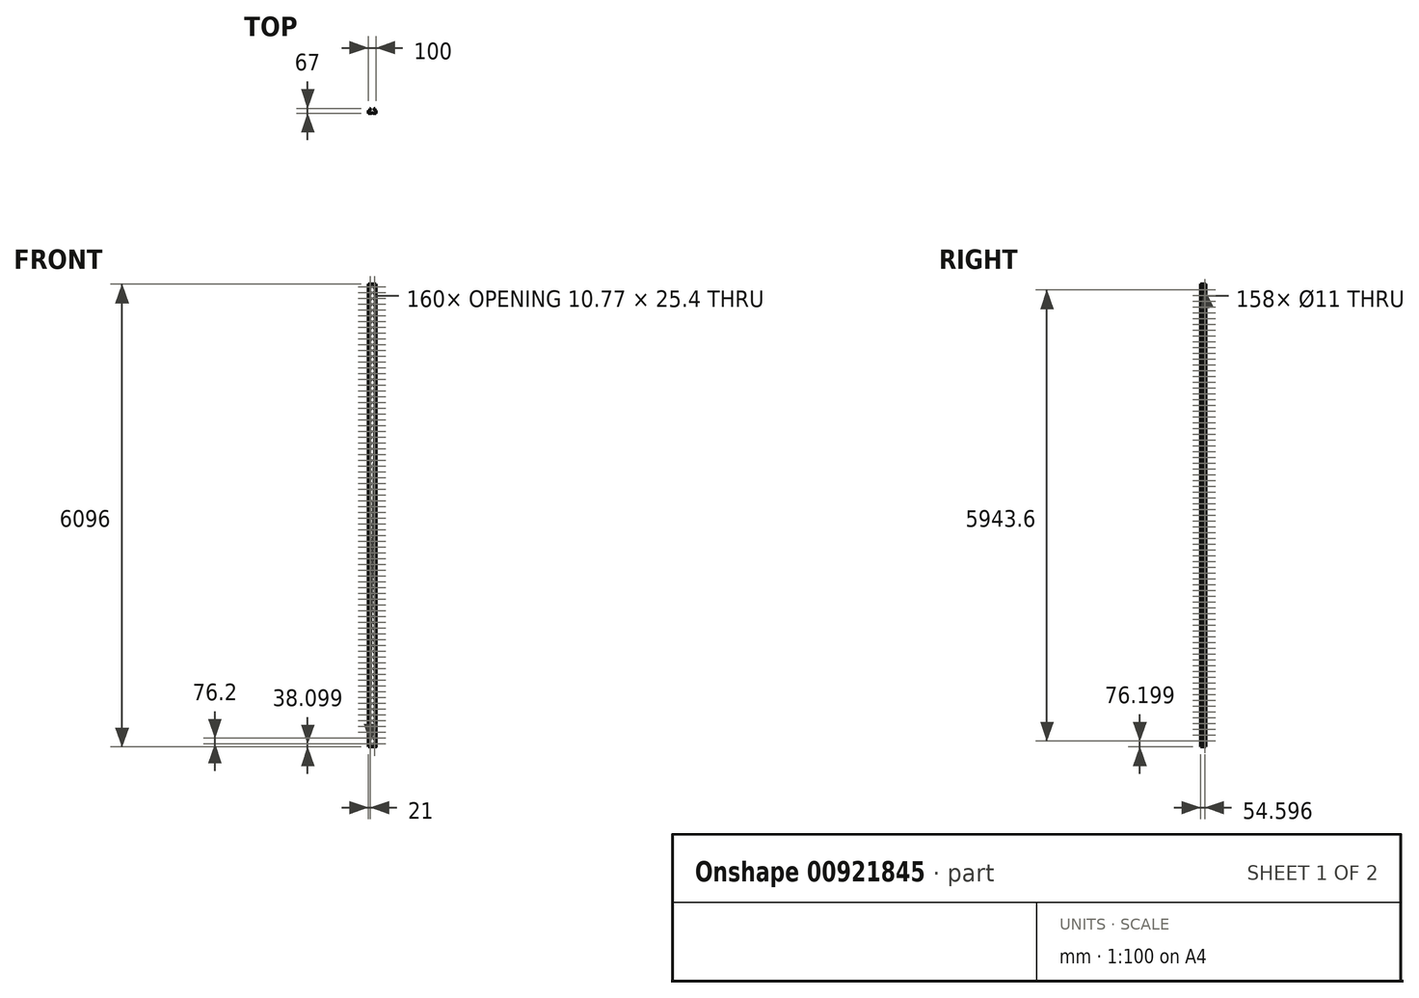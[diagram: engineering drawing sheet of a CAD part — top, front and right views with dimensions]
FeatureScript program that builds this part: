
annotation { "Feature Type Name" : "Feature", "Feature Type Description" : "" }
export const myFeature = defineFeature(function(context is Context, id is Id, definition is map)
    precondition{}
    {
        {
            var Q0;
            Q0=qCreatedBy(makeId("Top.planeOp"),FACE);
            var sketch = newSketch(context, id + "F0", { "sketchPlane" : qUnion([Q0])});
            skLineSegment(sketch, "E0", {"start": v(133.85, 104.26) * mm, "end": v(133.85, 405.9) * mm});
            skLineSegment(sketch, "E1", {"start": v(129.85, 104.03) * mm, "end": v(129.85, 405.9) * mm});
            skLineSegment(sketch, "E2", {"start": v(96.7, -203.7) * mm, "end": v(96.7, 405.9) * mm});
            skLineSegment(sketch, "E3", {"start": v(93.87, -203.7) * mm, "end": v(93.87, 405.9) * mm});
            skLineSegment(sketch, "E4", {"start": v(88.87, 103.15) * mm, "end": v(88.87, 405.9) * mm});
            skLineSegment(sketch, "E5", {"start": v(86.87, 103.6) * mm, "end": v(86.87, 405.9) * mm});
            skLineSegment(sketch, "E6", {"start": v(70.87, -203.7) * mm, "end": v(70.87, 405.9) * mm});
            skLineSegment(sketch, "E7", {"start": v(68.87, -203.7) * mm, "end": v(68.87, 405.9) * mm});
            skLineSegment(sketch, "E8", {"start": v(-161.67, -203.7) * mm, "end": v(-161.67, 405.9) * mm});
            skLineSegment(sketch, "E9", {"start": v(-165.67, -203.7) * mm, "end": v(-165.67, 405.9) * mm});
            skLineSegment(sketch, "E10", {"start": v(-122.17, -203.7) * mm, "end": v(-122.17, 405.9) * mm});
            skLineSegment(sketch, "E11", {"start": v(-125.67, -203.7) * mm, "end": v(-125.67, 405.9) * mm});
            skLineSegment(sketch, "E12", {"start": v(-109.17, -203.7) * mm, "end": v(-109.17, 405.9) * mm});
            skLineSegment(sketch, "E13", {"start": v(-105.67, -203.7) * mm, "end": v(-105.67, 405.9) * mm});
            skLineSegment(sketch, "E14", {"start": v(-69.67, -203.7) * mm, "end": v(-69.67, 405.9) * mm});
            skLineSegment(sketch, "E15", {"start": v(-65.67, -203.7) * mm, "end": v(-65.67, 405.9) * mm});
            skLineSegment(sketch, "E16", {"start": v(-165.67, -203.7) * mm, "end": v(-65.67, -203.7) * mm});
            skLineSegment(sketch, "E17", {"start": v(-140.6, 355.3) * mm, "end": v(-140.6, 357.1) * mm});
            skArc(sketch, "E18", {"start": v(-140.8, 355.1) * mm, "mid": v(-140.66, 355.17) * mm, "end": v(-140.6, 355.3) * mm});
            skLineSegment(sketch, "E19", {"start": v(-148.54, 355.1) * mm, "end": v(-140.8, 355.1) * mm});
            skArc(sketch, "E20", {"start": v(-148.74, 355.3) * mm, "mid": v(-148.68, 355.17) * mm, "end": v(-148.54, 355.1) * mm});
            skLineSegment(sketch, "E21", {"start": v(-148.74, 357.1) * mm, "end": v(-148.74, 355.3) * mm});
            skLineSegment(sketch, "E22", {"start": v(-150.06, 367.8) * mm, "end": v(-148.74, 357.1) * mm});
            skLineSegment(sketch, "E23", {"start": v(-148.74, 378.5) * mm, "end": v(-150.06, 367.8) * mm});
            skLineSegment(sketch, "E24", {"start": v(-148.74, 380.3) * mm, "end": v(-148.74, 378.5) * mm});
            skArc(sketch, "E25", {"start": v(-148.54, 380.5) * mm, "mid": v(-148.68, 380.45) * mm, "end": v(-148.74, 380.3) * mm});
            skLineSegment(sketch, "E26", {"start": v(-140.8, 380.5) * mm, "end": v(-148.54, 380.5) * mm});
            skArc(sketch, "E27", {"start": v(-140.6, 380.3) * mm, "mid": v(-140.66, 380.45) * mm, "end": v(-140.8, 380.5) * mm});
            skLineSegment(sketch, "E28", {"start": v(-140.6, 378.5) * mm, "end": v(-140.6, 380.3) * mm});
            skLineSegment(sketch, "E29", {"start": v(-139.29, 367.8) * mm, "end": v(-140.6, 378.5) * mm});
            skLineSegment(sketch, "E30", {"start": v(-140.6, 357.1) * mm, "end": v(-139.29, 367.8) * mm});
            skLineSegment(sketch, "E31", {"start": v(-140.6, 279.1) * mm, "end": v(-140.6, 280.9) * mm});
            skArc(sketch, "E32", {"start": v(-140.8, 278.9) * mm, "mid": v(-140.66, 278.97) * mm, "end": v(-140.6, 279.1) * mm});
            skLineSegment(sketch, "E33", {"start": v(-148.54, 278.9) * mm, "end": v(-140.8, 278.9) * mm});
            skArc(sketch, "E34", {"start": v(-148.74, 279.1) * mm, "mid": v(-148.68, 278.97) * mm, "end": v(-148.54, 278.9) * mm});
            skLineSegment(sketch, "E35", {"start": v(-148.74, 280.9) * mm, "end": v(-148.74, 279.1) * mm});
            skLineSegment(sketch, "E36", {"start": v(-150.06, 291.6) * mm, "end": v(-148.74, 280.9) * mm});
            skLineSegment(sketch, "E37", {"start": v(-148.74, 302.3) * mm, "end": v(-150.06, 291.6) * mm});
            skLineSegment(sketch, "E38", {"start": v(-148.74, 304.1) * mm, "end": v(-148.74, 302.3) * mm});
            skArc(sketch, "E39", {"start": v(-148.54, 304.3) * mm, "mid": v(-148.68, 304.25) * mm, "end": v(-148.74, 304.1) * mm});
            skLineSegment(sketch, "E40", {"start": v(-140.8, 304.3) * mm, "end": v(-148.54, 304.3) * mm});
            skArc(sketch, "E41", {"start": v(-140.6, 304.1) * mm, "mid": v(-140.66, 304.25) * mm, "end": v(-140.8, 304.3) * mm});
            skLineSegment(sketch, "E42", {"start": v(-140.6, 302.3) * mm, "end": v(-140.6, 304.1) * mm});
            skLineSegment(sketch, "E43", {"start": v(-139.29, 291.6) * mm, "end": v(-140.6, 302.3) * mm});
            skLineSegment(sketch, "E44", {"start": v(-140.6, 280.9) * mm, "end": v(-139.29, 291.6) * mm});
            skLineSegment(sketch, "E45", {"start": v(-140.6, 202.9) * mm, "end": v(-140.6, 204.7) * mm});
            skArc(sketch, "E46", {"start": v(-140.8, 202.7) * mm, "mid": v(-140.66, 202.77) * mm, "end": v(-140.6, 202.9) * mm});
            skLineSegment(sketch, "E47", {"start": v(-148.54, 202.7) * mm, "end": v(-140.8, 202.7) * mm});
            skArc(sketch, "E48", {"start": v(-148.74, 202.9) * mm, "mid": v(-148.68, 202.77) * mm, "end": v(-148.54, 202.7) * mm});
            skLineSegment(sketch, "E49", {"start": v(-148.74, 204.7) * mm, "end": v(-148.74, 202.9) * mm});
            skLineSegment(sketch, "E50", {"start": v(-150.06, 215.4) * mm, "end": v(-148.74, 204.7) * mm});
            skLineSegment(sketch, "E51", {"start": v(-148.74, 226.1) * mm, "end": v(-150.06, 215.4) * mm});
            skLineSegment(sketch, "E52", {"start": v(-148.74, 227.9) * mm, "end": v(-148.74, 226.1) * mm});
            skArc(sketch, "E53", {"start": v(-148.54, 228.1) * mm, "mid": v(-148.68, 228.05) * mm, "end": v(-148.74, 227.9) * mm});
            skLineSegment(sketch, "E54", {"start": v(-140.8, 228.1) * mm, "end": v(-148.54, 228.1) * mm});
            skArc(sketch, "E55", {"start": v(-140.6, 227.9) * mm, "mid": v(-140.66, 228.05) * mm, "end": v(-140.8, 228.1) * mm});
            skLineSegment(sketch, "E56", {"start": v(-140.6, 226.1) * mm, "end": v(-140.6, 227.9) * mm});
            skLineSegment(sketch, "E57", {"start": v(-139.29, 215.4) * mm, "end": v(-140.6, 226.1) * mm});
            skLineSegment(sketch, "E58", {"start": v(-140.6, 204.7) * mm, "end": v(-139.29, 215.4) * mm});
            skLineSegment(sketch, "E59", {"start": v(-140.6, 126.7) * mm, "end": v(-140.6, 128.5) * mm});
            skArc(sketch, "E60", {"start": v(-140.8, 126.5) * mm, "mid": v(-140.66, 126.57) * mm, "end": v(-140.6, 126.7) * mm});
            skLineSegment(sketch, "E61", {"start": v(-148.54, 126.5) * mm, "end": v(-140.8, 126.5) * mm});
            skArc(sketch, "E62", {"start": v(-148.74, 126.7) * mm, "mid": v(-148.68, 126.57) * mm, "end": v(-148.54, 126.5) * mm});
            skLineSegment(sketch, "E63", {"start": v(-148.74, 128.5) * mm, "end": v(-148.74, 126.7) * mm});
            skLineSegment(sketch, "E64", {"start": v(-150.06, 139.2) * mm, "end": v(-148.74, 128.5) * mm});
            skLineSegment(sketch, "E65", {"start": v(-148.74, 149.9) * mm, "end": v(-150.06, 139.2) * mm});
            skLineSegment(sketch, "E66", {"start": v(-148.74, 151.7) * mm, "end": v(-148.74, 149.9) * mm});
            skArc(sketch, "E67", {"start": v(-148.54, 151.9) * mm, "mid": v(-148.68, 151.85) * mm, "end": v(-148.74, 151.7) * mm});
            skLineSegment(sketch, "E68", {"start": v(-140.8, 151.9) * mm, "end": v(-148.54, 151.9) * mm});
            skArc(sketch, "E69", {"start": v(-140.6, 151.7) * mm, "mid": v(-140.66, 151.85) * mm, "end": v(-140.8, 151.9) * mm});
            skLineSegment(sketch, "E70", {"start": v(-140.6, 149.9) * mm, "end": v(-140.6, 151.7) * mm});
            skLineSegment(sketch, "E71", {"start": v(-139.29, 139.2) * mm, "end": v(-140.6, 149.9) * mm});
            skLineSegment(sketch, "E72", {"start": v(-140.6, 128.5) * mm, "end": v(-139.29, 139.2) * mm});
            skLineSegment(sketch, "E73", {"start": v(-140.6, 50.5) * mm, "end": v(-140.6, 52.3) * mm});
            skArc(sketch, "E74", {"start": v(-140.8, 50.3) * mm, "mid": v(-140.66, 50.37) * mm, "end": v(-140.6, 50.5) * mm});
            skLineSegment(sketch, "E75", {"start": v(-148.54, 50.3) * mm, "end": v(-140.8, 50.3) * mm});
            skArc(sketch, "E76", {"start": v(-148.74, 50.5) * mm, "mid": v(-148.68, 50.37) * mm, "end": v(-148.54, 50.3) * mm});
            skLineSegment(sketch, "E77", {"start": v(-148.74, 52.3) * mm, "end": v(-148.74, 50.5) * mm});
            skLineSegment(sketch, "E78", {"start": v(-150.06, 63) * mm, "end": v(-148.74, 52.3) * mm});
            skLineSegment(sketch, "E79", {"start": v(-148.74, 73.7) * mm, "end": v(-150.06, 63) * mm});
            skLineSegment(sketch, "E80", {"start": v(-148.74, 75.5) * mm, "end": v(-148.74, 73.7) * mm});
            skArc(sketch, "E81", {"start": v(-148.54, 75.7) * mm, "mid": v(-148.68, 75.65) * mm, "end": v(-148.74, 75.5) * mm});
            skLineSegment(sketch, "E82", {"start": v(-140.8, 75.7) * mm, "end": v(-148.54, 75.7) * mm});
            skArc(sketch, "E83", {"start": v(-140.6, 75.5) * mm, "mid": v(-140.66, 75.65) * mm, "end": v(-140.8, 75.7) * mm});
            skLineSegment(sketch, "E84", {"start": v(-140.6, 73.7) * mm, "end": v(-140.6, 75.5) * mm});
            skLineSegment(sketch, "E85", {"start": v(-139.29, 63) * mm, "end": v(-140.6, 73.7) * mm});
            skLineSegment(sketch, "E86", {"start": v(-140.6, 52.3) * mm, "end": v(-139.29, 63) * mm});
            skLineSegment(sketch, "E87", {"start": v(-140.6, -25.7) * mm, "end": v(-140.6, -23.9) * mm});
            skArc(sketch, "E88", {"start": v(-140.8, -25.9) * mm, "mid": v(-140.66, -25.83) * mm, "end": v(-140.6, -25.7) * mm});
            skLineSegment(sketch, "E89", {"start": v(-148.54, -25.9) * mm, "end": v(-140.8, -25.9) * mm});
            skArc(sketch, "E90", {"start": v(-148.74, -25.7) * mm, "mid": v(-148.68, -25.83) * mm, "end": v(-148.54, -25.9) * mm});
            skLineSegment(sketch, "E91", {"start": v(-148.74, -23.9) * mm, "end": v(-148.74, -25.7) * mm});
            skLineSegment(sketch, "E92", {"start": v(-150.06, -13.2) * mm, "end": v(-148.74, -23.9) * mm});
            skLineSegment(sketch, "E93", {"start": v(-148.74, -2.5) * mm, "end": v(-150.06, -13.2) * mm});
            skLineSegment(sketch, "E94", {"start": v(-148.74, -0.7) * mm, "end": v(-148.74, -2.5) * mm});
            skArc(sketch, "E95", {"start": v(-148.54, -0.5) * mm, "mid": v(-148.68, -0.55) * mm, "end": v(-148.74, -0.7) * mm});
            skLineSegment(sketch, "E96", {"start": v(-140.8, -0.5) * mm, "end": v(-148.54, -0.5) * mm});
            skArc(sketch, "E97", {"start": v(-140.6, -0.7) * mm, "mid": v(-140.66, -0.55) * mm, "end": v(-140.8, -0.5) * mm});
            skLineSegment(sketch, "E98", {"start": v(-140.6, -2.5) * mm, "end": v(-140.6, -0.7) * mm});
            skLineSegment(sketch, "E99", {"start": v(-139.29, -13.2) * mm, "end": v(-140.6, -2.5) * mm});
            skLineSegment(sketch, "E100", {"start": v(-140.6, -23.9) * mm, "end": v(-139.29, -13.2) * mm});
            skLineSegment(sketch, "E101", {"start": v(-140.6, -101.9) * mm, "end": v(-140.6, -100.1) * mm});
            skArc(sketch, "E102", {"start": v(-140.8, -102.1) * mm, "mid": v(-140.66, -102.03) * mm, "end": v(-140.6, -101.9) * mm});
            skLineSegment(sketch, "E103", {"start": v(-148.54, -102.1) * mm, "end": v(-140.8, -102.1) * mm});
            skArc(sketch, "E104", {"start": v(-148.74, -101.9) * mm, "mid": v(-148.68, -102.03) * mm, "end": v(-148.54, -102.1) * mm});
            skLineSegment(sketch, "E105", {"start": v(-148.74, -100.1) * mm, "end": v(-148.74, -101.9) * mm});
            skLineSegment(sketch, "E106", {"start": v(-150.06, -89.4) * mm, "end": v(-148.74, -100.1) * mm});
            skLineSegment(sketch, "E107", {"start": v(-148.74, -78.7) * mm, "end": v(-150.06, -89.4) * mm});
            skLineSegment(sketch, "E108", {"start": v(-148.74, -76.9) * mm, "end": v(-148.74, -78.7) * mm});
            skArc(sketch, "E109", {"start": v(-148.54, -76.7) * mm, "mid": v(-148.68, -76.75) * mm, "end": v(-148.74, -76.9) * mm});
            skLineSegment(sketch, "E110", {"start": v(-140.8, -76.7) * mm, "end": v(-148.54, -76.7) * mm});
            skArc(sketch, "E111", {"start": v(-140.6, -76.9) * mm, "mid": v(-140.66, -76.75) * mm, "end": v(-140.8, -76.7) * mm});
            skLineSegment(sketch, "E112", {"start": v(-140.6, -78.7) * mm, "end": v(-140.6, -76.9) * mm});
            skLineSegment(sketch, "E113", {"start": v(-139.29, -89.4) * mm, "end": v(-140.6, -78.7) * mm});
            skLineSegment(sketch, "E114", {"start": v(-140.6, -100.1) * mm, "end": v(-139.29, -89.4) * mm});
            skLineSegment(sketch, "E115", {"start": v(-140.6, -178.1) * mm, "end": v(-140.6, -176.3) * mm});
            skArc(sketch, "E116", {"start": v(-140.8, -178.3) * mm, "mid": v(-140.66, -178.23) * mm, "end": v(-140.6, -178.1) * mm});
            skLineSegment(sketch, "E117", {"start": v(-148.54, -178.3) * mm, "end": v(-140.8, -178.3) * mm});
            skArc(sketch, "E118", {"start": v(-148.74, -178.1) * mm, "mid": v(-148.68, -178.23) * mm, "end": v(-148.54, -178.3) * mm});
            skLineSegment(sketch, "E119", {"start": v(-148.74, -176.3) * mm, "end": v(-148.74, -178.1) * mm});
            skLineSegment(sketch, "E120", {"start": v(-150.06, -165.6) * mm, "end": v(-148.74, -176.3) * mm});
            skLineSegment(sketch, "E121", {"start": v(-148.74, -154.9) * mm, "end": v(-150.06, -165.6) * mm});
            skLineSegment(sketch, "E122", {"start": v(-148.74, -153.1) * mm, "end": v(-148.74, -154.9) * mm});
            skArc(sketch, "E123", {"start": v(-148.54, -152.9) * mm, "mid": v(-148.68, -152.95) * mm, "end": v(-148.74, -153.1) * mm});
            skLineSegment(sketch, "E124", {"start": v(-140.8, -152.9) * mm, "end": v(-148.54, -152.9) * mm});
            skArc(sketch, "E125", {"start": v(-140.6, -153.1) * mm, "mid": v(-140.66, -152.95) * mm, "end": v(-140.8, -152.9) * mm});
            skLineSegment(sketch, "E126", {"start": v(-140.6, -154.9) * mm, "end": v(-140.6, -153.1) * mm});
            skLineSegment(sketch, "E127", {"start": v(-139.29, -165.6) * mm, "end": v(-140.6, -154.9) * mm});
            skLineSegment(sketch, "E128", {"start": v(-140.6, -176.3) * mm, "end": v(-139.29, -165.6) * mm});
            skArc(sketch, "E129", {"start": v(-90.74, -178.1) * mm, "mid": v(-90.68, -178.23) * mm, "end": v(-90.54, -178.3) * mm});
            skLineSegment(sketch, "E130", {"start": v(-90.74, -176.3) * mm, "end": v(-90.74, -178.1) * mm});
            skLineSegment(sketch, "E131", {"start": v(-92.06, -165.6) * mm, "end": v(-90.74, -176.3) * mm});
            skLineSegment(sketch, "E132", {"start": v(-90.74, -154.9) * mm, "end": v(-92.06, -165.6) * mm});
            skLineSegment(sketch, "E133", {"start": v(-90.74, -153.1) * mm, "end": v(-90.74, -154.9) * mm});
            skArc(sketch, "E134", {"start": v(-90.54, -152.9) * mm, "mid": v(-90.68, -152.95) * mm, "end": v(-90.74, -153.1) * mm});
            skLineSegment(sketch, "E135", {"start": v(-82.8, -152.9) * mm, "end": v(-90.54, -152.9) * mm});
            skArc(sketch, "E136", {"start": v(-82.6, -153.1) * mm, "mid": v(-82.66, -152.95) * mm, "end": v(-82.8, -152.9) * mm});
            skLineSegment(sketch, "E137", {"start": v(-82.6, -154.9) * mm, "end": v(-82.6, -153.1) * mm});
            skLineSegment(sketch, "E138", {"start": v(-81.29, -165.6) * mm, "end": v(-82.6, -154.9) * mm});
            skLineSegment(sketch, "E139", {"start": v(-82.6, -176.3) * mm, "end": v(-81.29, -165.6) * mm});
            skLineSegment(sketch, "E140", {"start": v(-82.6, -178.1) * mm, "end": v(-82.6, -176.3) * mm});
            skArc(sketch, "E141", {"start": v(-82.8, -178.3) * mm, "mid": v(-82.66, -178.23) * mm, "end": v(-82.6, -178.1) * mm});
            skLineSegment(sketch, "E142", {"start": v(-90.54, -178.3) * mm, "end": v(-82.8, -178.3) * mm});
            skArc(sketch, "E143", {"start": v(-90.74, -101.9) * mm, "mid": v(-90.68, -102.03) * mm, "end": v(-90.54, -102.1) * mm});
            skLineSegment(sketch, "E144", {"start": v(-90.74, -100.1) * mm, "end": v(-90.74, -101.9) * mm});
            skLineSegment(sketch, "E145", {"start": v(-92.06, -89.4) * mm, "end": v(-90.74, -100.1) * mm});
            skLineSegment(sketch, "E146", {"start": v(-90.74, -78.7) * mm, "end": v(-92.06, -89.4) * mm});
            skLineSegment(sketch, "E147", {"start": v(-90.74, -76.9) * mm, "end": v(-90.74, -78.7) * mm});
            skArc(sketch, "E148", {"start": v(-90.54, -76.7) * mm, "mid": v(-90.68, -76.75) * mm, "end": v(-90.74, -76.9) * mm});
            skLineSegment(sketch, "E149", {"start": v(-82.8, -76.7) * mm, "end": v(-90.54, -76.7) * mm});
            skArc(sketch, "E150", {"start": v(-82.6, -76.9) * mm, "mid": v(-82.66, -76.75) * mm, "end": v(-82.8, -76.7) * mm});
            skLineSegment(sketch, "E151", {"start": v(-82.6, -78.7) * mm, "end": v(-82.6, -76.9) * mm});
            skLineSegment(sketch, "E152", {"start": v(-81.29, -89.4) * mm, "end": v(-82.6, -78.7) * mm});
            skLineSegment(sketch, "E153", {"start": v(-82.6, -100.1) * mm, "end": v(-81.29, -89.4) * mm});
            skLineSegment(sketch, "E154", {"start": v(-82.6, -101.9) * mm, "end": v(-82.6, -100.1) * mm});
            skArc(sketch, "E155", {"start": v(-82.8, -102.1) * mm, "mid": v(-82.66, -102.03) * mm, "end": v(-82.6, -101.9) * mm});
            skLineSegment(sketch, "E156", {"start": v(-90.54, -102.1) * mm, "end": v(-82.8, -102.1) * mm});
            skArc(sketch, "E157", {"start": v(-90.74, -25.7) * mm, "mid": v(-90.68, -25.83) * mm, "end": v(-90.54, -25.9) * mm});
            skLineSegment(sketch, "E158", {"start": v(-90.74, -23.9) * mm, "end": v(-90.74, -25.7) * mm});
            skLineSegment(sketch, "E159", {"start": v(-92.06, -13.2) * mm, "end": v(-90.74, -23.9) * mm});
            skLineSegment(sketch, "E160", {"start": v(-90.74, -2.5) * mm, "end": v(-92.06, -13.2) * mm});
            skLineSegment(sketch, "E161", {"start": v(-90.74, -0.7) * mm, "end": v(-90.74, -2.5) * mm});
            skArc(sketch, "E162", {"start": v(-90.54, -0.5) * mm, "mid": v(-90.68, -0.55) * mm, "end": v(-90.74, -0.7) * mm});
            skLineSegment(sketch, "E163", {"start": v(-82.8, -0.5) * mm, "end": v(-90.54, -0.5) * mm});
            skArc(sketch, "E164", {"start": v(-82.6, -0.7) * mm, "mid": v(-82.66, -0.55) * mm, "end": v(-82.8, -0.5) * mm});
            skLineSegment(sketch, "E165", {"start": v(-82.6, -2.5) * mm, "end": v(-82.6, -0.7) * mm});
            skLineSegment(sketch, "E166", {"start": v(-81.29, -13.2) * mm, "end": v(-82.6, -2.5) * mm});
            skLineSegment(sketch, "E167", {"start": v(-82.6, -23.9) * mm, "end": v(-81.29, -13.2) * mm});
            skLineSegment(sketch, "E168", {"start": v(-82.6, -25.7) * mm, "end": v(-82.6, -23.9) * mm});
            skArc(sketch, "E169", {"start": v(-82.8, -25.9) * mm, "mid": v(-82.66, -25.83) * mm, "end": v(-82.6, -25.7) * mm});
            skLineSegment(sketch, "E170", {"start": v(-90.54, -25.9) * mm, "end": v(-82.8, -25.9) * mm});
            skArc(sketch, "E171", {"start": v(-90.74, 50.5) * mm, "mid": v(-90.68, 50.37) * mm, "end": v(-90.54, 50.3) * mm});
            skLineSegment(sketch, "E172", {"start": v(-90.74, 52.3) * mm, "end": v(-90.74, 50.5) * mm});
            skLineSegment(sketch, "E173", {"start": v(-92.06, 63) * mm, "end": v(-90.74, 52.3) * mm});
            skLineSegment(sketch, "E174", {"start": v(-90.74, 73.7) * mm, "end": v(-92.06, 63) * mm});
            skLineSegment(sketch, "E175", {"start": v(-90.74, 75.5) * mm, "end": v(-90.74, 73.7) * mm});
            skArc(sketch, "E176", {"start": v(-90.54, 75.7) * mm, "mid": v(-90.68, 75.65) * mm, "end": v(-90.74, 75.5) * mm});
            skLineSegment(sketch, "E177", {"start": v(-82.8, 75.7) * mm, "end": v(-90.54, 75.7) * mm});
            skArc(sketch, "E178", {"start": v(-82.6, 75.5) * mm, "mid": v(-82.66, 75.65) * mm, "end": v(-82.8, 75.7) * mm});
            skLineSegment(sketch, "E179", {"start": v(-82.6, 73.7) * mm, "end": v(-82.6, 75.5) * mm});
            skLineSegment(sketch, "E180", {"start": v(-81.29, 63) * mm, "end": v(-82.6, 73.7) * mm});
            skLineSegment(sketch, "E181", {"start": v(-82.6, 52.3) * mm, "end": v(-81.29, 63) * mm});
            skLineSegment(sketch, "E182", {"start": v(-82.6, 50.5) * mm, "end": v(-82.6, 52.3) * mm});
            skArc(sketch, "E183", {"start": v(-82.8, 50.3) * mm, "mid": v(-82.66, 50.37) * mm, "end": v(-82.6, 50.5) * mm});
            skLineSegment(sketch, "E184", {"start": v(-90.54, 50.3) * mm, "end": v(-82.8, 50.3) * mm});
            skArc(sketch, "E185", {"start": v(-90.74, 126.7) * mm, "mid": v(-90.68, 126.57) * mm, "end": v(-90.54, 126.5) * mm});
            skLineSegment(sketch, "E186", {"start": v(-90.74, 128.5) * mm, "end": v(-90.74, 126.7) * mm});
            skLineSegment(sketch, "E187", {"start": v(-92.06, 139.2) * mm, "end": v(-90.74, 128.5) * mm});
            skLineSegment(sketch, "E188", {"start": v(-90.74, 149.9) * mm, "end": v(-92.06, 139.2) * mm});
            skLineSegment(sketch, "E189", {"start": v(-90.74, 151.7) * mm, "end": v(-90.74, 149.9) * mm});
            skArc(sketch, "E190", {"start": v(-90.54, 151.9) * mm, "mid": v(-90.68, 151.85) * mm, "end": v(-90.74, 151.7) * mm});
            skLineSegment(sketch, "E191", {"start": v(-82.8, 151.9) * mm, "end": v(-90.54, 151.9) * mm});
            skArc(sketch, "E192", {"start": v(-82.6, 151.7) * mm, "mid": v(-82.66, 151.85) * mm, "end": v(-82.8, 151.9) * mm});
            skLineSegment(sketch, "E193", {"start": v(-82.6, 149.9) * mm, "end": v(-82.6, 151.7) * mm});
            skLineSegment(sketch, "E194", {"start": v(-81.29, 139.2) * mm, "end": v(-82.6, 149.9) * mm});
            skLineSegment(sketch, "E195", {"start": v(-82.6, 128.5) * mm, "end": v(-81.29, 139.2) * mm});
            skLineSegment(sketch, "E196", {"start": v(-82.6, 126.7) * mm, "end": v(-82.6, 128.5) * mm});
            skArc(sketch, "E197", {"start": v(-82.8, 126.5) * mm, "mid": v(-82.66, 126.57) * mm, "end": v(-82.6, 126.7) * mm});
            skLineSegment(sketch, "E198", {"start": v(-90.54, 126.5) * mm, "end": v(-82.8, 126.5) * mm});
            skArc(sketch, "E199", {"start": v(-90.74, 202.9) * mm, "mid": v(-90.68, 202.77) * mm, "end": v(-90.54, 202.7) * mm});
            skLineSegment(sketch, "E200", {"start": v(-90.74, 204.7) * mm, "end": v(-90.74, 202.9) * mm});
            skLineSegment(sketch, "E201", {"start": v(-92.06, 215.4) * mm, "end": v(-90.74, 204.7) * mm});
            skLineSegment(sketch, "E202", {"start": v(-90.74, 226.1) * mm, "end": v(-92.06, 215.4) * mm});
            skLineSegment(sketch, "E203", {"start": v(-90.74, 227.9) * mm, "end": v(-90.74, 226.1) * mm});
            skArc(sketch, "E204", {"start": v(-90.54, 228.1) * mm, "mid": v(-90.68, 228.05) * mm, "end": v(-90.74, 227.9) * mm});
            skLineSegment(sketch, "E205", {"start": v(-82.8, 228.1) * mm, "end": v(-90.54, 228.1) * mm});
            skArc(sketch, "E206", {"start": v(-82.6, 227.9) * mm, "mid": v(-82.66, 228.05) * mm, "end": v(-82.8, 228.1) * mm});
            skLineSegment(sketch, "E207", {"start": v(-82.6, 226.1) * mm, "end": v(-82.6, 227.9) * mm});
            skLineSegment(sketch, "E208", {"start": v(-81.29, 215.4) * mm, "end": v(-82.6, 226.1) * mm});
            skLineSegment(sketch, "E209", {"start": v(-82.6, 204.7) * mm, "end": v(-81.29, 215.4) * mm});
            skLineSegment(sketch, "E210", {"start": v(-82.6, 202.9) * mm, "end": v(-82.6, 204.7) * mm});
            skArc(sketch, "E211", {"start": v(-82.8, 202.7) * mm, "mid": v(-82.66, 202.77) * mm, "end": v(-82.6, 202.9) * mm});
            skLineSegment(sketch, "E212", {"start": v(-90.54, 202.7) * mm, "end": v(-82.8, 202.7) * mm});
            skArc(sketch, "E213", {"start": v(-90.74, 279.1) * mm, "mid": v(-90.68, 278.97) * mm, "end": v(-90.54, 278.9) * mm});
            skLineSegment(sketch, "E214", {"start": v(-90.74, 280.9) * mm, "end": v(-90.74, 279.1) * mm});
            skLineSegment(sketch, "E215", {"start": v(-92.06, 291.6) * mm, "end": v(-90.74, 280.9) * mm});
            skLineSegment(sketch, "E216", {"start": v(-90.74, 302.3) * mm, "end": v(-92.06, 291.6) * mm});
            skLineSegment(sketch, "E217", {"start": v(-90.74, 304.1) * mm, "end": v(-90.74, 302.3) * mm});
            skArc(sketch, "E218", {"start": v(-90.54, 304.3) * mm, "mid": v(-90.68, 304.25) * mm, "end": v(-90.74, 304.1) * mm});
            skLineSegment(sketch, "E219", {"start": v(-82.8, 304.3) * mm, "end": v(-90.54, 304.3) * mm});
            skArc(sketch, "E220", {"start": v(-82.6, 304.1) * mm, "mid": v(-82.66, 304.25) * mm, "end": v(-82.8, 304.3) * mm});
            skLineSegment(sketch, "E221", {"start": v(-82.6, 302.3) * mm, "end": v(-82.6, 304.1) * mm});
            skLineSegment(sketch, "E222", {"start": v(-81.29, 291.6) * mm, "end": v(-82.6, 302.3) * mm});
            skLineSegment(sketch, "E223", {"start": v(-82.6, 280.9) * mm, "end": v(-81.29, 291.6) * mm});
            skLineSegment(sketch, "E224", {"start": v(-82.6, 279.1) * mm, "end": v(-82.6, 280.9) * mm});
            skArc(sketch, "E225", {"start": v(-82.8, 278.9) * mm, "mid": v(-82.66, 278.97) * mm, "end": v(-82.6, 279.1) * mm});
            skLineSegment(sketch, "E226", {"start": v(-90.54, 278.9) * mm, "end": v(-82.8, 278.9) * mm});
            skArc(sketch, "E227", {"start": v(-90.74, 355.3) * mm, "mid": v(-90.68, 355.17) * mm, "end": v(-90.54, 355.1) * mm});
            skLineSegment(sketch, "E228", {"start": v(-90.74, 357.1) * mm, "end": v(-90.74, 355.3) * mm});
            skLineSegment(sketch, "E229", {"start": v(-92.06, 367.8) * mm, "end": v(-90.74, 357.1) * mm});
            skLineSegment(sketch, "E230", {"start": v(-90.74, 378.5) * mm, "end": v(-92.06, 367.8) * mm});
            skLineSegment(sketch, "E231", {"start": v(-90.74, 380.3) * mm, "end": v(-90.74, 378.5) * mm});
            skArc(sketch, "E232", {"start": v(-90.54, 380.5) * mm, "mid": v(-90.68, 380.45) * mm, "end": v(-90.74, 380.3) * mm});
            skLineSegment(sketch, "E233", {"start": v(-82.8, 380.5) * mm, "end": v(-90.54, 380.5) * mm});
            skArc(sketch, "E234", {"start": v(-82.6, 380.3) * mm, "mid": v(-82.66, 380.45) * mm, "end": v(-82.8, 380.5) * mm});
            skLineSegment(sketch, "E235", {"start": v(-82.6, 378.5) * mm, "end": v(-82.6, 380.3) * mm});
            skLineSegment(sketch, "E236", {"start": v(-81.29, 367.8) * mm, "end": v(-82.6, 378.5) * mm});
            skLineSegment(sketch, "E237", {"start": v(-82.6, 357.1) * mm, "end": v(-81.29, 367.8) * mm});
            skLineSegment(sketch, "E238", {"start": v(-82.6, 355.3) * mm, "end": v(-82.6, 357.1) * mm});
            skArc(sketch, "E239", {"start": v(-82.8, 355.1) * mm, "mid": v(-82.66, 355.17) * mm, "end": v(-82.6, 355.3) * mm});
            skLineSegment(sketch, "E240", {"start": v(-90.54, 355.1) * mm, "end": v(-82.8, 355.1) * mm});
            skLineSegment(sketch, "E241", {"start": v(133.85, -203.7) * mm, "end": v(133.85, 175.06) * mm});
            skLineSegment(sketch, "E242", {"start": v(129.85, -203.7) * mm, "end": v(129.85, 174.83) * mm});
            skLineSegment(sketch, "E243", {"start": v(129.85, -203.7) * mm, "end": v(133.85, -203.7) * mm});
            skLineSegment(sketch, "E244", {"start": v(129.85, -203.7) * mm, "end": v(96.7, -203.7) * mm});
            skLineSegment(sketch, "E245", {"start": v(92.87, -203.7) * mm, "end": v(96.7, -203.7) * mm});
            skLineSegment(sketch, "E246", {"start": v(88.87, -203.7) * mm, "end": v(88.87, 173.95) * mm});
            skLineSegment(sketch, "E247", {"start": v(92.87, -203.7) * mm, "end": v(87.87, -203.7) * mm});
            skLineSegment(sketch, "E248", {"start": v(86.87, -203.7) * mm, "end": v(86.87, 174.41) * mm});
            skLineSegment(sketch, "E249", {"start": v(87.87, -203.7) * mm, "end": v(85.87, -203.7) * mm});
            skLineSegment(sketch, "E250", {"start": v(66.87, -203.7) * mm, "end": v(66.87, 405.9) * mm});
            skLineSegment(sketch, "E251", {"start": v(66.87, -203.7) * mm, "end": v(67.87, -203.7) * mm});
            skArc(sketch, "E252", {"start": v(72.35, 405.9) * mm, "mid": v(77.85, 400.4) * mm, "end": v(83.35, 405.9) * mm});
            skCircle(sketch, "E253", {"center": v(77.85, 253.5) * mm, "radius": 5.5 * mm});
            skCircle(sketch, "E254", {"center": v(77.85, 24.9) * mm, "radius": 5.5 * mm});
            skCircle(sketch, "E255", {"center": v(77.85, -127.5) * mm, "radius": 5.5 * mm});
            skArc(sketch, "E256", {"start": v(83.35, -203.7) * mm, "mid": v(77.85, -198.2) * mm, "end": v(72.35, -203.7) * mm});
            skCircle(sketch, "E257", {"center": v(77.85, -51.3) * mm, "radius": 5.5 * mm});
            skCircle(sketch, "E258", {"center": v(77.85, 101.1) * mm, "radius": 5.5 * mm});
            skCircle(sketch, "E259", {"center": v(77.85, 177.3) * mm, "radius": 5.5 * mm});
            skCircle(sketch, "E260", {"center": v(77.85, 329.7) * mm, "radius": 5.5 * mm});
            skLineSegment(sketch, "E261", {"start": v(69.87, -203.7) * mm, "end": v(72.35, -203.7) * mm});
            skLineSegment(sketch, "E262", {"start": v(83.35, -203.7) * mm, "end": v(85.87, -203.7) * mm});
            skLineSegment(sketch, "E263", {"start": v(69.87, -203.7) * mm, "end": v(67.87, -203.7) * mm});
            skLineSegment(sketch, "E264", {"start": v(-150.17, -262.95) * mm, "end": v(-150.17, -265.45) * mm});
            skArc(sketch, "E265", {"start": v(-143.67, -267.95) * mm, "mid": v(-144.4, -266.18) * mm, "end": v(-146.17, -265.45) * mm});
            skArc(sketch, "E266", {"start": v(-165.67, -324.45) * mm, "mid": v(-164.06, -328.34) * mm, "end": v(-160.17, -329.95) * mm});
            skLineSegment(sketch, "E267", {"start": v(-160.17, -329.95) * mm, "end": v(-130.39, -329.95) * mm});
            skArc(sketch, "E268", {"start": v(-130.39, -329.95) * mm, "mid": v(-128.45, -329.45) * mm, "end": v(-127, -328.07) * mm});
            skLineSegment(sketch, "E269", {"start": v(-127, -328.07) * mm, "end": v(-126.4, -327.12) * mm});
            skArc(sketch, "E270", {"start": v(-124.28, -325.95) * mm, "mid": v(-125.5, -326.26) * mm, "end": v(-126.4, -327.12) * mm});
            skLineSegment(sketch, "E271", {"start": v(-124.28, -325.95) * mm, "end": v(-107.06, -325.95) * mm});
            skLineSegment(sketch, "E272", {"start": v(-165.67, 405.9) * mm, "end": v(-65.67, 405.9) * mm});
            skLineSegment(sketch, "E273", {"start": v(66.87, 405.9) * mm, "end": v(72.35, 405.9) * mm});
            skLineSegment(sketch, "E274", {"start": v(83.35, 405.9) * mm, "end": v(133.85, 405.9) * mm});
            skLineSegment(sketch, "E275", {"start": v(-150.17, -265.45) * mm, "end": v(-146.17, -265.45) * mm});
            skLineSegment(sketch, "E276", {"start": v(-165.67, -324.45) * mm, "end": v(-165.67, -297.7) * mm});
            skArc(sketch, "E277", {"start": v(-165.67, -297.7) * mm, "mid": v(-164.71, -294.6) * mm, "end": v(-162.17, -292.58) * mm});
            skLineSegment(sketch, "E278", {"start": v(-162.17, -292.58) * mm, "end": v(-145.9, -286.02) * mm});
            skArc(sketch, "E279", {"start": v(-145.9, -286.02) * mm, "mid": v(-144.28, -284.73) * mm, "end": v(-143.67, -282.76) * mm});
            skLineSegment(sketch, "E280", {"start": v(-143.67, -282.76) * mm, "end": v(-143.67, -267.95) * mm});
            skLineSegment(sketch, "E281", {"start": v(-150.17, -262.95) * mm, "end": v(-146.17, -262.95) * mm});
            skArc(sketch, "E282", {"start": v(-141.17, -267.95) * mm, "mid": v(-142.63, -264.41) * mm, "end": v(-146.17, -262.95) * mm});
            skLineSegment(sketch, "E283", {"start": v(-163.17, -324.45) * mm, "end": v(-163.17, -297.7) * mm});
            skArc(sketch, "E284", {"start": v(-163.17, -297.7) * mm, "mid": v(-162.64, -296) * mm, "end": v(-161.25, -294.9) * mm});
            skLineSegment(sketch, "E285", {"start": v(-161.25, -294.9) * mm, "end": v(-144.97, -288.34) * mm});
            skArc(sketch, "E286", {"start": v(-144.97, -288.34) * mm, "mid": v(-142.21, -286.14) * mm, "end": v(-141.17, -282.76) * mm});
            skLineSegment(sketch, "E287", {"start": v(-141.17, -282.76) * mm, "end": v(-141.17, -267.95) * mm});
            skArc(sketch, "E288", {"start": v(-163.17, -324.45) * mm, "mid": v(-162.3, -326.57) * mm, "end": v(-160.17, -327.45) * mm});
            skLineSegment(sketch, "E289", {"start": v(-160.17, -327.45) * mm, "end": v(-130.39, -327.45) * mm});
            skArc(sketch, "E290", {"start": v(-130.39, -327.45) * mm, "mid": v(-129.66, -327.26) * mm, "end": v(-129.12, -326.74) * mm});
            skLineSegment(sketch, "E291", {"start": v(-129.12, -326.74) * mm, "end": v(-128.52, -325.8) * mm});
            skArc(sketch, "E292", {"start": v(-124.28, -323.45) * mm, "mid": v(-126.7, -324.08) * mm, "end": v(-128.52, -325.8) * mm});
            skLineSegment(sketch, "E293", {"start": v(-124.28, -323.45) * mm, "end": v(-107.06, -323.45) * mm});
            skLineSegment(sketch, "E294", {"start": v(-81.17, -262.95) * mm, "end": v(-81.17, -265.45) * mm});
            skLineSegment(sketch, "E295", {"start": v(-81.17, -265.45) * mm, "end": v(-85.17, -265.45) * mm});
            skLineSegment(sketch, "E296", {"start": v(-81.17, -262.95) * mm, "end": v(-85.17, -262.95) * mm});
            skArc(sketch, "E297", {"start": v(-85.17, -265.45) * mm, "mid": v(-86.94, -266.18) * mm, "end": v(-87.67, -267.95) * mm});
            skArc(sketch, "E298", {"start": v(-85.17, -262.95) * mm, "mid": v(-88.7, -264.41) * mm, "end": v(-90.17, -267.95) * mm});
            skLineSegment(sketch, "E299", {"start": v(-65.67, -324.45) * mm, "end": v(-65.67, -297.7) * mm});
            skArc(sketch, "E300", {"start": v(-65.67, -297.7) * mm, "mid": v(-66.63, -294.6) * mm, "end": v(-69.17, -292.58) * mm});
            skLineSegment(sketch, "E301", {"start": v(-69.17, -292.58) * mm, "end": v(-85.45, -286.02) * mm});
            skArc(sketch, "E302", {"start": v(-85.45, -286.02) * mm, "mid": v(-87.06, -284.73) * mm, "end": v(-87.67, -282.76) * mm});
            skLineSegment(sketch, "E303", {"start": v(-87.67, -282.76) * mm, "end": v(-87.67, -267.95) * mm});
            skLineSegment(sketch, "E304", {"start": v(-68.17, -324.45) * mm, "end": v(-68.17, -297.7) * mm});
            skArc(sketch, "E305", {"start": v(-68.17, -297.7) * mm, "mid": v(-68.7, -296) * mm, "end": v(-70.09, -294.9) * mm});
            skLineSegment(sketch, "E306", {"start": v(-70.09, -294.9) * mm, "end": v(-86.37, -288.34) * mm});
            skArc(sketch, "E307", {"start": v(-86.37, -288.34) * mm, "mid": v(-89.13, -286.14) * mm, "end": v(-90.17, -282.76) * mm});
            skLineSegment(sketch, "E308", {"start": v(-90.17, -282.76) * mm, "end": v(-90.17, -267.95) * mm});
            skArc(sketch, "E309", {"start": v(-71.17, -329.95) * mm, "mid": v(-67.28, -328.34) * mm, "end": v(-65.67, -324.45) * mm});
            skArc(sketch, "E310", {"start": v(-71.17, -327.45) * mm, "mid": v(-69.05, -326.57) * mm, "end": v(-68.17, -324.45) * mm});
            skLineSegment(sketch, "E311", {"start": v(-71.17, -329.95) * mm, "end": v(-100.95, -329.95) * mm});
            skLineSegment(sketch, "E312", {"start": v(-71.17, -327.45) * mm, "end": v(-100.95, -327.45) * mm});
            skArc(sketch, "E313", {"start": v(-104.35, -328.07) * mm, "mid": v(-102.9, -329.45) * mm, "end": v(-100.95, -329.95) * mm});
            skArc(sketch, "E314", {"start": v(-102.23, -326.74) * mm, "mid": v(-101.68, -327.26) * mm, "end": v(-100.95, -327.45) * mm});
            skLineSegment(sketch, "E315", {"start": v(-104.35, -328.07) * mm, "end": v(-104.94, -327.12) * mm});
            skLineSegment(sketch, "E316", {"start": v(-102.23, -326.74) * mm, "end": v(-102.82, -325.8) * mm});
            skArc(sketch, "E317", {"start": v(-104.94, -327.12) * mm, "mid": v(-105.84, -326.26) * mm, "end": v(-107.06, -325.95) * mm});
            skArc(sketch, "E318", {"start": v(-102.82, -325.8) * mm, "mid": v(-104.63, -324.08) * mm, "end": v(-107.06, -323.45) * mm});
            skSolve(sketch);
        }
        {
            var Q0;
            Q0=makeQuery(id+"F0.imprint","IMPRINT",FACE,{"disambiguationData":[TD([[makeQuery(id+"F0.imprint","IMPRINT",EDGE,{"derivedFrom":sQuery(id+"F0.wireOp",EDGE,"E264")}),1.0]])]});
            extrude(context, id + "F1", {"entities" : qUnion([Q0]), "depth" : 5257 * mm, "offsetDistance" : 25 * mm});
        }
        {
            var Q0;
            Q0=makeQuery(id+"F1.opExtrude","CAP_FACE",FACE,{"disambiguationData":[OSD([sQuery(id+"F0.wireOp",EDGE,"E264"),sQuery(id+"F0.wireOp",EDGE,"E265"),sQuery(id+"F0.wireOp",EDGE,"E266"),sQuery(id+"F0.wireOp",EDGE,"E267"),sQuery(id+"F0.wireOp",EDGE,"E268"),sQuery(id+"F0.wireOp",EDGE,"E269"),sQuery(id+"F0.wireOp",EDGE,"E270"),sQuery(id+"F0.wireOp",EDGE,"E271"),sQuery(id+"F0.wireOp",EDGE,"E275"),sQuery(id+"F0.wireOp",EDGE,"E276"),sQuery(id+"F0.wireOp",EDGE,"E277"),sQuery(id+"F0.wireOp",EDGE,"E278"),sQuery(id+"F0.wireOp",EDGE,"E279"),sQuery(id+"F0.wireOp",EDGE,"E280"),sQuery(id+"F0.wireOp",EDGE,"E281"),sQuery(id+"F0.wireOp",EDGE,"E282"),sQuery(id+"F0.wireOp",EDGE,"E283"),sQuery(id+"F0.wireOp",EDGE,"E284"),sQuery(id+"F0.wireOp",EDGE,"E285"),sQuery(id+"F0.wireOp",EDGE,"E286"),sQuery(id+"F0.wireOp",EDGE,"E287"),sQuery(id+"F0.wireOp",EDGE,"E288"),sQuery(id+"F0.wireOp",EDGE,"E289"),sQuery(id+"F0.wireOp",EDGE,"E290"),sQuery(id+"F0.wireOp",EDGE,"E291"),sQuery(id+"F0.wireOp",EDGE,"E292"),sQuery(id+"F0.wireOp",EDGE,"E293"),sQuery(id+"F0.wireOp",EDGE,"E294"),sQuery(id+"F0.wireOp",EDGE,"E295"),sQuery(id+"F0.wireOp",EDGE,"E296"),sQuery(id+"F0.wireOp",EDGE,"E297"),sQuery(id+"F0.wireOp",EDGE,"E298"),sQuery(id+"F0.wireOp",EDGE,"E299"),sQuery(id+"F0.wireOp",EDGE,"E300"),sQuery(id+"F0.wireOp",EDGE,"E301"),sQuery(id+"F0.wireOp",EDGE,"E302"),sQuery(id+"F0.wireOp",EDGE,"E303"),sQuery(id+"F0.wireOp",EDGE,"E304"),sQuery(id+"F0.wireOp",EDGE,"E305"),sQuery(id+"F0.wireOp",EDGE,"E306"),sQuery(id+"F0.wireOp",EDGE,"E307"),sQuery(id+"F0.wireOp",EDGE,"E308"),sQuery(id+"F0.wireOp",EDGE,"E309"),sQuery(id+"F0.wireOp",EDGE,"E310"),sQuery(id+"F0.wireOp",EDGE,"E311"),sQuery(id+"F0.wireOp",EDGE,"E312"),sQuery(id+"F0.wireOp",EDGE,"E313"),sQuery(id+"F0.wireOp",EDGE,"E314"),sQuery(id+"F0.wireOp",EDGE,"E315"),sQuery(id+"F0.wireOp",EDGE,"E316"),sQuery(id+"F0.wireOp",EDGE,"E317"),sQuery(id+"F0.wireOp",EDGE,"E318")])],"isStart":true});
            extrude(context, id + "F2", {"entities" : qUnion([Q0]), "operationType" : NewBodyOperationType.ADD, "depth" : 203.7 * mm, "offsetDistance" : 25 * mm});
        }
        {
            var Q0;
            Q0=makeQuery(id+"F1.opExtrude","CAP_FACE",FACE,{"disambiguationData":[OSD([sQuery(id+"F0.wireOp",EDGE,"E264"),sQuery(id+"F0.wireOp",EDGE,"E265"),sQuery(id+"F0.wireOp",EDGE,"E266"),sQuery(id+"F0.wireOp",EDGE,"E267"),sQuery(id+"F0.wireOp",EDGE,"E268"),sQuery(id+"F0.wireOp",EDGE,"E269"),sQuery(id+"F0.wireOp",EDGE,"E270"),sQuery(id+"F0.wireOp",EDGE,"E271"),sQuery(id+"F0.wireOp",EDGE,"E275"),sQuery(id+"F0.wireOp",EDGE,"E276"),sQuery(id+"F0.wireOp",EDGE,"E277"),sQuery(id+"F0.wireOp",EDGE,"E278"),sQuery(id+"F0.wireOp",EDGE,"E279"),sQuery(id+"F0.wireOp",EDGE,"E280"),sQuery(id+"F0.wireOp",EDGE,"E281"),sQuery(id+"F0.wireOp",EDGE,"E282"),sQuery(id+"F0.wireOp",EDGE,"E283"),sQuery(id+"F0.wireOp",EDGE,"E284"),sQuery(id+"F0.wireOp",EDGE,"E285"),sQuery(id+"F0.wireOp",EDGE,"E286"),sQuery(id+"F0.wireOp",EDGE,"E287"),sQuery(id+"F0.wireOp",EDGE,"E288"),sQuery(id+"F0.wireOp",EDGE,"E289"),sQuery(id+"F0.wireOp",EDGE,"E290"),sQuery(id+"F0.wireOp",EDGE,"E291"),sQuery(id+"F0.wireOp",EDGE,"E292"),sQuery(id+"F0.wireOp",EDGE,"E293"),sQuery(id+"F0.wireOp",EDGE,"E294"),sQuery(id+"F0.wireOp",EDGE,"E295"),sQuery(id+"F0.wireOp",EDGE,"E296"),sQuery(id+"F0.wireOp",EDGE,"E297"),sQuery(id+"F0.wireOp",EDGE,"E298"),sQuery(id+"F0.wireOp",EDGE,"E299"),sQuery(id+"F0.wireOp",EDGE,"E300"),sQuery(id+"F0.wireOp",EDGE,"E301"),sQuery(id+"F0.wireOp",EDGE,"E302"),sQuery(id+"F0.wireOp",EDGE,"E303"),sQuery(id+"F0.wireOp",EDGE,"E304"),sQuery(id+"F0.wireOp",EDGE,"E305"),sQuery(id+"F0.wireOp",EDGE,"E306"),sQuery(id+"F0.wireOp",EDGE,"E307"),sQuery(id+"F0.wireOp",EDGE,"E308"),sQuery(id+"F0.wireOp",EDGE,"E309"),sQuery(id+"F0.wireOp",EDGE,"E310"),sQuery(id+"F0.wireOp",EDGE,"E311"),sQuery(id+"F0.wireOp",EDGE,"E312"),sQuery(id+"F0.wireOp",EDGE,"E313"),sQuery(id+"F0.wireOp",EDGE,"E314"),sQuery(id+"F0.wireOp",EDGE,"E315"),sQuery(id+"F0.wireOp",EDGE,"E316"),sQuery(id+"F0.wireOp",EDGE,"E317"),sQuery(id+"F0.wireOp",EDGE,"E318")])],"isStart":false});
            extrude(context, id + "F3", {"entities" : qUnion([Q0]), "operationType" : NewBodyOperationType.REMOVE, "oppositeDirection" : true, "depth" : 203.7 * mm, "offsetDistance" : 25 * mm});
        }
        {
            var Q0;
            Q0=makeQuery(id+"F3.boolean.opBoolean","COPY",FACE,{"derivedFrom":makeQuery(id+"F3.opExtrude","CAP_FACE",FACE,{"disambiguationData":[OSD([sQuery(id+"F0.wireOp",EDGE,"E264"),sQuery(id+"F0.wireOp",EDGE,"E265"),sQuery(id+"F0.wireOp",EDGE,"E266"),sQuery(id+"F0.wireOp",EDGE,"E267"),sQuery(id+"F0.wireOp",EDGE,"E268"),sQuery(id+"F0.wireOp",EDGE,"E269"),sQuery(id+"F0.wireOp",EDGE,"E270"),sQuery(id+"F0.wireOp",EDGE,"E271"),sQuery(id+"F0.wireOp",EDGE,"E275"),sQuery(id+"F0.wireOp",EDGE,"E276"),sQuery(id+"F0.wireOp",EDGE,"E277"),sQuery(id+"F0.wireOp",EDGE,"E278"),sQuery(id+"F0.wireOp",EDGE,"E279"),sQuery(id+"F0.wireOp",EDGE,"E280"),sQuery(id+"F0.wireOp",EDGE,"E281"),sQuery(id+"F0.wireOp",EDGE,"E282"),sQuery(id+"F0.wireOp",EDGE,"E283"),sQuery(id+"F0.wireOp",EDGE,"E284"),sQuery(id+"F0.wireOp",EDGE,"E285"),sQuery(id+"F0.wireOp",EDGE,"E286"),sQuery(id+"F0.wireOp",EDGE,"E287"),sQuery(id+"F0.wireOp",EDGE,"E288"),sQuery(id+"F0.wireOp",EDGE,"E289"),sQuery(id+"F0.wireOp",EDGE,"E290"),sQuery(id+"F0.wireOp",EDGE,"E291"),sQuery(id+"F0.wireOp",EDGE,"E292"),sQuery(id+"F0.wireOp",EDGE,"E293"),sQuery(id+"F0.wireOp",EDGE,"E294"),sQuery(id+"F0.wireOp",EDGE,"E295"),sQuery(id+"F0.wireOp",EDGE,"E296"),sQuery(id+"F0.wireOp",EDGE,"E297"),sQuery(id+"F0.wireOp",EDGE,"E298"),sQuery(id+"F0.wireOp",EDGE,"E299"),sQuery(id+"F0.wireOp",EDGE,"E300"),sQuery(id+"F0.wireOp",EDGE,"E301"),sQuery(id+"F0.wireOp",EDGE,"E302"),sQuery(id+"F0.wireOp",EDGE,"E303"),sQuery(id+"F0.wireOp",EDGE,"E304"),sQuery(id+"F0.wireOp",EDGE,"E305"),sQuery(id+"F0.wireOp",EDGE,"E306"),sQuery(id+"F0.wireOp",EDGE,"E307"),sQuery(id+"F0.wireOp",EDGE,"E308"),sQuery(id+"F0.wireOp",EDGE,"E309"),sQuery(id+"F0.wireOp",EDGE,"E310"),sQuery(id+"F0.wireOp",EDGE,"E311"),sQuery(id+"F0.wireOp",EDGE,"E312"),sQuery(id+"F0.wireOp",EDGE,"E313"),sQuery(id+"F0.wireOp",EDGE,"E314"),sQuery(id+"F0.wireOp",EDGE,"E315"),sQuery(id+"F0.wireOp",EDGE,"E316"),sQuery(id+"F0.wireOp",EDGE,"E317"),sQuery(id+"F0.wireOp",EDGE,"E318")])],"isStart":false})});
            extrude(context, id + "F4", {"entities" : qUnion([Q0]), "operationType" : NewBodyOperationType.ADD, "depth" : 839 * mm, "offsetDistance" : 25 * mm});
        }
        {
            var Q0;
            {var subQ0=sQuery(id+"F0.wireOp",EDGE,"E267");Q0=makeQuery(id+"F4.boolean.opBoolean","MERGE",FACE,{"derivedFrom":[makeQuery(id+"F2.boolean.opBoolean","MERGE",FACE,{"derivedFrom":[makeQuery(id+"F1.opExtrude","SWEPT_FACE",FACE,{"disambiguationData":[OSD([subQ0])]}),makeQuery(id+"F2.opExtrude","SWEPT_FACE",FACE,{"disambiguationData":[OSD([subQ0])]})]}),makeQuery(id+"F4.opExtrude","SWEPT_FACE",FACE,{"disambiguationData":[OSD([subQ0])]})]});}
            var sketch = newSketch(context, id + "F5", { "sketchPlane" : qUnion([Q0])});
            skLineSegment(sketch, "E319", {"start": v(-140.6, -178.1) * mm, "end": v(-140.6, -176.3) * mm});
            skArc(sketch, "E320", {"start": v(-140.8, -178.3) * mm, "mid": v(-140.66, -178.23) * mm, "end": v(-140.6, -178.1) * mm});
            skLineSegment(sketch, "E321", {"start": v(-148.54, -178.3) * mm, "end": v(-140.8, -178.3) * mm});
            skArc(sketch, "E322", {"start": v(-148.74, -178.1) * mm, "mid": v(-148.68, -178.23) * mm, "end": v(-148.54, -178.3) * mm});
            skLineSegment(sketch, "E323", {"start": v(-148.74, -176.3) * mm, "end": v(-148.74, -178.1) * mm});
            skLineSegment(sketch, "E324", {"start": v(-150.06, -165.6) * mm, "end": v(-148.74, -176.3) * mm});
            skLineSegment(sketch, "E325", {"start": v(-148.74, -154.9) * mm, "end": v(-150.06, -165.6) * mm});
            skLineSegment(sketch, "E326", {"start": v(-148.74, -153.1) * mm, "end": v(-148.74, -154.9) * mm});
            skArc(sketch, "E327", {"start": v(-148.54, -152.9) * mm, "mid": v(-148.68, -152.95) * mm, "end": v(-148.74, -153.1) * mm});
            skLineSegment(sketch, "E328", {"start": v(-140.8, -152.9) * mm, "end": v(-148.54, -152.9) * mm});
            skArc(sketch, "E329", {"start": v(-140.6, -153.1) * mm, "mid": v(-140.66, -152.95) * mm, "end": v(-140.8, -152.9) * mm});
            skLineSegment(sketch, "E330", {"start": v(-140.6, -154.9) * mm, "end": v(-140.6, -153.1) * mm});
            skLineSegment(sketch, "E331", {"start": v(-139.29, -165.6) * mm, "end": v(-140.6, -154.9) * mm});
            skLineSegment(sketch, "E332", {"start": v(-140.6, -176.3) * mm, "end": v(-139.29, -165.6) * mm});
            skArc(sketch, "E333", {"start": v(-90.74, -178.1) * mm, "mid": v(-90.68, -178.23) * mm, "end": v(-90.54, -178.3) * mm});
            skLineSegment(sketch, "E334", {"start": v(-90.74, -176.3) * mm, "end": v(-90.74, -178.1) * mm});
            skLineSegment(sketch, "E335", {"start": v(-92.06, -165.6) * mm, "end": v(-90.74, -176.3) * mm});
            skLineSegment(sketch, "E336", {"start": v(-90.74, -154.9) * mm, "end": v(-92.06, -165.6) * mm});
            skLineSegment(sketch, "E337", {"start": v(-90.74, -153.1) * mm, "end": v(-90.74, -154.9) * mm});
            skArc(sketch, "E338", {"start": v(-90.54, -152.9) * mm, "mid": v(-90.68, -152.95) * mm, "end": v(-90.74, -153.1) * mm});
            skLineSegment(sketch, "E339", {"start": v(-82.8, -152.9) * mm, "end": v(-90.54, -152.9) * mm});
            skArc(sketch, "E340", {"start": v(-82.6, -153.1) * mm, "mid": v(-82.66, -152.95) * mm, "end": v(-82.8, -152.9) * mm});
            skLineSegment(sketch, "E341", {"start": v(-82.6, -154.9) * mm, "end": v(-82.6, -153.1) * mm});
            skLineSegment(sketch, "E342", {"start": v(-81.29, -165.6) * mm, "end": v(-82.6, -154.9) * mm});
            skLineSegment(sketch, "E343", {"start": v(-82.6, -176.3) * mm, "end": v(-81.29, -165.6) * mm});
            skLineSegment(sketch, "E344", {"start": v(-82.6, -178.1) * mm, "end": v(-82.6, -176.3) * mm});
            skArc(sketch, "E345", {"start": v(-82.8, -178.3) * mm, "mid": v(-82.66, -178.23) * mm, "end": v(-82.6, -178.1) * mm});
            skLineSegment(sketch, "E346", {"start": v(-90.54, -178.3) * mm, "end": v(-82.8, -178.3) * mm});
            skLineSegment(sketch, "E347.0.1.0", {"start": v(-92.06, -89.4) * mm, "end": v(-90.74, -100.1) * mm});
            skLineSegment(sketch, "E347.0.1.1", {"start": v(-139.29, -89.4) * mm, "end": v(-140.6, -78.7) * mm});
            skLineSegment(sketch, "E347.0.1.2", {"start": v(-81.29, -89.4) * mm, "end": v(-82.6, -78.7) * mm});
            skLineSegment(sketch, "E347.0.1.3", {"start": v(-82.6, -100.1) * mm, "end": v(-81.29, -89.4) * mm});
            skLineSegment(sketch, "E347.0.1.4", {"start": v(-140.6, -100.1) * mm, "end": v(-139.29, -89.4) * mm});
            skLineSegment(sketch, "E347.0.1.5", {"start": v(-150.06, -89.4) * mm, "end": v(-148.74, -100.1) * mm});
            skLineSegment(sketch, "E347.0.1.6", {"start": v(-90.74, -78.7) * mm, "end": v(-92.06, -89.4) * mm});
            skLineSegment(sketch, "E347.0.1.7", {"start": v(-148.74, -78.7) * mm, "end": v(-150.06, -89.4) * mm});
            skLineSegment(sketch, "E347.0.1.8", {"start": v(-90.74, -76.9) * mm, "end": v(-90.74, -78.7) * mm});
            skLineSegment(sketch, "E347.0.1.9", {"start": v(-148.54, -102.1) * mm, "end": v(-140.8, -102.1) * mm});
            skArc(sketch, "E347.0.1.10", {"start": v(-82.6, -76.9) * mm, "mid": v(-82.66, -76.75) * mm, "end": v(-82.8, -76.7) * mm});
            skLineSegment(sketch, "E347.0.1.11", {"start": v(-82.8, -76.7) * mm, "end": v(-90.54, -76.7) * mm});
            skArc(sketch, "E347.0.1.12", {"start": v(-140.8, -102.1) * mm, "mid": v(-140.66, -102.03) * mm, "end": v(-140.6, -101.9) * mm});
            skLineSegment(sketch, "E347.0.1.13", {"start": v(-82.6, -78.7) * mm, "end": v(-82.6, -76.9) * mm});
            skLineSegment(sketch, "E347.0.1.14", {"start": v(-140.6, -101.9) * mm, "end": v(-140.6, -100.1) * mm});
            skArc(sketch, "E347.0.1.15", {"start": v(-90.54, -76.7) * mm, "mid": v(-90.68, -76.75) * mm, "end": v(-90.74, -76.9) * mm});
            skLineSegment(sketch, "E347.0.1.16", {"start": v(-140.6, -78.7) * mm, "end": v(-140.6, -76.9) * mm});
            skArc(sketch, "E347.0.1.17", {"start": v(-140.6, -76.9) * mm, "mid": v(-140.66, -76.75) * mm, "end": v(-140.8, -76.7) * mm});
            skLineSegment(sketch, "E347.0.1.18", {"start": v(-140.8, -76.7) * mm, "end": v(-148.54, -76.7) * mm});
            skArc(sketch, "E347.0.1.19", {"start": v(-90.74, -101.9) * mm, "mid": v(-90.68, -102.03) * mm, "end": v(-90.54, -102.1) * mm});
            skLineSegment(sketch, "E347.0.1.20", {"start": v(-90.74, -100.1) * mm, "end": v(-90.74, -101.9) * mm});
            skLineSegment(sketch, "E347.0.1.21", {"start": v(-82.6, -101.9) * mm, "end": v(-82.6, -100.1) * mm});
            skArc(sketch, "E347.0.1.22", {"start": v(-148.54, -76.7) * mm, "mid": v(-148.68, -76.75) * mm, "end": v(-148.74, -76.9) * mm});
            skLineSegment(sketch, "E347.0.1.23", {"start": v(-148.74, -76.9) * mm, "end": v(-148.74, -78.7) * mm});
            skArc(sketch, "E347.0.1.24", {"start": v(-148.74, -101.9) * mm, "mid": v(-148.68, -102.03) * mm, "end": v(-148.54, -102.1) * mm});
            skLineSegment(sketch, "E347.0.1.25", {"start": v(-148.74, -100.1) * mm, "end": v(-148.74, -101.9) * mm});
            skLineSegment(sketch, "E347.0.1.26", {"start": v(-90.54, -102.1) * mm, "end": v(-82.8, -102.1) * mm});
            skArc(sketch, "E347.0.1.27", {"start": v(-82.8, -102.1) * mm, "mid": v(-82.66, -102.03) * mm, "end": v(-82.6, -101.9) * mm});
            skLineSegment(sketch, "E347.0.2.0", {"start": v(-92.06, -13.2) * mm, "end": v(-90.74, -23.9) * mm});
            skLineSegment(sketch, "E347.0.2.1", {"start": v(-139.29, -13.2) * mm, "end": v(-140.6, -2.5) * mm});
            skLineSegment(sketch, "E347.0.2.2", {"start": v(-81.29, -13.2) * mm, "end": v(-82.6, -2.5) * mm});
            skLineSegment(sketch, "E347.0.2.3", {"start": v(-82.6, -23.9) * mm, "end": v(-81.29, -13.2) * mm});
            skLineSegment(sketch, "E347.0.2.4", {"start": v(-140.6, -23.9) * mm, "end": v(-139.29, -13.2) * mm});
            skLineSegment(sketch, "E347.0.2.5", {"start": v(-150.06, -13.2) * mm, "end": v(-148.74, -23.9) * mm});
            skLineSegment(sketch, "E347.0.2.6", {"start": v(-90.74, -2.5) * mm, "end": v(-92.06, -13.2) * mm});
            skLineSegment(sketch, "E347.0.2.7", {"start": v(-148.74, -2.5) * mm, "end": v(-150.06, -13.2) * mm});
            skLineSegment(sketch, "E347.0.2.8", {"start": v(-90.74, -0.7) * mm, "end": v(-90.74, -2.5) * mm});
            skLineSegment(sketch, "E347.0.2.9", {"start": v(-148.54, -25.9) * mm, "end": v(-140.8, -25.9) * mm});
            skArc(sketch, "E347.0.2.10", {"start": v(-82.6, -0.7) * mm, "mid": v(-82.66, -0.55) * mm, "end": v(-82.8, -0.5) * mm});
            skLineSegment(sketch, "E347.0.2.11", {"start": v(-82.8, -0.5) * mm, "end": v(-90.54, -0.5) * mm});
            skArc(sketch, "E347.0.2.12", {"start": v(-140.8, -25.9) * mm, "mid": v(-140.66, -25.83) * mm, "end": v(-140.6, -25.7) * mm});
            skLineSegment(sketch, "E347.0.2.13", {"start": v(-82.6, -2.5) * mm, "end": v(-82.6, -0.7) * mm});
            skLineSegment(sketch, "E347.0.2.14", {"start": v(-140.6, -25.7) * mm, "end": v(-140.6, -23.9) * mm});
            skArc(sketch, "E347.0.2.15", {"start": v(-90.54, -0.5) * mm, "mid": v(-90.68, -0.55) * mm, "end": v(-90.74, -0.7) * mm});
            skLineSegment(sketch, "E347.0.2.16", {"start": v(-140.6, -2.5) * mm, "end": v(-140.6, -0.7) * mm});
            skArc(sketch, "E347.0.2.17", {"start": v(-140.6, -0.7) * mm, "mid": v(-140.66, -0.55) * mm, "end": v(-140.8, -0.5) * mm});
            skLineSegment(sketch, "E347.0.2.18", {"start": v(-140.8, -0.5) * mm, "end": v(-148.54, -0.5) * mm});
            skArc(sketch, "E347.0.2.19", {"start": v(-90.74, -25.7) * mm, "mid": v(-90.68, -25.83) * mm, "end": v(-90.54, -25.9) * mm});
            skLineSegment(sketch, "E347.0.2.20", {"start": v(-90.74, -23.9) * mm, "end": v(-90.74, -25.7) * mm});
            skLineSegment(sketch, "E347.0.2.21", {"start": v(-82.6, -25.7) * mm, "end": v(-82.6, -23.9) * mm});
            skArc(sketch, "E347.0.2.22", {"start": v(-148.54, -0.5) * mm, "mid": v(-148.68, -0.55) * mm, "end": v(-148.74, -0.7) * mm});
            skLineSegment(sketch, "E347.0.2.23", {"start": v(-148.74, -0.7) * mm, "end": v(-148.74, -2.5) * mm});
            skArc(sketch, "E347.0.2.24", {"start": v(-148.74, -25.7) * mm, "mid": v(-148.68, -25.83) * mm, "end": v(-148.54, -25.9) * mm});
            skLineSegment(sketch, "E347.0.2.25", {"start": v(-148.74, -23.9) * mm, "end": v(-148.74, -25.7) * mm});
            skLineSegment(sketch, "E347.0.2.26", {"start": v(-90.54, -25.9) * mm, "end": v(-82.8, -25.9) * mm});
            skArc(sketch, "E347.0.2.27", {"start": v(-82.8, -25.9) * mm, "mid": v(-82.66, -25.83) * mm, "end": v(-82.6, -25.7) * mm});
            skLineSegment(sketch, "E347.0.3.0", {"start": v(-92.06, 63) * mm, "end": v(-90.74, 52.3) * mm});
            skLineSegment(sketch, "E347.0.3.1", {"start": v(-139.29, 63) * mm, "end": v(-140.6, 73.7) * mm});
            skLineSegment(sketch, "E347.0.3.2", {"start": v(-81.29, 63) * mm, "end": v(-82.6, 73.7) * mm});
            skLineSegment(sketch, "E347.0.3.3", {"start": v(-82.6, 52.3) * mm, "end": v(-81.29, 63) * mm});
            skLineSegment(sketch, "E347.0.3.4", {"start": v(-140.6, 52.3) * mm, "end": v(-139.29, 63) * mm});
            skLineSegment(sketch, "E347.0.3.5", {"start": v(-150.06, 63) * mm, "end": v(-148.74, 52.3) * mm});
            skLineSegment(sketch, "E347.0.3.6", {"start": v(-90.74, 73.7) * mm, "end": v(-92.06, 63) * mm});
            skLineSegment(sketch, "E347.0.3.7", {"start": v(-148.74, 73.7) * mm, "end": v(-150.06, 63) * mm});
            skLineSegment(sketch, "E347.0.3.8", {"start": v(-90.74, 75.5) * mm, "end": v(-90.74, 73.7) * mm});
            skLineSegment(sketch, "E347.0.3.9", {"start": v(-148.54, 50.3) * mm, "end": v(-140.8, 50.3) * mm});
            skArc(sketch, "E347.0.3.10", {"start": v(-82.6, 75.5) * mm, "mid": v(-82.66, 75.65) * mm, "end": v(-82.8, 75.7) * mm});
            skLineSegment(sketch, "E347.0.3.11", {"start": v(-82.8, 75.7) * mm, "end": v(-90.54, 75.7) * mm});
            skArc(sketch, "E347.0.3.12", {"start": v(-140.8, 50.3) * mm, "mid": v(-140.66, 50.37) * mm, "end": v(-140.6, 50.5) * mm});
            skLineSegment(sketch, "E347.0.3.13", {"start": v(-82.6, 73.7) * mm, "end": v(-82.6, 75.5) * mm});
            skLineSegment(sketch, "E347.0.3.14", {"start": v(-140.6, 50.5) * mm, "end": v(-140.6, 52.3) * mm});
            skArc(sketch, "E347.0.3.15", {"start": v(-90.54, 75.7) * mm, "mid": v(-90.68, 75.65) * mm, "end": v(-90.74, 75.5) * mm});
            skLineSegment(sketch, "E347.0.3.16", {"start": v(-140.6, 73.7) * mm, "end": v(-140.6, 75.5) * mm});
            skArc(sketch, "E347.0.3.17", {"start": v(-140.6, 75.5) * mm, "mid": v(-140.66, 75.65) * mm, "end": v(-140.8, 75.7) * mm});
            skLineSegment(sketch, "E347.0.3.18", {"start": v(-140.8, 75.7) * mm, "end": v(-148.54, 75.7) * mm});
            skArc(sketch, "E347.0.3.19", {"start": v(-90.74, 50.5) * mm, "mid": v(-90.68, 50.37) * mm, "end": v(-90.54, 50.3) * mm});
            skLineSegment(sketch, "E347.0.3.20", {"start": v(-90.74, 52.3) * mm, "end": v(-90.74, 50.5) * mm});
            skLineSegment(sketch, "E347.0.3.21", {"start": v(-82.6, 50.5) * mm, "end": v(-82.6, 52.3) * mm});
            skArc(sketch, "E347.0.3.22", {"start": v(-148.54, 75.7) * mm, "mid": v(-148.68, 75.65) * mm, "end": v(-148.74, 75.5) * mm});
            skLineSegment(sketch, "E347.0.3.23", {"start": v(-148.74, 75.5) * mm, "end": v(-148.74, 73.7) * mm});
            skArc(sketch, "E347.0.3.24", {"start": v(-148.74, 50.5) * mm, "mid": v(-148.68, 50.37) * mm, "end": v(-148.54, 50.3) * mm});
            skLineSegment(sketch, "E347.0.3.25", {"start": v(-148.74, 52.3) * mm, "end": v(-148.74, 50.5) * mm});
            skLineSegment(sketch, "E347.0.3.26", {"start": v(-90.54, 50.3) * mm, "end": v(-82.8, 50.3) * mm});
            skArc(sketch, "E347.0.3.27", {"start": v(-82.8, 50.3) * mm, "mid": v(-82.66, 50.37) * mm, "end": v(-82.6, 50.5) * mm});
            skLineSegment(sketch, "E347.0.4.0", {"start": v(-92.06, 139.2) * mm, "end": v(-90.74, 128.5) * mm});
            skLineSegment(sketch, "E347.0.4.1", {"start": v(-139.29, 139.2) * mm, "end": v(-140.6, 149.9) * mm});
            skLineSegment(sketch, "E347.0.4.2", {"start": v(-81.29, 139.2) * mm, "end": v(-82.6, 149.9) * mm});
            skLineSegment(sketch, "E347.0.4.3", {"start": v(-82.6, 128.5) * mm, "end": v(-81.29, 139.2) * mm});
            skLineSegment(sketch, "E347.0.4.4", {"start": v(-140.6, 128.5) * mm, "end": v(-139.29, 139.2) * mm});
            skLineSegment(sketch, "E347.0.4.5", {"start": v(-150.06, 139.2) * mm, "end": v(-148.74, 128.5) * mm});
            skLineSegment(sketch, "E347.0.4.6", {"start": v(-90.74, 149.9) * mm, "end": v(-92.06, 139.2) * mm});
            skLineSegment(sketch, "E347.0.4.7", {"start": v(-148.74, 149.9) * mm, "end": v(-150.06, 139.2) * mm});
            skLineSegment(sketch, "E347.0.4.8", {"start": v(-90.74, 151.7) * mm, "end": v(-90.74, 149.9) * mm});
            skLineSegment(sketch, "E347.0.4.9", {"start": v(-148.54, 126.5) * mm, "end": v(-140.8, 126.5) * mm});
            skArc(sketch, "E347.0.4.10", {"start": v(-82.6, 151.7) * mm, "mid": v(-82.66, 151.85) * mm, "end": v(-82.8, 151.9) * mm});
            skLineSegment(sketch, "E347.0.4.11", {"start": v(-82.8, 151.9) * mm, "end": v(-90.54, 151.9) * mm});
            skArc(sketch, "E347.0.4.12", {"start": v(-140.8, 126.5) * mm, "mid": v(-140.66, 126.57) * mm, "end": v(-140.6, 126.7) * mm});
            skLineSegment(sketch, "E347.0.4.13", {"start": v(-82.6, 149.9) * mm, "end": v(-82.6, 151.7) * mm});
            skLineSegment(sketch, "E347.0.4.14", {"start": v(-140.6, 126.7) * mm, "end": v(-140.6, 128.5) * mm});
            skArc(sketch, "E347.0.4.15", {"start": v(-90.54, 151.9) * mm, "mid": v(-90.68, 151.85) * mm, "end": v(-90.74, 151.7) * mm});
            skLineSegment(sketch, "E347.0.4.16", {"start": v(-140.6, 149.9) * mm, "end": v(-140.6, 151.7) * mm});
            skArc(sketch, "E347.0.4.17", {"start": v(-140.6, 151.7) * mm, "mid": v(-140.66, 151.85) * mm, "end": v(-140.8, 151.9) * mm});
            skLineSegment(sketch, "E347.0.4.18", {"start": v(-140.8, 151.9) * mm, "end": v(-148.54, 151.9) * mm});
            skArc(sketch, "E347.0.4.19", {"start": v(-90.74, 126.7) * mm, "mid": v(-90.68, 126.57) * mm, "end": v(-90.54, 126.5) * mm});
            skLineSegment(sketch, "E347.0.4.20", {"start": v(-90.74, 128.5) * mm, "end": v(-90.74, 126.7) * mm});
            skLineSegment(sketch, "E347.0.4.21", {"start": v(-82.6, 126.7) * mm, "end": v(-82.6, 128.5) * mm});
            skArc(sketch, "E347.0.4.22", {"start": v(-148.54, 151.9) * mm, "mid": v(-148.68, 151.85) * mm, "end": v(-148.74, 151.7) * mm});
            skLineSegment(sketch, "E347.0.4.23", {"start": v(-148.74, 151.7) * mm, "end": v(-148.74, 149.9) * mm});
            skArc(sketch, "E347.0.4.24", {"start": v(-148.74, 126.7) * mm, "mid": v(-148.68, 126.57) * mm, "end": v(-148.54, 126.5) * mm});
            skLineSegment(sketch, "E347.0.4.25", {"start": v(-148.74, 128.5) * mm, "end": v(-148.74, 126.7) * mm});
            skLineSegment(sketch, "E347.0.4.26", {"start": v(-90.54, 126.5) * mm, "end": v(-82.8, 126.5) * mm});
            skArc(sketch, "E347.0.4.27", {"start": v(-82.8, 126.5) * mm, "mid": v(-82.66, 126.57) * mm, "end": v(-82.6, 126.7) * mm});
            skLineSegment(sketch, "E347.0.5.0", {"start": v(-92.06, 215.4) * mm, "end": v(-90.74, 204.7) * mm});
            skLineSegment(sketch, "E347.0.5.1", {"start": v(-139.29, 215.4) * mm, "end": v(-140.6, 226.1) * mm});
            skLineSegment(sketch, "E347.0.5.2", {"start": v(-81.29, 215.4) * mm, "end": v(-82.6, 226.1) * mm});
            skLineSegment(sketch, "E347.0.5.3", {"start": v(-82.6, 204.7) * mm, "end": v(-81.29, 215.4) * mm});
            skLineSegment(sketch, "E347.0.5.4", {"start": v(-140.6, 204.7) * mm, "end": v(-139.29, 215.4) * mm});
            skLineSegment(sketch, "E347.0.5.5", {"start": v(-150.06, 215.4) * mm, "end": v(-148.74, 204.7) * mm});
            skLineSegment(sketch, "E347.0.5.6", {"start": v(-90.74, 226.1) * mm, "end": v(-92.06, 215.4) * mm});
            skLineSegment(sketch, "E347.0.5.7", {"start": v(-148.74, 226.1) * mm, "end": v(-150.06, 215.4) * mm});
            skLineSegment(sketch, "E347.0.5.8", {"start": v(-90.74, 227.9) * mm, "end": v(-90.74, 226.1) * mm});
            skLineSegment(sketch, "E347.0.5.9", {"start": v(-148.54, 202.7) * mm, "end": v(-140.8, 202.7) * mm});
            skArc(sketch, "E347.0.5.10", {"start": v(-82.6, 227.9) * mm, "mid": v(-82.66, 228.05) * mm, "end": v(-82.8, 228.1) * mm});
            skLineSegment(sketch, "E347.0.5.11", {"start": v(-82.8, 228.1) * mm, "end": v(-90.54, 228.1) * mm});
            skArc(sketch, "E347.0.5.12", {"start": v(-140.8, 202.7) * mm, "mid": v(-140.66, 202.77) * mm, "end": v(-140.6, 202.9) * mm});
            skLineSegment(sketch, "E347.0.5.13", {"start": v(-82.6, 226.1) * mm, "end": v(-82.6, 227.9) * mm});
            skLineSegment(sketch, "E347.0.5.14", {"start": v(-140.6, 202.9) * mm, "end": v(-140.6, 204.7) * mm});
            skArc(sketch, "E347.0.5.15", {"start": v(-90.54, 228.1) * mm, "mid": v(-90.68, 228.05) * mm, "end": v(-90.74, 227.9) * mm});
            skLineSegment(sketch, "E347.0.5.16", {"start": v(-140.6, 226.1) * mm, "end": v(-140.6, 227.9) * mm});
            skArc(sketch, "E347.0.5.17", {"start": v(-140.6, 227.9) * mm, "mid": v(-140.66, 228.05) * mm, "end": v(-140.8, 228.1) * mm});
            skLineSegment(sketch, "E347.0.5.18", {"start": v(-140.8, 228.1) * mm, "end": v(-148.54, 228.1) * mm});
            skArc(sketch, "E347.0.5.19", {"start": v(-90.74, 202.9) * mm, "mid": v(-90.68, 202.77) * mm, "end": v(-90.54, 202.7) * mm});
            skLineSegment(sketch, "E347.0.5.20", {"start": v(-90.74, 204.7) * mm, "end": v(-90.74, 202.9) * mm});
            skLineSegment(sketch, "E347.0.5.21", {"start": v(-82.6, 202.9) * mm, "end": v(-82.6, 204.7) * mm});
            skArc(sketch, "E347.0.5.22", {"start": v(-148.54, 228.1) * mm, "mid": v(-148.68, 228.05) * mm, "end": v(-148.74, 227.9) * mm});
            skLineSegment(sketch, "E347.0.5.23", {"start": v(-148.74, 227.9) * mm, "end": v(-148.74, 226.1) * mm});
            skArc(sketch, "E347.0.5.24", {"start": v(-148.74, 202.9) * mm, "mid": v(-148.68, 202.77) * mm, "end": v(-148.54, 202.7) * mm});
            skLineSegment(sketch, "E347.0.5.25", {"start": v(-148.74, 204.7) * mm, "end": v(-148.74, 202.9) * mm});
            skLineSegment(sketch, "E347.0.5.26", {"start": v(-90.54, 202.7) * mm, "end": v(-82.8, 202.7) * mm});
            skArc(sketch, "E347.0.5.27", {"start": v(-82.8, 202.7) * mm, "mid": v(-82.66, 202.77) * mm, "end": v(-82.6, 202.9) * mm});
            skLineSegment(sketch, "E347.0.6.0", {"start": v(-92.06, 291.6) * mm, "end": v(-90.74, 280.9) * mm});
            skLineSegment(sketch, "E347.0.6.1", {"start": v(-139.29, 291.6) * mm, "end": v(-140.6, 302.3) * mm});
            skLineSegment(sketch, "E347.0.6.2", {"start": v(-81.29, 291.6) * mm, "end": v(-82.6, 302.3) * mm});
            skLineSegment(sketch, "E347.0.6.3", {"start": v(-82.6, 280.9) * mm, "end": v(-81.29, 291.6) * mm});
            skLineSegment(sketch, "E347.0.6.4", {"start": v(-140.6, 280.9) * mm, "end": v(-139.29, 291.6) * mm});
            skLineSegment(sketch, "E347.0.6.5", {"start": v(-150.06, 291.6) * mm, "end": v(-148.74, 280.9) * mm});
            skLineSegment(sketch, "E347.0.6.6", {"start": v(-90.74, 302.3) * mm, "end": v(-92.06, 291.6) * mm});
            skLineSegment(sketch, "E347.0.6.7", {"start": v(-148.74, 302.3) * mm, "end": v(-150.06, 291.6) * mm});
            skLineSegment(sketch, "E347.0.6.8", {"start": v(-90.74, 304.1) * mm, "end": v(-90.74, 302.3) * mm});
            skLineSegment(sketch, "E347.0.6.9", {"start": v(-148.54, 278.9) * mm, "end": v(-140.8, 278.9) * mm});
            skArc(sketch, "E347.0.6.10", {"start": v(-82.6, 304.1) * mm, "mid": v(-82.66, 304.25) * mm, "end": v(-82.8, 304.3) * mm});
            skLineSegment(sketch, "E347.0.6.11", {"start": v(-82.8, 304.3) * mm, "end": v(-90.54, 304.3) * mm});
            skArc(sketch, "E347.0.6.12", {"start": v(-140.8, 278.9) * mm, "mid": v(-140.66, 278.97) * mm, "end": v(-140.6, 279.1) * mm});
            skLineSegment(sketch, "E347.0.6.13", {"start": v(-82.6, 302.3) * mm, "end": v(-82.6, 304.1) * mm});
            skLineSegment(sketch, "E347.0.6.14", {"start": v(-140.6, 279.1) * mm, "end": v(-140.6, 280.9) * mm});
            skArc(sketch, "E347.0.6.15", {"start": v(-90.54, 304.3) * mm, "mid": v(-90.68, 304.25) * mm, "end": v(-90.74, 304.1) * mm});
            skLineSegment(sketch, "E347.0.6.16", {"start": v(-140.6, 302.3) * mm, "end": v(-140.6, 304.1) * mm});
            skArc(sketch, "E347.0.6.17", {"start": v(-140.6, 304.1) * mm, "mid": v(-140.66, 304.25) * mm, "end": v(-140.8, 304.3) * mm});
            skLineSegment(sketch, "E347.0.6.18", {"start": v(-140.8, 304.3) * mm, "end": v(-148.54, 304.3) * mm});
            skArc(sketch, "E347.0.6.19", {"start": v(-90.74, 279.1) * mm, "mid": v(-90.68, 278.97) * mm, "end": v(-90.54, 278.9) * mm});
            skLineSegment(sketch, "E347.0.6.20", {"start": v(-90.74, 280.9) * mm, "end": v(-90.74, 279.1) * mm});
            skLineSegment(sketch, "E347.0.6.21", {"start": v(-82.6, 279.1) * mm, "end": v(-82.6, 280.9) * mm});
            skArc(sketch, "E347.0.6.22", {"start": v(-148.54, 304.3) * mm, "mid": v(-148.68, 304.25) * mm, "end": v(-148.74, 304.1) * mm});
            skLineSegment(sketch, "E347.0.6.23", {"start": v(-148.74, 304.1) * mm, "end": v(-148.74, 302.3) * mm});
            skArc(sketch, "E347.0.6.24", {"start": v(-148.74, 279.1) * mm, "mid": v(-148.68, 278.97) * mm, "end": v(-148.54, 278.9) * mm});
            skLineSegment(sketch, "E347.0.6.25", {"start": v(-148.74, 280.9) * mm, "end": v(-148.74, 279.1) * mm});
            skLineSegment(sketch, "E347.0.6.26", {"start": v(-90.54, 278.9) * mm, "end": v(-82.8, 278.9) * mm});
            skArc(sketch, "E347.0.6.27", {"start": v(-82.8, 278.9) * mm, "mid": v(-82.66, 278.97) * mm, "end": v(-82.6, 279.1) * mm});
            skLineSegment(sketch, "E347.0.7.0", {"start": v(-92.06, 367.8) * mm, "end": v(-90.74, 357.1) * mm});
            skLineSegment(sketch, "E347.0.7.1", {"start": v(-139.29, 367.8) * mm, "end": v(-140.6, 378.5) * mm});
            skLineSegment(sketch, "E347.0.7.2", {"start": v(-81.29, 367.8) * mm, "end": v(-82.6, 378.5) * mm});
            skLineSegment(sketch, "E347.0.7.3", {"start": v(-82.6, 357.1) * mm, "end": v(-81.29, 367.8) * mm});
            skLineSegment(sketch, "E347.0.7.4", {"start": v(-140.6, 357.1) * mm, "end": v(-139.29, 367.8) * mm});
            skLineSegment(sketch, "E347.0.7.5", {"start": v(-150.06, 367.8) * mm, "end": v(-148.74, 357.1) * mm});
            skLineSegment(sketch, "E347.0.7.6", {"start": v(-90.74, 378.5) * mm, "end": v(-92.06, 367.8) * mm});
            skLineSegment(sketch, "E347.0.7.7", {"start": v(-148.74, 378.5) * mm, "end": v(-150.06, 367.8) * mm});
            skLineSegment(sketch, "E347.0.7.8", {"start": v(-90.74, 380.3) * mm, "end": v(-90.74, 378.5) * mm});
            skLineSegment(sketch, "E347.0.7.9", {"start": v(-148.54, 355.1) * mm, "end": v(-140.8, 355.1) * mm});
            skArc(sketch, "E347.0.7.10", {"start": v(-82.6, 380.3) * mm, "mid": v(-82.66, 380.45) * mm, "end": v(-82.8, 380.5) * mm});
            skLineSegment(sketch, "E347.0.7.11", {"start": v(-82.8, 380.5) * mm, "end": v(-90.54, 380.5) * mm});
            skArc(sketch, "E347.0.7.12", {"start": v(-140.8, 355.1) * mm, "mid": v(-140.66, 355.17) * mm, "end": v(-140.6, 355.3) * mm});
            skLineSegment(sketch, "E347.0.7.13", {"start": v(-82.6, 378.5) * mm, "end": v(-82.6, 380.3) * mm});
            skLineSegment(sketch, "E347.0.7.14", {"start": v(-140.6, 355.3) * mm, "end": v(-140.6, 357.1) * mm});
            skArc(sketch, "E347.0.7.15", {"start": v(-90.54, 380.5) * mm, "mid": v(-90.68, 380.45) * mm, "end": v(-90.74, 380.3) * mm});
            skLineSegment(sketch, "E347.0.7.16", {"start": v(-140.6, 378.5) * mm, "end": v(-140.6, 380.3) * mm});
            skArc(sketch, "E347.0.7.17", {"start": v(-140.6, 380.3) * mm, "mid": v(-140.66, 380.45) * mm, "end": v(-140.8, 380.5) * mm});
            skLineSegment(sketch, "E347.0.7.18", {"start": v(-140.8, 380.5) * mm, "end": v(-148.54, 380.5) * mm});
            skArc(sketch, "E347.0.7.19", {"start": v(-90.74, 355.3) * mm, "mid": v(-90.68, 355.17) * mm, "end": v(-90.54, 355.1) * mm});
            skLineSegment(sketch, "E347.0.7.20", {"start": v(-90.74, 357.1) * mm, "end": v(-90.74, 355.3) * mm});
            skLineSegment(sketch, "E347.0.7.21", {"start": v(-82.6, 355.3) * mm, "end": v(-82.6, 357.1) * mm});
            skArc(sketch, "E347.0.7.22", {"start": v(-148.54, 380.5) * mm, "mid": v(-148.68, 380.45) * mm, "end": v(-148.74, 380.3) * mm});
            skLineSegment(sketch, "E347.0.7.23", {"start": v(-148.74, 380.3) * mm, "end": v(-148.74, 378.5) * mm});
            skArc(sketch, "E347.0.7.24", {"start": v(-148.74, 355.3) * mm, "mid": v(-148.68, 355.17) * mm, "end": v(-148.54, 355.1) * mm});
            skLineSegment(sketch, "E347.0.7.25", {"start": v(-148.74, 357.1) * mm, "end": v(-148.74, 355.3) * mm});
            skLineSegment(sketch, "E347.0.7.26", {"start": v(-90.54, 355.1) * mm, "end": v(-82.8, 355.1) * mm});
            skArc(sketch, "E347.0.7.27", {"start": v(-82.8, 355.1) * mm, "mid": v(-82.66, 355.17) * mm, "end": v(-82.6, 355.3) * mm});
            skLineSegment(sketch, "E347.0.8.0", {"start": v(-92.06, 444) * mm, "end": v(-90.74, 433.3) * mm});
            skLineSegment(sketch, "E347.0.8.1", {"start": v(-139.29, 444) * mm, "end": v(-140.6, 454.7) * mm});
            skLineSegment(sketch, "E347.0.8.2", {"start": v(-81.29, 444) * mm, "end": v(-82.6, 454.7) * mm});
            skLineSegment(sketch, "E347.0.8.3", {"start": v(-82.6, 433.3) * mm, "end": v(-81.29, 444) * mm});
            skLineSegment(sketch, "E347.0.8.4", {"start": v(-140.6, 433.3) * mm, "end": v(-139.29, 444) * mm});
            skLineSegment(sketch, "E347.0.8.5", {"start": v(-150.06, 444) * mm, "end": v(-148.74, 433.3) * mm});
            skLineSegment(sketch, "E347.0.8.6", {"start": v(-90.74, 454.7) * mm, "end": v(-92.06, 444) * mm});
            skLineSegment(sketch, "E347.0.8.7", {"start": v(-148.74, 454.7) * mm, "end": v(-150.06, 444) * mm});
            skLineSegment(sketch, "E347.0.8.8", {"start": v(-90.74, 456.5) * mm, "end": v(-90.74, 454.7) * mm});
            skLineSegment(sketch, "E347.0.8.9", {"start": v(-148.54, 431.3) * mm, "end": v(-140.8, 431.3) * mm});
            skArc(sketch, "E347.0.8.10", {"start": v(-82.6, 456.5) * mm, "mid": v(-82.66, 456.65) * mm, "end": v(-82.8, 456.7) * mm});
            skLineSegment(sketch, "E347.0.8.11", {"start": v(-82.8, 456.7) * mm, "end": v(-90.54, 456.7) * mm});
            skArc(sketch, "E347.0.8.12", {"start": v(-140.8, 431.3) * mm, "mid": v(-140.66, 431.37) * mm, "end": v(-140.6, 431.5) * mm});
            skLineSegment(sketch, "E347.0.8.13", {"start": v(-82.6, 454.7) * mm, "end": v(-82.6, 456.5) * mm});
            skLineSegment(sketch, "E347.0.8.14", {"start": v(-140.6, 431.5) * mm, "end": v(-140.6, 433.3) * mm});
            skArc(sketch, "E347.0.8.15", {"start": v(-90.54, 456.7) * mm, "mid": v(-90.68, 456.65) * mm, "end": v(-90.74, 456.5) * mm});
            skLineSegment(sketch, "E347.0.8.16", {"start": v(-140.6, 454.7) * mm, "end": v(-140.6, 456.5) * mm});
            skArc(sketch, "E347.0.8.17", {"start": v(-140.6, 456.5) * mm, "mid": v(-140.66, 456.65) * mm, "end": v(-140.8, 456.7) * mm});
            skLineSegment(sketch, "E347.0.8.18", {"start": v(-140.8, 456.7) * mm, "end": v(-148.54, 456.7) * mm});
            skArc(sketch, "E347.0.8.19", {"start": v(-90.74, 431.5) * mm, "mid": v(-90.68, 431.37) * mm, "end": v(-90.54, 431.3) * mm});
            skLineSegment(sketch, "E347.0.8.20", {"start": v(-90.74, 433.3) * mm, "end": v(-90.74, 431.5) * mm});
            skLineSegment(sketch, "E347.0.8.21", {"start": v(-82.6, 431.5) * mm, "end": v(-82.6, 433.3) * mm});
            skArc(sketch, "E347.0.8.22", {"start": v(-148.54, 456.7) * mm, "mid": v(-148.68, 456.65) * mm, "end": v(-148.74, 456.5) * mm});
            skLineSegment(sketch, "E347.0.8.23", {"start": v(-148.74, 456.5) * mm, "end": v(-148.74, 454.7) * mm});
            skArc(sketch, "E347.0.8.24", {"start": v(-148.74, 431.5) * mm, "mid": v(-148.68, 431.37) * mm, "end": v(-148.54, 431.3) * mm});
            skLineSegment(sketch, "E347.0.8.25", {"start": v(-148.74, 433.3) * mm, "end": v(-148.74, 431.5) * mm});
            skLineSegment(sketch, "E347.0.8.26", {"start": v(-90.54, 431.3) * mm, "end": v(-82.8, 431.3) * mm});
            skArc(sketch, "E347.0.8.27", {"start": v(-82.8, 431.3) * mm, "mid": v(-82.66, 431.37) * mm, "end": v(-82.6, 431.5) * mm});
            skLineSegment(sketch, "E347.0.9.0", {"start": v(-92.06, 520.2) * mm, "end": v(-90.74, 509.5) * mm});
            skLineSegment(sketch, "E347.0.9.1", {"start": v(-139.29, 520.2) * mm, "end": v(-140.6, 530.9) * mm});
            skLineSegment(sketch, "E347.0.9.2", {"start": v(-81.29, 520.2) * mm, "end": v(-82.6, 530.9) * mm});
            skLineSegment(sketch, "E347.0.9.3", {"start": v(-82.6, 509.5) * mm, "end": v(-81.29, 520.2) * mm});
            skLineSegment(sketch, "E347.0.9.4", {"start": v(-140.6, 509.5) * mm, "end": v(-139.29, 520.2) * mm});
            skLineSegment(sketch, "E347.0.9.5", {"start": v(-150.06, 520.2) * mm, "end": v(-148.74, 509.5) * mm});
            skLineSegment(sketch, "E347.0.9.6", {"start": v(-90.74, 530.9) * mm, "end": v(-92.06, 520.2) * mm});
            skLineSegment(sketch, "E347.0.9.7", {"start": v(-148.74, 530.9) * mm, "end": v(-150.06, 520.2) * mm});
            skLineSegment(sketch, "E347.0.9.8", {"start": v(-90.74, 532.7) * mm, "end": v(-90.74, 530.9) * mm});
            skLineSegment(sketch, "E347.0.9.9", {"start": v(-148.54, 507.5) * mm, "end": v(-140.8, 507.5) * mm});
            skArc(sketch, "E347.0.9.10", {"start": v(-82.6, 532.7) * mm, "mid": v(-82.66, 532.85) * mm, "end": v(-82.8, 532.9) * mm});
            skLineSegment(sketch, "E347.0.9.11", {"start": v(-82.8, 532.9) * mm, "end": v(-90.54, 532.9) * mm});
            skArc(sketch, "E347.0.9.12", {"start": v(-140.8, 507.5) * mm, "mid": v(-140.66, 507.57) * mm, "end": v(-140.6, 507.7) * mm});
            skLineSegment(sketch, "E347.0.9.13", {"start": v(-82.6, 530.9) * mm, "end": v(-82.6, 532.7) * mm});
            skLineSegment(sketch, "E347.0.9.14", {"start": v(-140.6, 507.7) * mm, "end": v(-140.6, 509.5) * mm});
            skArc(sketch, "E347.0.9.15", {"start": v(-90.54, 532.9) * mm, "mid": v(-90.68, 532.85) * mm, "end": v(-90.74, 532.7) * mm});
            skLineSegment(sketch, "E347.0.9.16", {"start": v(-140.6, 530.9) * mm, "end": v(-140.6, 532.7) * mm});
            skArc(sketch, "E347.0.9.17", {"start": v(-140.6, 532.7) * mm, "mid": v(-140.66, 532.85) * mm, "end": v(-140.8, 532.9) * mm});
            skLineSegment(sketch, "E347.0.9.18", {"start": v(-140.8, 532.9) * mm, "end": v(-148.54, 532.9) * mm});
            skArc(sketch, "E347.0.9.19", {"start": v(-90.74, 507.7) * mm, "mid": v(-90.68, 507.57) * mm, "end": v(-90.54, 507.5) * mm});
            skLineSegment(sketch, "E347.0.9.20", {"start": v(-90.74, 509.5) * mm, "end": v(-90.74, 507.7) * mm});
            skLineSegment(sketch, "E347.0.9.21", {"start": v(-82.6, 507.7) * mm, "end": v(-82.6, 509.5) * mm});
            skArc(sketch, "E347.0.9.22", {"start": v(-148.54, 532.9) * mm, "mid": v(-148.68, 532.85) * mm, "end": v(-148.74, 532.7) * mm});
            skLineSegment(sketch, "E347.0.9.23", {"start": v(-148.74, 532.7) * mm, "end": v(-148.74, 530.9) * mm});
            skArc(sketch, "E347.0.9.24", {"start": v(-148.74, 507.7) * mm, "mid": v(-148.68, 507.57) * mm, "end": v(-148.54, 507.5) * mm});
            skLineSegment(sketch, "E347.0.9.25", {"start": v(-148.74, 509.5) * mm, "end": v(-148.74, 507.7) * mm});
            skLineSegment(sketch, "E347.0.9.26", {"start": v(-90.54, 507.5) * mm, "end": v(-82.8, 507.5) * mm});
            skArc(sketch, "E347.0.9.27", {"start": v(-82.8, 507.5) * mm, "mid": v(-82.66, 507.57) * mm, "end": v(-82.6, 507.7) * mm});
            skLineSegment(sketch, "E347.0.10.0", {"start": v(-92.06, 596.4) * mm, "end": v(-90.74, 585.7) * mm});
            skLineSegment(sketch, "E347.0.10.1", {"start": v(-139.29, 596.4) * mm, "end": v(-140.6, 607.1) * mm});
            skLineSegment(sketch, "E347.0.10.2", {"start": v(-81.29, 596.4) * mm, "end": v(-82.6, 607.1) * mm});
            skLineSegment(sketch, "E347.0.10.3", {"start": v(-82.6, 585.7) * mm, "end": v(-81.29, 596.4) * mm});
            skLineSegment(sketch, "E347.0.10.4", {"start": v(-140.6, 585.7) * mm, "end": v(-139.29, 596.4) * mm});
            skLineSegment(sketch, "E347.0.10.5", {"start": v(-150.06, 596.4) * mm, "end": v(-148.74, 585.7) * mm});
            skLineSegment(sketch, "E347.0.10.6", {"start": v(-90.74, 607.1) * mm, "end": v(-92.06, 596.4) * mm});
            skLineSegment(sketch, "E347.0.10.7", {"start": v(-148.74, 607.1) * mm, "end": v(-150.06, 596.4) * mm});
            skLineSegment(sketch, "E347.0.10.8", {"start": v(-90.74, 608.9) * mm, "end": v(-90.74, 607.1) * mm});
            skLineSegment(sketch, "E347.0.10.9", {"start": v(-148.54, 583.7) * mm, "end": v(-140.8, 583.7) * mm});
            skArc(sketch, "E347.0.10.10", {"start": v(-82.6, 608.9) * mm, "mid": v(-82.66, 609.05) * mm, "end": v(-82.8, 609.1) * mm});
            skLineSegment(sketch, "E347.0.10.11", {"start": v(-82.8, 609.1) * mm, "end": v(-90.54, 609.1) * mm});
            skArc(sketch, "E347.0.10.12", {"start": v(-140.8, 583.7) * mm, "mid": v(-140.66, 583.77) * mm, "end": v(-140.6, 583.9) * mm});
            skLineSegment(sketch, "E347.0.10.13", {"start": v(-82.6, 607.1) * mm, "end": v(-82.6, 608.9) * mm});
            skLineSegment(sketch, "E347.0.10.14", {"start": v(-140.6, 583.9) * mm, "end": v(-140.6, 585.7) * mm});
            skArc(sketch, "E347.0.10.15", {"start": v(-90.54, 609.1) * mm, "mid": v(-90.68, 609.05) * mm, "end": v(-90.74, 608.9) * mm});
            skLineSegment(sketch, "E347.0.10.16", {"start": v(-140.6, 607.1) * mm, "end": v(-140.6, 608.9) * mm});
            skArc(sketch, "E347.0.10.17", {"start": v(-140.6, 608.9) * mm, "mid": v(-140.66, 609.05) * mm, "end": v(-140.8, 609.1) * mm});
            skLineSegment(sketch, "E347.0.10.18", {"start": v(-140.8, 609.1) * mm, "end": v(-148.54, 609.1) * mm});
            skArc(sketch, "E347.0.10.19", {"start": v(-90.74, 583.9) * mm, "mid": v(-90.68, 583.77) * mm, "end": v(-90.54, 583.7) * mm});
            skLineSegment(sketch, "E347.0.10.20", {"start": v(-90.74, 585.7) * mm, "end": v(-90.74, 583.9) * mm});
            skLineSegment(sketch, "E347.0.10.21", {"start": v(-82.6, 583.9) * mm, "end": v(-82.6, 585.7) * mm});
            skArc(sketch, "E347.0.10.22", {"start": v(-148.54, 609.1) * mm, "mid": v(-148.68, 609.05) * mm, "end": v(-148.74, 608.9) * mm});
            skLineSegment(sketch, "E347.0.10.23", {"start": v(-148.74, 608.9) * mm, "end": v(-148.74, 607.1) * mm});
            skArc(sketch, "E347.0.10.24", {"start": v(-148.74, 583.9) * mm, "mid": v(-148.68, 583.77) * mm, "end": v(-148.54, 583.7) * mm});
            skLineSegment(sketch, "E347.0.10.25", {"start": v(-148.74, 585.7) * mm, "end": v(-148.74, 583.9) * mm});
            skLineSegment(sketch, "E347.0.10.26", {"start": v(-90.54, 583.7) * mm, "end": v(-82.8, 583.7) * mm});
            skArc(sketch, "E347.0.10.27", {"start": v(-82.8, 583.7) * mm, "mid": v(-82.66, 583.77) * mm, "end": v(-82.6, 583.9) * mm});
            skLineSegment(sketch, "E347.0.11.0", {"start": v(-92.06, 672.6) * mm, "end": v(-90.74, 661.9) * mm});
            skLineSegment(sketch, "E347.0.11.1", {"start": v(-139.29, 672.6) * mm, "end": v(-140.6, 683.3) * mm});
            skLineSegment(sketch, "E347.0.11.2", {"start": v(-81.29, 672.6) * mm, "end": v(-82.6, 683.3) * mm});
            skLineSegment(sketch, "E347.0.11.3", {"start": v(-82.6, 661.9) * mm, "end": v(-81.29, 672.6) * mm});
            skLineSegment(sketch, "E347.0.11.4", {"start": v(-140.6, 661.9) * mm, "end": v(-139.29, 672.6) * mm});
            skLineSegment(sketch, "E347.0.11.5", {"start": v(-150.06, 672.6) * mm, "end": v(-148.74, 661.9) * mm});
            skLineSegment(sketch, "E347.0.11.6", {"start": v(-90.74, 683.3) * mm, "end": v(-92.06, 672.6) * mm});
            skLineSegment(sketch, "E347.0.11.7", {"start": v(-148.74, 683.3) * mm, "end": v(-150.06, 672.6) * mm});
            skLineSegment(sketch, "E347.0.11.8", {"start": v(-90.74, 685.1) * mm, "end": v(-90.74, 683.3) * mm});
            skLineSegment(sketch, "E347.0.11.9", {"start": v(-148.54, 659.9) * mm, "end": v(-140.8, 659.9) * mm});
            skArc(sketch, "E347.0.11.10", {"start": v(-82.6, 685.1) * mm, "mid": v(-82.66, 685.25) * mm, "end": v(-82.8, 685.3) * mm});
            skLineSegment(sketch, "E347.0.11.11", {"start": v(-82.8, 685.3) * mm, "end": v(-90.54, 685.3) * mm});
            skArc(sketch, "E347.0.11.12", {"start": v(-140.8, 659.9) * mm, "mid": v(-140.66, 659.97) * mm, "end": v(-140.6, 660.1) * mm});
            skLineSegment(sketch, "E347.0.11.13", {"start": v(-82.6, 683.3) * mm, "end": v(-82.6, 685.1) * mm});
            skLineSegment(sketch, "E347.0.11.14", {"start": v(-140.6, 660.1) * mm, "end": v(-140.6, 661.9) * mm});
            skArc(sketch, "E347.0.11.15", {"start": v(-90.54, 685.3) * mm, "mid": v(-90.68, 685.25) * mm, "end": v(-90.74, 685.1) * mm});
            skLineSegment(sketch, "E347.0.11.16", {"start": v(-140.6, 683.3) * mm, "end": v(-140.6, 685.1) * mm});
            skArc(sketch, "E347.0.11.17", {"start": v(-140.6, 685.1) * mm, "mid": v(-140.66, 685.25) * mm, "end": v(-140.8, 685.3) * mm});
            skLineSegment(sketch, "E347.0.11.18", {"start": v(-140.8, 685.3) * mm, "end": v(-148.54, 685.3) * mm});
            skArc(sketch, "E347.0.11.19", {"start": v(-90.74, 660.1) * mm, "mid": v(-90.68, 659.97) * mm, "end": v(-90.54, 659.9) * mm});
            skLineSegment(sketch, "E347.0.11.20", {"start": v(-90.74, 661.9) * mm, "end": v(-90.74, 660.1) * mm});
            skLineSegment(sketch, "E347.0.11.21", {"start": v(-82.6, 660.1) * mm, "end": v(-82.6, 661.9) * mm});
            skArc(sketch, "E347.0.11.22", {"start": v(-148.54, 685.3) * mm, "mid": v(-148.68, 685.25) * mm, "end": v(-148.74, 685.1) * mm});
            skLineSegment(sketch, "E347.0.11.23", {"start": v(-148.74, 685.1) * mm, "end": v(-148.74, 683.3) * mm});
            skArc(sketch, "E347.0.11.24", {"start": v(-148.74, 660.1) * mm, "mid": v(-148.68, 659.97) * mm, "end": v(-148.54, 659.9) * mm});
            skLineSegment(sketch, "E347.0.11.25", {"start": v(-148.74, 661.9) * mm, "end": v(-148.74, 660.1) * mm});
            skLineSegment(sketch, "E347.0.11.26", {"start": v(-90.54, 659.9) * mm, "end": v(-82.8, 659.9) * mm});
            skArc(sketch, "E347.0.11.27", {"start": v(-82.8, 659.9) * mm, "mid": v(-82.66, 659.97) * mm, "end": v(-82.6, 660.1) * mm});
            skLineSegment(sketch, "E347.0.12.0", {"start": v(-92.06, 748.8) * mm, "end": v(-90.74, 738.1) * mm});
            skLineSegment(sketch, "E347.0.12.1", {"start": v(-139.29, 748.8) * mm, "end": v(-140.6, 759.5) * mm});
            skLineSegment(sketch, "E347.0.12.2", {"start": v(-81.29, 748.8) * mm, "end": v(-82.6, 759.5) * mm});
            skLineSegment(sketch, "E347.0.12.3", {"start": v(-82.6, 738.1) * mm, "end": v(-81.29, 748.8) * mm});
            skLineSegment(sketch, "E347.0.12.4", {"start": v(-140.6, 738.1) * mm, "end": v(-139.29, 748.8) * mm});
            skLineSegment(sketch, "E347.0.12.5", {"start": v(-150.06, 748.8) * mm, "end": v(-148.74, 738.1) * mm});
            skLineSegment(sketch, "E347.0.12.6", {"start": v(-90.74, 759.5) * mm, "end": v(-92.06, 748.8) * mm});
            skLineSegment(sketch, "E347.0.12.7", {"start": v(-148.74, 759.5) * mm, "end": v(-150.06, 748.8) * mm});
            skLineSegment(sketch, "E347.0.12.8", {"start": v(-90.74, 761.3) * mm, "end": v(-90.74, 759.5) * mm});
            skLineSegment(sketch, "E347.0.12.9", {"start": v(-148.54, 736.1) * mm, "end": v(-140.8, 736.1) * mm});
            skArc(sketch, "E347.0.12.10", {"start": v(-82.6, 761.3) * mm, "mid": v(-82.66, 761.45) * mm, "end": v(-82.8, 761.5) * mm});
            skLineSegment(sketch, "E347.0.12.11", {"start": v(-82.8, 761.5) * mm, "end": v(-90.54, 761.5) * mm});
            skArc(sketch, "E347.0.12.12", {"start": v(-140.8, 736.1) * mm, "mid": v(-140.66, 736.17) * mm, "end": v(-140.6, 736.3) * mm});
            skLineSegment(sketch, "E347.0.12.13", {"start": v(-82.6, 759.5) * mm, "end": v(-82.6, 761.3) * mm});
            skLineSegment(sketch, "E347.0.12.14", {"start": v(-140.6, 736.3) * mm, "end": v(-140.6, 738.1) * mm});
            skArc(sketch, "E347.0.12.15", {"start": v(-90.54, 761.5) * mm, "mid": v(-90.68, 761.45) * mm, "end": v(-90.74, 761.3) * mm});
            skLineSegment(sketch, "E347.0.12.16", {"start": v(-140.6, 759.5) * mm, "end": v(-140.6, 761.3) * mm});
            skArc(sketch, "E347.0.12.17", {"start": v(-140.6, 761.3) * mm, "mid": v(-140.66, 761.45) * mm, "end": v(-140.8, 761.5) * mm});
            skLineSegment(sketch, "E347.0.12.18", {"start": v(-140.8, 761.5) * mm, "end": v(-148.54, 761.5) * mm});
            skArc(sketch, "E347.0.12.19", {"start": v(-90.74, 736.3) * mm, "mid": v(-90.68, 736.17) * mm, "end": v(-90.54, 736.1) * mm});
            skLineSegment(sketch, "E347.0.12.20", {"start": v(-90.74, 738.1) * mm, "end": v(-90.74, 736.3) * mm});
            skLineSegment(sketch, "E347.0.12.21", {"start": v(-82.6, 736.3) * mm, "end": v(-82.6, 738.1) * mm});
            skArc(sketch, "E347.0.12.22", {"start": v(-148.54, 761.5) * mm, "mid": v(-148.68, 761.45) * mm, "end": v(-148.74, 761.3) * mm});
            skLineSegment(sketch, "E347.0.12.23", {"start": v(-148.74, 761.3) * mm, "end": v(-148.74, 759.5) * mm});
            skArc(sketch, "E347.0.12.24", {"start": v(-148.74, 736.3) * mm, "mid": v(-148.68, 736.17) * mm, "end": v(-148.54, 736.1) * mm});
            skLineSegment(sketch, "E347.0.12.25", {"start": v(-148.74, 738.1) * mm, "end": v(-148.74, 736.3) * mm});
            skLineSegment(sketch, "E347.0.12.26", {"start": v(-90.54, 736.1) * mm, "end": v(-82.8, 736.1) * mm});
            skArc(sketch, "E347.0.12.27", {"start": v(-82.8, 736.1) * mm, "mid": v(-82.66, 736.17) * mm, "end": v(-82.6, 736.3) * mm});
            skLineSegment(sketch, "E347.0.13.0", {"start": v(-92.06, 825) * mm, "end": v(-90.74, 814.3) * mm});
            skLineSegment(sketch, "E347.0.13.1", {"start": v(-139.29, 825) * mm, "end": v(-140.6, 835.7) * mm});
            skLineSegment(sketch, "E347.0.13.2", {"start": v(-81.29, 825) * mm, "end": v(-82.6, 835.7) * mm});
            skLineSegment(sketch, "E347.0.13.3", {"start": v(-82.6, 814.3) * mm, "end": v(-81.29, 825) * mm});
            skLineSegment(sketch, "E347.0.13.4", {"start": v(-140.6, 814.3) * mm, "end": v(-139.29, 825) * mm});
            skLineSegment(sketch, "E347.0.13.5", {"start": v(-150.06, 825) * mm, "end": v(-148.74, 814.3) * mm});
            skLineSegment(sketch, "E347.0.13.6", {"start": v(-90.74, 835.7) * mm, "end": v(-92.06, 825) * mm});
            skLineSegment(sketch, "E347.0.13.7", {"start": v(-148.74, 835.7) * mm, "end": v(-150.06, 825) * mm});
            skLineSegment(sketch, "E347.0.13.8", {"start": v(-90.74, 837.5) * mm, "end": v(-90.74, 835.7) * mm});
            skLineSegment(sketch, "E347.0.13.9", {"start": v(-148.54, 812.3) * mm, "end": v(-140.8, 812.3) * mm});
            skArc(sketch, "E347.0.13.10", {"start": v(-82.6, 837.5) * mm, "mid": v(-82.66, 837.65) * mm, "end": v(-82.8, 837.7) * mm});
            skLineSegment(sketch, "E347.0.13.11", {"start": v(-82.8, 837.7) * mm, "end": v(-90.54, 837.7) * mm});
            skArc(sketch, "E347.0.13.12", {"start": v(-140.8, 812.3) * mm, "mid": v(-140.66, 812.37) * mm, "end": v(-140.6, 812.5) * mm});
            skLineSegment(sketch, "E347.0.13.13", {"start": v(-82.6, 835.7) * mm, "end": v(-82.6, 837.5) * mm});
            skLineSegment(sketch, "E347.0.13.14", {"start": v(-140.6, 812.5) * mm, "end": v(-140.6, 814.3) * mm});
            skArc(sketch, "E347.0.13.15", {"start": v(-90.54, 837.7) * mm, "mid": v(-90.68, 837.65) * mm, "end": v(-90.74, 837.5) * mm});
            skLineSegment(sketch, "E347.0.13.16", {"start": v(-140.6, 835.7) * mm, "end": v(-140.6, 837.5) * mm});
            skArc(sketch, "E347.0.13.17", {"start": v(-140.6, 837.5) * mm, "mid": v(-140.66, 837.65) * mm, "end": v(-140.8, 837.7) * mm});
            skLineSegment(sketch, "E347.0.13.18", {"start": v(-140.8, 837.7) * mm, "end": v(-148.54, 837.7) * mm});
            skArc(sketch, "E347.0.13.19", {"start": v(-90.74, 812.5) * mm, "mid": v(-90.68, 812.37) * mm, "end": v(-90.54, 812.3) * mm});
            skLineSegment(sketch, "E347.0.13.20", {"start": v(-90.74, 814.3) * mm, "end": v(-90.74, 812.5) * mm});
            skLineSegment(sketch, "E347.0.13.21", {"start": v(-82.6, 812.5) * mm, "end": v(-82.6, 814.3) * mm});
            skArc(sketch, "E347.0.13.22", {"start": v(-148.54, 837.7) * mm, "mid": v(-148.68, 837.65) * mm, "end": v(-148.74, 837.5) * mm});
            skLineSegment(sketch, "E347.0.13.23", {"start": v(-148.74, 837.5) * mm, "end": v(-148.74, 835.7) * mm});
            skArc(sketch, "E347.0.13.24", {"start": v(-148.74, 812.5) * mm, "mid": v(-148.68, 812.37) * mm, "end": v(-148.54, 812.3) * mm});
            skLineSegment(sketch, "E347.0.13.25", {"start": v(-148.74, 814.3) * mm, "end": v(-148.74, 812.5) * mm});
            skLineSegment(sketch, "E347.0.13.26", {"start": v(-90.54, 812.3) * mm, "end": v(-82.8, 812.3) * mm});
            skArc(sketch, "E347.0.13.27", {"start": v(-82.8, 812.3) * mm, "mid": v(-82.66, 812.37) * mm, "end": v(-82.6, 812.5) * mm});
            skLineSegment(sketch, "E347.0.14.0", {"start": v(-92.06, 901.2) * mm, "end": v(-90.74, 890.5) * mm});
            skLineSegment(sketch, "E347.0.14.1", {"start": v(-139.29, 901.2) * mm, "end": v(-140.6, 911.9) * mm});
            skLineSegment(sketch, "E347.0.14.2", {"start": v(-81.29, 901.2) * mm, "end": v(-82.6, 911.9) * mm});
            skLineSegment(sketch, "E347.0.14.3", {"start": v(-82.6, 890.5) * mm, "end": v(-81.29, 901.2) * mm});
            skLineSegment(sketch, "E347.0.14.4", {"start": v(-140.6, 890.5) * mm, "end": v(-139.29, 901.2) * mm});
            skLineSegment(sketch, "E347.0.14.5", {"start": v(-150.06, 901.2) * mm, "end": v(-148.74, 890.5) * mm});
            skLineSegment(sketch, "E347.0.14.6", {"start": v(-90.74, 911.9) * mm, "end": v(-92.06, 901.2) * mm});
            skLineSegment(sketch, "E347.0.14.7", {"start": v(-148.74, 911.9) * mm, "end": v(-150.06, 901.2) * mm});
            skLineSegment(sketch, "E347.0.14.8", {"start": v(-90.74, 913.7) * mm, "end": v(-90.74, 911.9) * mm});
            skLineSegment(sketch, "E347.0.14.9", {"start": v(-148.54, 888.5) * mm, "end": v(-140.8, 888.5) * mm});
            skArc(sketch, "E347.0.14.10", {"start": v(-82.6, 913.7) * mm, "mid": v(-82.66, 913.85) * mm, "end": v(-82.8, 913.9) * mm});
            skLineSegment(sketch, "E347.0.14.11", {"start": v(-82.8, 913.9) * mm, "end": v(-90.54, 913.9) * mm});
            skArc(sketch, "E347.0.14.12", {"start": v(-140.8, 888.5) * mm, "mid": v(-140.66, 888.57) * mm, "end": v(-140.6, 888.7) * mm});
            skLineSegment(sketch, "E347.0.14.13", {"start": v(-82.6, 911.9) * mm, "end": v(-82.6, 913.7) * mm});
            skLineSegment(sketch, "E347.0.14.14", {"start": v(-140.6, 888.7) * mm, "end": v(-140.6, 890.5) * mm});
            skArc(sketch, "E347.0.14.15", {"start": v(-90.54, 913.9) * mm, "mid": v(-90.68, 913.85) * mm, "end": v(-90.74, 913.7) * mm});
            skLineSegment(sketch, "E347.0.14.16", {"start": v(-140.6, 911.9) * mm, "end": v(-140.6, 913.7) * mm});
            skArc(sketch, "E347.0.14.17", {"start": v(-140.6, 913.7) * mm, "mid": v(-140.66, 913.85) * mm, "end": v(-140.8, 913.9) * mm});
            skLineSegment(sketch, "E347.0.14.18", {"start": v(-140.8, 913.9) * mm, "end": v(-148.54, 913.9) * mm});
            skArc(sketch, "E347.0.14.19", {"start": v(-90.74, 888.7) * mm, "mid": v(-90.68, 888.57) * mm, "end": v(-90.54, 888.5) * mm});
            skLineSegment(sketch, "E347.0.14.20", {"start": v(-90.74, 890.5) * mm, "end": v(-90.74, 888.7) * mm});
            skLineSegment(sketch, "E347.0.14.21", {"start": v(-82.6, 888.7) * mm, "end": v(-82.6, 890.5) * mm});
            skArc(sketch, "E347.0.14.22", {"start": v(-148.54, 913.9) * mm, "mid": v(-148.68, 913.85) * mm, "end": v(-148.74, 913.7) * mm});
            skLineSegment(sketch, "E347.0.14.23", {"start": v(-148.74, 913.7) * mm, "end": v(-148.74, 911.9) * mm});
            skArc(sketch, "E347.0.14.24", {"start": v(-148.74, 888.7) * mm, "mid": v(-148.68, 888.57) * mm, "end": v(-148.54, 888.5) * mm});
            skLineSegment(sketch, "E347.0.14.25", {"start": v(-148.74, 890.5) * mm, "end": v(-148.74, 888.7) * mm});
            skLineSegment(sketch, "E347.0.14.26", {"start": v(-90.54, 888.5) * mm, "end": v(-82.8, 888.5) * mm});
            skArc(sketch, "E347.0.14.27", {"start": v(-82.8, 888.5) * mm, "mid": v(-82.66, 888.57) * mm, "end": v(-82.6, 888.7) * mm});
            skLineSegment(sketch, "E347.0.15.0", {"start": v(-92.06, 977.4) * mm, "end": v(-90.74, 966.7) * mm});
            skLineSegment(sketch, "E347.0.15.1", {"start": v(-139.29, 977.4) * mm, "end": v(-140.6, 988.1) * mm});
            skLineSegment(sketch, "E347.0.15.2", {"start": v(-81.29, 977.4) * mm, "end": v(-82.6, 988.1) * mm});
            skLineSegment(sketch, "E347.0.15.3", {"start": v(-82.6, 966.7) * mm, "end": v(-81.29, 977.4) * mm});
            skLineSegment(sketch, "E347.0.15.4", {"start": v(-140.6, 966.7) * mm, "end": v(-139.29, 977.4) * mm});
            skLineSegment(sketch, "E347.0.15.5", {"start": v(-150.06, 977.4) * mm, "end": v(-148.74, 966.7) * mm});
            skLineSegment(sketch, "E347.0.15.6", {"start": v(-90.74, 988.1) * mm, "end": v(-92.06, 977.4) * mm});
            skLineSegment(sketch, "E347.0.15.7", {"start": v(-148.74, 988.1) * mm, "end": v(-150.06, 977.4) * mm});
            skLineSegment(sketch, "E347.0.15.8", {"start": v(-90.74, 989.9) * mm, "end": v(-90.74, 988.1) * mm});
            skLineSegment(sketch, "E347.0.15.9", {"start": v(-148.54, 964.7) * mm, "end": v(-140.8, 964.7) * mm});
            skArc(sketch, "E347.0.15.10", {"start": v(-82.6, 989.9) * mm, "mid": v(-82.66, 990.05) * mm, "end": v(-82.8, 990.1) * mm});
            skLineSegment(sketch, "E347.0.15.11", {"start": v(-82.8, 990.1) * mm, "end": v(-90.54, 990.1) * mm});
            skArc(sketch, "E347.0.15.12", {"start": v(-140.8, 964.7) * mm, "mid": v(-140.66, 964.77) * mm, "end": v(-140.6, 964.9) * mm});
            skLineSegment(sketch, "E347.0.15.13", {"start": v(-82.6, 988.1) * mm, "end": v(-82.6, 989.9) * mm});
            skLineSegment(sketch, "E347.0.15.14", {"start": v(-140.6, 964.9) * mm, "end": v(-140.6, 966.7) * mm});
            skArc(sketch, "E347.0.15.15", {"start": v(-90.54, 990.1) * mm, "mid": v(-90.68, 990.05) * mm, "end": v(-90.74, 989.9) * mm});
            skLineSegment(sketch, "E347.0.15.16", {"start": v(-140.6, 988.1) * mm, "end": v(-140.6, 989.9) * mm});
            skArc(sketch, "E347.0.15.17", {"start": v(-140.6, 989.9) * mm, "mid": v(-140.66, 990.05) * mm, "end": v(-140.8, 990.1) * mm});
            skLineSegment(sketch, "E347.0.15.18", {"start": v(-140.8, 990.1) * mm, "end": v(-148.54, 990.1) * mm});
            skArc(sketch, "E347.0.15.19", {"start": v(-90.74, 964.9) * mm, "mid": v(-90.68, 964.77) * mm, "end": v(-90.54, 964.7) * mm});
            skLineSegment(sketch, "E347.0.15.20", {"start": v(-90.74, 966.7) * mm, "end": v(-90.74, 964.9) * mm});
            skLineSegment(sketch, "E347.0.15.21", {"start": v(-82.6, 964.9) * mm, "end": v(-82.6, 966.7) * mm});
            skArc(sketch, "E347.0.15.22", {"start": v(-148.54, 990.1) * mm, "mid": v(-148.68, 990.05) * mm, "end": v(-148.74, 989.9) * mm});
            skLineSegment(sketch, "E347.0.15.23", {"start": v(-148.74, 989.9) * mm, "end": v(-148.74, 988.1) * mm});
            skArc(sketch, "E347.0.15.24", {"start": v(-148.74, 964.9) * mm, "mid": v(-148.68, 964.77) * mm, "end": v(-148.54, 964.7) * mm});
            skLineSegment(sketch, "E347.0.15.25", {"start": v(-148.74, 966.7) * mm, "end": v(-148.74, 964.9) * mm});
            skLineSegment(sketch, "E347.0.15.26", {"start": v(-90.54, 964.7) * mm, "end": v(-82.8, 964.7) * mm});
            skArc(sketch, "E347.0.15.27", {"start": v(-82.8, 964.7) * mm, "mid": v(-82.66, 964.77) * mm, "end": v(-82.6, 964.9) * mm});
            skLineSegment(sketch, "E347.0.16.0", {"start": v(-92.06, 1053.6) * mm, "end": v(-90.74, 1042.9) * mm});
            skLineSegment(sketch, "E347.0.16.1", {"start": v(-139.29, 1053.6) * mm, "end": v(-140.6, 1064.3) * mm});
            skLineSegment(sketch, "E347.0.16.2", {"start": v(-81.29, 1053.6) * mm, "end": v(-82.6, 1064.3) * mm});
            skLineSegment(sketch, "E347.0.16.3", {"start": v(-82.6, 1042.9) * mm, "end": v(-81.29, 1053.6) * mm});
            skLineSegment(sketch, "E347.0.16.4", {"start": v(-140.6, 1042.9) * mm, "end": v(-139.29, 1053.6) * mm});
            skLineSegment(sketch, "E347.0.16.5", {"start": v(-150.06, 1053.6) * mm, "end": v(-148.74, 1042.9) * mm});
            skLineSegment(sketch, "E347.0.16.6", {"start": v(-90.74, 1064.3) * mm, "end": v(-92.06, 1053.6) * mm});
            skLineSegment(sketch, "E347.0.16.7", {"start": v(-148.74, 1064.3) * mm, "end": v(-150.06, 1053.6) * mm});
            skLineSegment(sketch, "E347.0.16.8", {"start": v(-90.74, 1066.1) * mm, "end": v(-90.74, 1064.3) * mm});
            skLineSegment(sketch, "E347.0.16.9", {"start": v(-148.54, 1040.9) * mm, "end": v(-140.8, 1040.9) * mm});
            skArc(sketch, "E347.0.16.10", {"start": v(-82.6, 1066.1) * mm, "mid": v(-82.66, 1066.25) * mm, "end": v(-82.8, 1066.3) * mm});
            skLineSegment(sketch, "E347.0.16.11", {"start": v(-82.8, 1066.3) * mm, "end": v(-90.54, 1066.3) * mm});
            skArc(sketch, "E347.0.16.12", {"start": v(-140.8, 1040.9) * mm, "mid": v(-140.66, 1040.97) * mm, "end": v(-140.6, 1041.1) * mm});
            skLineSegment(sketch, "E347.0.16.13", {"start": v(-82.6, 1064.3) * mm, "end": v(-82.6, 1066.1) * mm});
            skLineSegment(sketch, "E347.0.16.14", {"start": v(-140.6, 1041.1) * mm, "end": v(-140.6, 1042.9) * mm});
            skArc(sketch, "E347.0.16.15", {"start": v(-90.54, 1066.3) * mm, "mid": v(-90.68, 1066.25) * mm, "end": v(-90.74, 1066.1) * mm});
            skLineSegment(sketch, "E347.0.16.16", {"start": v(-140.6, 1064.3) * mm, "end": v(-140.6, 1066.1) * mm});
            skArc(sketch, "E347.0.16.17", {"start": v(-140.6, 1066.1) * mm, "mid": v(-140.66, 1066.25) * mm, "end": v(-140.8, 1066.3) * mm});
            skLineSegment(sketch, "E347.0.16.18", {"start": v(-140.8, 1066.3) * mm, "end": v(-148.54, 1066.3) * mm});
            skArc(sketch, "E347.0.16.19", {"start": v(-90.74, 1041.1) * mm, "mid": v(-90.68, 1040.97) * mm, "end": v(-90.54, 1040.9) * mm});
            skLineSegment(sketch, "E347.0.16.20", {"start": v(-90.74, 1042.9) * mm, "end": v(-90.74, 1041.1) * mm});
            skLineSegment(sketch, "E347.0.16.21", {"start": v(-82.6, 1041.1) * mm, "end": v(-82.6, 1042.9) * mm});
            skArc(sketch, "E347.0.16.22", {"start": v(-148.54, 1066.3) * mm, "mid": v(-148.68, 1066.25) * mm, "end": v(-148.74, 1066.1) * mm});
            skLineSegment(sketch, "E347.0.16.23", {"start": v(-148.74, 1066.1) * mm, "end": v(-148.74, 1064.3) * mm});
            skArc(sketch, "E347.0.16.24", {"start": v(-148.74, 1041.1) * mm, "mid": v(-148.68, 1040.97) * mm, "end": v(-148.54, 1040.9) * mm});
            skLineSegment(sketch, "E347.0.16.25", {"start": v(-148.74, 1042.9) * mm, "end": v(-148.74, 1041.1) * mm});
            skLineSegment(sketch, "E347.0.16.26", {"start": v(-90.54, 1040.9) * mm, "end": v(-82.8, 1040.9) * mm});
            skArc(sketch, "E347.0.16.27", {"start": v(-82.8, 1040.9) * mm, "mid": v(-82.66, 1040.97) * mm, "end": v(-82.6, 1041.1) * mm});
            skLineSegment(sketch, "E347.0.17.0", {"start": v(-92.06, 1129.8) * mm, "end": v(-90.74, 1119.1) * mm});
            skLineSegment(sketch, "E347.0.17.1", {"start": v(-139.29, 1129.8) * mm, "end": v(-140.6, 1140.5) * mm});
            skLineSegment(sketch, "E347.0.17.2", {"start": v(-81.29, 1129.8) * mm, "end": v(-82.6, 1140.5) * mm});
            skLineSegment(sketch, "E347.0.17.3", {"start": v(-82.6, 1119.1) * mm, "end": v(-81.29, 1129.8) * mm});
            skLineSegment(sketch, "E347.0.17.4", {"start": v(-140.6, 1119.1) * mm, "end": v(-139.29, 1129.8) * mm});
            skLineSegment(sketch, "E347.0.17.5", {"start": v(-150.06, 1129.8) * mm, "end": v(-148.74, 1119.1) * mm});
            skLineSegment(sketch, "E347.0.17.6", {"start": v(-90.74, 1140.5) * mm, "end": v(-92.06, 1129.8) * mm});
            skLineSegment(sketch, "E347.0.17.7", {"start": v(-148.74, 1140.5) * mm, "end": v(-150.06, 1129.8) * mm});
            skLineSegment(sketch, "E347.0.17.8", {"start": v(-90.74, 1142.3) * mm, "end": v(-90.74, 1140.5) * mm});
            skLineSegment(sketch, "E347.0.17.9", {"start": v(-148.54, 1117.1) * mm, "end": v(-140.8, 1117.1) * mm});
            skArc(sketch, "E347.0.17.10", {"start": v(-82.6, 1142.3) * mm, "mid": v(-82.66, 1142.45) * mm, "end": v(-82.8, 1142.5) * mm});
            skLineSegment(sketch, "E347.0.17.11", {"start": v(-82.8, 1142.5) * mm, "end": v(-90.54, 1142.5) * mm});
            skArc(sketch, "E347.0.17.12", {"start": v(-140.8, 1117.1) * mm, "mid": v(-140.66, 1117.17) * mm, "end": v(-140.6, 1117.3) * mm});
            skLineSegment(sketch, "E347.0.17.13", {"start": v(-82.6, 1140.5) * mm, "end": v(-82.6, 1142.3) * mm});
            skLineSegment(sketch, "E347.0.17.14", {"start": v(-140.6, 1117.3) * mm, "end": v(-140.6, 1119.1) * mm});
            skArc(sketch, "E347.0.17.15", {"start": v(-90.54, 1142.5) * mm, "mid": v(-90.68, 1142.45) * mm, "end": v(-90.74, 1142.3) * mm});
            skLineSegment(sketch, "E347.0.17.16", {"start": v(-140.6, 1140.5) * mm, "end": v(-140.6, 1142.3) * mm});
            skArc(sketch, "E347.0.17.17", {"start": v(-140.6, 1142.3) * mm, "mid": v(-140.66, 1142.45) * mm, "end": v(-140.8, 1142.5) * mm});
            skLineSegment(sketch, "E347.0.17.18", {"start": v(-140.8, 1142.5) * mm, "end": v(-148.54, 1142.5) * mm});
            skArc(sketch, "E347.0.17.19", {"start": v(-90.74, 1117.3) * mm, "mid": v(-90.68, 1117.17) * mm, "end": v(-90.54, 1117.1) * mm});
            skLineSegment(sketch, "E347.0.17.20", {"start": v(-90.74, 1119.1) * mm, "end": v(-90.74, 1117.3) * mm});
            skLineSegment(sketch, "E347.0.17.21", {"start": v(-82.6, 1117.3) * mm, "end": v(-82.6, 1119.1) * mm});
            skArc(sketch, "E347.0.17.22", {"start": v(-148.54, 1142.5) * mm, "mid": v(-148.68, 1142.45) * mm, "end": v(-148.74, 1142.3) * mm});
            skLineSegment(sketch, "E347.0.17.23", {"start": v(-148.74, 1142.3) * mm, "end": v(-148.74, 1140.5) * mm});
            skArc(sketch, "E347.0.17.24", {"start": v(-148.74, 1117.3) * mm, "mid": v(-148.68, 1117.17) * mm, "end": v(-148.54, 1117.1) * mm});
            skLineSegment(sketch, "E347.0.17.25", {"start": v(-148.74, 1119.1) * mm, "end": v(-148.74, 1117.3) * mm});
            skLineSegment(sketch, "E347.0.17.26", {"start": v(-90.54, 1117.1) * mm, "end": v(-82.8, 1117.1) * mm});
            skArc(sketch, "E347.0.17.27", {"start": v(-82.8, 1117.1) * mm, "mid": v(-82.66, 1117.17) * mm, "end": v(-82.6, 1117.3) * mm});
            skLineSegment(sketch, "E347.0.18.0", {"start": v(-92.06, 1206) * mm, "end": v(-90.74, 1195.3) * mm});
            skLineSegment(sketch, "E347.0.18.1", {"start": v(-139.29, 1206) * mm, "end": v(-140.6, 1216.7) * mm});
            skLineSegment(sketch, "E347.0.18.2", {"start": v(-81.29, 1206) * mm, "end": v(-82.6, 1216.7) * mm});
            skLineSegment(sketch, "E347.0.18.3", {"start": v(-82.6, 1195.3) * mm, "end": v(-81.29, 1206) * mm});
            skLineSegment(sketch, "E347.0.18.4", {"start": v(-140.6, 1195.3) * mm, "end": v(-139.29, 1206) * mm});
            skLineSegment(sketch, "E347.0.18.5", {"start": v(-150.06, 1206) * mm, "end": v(-148.74, 1195.3) * mm});
            skLineSegment(sketch, "E347.0.18.6", {"start": v(-90.74, 1216.7) * mm, "end": v(-92.06, 1206) * mm});
            skLineSegment(sketch, "E347.0.18.7", {"start": v(-148.74, 1216.7) * mm, "end": v(-150.06, 1206) * mm});
            skLineSegment(sketch, "E347.0.18.8", {"start": v(-90.74, 1218.5) * mm, "end": v(-90.74, 1216.7) * mm});
            skLineSegment(sketch, "E347.0.18.9", {"start": v(-148.54, 1193.3) * mm, "end": v(-140.8, 1193.3) * mm});
            skArc(sketch, "E347.0.18.10", {"start": v(-82.6, 1218.5) * mm, "mid": v(-82.66, 1218.65) * mm, "end": v(-82.8, 1218.7) * mm});
            skLineSegment(sketch, "E347.0.18.11", {"start": v(-82.8, 1218.7) * mm, "end": v(-90.54, 1218.7) * mm});
            skArc(sketch, "E347.0.18.12", {"start": v(-140.8, 1193.3) * mm, "mid": v(-140.66, 1193.37) * mm, "end": v(-140.6, 1193.5) * mm});
            skLineSegment(sketch, "E347.0.18.13", {"start": v(-82.6, 1216.7) * mm, "end": v(-82.6, 1218.5) * mm});
            skLineSegment(sketch, "E347.0.18.14", {"start": v(-140.6, 1193.5) * mm, "end": v(-140.6, 1195.3) * mm});
            skArc(sketch, "E347.0.18.15", {"start": v(-90.54, 1218.7) * mm, "mid": v(-90.68, 1218.65) * mm, "end": v(-90.74, 1218.5) * mm});
            skLineSegment(sketch, "E347.0.18.16", {"start": v(-140.6, 1216.7) * mm, "end": v(-140.6, 1218.5) * mm});
            skArc(sketch, "E347.0.18.17", {"start": v(-140.6, 1218.5) * mm, "mid": v(-140.66, 1218.65) * mm, "end": v(-140.8, 1218.7) * mm});
            skLineSegment(sketch, "E347.0.18.18", {"start": v(-140.8, 1218.7) * mm, "end": v(-148.54, 1218.7) * mm});
            skArc(sketch, "E347.0.18.19", {"start": v(-90.74, 1193.5) * mm, "mid": v(-90.68, 1193.37) * mm, "end": v(-90.54, 1193.3) * mm});
            skLineSegment(sketch, "E347.0.18.20", {"start": v(-90.74, 1195.3) * mm, "end": v(-90.74, 1193.5) * mm});
            skLineSegment(sketch, "E347.0.18.21", {"start": v(-82.6, 1193.5) * mm, "end": v(-82.6, 1195.3) * mm});
            skArc(sketch, "E347.0.18.22", {"start": v(-148.54, 1218.7) * mm, "mid": v(-148.68, 1218.65) * mm, "end": v(-148.74, 1218.5) * mm});
            skLineSegment(sketch, "E347.0.18.23", {"start": v(-148.74, 1218.5) * mm, "end": v(-148.74, 1216.7) * mm});
            skArc(sketch, "E347.0.18.24", {"start": v(-148.74, 1193.5) * mm, "mid": v(-148.68, 1193.37) * mm, "end": v(-148.54, 1193.3) * mm});
            skLineSegment(sketch, "E347.0.18.25", {"start": v(-148.74, 1195.3) * mm, "end": v(-148.74, 1193.5) * mm});
            skLineSegment(sketch, "E347.0.18.26", {"start": v(-90.54, 1193.3) * mm, "end": v(-82.8, 1193.3) * mm});
            skArc(sketch, "E347.0.18.27", {"start": v(-82.8, 1193.3) * mm, "mid": v(-82.66, 1193.37) * mm, "end": v(-82.6, 1193.5) * mm});
            skLineSegment(sketch, "E347.0.19.0", {"start": v(-92.06, 1282.2) * mm, "end": v(-90.74, 1271.5) * mm});
            skLineSegment(sketch, "E347.0.19.1", {"start": v(-139.29, 1282.2) * mm, "end": v(-140.6, 1292.9) * mm});
            skLineSegment(sketch, "E347.0.19.2", {"start": v(-81.29, 1282.2) * mm, "end": v(-82.6, 1292.9) * mm});
            skLineSegment(sketch, "E347.0.19.3", {"start": v(-82.6, 1271.5) * mm, "end": v(-81.29, 1282.2) * mm});
            skLineSegment(sketch, "E347.0.19.4", {"start": v(-140.6, 1271.5) * mm, "end": v(-139.29, 1282.2) * mm});
            skLineSegment(sketch, "E347.0.19.5", {"start": v(-150.06, 1282.2) * mm, "end": v(-148.74, 1271.5) * mm});
            skLineSegment(sketch, "E347.0.19.6", {"start": v(-90.74, 1292.9) * mm, "end": v(-92.06, 1282.2) * mm});
            skLineSegment(sketch, "E347.0.19.7", {"start": v(-148.74, 1292.9) * mm, "end": v(-150.06, 1282.2) * mm});
            skLineSegment(sketch, "E347.0.19.8", {"start": v(-90.74, 1294.7) * mm, "end": v(-90.74, 1292.9) * mm});
            skLineSegment(sketch, "E347.0.19.9", {"start": v(-148.54, 1269.5) * mm, "end": v(-140.8, 1269.5) * mm});
            skArc(sketch, "E347.0.19.10", {"start": v(-82.6, 1294.7) * mm, "mid": v(-82.66, 1294.85) * mm, "end": v(-82.8, 1294.9) * mm});
            skLineSegment(sketch, "E347.0.19.11", {"start": v(-82.8, 1294.9) * mm, "end": v(-90.54, 1294.9) * mm});
            skArc(sketch, "E347.0.19.12", {"start": v(-140.8, 1269.5) * mm, "mid": v(-140.66, 1269.57) * mm, "end": v(-140.6, 1269.7) * mm});
            skLineSegment(sketch, "E347.0.19.13", {"start": v(-82.6, 1292.9) * mm, "end": v(-82.6, 1294.7) * mm});
            skLineSegment(sketch, "E347.0.19.14", {"start": v(-140.6, 1269.7) * mm, "end": v(-140.6, 1271.5) * mm});
            skArc(sketch, "E347.0.19.15", {"start": v(-90.54, 1294.9) * mm, "mid": v(-90.68, 1294.85) * mm, "end": v(-90.74, 1294.7) * mm});
            skLineSegment(sketch, "E347.0.19.16", {"start": v(-140.6, 1292.9) * mm, "end": v(-140.6, 1294.7) * mm});
            skArc(sketch, "E347.0.19.17", {"start": v(-140.6, 1294.7) * mm, "mid": v(-140.66, 1294.85) * mm, "end": v(-140.8, 1294.9) * mm});
            skLineSegment(sketch, "E347.0.19.18", {"start": v(-140.8, 1294.9) * mm, "end": v(-148.54, 1294.9) * mm});
            skArc(sketch, "E347.0.19.19", {"start": v(-90.74, 1269.7) * mm, "mid": v(-90.68, 1269.57) * mm, "end": v(-90.54, 1269.5) * mm});
            skLineSegment(sketch, "E347.0.19.20", {"start": v(-90.74, 1271.5) * mm, "end": v(-90.74, 1269.7) * mm});
            skLineSegment(sketch, "E347.0.19.21", {"start": v(-82.6, 1269.7) * mm, "end": v(-82.6, 1271.5) * mm});
            skArc(sketch, "E347.0.19.22", {"start": v(-148.54, 1294.9) * mm, "mid": v(-148.68, 1294.85) * mm, "end": v(-148.74, 1294.7) * mm});
            skLineSegment(sketch, "E347.0.19.23", {"start": v(-148.74, 1294.7) * mm, "end": v(-148.74, 1292.9) * mm});
            skArc(sketch, "E347.0.19.24", {"start": v(-148.74, 1269.7) * mm, "mid": v(-148.68, 1269.57) * mm, "end": v(-148.54, 1269.5) * mm});
            skLineSegment(sketch, "E347.0.19.25", {"start": v(-148.74, 1271.5) * mm, "end": v(-148.74, 1269.7) * mm});
            skLineSegment(sketch, "E347.0.19.26", {"start": v(-90.54, 1269.5) * mm, "end": v(-82.8, 1269.5) * mm});
            skArc(sketch, "E347.0.19.27", {"start": v(-82.8, 1269.5) * mm, "mid": v(-82.66, 1269.57) * mm, "end": v(-82.6, 1269.7) * mm});
            skLineSegment(sketch, "E347.0.20.0", {"start": v(-92.06, 1358.4) * mm, "end": v(-90.74, 1347.7) * mm});
            skLineSegment(sketch, "E347.0.20.1", {"start": v(-139.29, 1358.4) * mm, "end": v(-140.6, 1369.1) * mm});
            skLineSegment(sketch, "E347.0.20.2", {"start": v(-81.29, 1358.4) * mm, "end": v(-82.6, 1369.1) * mm});
            skLineSegment(sketch, "E347.0.20.3", {"start": v(-82.6, 1347.7) * mm, "end": v(-81.29, 1358.4) * mm});
            skLineSegment(sketch, "E347.0.20.4", {"start": v(-140.6, 1347.7) * mm, "end": v(-139.29, 1358.4) * mm});
            skLineSegment(sketch, "E347.0.20.5", {"start": v(-150.06, 1358.4) * mm, "end": v(-148.74, 1347.7) * mm});
            skLineSegment(sketch, "E347.0.20.6", {"start": v(-90.74, 1369.1) * mm, "end": v(-92.06, 1358.4) * mm});
            skLineSegment(sketch, "E347.0.20.7", {"start": v(-148.74, 1369.1) * mm, "end": v(-150.06, 1358.4) * mm});
            skLineSegment(sketch, "E347.0.20.8", {"start": v(-90.74, 1370.9) * mm, "end": v(-90.74, 1369.1) * mm});
            skLineSegment(sketch, "E347.0.20.9", {"start": v(-148.54, 1345.7) * mm, "end": v(-140.8, 1345.7) * mm});
            skArc(sketch, "E347.0.20.10", {"start": v(-82.6, 1370.9) * mm, "mid": v(-82.66, 1371.05) * mm, "end": v(-82.8, 1371.1) * mm});
            skLineSegment(sketch, "E347.0.20.11", {"start": v(-82.8, 1371.1) * mm, "end": v(-90.54, 1371.1) * mm});
            skArc(sketch, "E347.0.20.12", {"start": v(-140.8, 1345.7) * mm, "mid": v(-140.66, 1345.77) * mm, "end": v(-140.6, 1345.9) * mm});
            skLineSegment(sketch, "E347.0.20.13", {"start": v(-82.6, 1369.1) * mm, "end": v(-82.6, 1370.9) * mm});
            skLineSegment(sketch, "E347.0.20.14", {"start": v(-140.6, 1345.9) * mm, "end": v(-140.6, 1347.7) * mm});
            skArc(sketch, "E347.0.20.15", {"start": v(-90.54, 1371.1) * mm, "mid": v(-90.68, 1371.05) * mm, "end": v(-90.74, 1370.9) * mm});
            skLineSegment(sketch, "E347.0.20.16", {"start": v(-140.6, 1369.1) * mm, "end": v(-140.6, 1370.9) * mm});
            skArc(sketch, "E347.0.20.17", {"start": v(-140.6, 1370.9) * mm, "mid": v(-140.66, 1371.05) * mm, "end": v(-140.8, 1371.1) * mm});
            skLineSegment(sketch, "E347.0.20.18", {"start": v(-140.8, 1371.1) * mm, "end": v(-148.54, 1371.1) * mm});
            skArc(sketch, "E347.0.20.19", {"start": v(-90.74, 1345.9) * mm, "mid": v(-90.68, 1345.77) * mm, "end": v(-90.54, 1345.7) * mm});
            skLineSegment(sketch, "E347.0.20.20", {"start": v(-90.74, 1347.7) * mm, "end": v(-90.74, 1345.9) * mm});
            skLineSegment(sketch, "E347.0.20.21", {"start": v(-82.6, 1345.9) * mm, "end": v(-82.6, 1347.7) * mm});
            skArc(sketch, "E347.0.20.22", {"start": v(-148.54, 1371.1) * mm, "mid": v(-148.68, 1371.05) * mm, "end": v(-148.74, 1370.9) * mm});
            skLineSegment(sketch, "E347.0.20.23", {"start": v(-148.74, 1370.9) * mm, "end": v(-148.74, 1369.1) * mm});
            skArc(sketch, "E347.0.20.24", {"start": v(-148.74, 1345.9) * mm, "mid": v(-148.68, 1345.77) * mm, "end": v(-148.54, 1345.7) * mm});
            skLineSegment(sketch, "E347.0.20.25", {"start": v(-148.74, 1347.7) * mm, "end": v(-148.74, 1345.9) * mm});
            skLineSegment(sketch, "E347.0.20.26", {"start": v(-90.54, 1345.7) * mm, "end": v(-82.8, 1345.7) * mm});
            skArc(sketch, "E347.0.20.27", {"start": v(-82.8, 1345.7) * mm, "mid": v(-82.66, 1345.77) * mm, "end": v(-82.6, 1345.9) * mm});
            skLineSegment(sketch, "E347.0.21.0", {"start": v(-92.06, 1434.6) * mm, "end": v(-90.74, 1423.9) * mm});
            skLineSegment(sketch, "E347.0.21.1", {"start": v(-139.29, 1434.6) * mm, "end": v(-140.6, 1445.3) * mm});
            skLineSegment(sketch, "E347.0.21.2", {"start": v(-81.29, 1434.6) * mm, "end": v(-82.6, 1445.3) * mm});
            skLineSegment(sketch, "E347.0.21.3", {"start": v(-82.6, 1423.9) * mm, "end": v(-81.29, 1434.6) * mm});
            skLineSegment(sketch, "E347.0.21.4", {"start": v(-140.6, 1423.9) * mm, "end": v(-139.29, 1434.6) * mm});
            skLineSegment(sketch, "E347.0.21.5", {"start": v(-150.06, 1434.6) * mm, "end": v(-148.74, 1423.9) * mm});
            skLineSegment(sketch, "E347.0.21.6", {"start": v(-90.74, 1445.3) * mm, "end": v(-92.06, 1434.6) * mm});
            skLineSegment(sketch, "E347.0.21.7", {"start": v(-148.74, 1445.3) * mm, "end": v(-150.06, 1434.6) * mm});
            skLineSegment(sketch, "E347.0.21.8", {"start": v(-90.74, 1447.1) * mm, "end": v(-90.74, 1445.3) * mm});
            skLineSegment(sketch, "E347.0.21.9", {"start": v(-148.54, 1421.9) * mm, "end": v(-140.8, 1421.9) * mm});
            skArc(sketch, "E347.0.21.10", {"start": v(-82.6, 1447.1) * mm, "mid": v(-82.66, 1447.25) * mm, "end": v(-82.8, 1447.3) * mm});
            skLineSegment(sketch, "E347.0.21.11", {"start": v(-82.8, 1447.3) * mm, "end": v(-90.54, 1447.3) * mm});
            skArc(sketch, "E347.0.21.12", {"start": v(-140.8, 1421.9) * mm, "mid": v(-140.66, 1421.97) * mm, "end": v(-140.6, 1422.1) * mm});
            skLineSegment(sketch, "E347.0.21.13", {"start": v(-82.6, 1445.3) * mm, "end": v(-82.6, 1447.1) * mm});
            skLineSegment(sketch, "E347.0.21.14", {"start": v(-140.6, 1422.1) * mm, "end": v(-140.6, 1423.9) * mm});
            skArc(sketch, "E347.0.21.15", {"start": v(-90.54, 1447.3) * mm, "mid": v(-90.68, 1447.25) * mm, "end": v(-90.74, 1447.1) * mm});
            skLineSegment(sketch, "E347.0.21.16", {"start": v(-140.6, 1445.3) * mm, "end": v(-140.6, 1447.1) * mm});
            skArc(sketch, "E347.0.21.17", {"start": v(-140.6, 1447.1) * mm, "mid": v(-140.66, 1447.25) * mm, "end": v(-140.8, 1447.3) * mm});
            skLineSegment(sketch, "E347.0.21.18", {"start": v(-140.8, 1447.3) * mm, "end": v(-148.54, 1447.3) * mm});
            skArc(sketch, "E347.0.21.19", {"start": v(-90.74, 1422.1) * mm, "mid": v(-90.68, 1421.97) * mm, "end": v(-90.54, 1421.9) * mm});
            skLineSegment(sketch, "E347.0.21.20", {"start": v(-90.74, 1423.9) * mm, "end": v(-90.74, 1422.1) * mm});
            skLineSegment(sketch, "E347.0.21.21", {"start": v(-82.6, 1422.1) * mm, "end": v(-82.6, 1423.9) * mm});
            skArc(sketch, "E347.0.21.22", {"start": v(-148.54, 1447.3) * mm, "mid": v(-148.68, 1447.25) * mm, "end": v(-148.74, 1447.1) * mm});
            skLineSegment(sketch, "E347.0.21.23", {"start": v(-148.74, 1447.1) * mm, "end": v(-148.74, 1445.3) * mm});
            skArc(sketch, "E347.0.21.24", {"start": v(-148.74, 1422.1) * mm, "mid": v(-148.68, 1421.97) * mm, "end": v(-148.54, 1421.9) * mm});
            skLineSegment(sketch, "E347.0.21.25", {"start": v(-148.74, 1423.9) * mm, "end": v(-148.74, 1422.1) * mm});
            skLineSegment(sketch, "E347.0.21.26", {"start": v(-90.54, 1421.9) * mm, "end": v(-82.8, 1421.9) * mm});
            skArc(sketch, "E347.0.21.27", {"start": v(-82.8, 1421.9) * mm, "mid": v(-82.66, 1421.97) * mm, "end": v(-82.6, 1422.1) * mm});
            skLineSegment(sketch, "E347.0.22.0", {"start": v(-92.06, 1510.8) * mm, "end": v(-90.74, 1500.1) * mm});
            skLineSegment(sketch, "E347.0.22.1", {"start": v(-139.29, 1510.8) * mm, "end": v(-140.6, 1521.5) * mm});
            skLineSegment(sketch, "E347.0.22.2", {"start": v(-81.29, 1510.8) * mm, "end": v(-82.6, 1521.5) * mm});
            skLineSegment(sketch, "E347.0.22.3", {"start": v(-82.6, 1500.1) * mm, "end": v(-81.29, 1510.8) * mm});
            skLineSegment(sketch, "E347.0.22.4", {"start": v(-140.6, 1500.1) * mm, "end": v(-139.29, 1510.8) * mm});
            skLineSegment(sketch, "E347.0.22.5", {"start": v(-150.06, 1510.8) * mm, "end": v(-148.74, 1500.1) * mm});
            skLineSegment(sketch, "E347.0.22.6", {"start": v(-90.74, 1521.5) * mm, "end": v(-92.06, 1510.8) * mm});
            skLineSegment(sketch, "E347.0.22.7", {"start": v(-148.74, 1521.5) * mm, "end": v(-150.06, 1510.8) * mm});
            skLineSegment(sketch, "E347.0.22.8", {"start": v(-90.74, 1523.3) * mm, "end": v(-90.74, 1521.5) * mm});
            skLineSegment(sketch, "E347.0.22.9", {"start": v(-148.54, 1498.1) * mm, "end": v(-140.8, 1498.1) * mm});
            skArc(sketch, "E347.0.22.10", {"start": v(-82.6, 1523.3) * mm, "mid": v(-82.66, 1523.45) * mm, "end": v(-82.8, 1523.5) * mm});
            skLineSegment(sketch, "E347.0.22.11", {"start": v(-82.8, 1523.5) * mm, "end": v(-90.54, 1523.5) * mm});
            skArc(sketch, "E347.0.22.12", {"start": v(-140.8, 1498.1) * mm, "mid": v(-140.66, 1498.17) * mm, "end": v(-140.6, 1498.3) * mm});
            skLineSegment(sketch, "E347.0.22.13", {"start": v(-82.6, 1521.5) * mm, "end": v(-82.6, 1523.3) * mm});
            skLineSegment(sketch, "E347.0.22.14", {"start": v(-140.6, 1498.3) * mm, "end": v(-140.6, 1500.1) * mm});
            skArc(sketch, "E347.0.22.15", {"start": v(-90.54, 1523.5) * mm, "mid": v(-90.68, 1523.45) * mm, "end": v(-90.74, 1523.3) * mm});
            skLineSegment(sketch, "E347.0.22.16", {"start": v(-140.6, 1521.5) * mm, "end": v(-140.6, 1523.3) * mm});
            skArc(sketch, "E347.0.22.17", {"start": v(-140.6, 1523.3) * mm, "mid": v(-140.66, 1523.45) * mm, "end": v(-140.8, 1523.5) * mm});
            skLineSegment(sketch, "E347.0.22.18", {"start": v(-140.8, 1523.5) * mm, "end": v(-148.54, 1523.5) * mm});
            skArc(sketch, "E347.0.22.19", {"start": v(-90.74, 1498.3) * mm, "mid": v(-90.68, 1498.17) * mm, "end": v(-90.54, 1498.1) * mm});
            skLineSegment(sketch, "E347.0.22.20", {"start": v(-90.74, 1500.1) * mm, "end": v(-90.74, 1498.3) * mm});
            skLineSegment(sketch, "E347.0.22.21", {"start": v(-82.6, 1498.3) * mm, "end": v(-82.6, 1500.1) * mm});
            skArc(sketch, "E347.0.22.22", {"start": v(-148.54, 1523.5) * mm, "mid": v(-148.68, 1523.45) * mm, "end": v(-148.74, 1523.3) * mm});
            skLineSegment(sketch, "E347.0.22.23", {"start": v(-148.74, 1523.3) * mm, "end": v(-148.74, 1521.5) * mm});
            skArc(sketch, "E347.0.22.24", {"start": v(-148.74, 1498.3) * mm, "mid": v(-148.68, 1498.17) * mm, "end": v(-148.54, 1498.1) * mm});
            skLineSegment(sketch, "E347.0.22.25", {"start": v(-148.74, 1500.1) * mm, "end": v(-148.74, 1498.3) * mm});
            skLineSegment(sketch, "E347.0.22.26", {"start": v(-90.54, 1498.1) * mm, "end": v(-82.8, 1498.1) * mm});
            skArc(sketch, "E347.0.22.27", {"start": v(-82.8, 1498.1) * mm, "mid": v(-82.66, 1498.17) * mm, "end": v(-82.6, 1498.3) * mm});
            skLineSegment(sketch, "E347.0.23.0", {"start": v(-92.06, 1587) * mm, "end": v(-90.74, 1576.3) * mm});
            skLineSegment(sketch, "E347.0.23.1", {"start": v(-139.29, 1587) * mm, "end": v(-140.6, 1597.7) * mm});
            skLineSegment(sketch, "E347.0.23.2", {"start": v(-81.29, 1587) * mm, "end": v(-82.6, 1597.7) * mm});
            skLineSegment(sketch, "E347.0.23.3", {"start": v(-82.6, 1576.3) * mm, "end": v(-81.29, 1587) * mm});
            skLineSegment(sketch, "E347.0.23.4", {"start": v(-140.6, 1576.3) * mm, "end": v(-139.29, 1587) * mm});
            skLineSegment(sketch, "E347.0.23.5", {"start": v(-150.06, 1587) * mm, "end": v(-148.74, 1576.3) * mm});
            skLineSegment(sketch, "E347.0.23.6", {"start": v(-90.74, 1597.7) * mm, "end": v(-92.06, 1587) * mm});
            skLineSegment(sketch, "E347.0.23.7", {"start": v(-148.74, 1597.7) * mm, "end": v(-150.06, 1587) * mm});
            skLineSegment(sketch, "E347.0.23.8", {"start": v(-90.74, 1599.5) * mm, "end": v(-90.74, 1597.7) * mm});
            skLineSegment(sketch, "E347.0.23.9", {"start": v(-148.54, 1574.3) * mm, "end": v(-140.8, 1574.3) * mm});
            skArc(sketch, "E347.0.23.10", {"start": v(-82.6, 1599.5) * mm, "mid": v(-82.66, 1599.65) * mm, "end": v(-82.8, 1599.7) * mm});
            skLineSegment(sketch, "E347.0.23.11", {"start": v(-82.8, 1599.7) * mm, "end": v(-90.54, 1599.7) * mm});
            skArc(sketch, "E347.0.23.12", {"start": v(-140.8, 1574.3) * mm, "mid": v(-140.66, 1574.37) * mm, "end": v(-140.6, 1574.5) * mm});
            skLineSegment(sketch, "E347.0.23.13", {"start": v(-82.6, 1597.7) * mm, "end": v(-82.6, 1599.5) * mm});
            skLineSegment(sketch, "E347.0.23.14", {"start": v(-140.6, 1574.5) * mm, "end": v(-140.6, 1576.3) * mm});
            skArc(sketch, "E347.0.23.15", {"start": v(-90.54, 1599.7) * mm, "mid": v(-90.68, 1599.65) * mm, "end": v(-90.74, 1599.5) * mm});
            skLineSegment(sketch, "E347.0.23.16", {"start": v(-140.6, 1597.7) * mm, "end": v(-140.6, 1599.5) * mm});
            skArc(sketch, "E347.0.23.17", {"start": v(-140.6, 1599.5) * mm, "mid": v(-140.66, 1599.65) * mm, "end": v(-140.8, 1599.7) * mm});
            skLineSegment(sketch, "E347.0.23.18", {"start": v(-140.8, 1599.7) * mm, "end": v(-148.54, 1599.7) * mm});
            skArc(sketch, "E347.0.23.19", {"start": v(-90.74, 1574.5) * mm, "mid": v(-90.68, 1574.37) * mm, "end": v(-90.54, 1574.3) * mm});
            skLineSegment(sketch, "E347.0.23.20", {"start": v(-90.74, 1576.3) * mm, "end": v(-90.74, 1574.5) * mm});
            skLineSegment(sketch, "E347.0.23.21", {"start": v(-82.6, 1574.5) * mm, "end": v(-82.6, 1576.3) * mm});
            skArc(sketch, "E347.0.23.22", {"start": v(-148.54, 1599.7) * mm, "mid": v(-148.68, 1599.65) * mm, "end": v(-148.74, 1599.5) * mm});
            skLineSegment(sketch, "E347.0.23.23", {"start": v(-148.74, 1599.5) * mm, "end": v(-148.74, 1597.7) * mm});
            skArc(sketch, "E347.0.23.24", {"start": v(-148.74, 1574.5) * mm, "mid": v(-148.68, 1574.37) * mm, "end": v(-148.54, 1574.3) * mm});
            skLineSegment(sketch, "E347.0.23.25", {"start": v(-148.74, 1576.3) * mm, "end": v(-148.74, 1574.5) * mm});
            skLineSegment(sketch, "E347.0.23.26", {"start": v(-90.54, 1574.3) * mm, "end": v(-82.8, 1574.3) * mm});
            skArc(sketch, "E347.0.23.27", {"start": v(-82.8, 1574.3) * mm, "mid": v(-82.66, 1574.37) * mm, "end": v(-82.6, 1574.5) * mm});
            skLineSegment(sketch, "E347.0.24.0", {"start": v(-92.06, 1663.2) * mm, "end": v(-90.74, 1652.5) * mm});
            skLineSegment(sketch, "E347.0.24.1", {"start": v(-139.29, 1663.2) * mm, "end": v(-140.6, 1673.9) * mm});
            skLineSegment(sketch, "E347.0.24.2", {"start": v(-81.29, 1663.2) * mm, "end": v(-82.6, 1673.9) * mm});
            skLineSegment(sketch, "E347.0.24.3", {"start": v(-82.6, 1652.5) * mm, "end": v(-81.29, 1663.2) * mm});
            skLineSegment(sketch, "E347.0.24.4", {"start": v(-140.6, 1652.5) * mm, "end": v(-139.29, 1663.2) * mm});
            skLineSegment(sketch, "E347.0.24.5", {"start": v(-150.06, 1663.2) * mm, "end": v(-148.74, 1652.5) * mm});
            skLineSegment(sketch, "E347.0.24.6", {"start": v(-90.74, 1673.9) * mm, "end": v(-92.06, 1663.2) * mm});
            skLineSegment(sketch, "E347.0.24.7", {"start": v(-148.74, 1673.9) * mm, "end": v(-150.06, 1663.2) * mm});
            skLineSegment(sketch, "E347.0.24.8", {"start": v(-90.74, 1675.7) * mm, "end": v(-90.74, 1673.9) * mm});
            skLineSegment(sketch, "E347.0.24.9", {"start": v(-148.54, 1650.5) * mm, "end": v(-140.8, 1650.5) * mm});
            skArc(sketch, "E347.0.24.10", {"start": v(-82.6, 1675.7) * mm, "mid": v(-82.66, 1675.85) * mm, "end": v(-82.8, 1675.9) * mm});
            skLineSegment(sketch, "E347.0.24.11", {"start": v(-82.8, 1675.9) * mm, "end": v(-90.54, 1675.9) * mm});
            skArc(sketch, "E347.0.24.12", {"start": v(-140.8, 1650.5) * mm, "mid": v(-140.66, 1650.57) * mm, "end": v(-140.6, 1650.7) * mm});
            skLineSegment(sketch, "E347.0.24.13", {"start": v(-82.6, 1673.9) * mm, "end": v(-82.6, 1675.7) * mm});
            skLineSegment(sketch, "E347.0.24.14", {"start": v(-140.6, 1650.7) * mm, "end": v(-140.6, 1652.5) * mm});
            skArc(sketch, "E347.0.24.15", {"start": v(-90.54, 1675.9) * mm, "mid": v(-90.68, 1675.85) * mm, "end": v(-90.74, 1675.7) * mm});
            skLineSegment(sketch, "E347.0.24.16", {"start": v(-140.6, 1673.9) * mm, "end": v(-140.6, 1675.7) * mm});
            skArc(sketch, "E347.0.24.17", {"start": v(-140.6, 1675.7) * mm, "mid": v(-140.66, 1675.85) * mm, "end": v(-140.8, 1675.9) * mm});
            skLineSegment(sketch, "E347.0.24.18", {"start": v(-140.8, 1675.9) * mm, "end": v(-148.54, 1675.9) * mm});
            skArc(sketch, "E347.0.24.19", {"start": v(-90.74, 1650.7) * mm, "mid": v(-90.68, 1650.57) * mm, "end": v(-90.54, 1650.5) * mm});
            skLineSegment(sketch, "E347.0.24.20", {"start": v(-90.74, 1652.5) * mm, "end": v(-90.74, 1650.7) * mm});
            skLineSegment(sketch, "E347.0.24.21", {"start": v(-82.6, 1650.7) * mm, "end": v(-82.6, 1652.5) * mm});
            skArc(sketch, "E347.0.24.22", {"start": v(-148.54, 1675.9) * mm, "mid": v(-148.68, 1675.85) * mm, "end": v(-148.74, 1675.7) * mm});
            skLineSegment(sketch, "E347.0.24.23", {"start": v(-148.74, 1675.7) * mm, "end": v(-148.74, 1673.9) * mm});
            skArc(sketch, "E347.0.24.24", {"start": v(-148.74, 1650.7) * mm, "mid": v(-148.68, 1650.57) * mm, "end": v(-148.54, 1650.5) * mm});
            skLineSegment(sketch, "E347.0.24.25", {"start": v(-148.74, 1652.5) * mm, "end": v(-148.74, 1650.7) * mm});
            skLineSegment(sketch, "E347.0.24.26", {"start": v(-90.54, 1650.5) * mm, "end": v(-82.8, 1650.5) * mm});
            skArc(sketch, "E347.0.24.27", {"start": v(-82.8, 1650.5) * mm, "mid": v(-82.66, 1650.57) * mm, "end": v(-82.6, 1650.7) * mm});
            skLineSegment(sketch, "E347.0.25.0", {"start": v(-92.06, 1739.4) * mm, "end": v(-90.74, 1728.7) * mm});
            skLineSegment(sketch, "E347.0.25.1", {"start": v(-139.29, 1739.4) * mm, "end": v(-140.6, 1750.1) * mm});
            skLineSegment(sketch, "E347.0.25.2", {"start": v(-81.29, 1739.4) * mm, "end": v(-82.6, 1750.1) * mm});
            skLineSegment(sketch, "E347.0.25.3", {"start": v(-82.6, 1728.7) * mm, "end": v(-81.29, 1739.4) * mm});
            skLineSegment(sketch, "E347.0.25.4", {"start": v(-140.6, 1728.7) * mm, "end": v(-139.29, 1739.4) * mm});
            skLineSegment(sketch, "E347.0.25.5", {"start": v(-150.06, 1739.4) * mm, "end": v(-148.74, 1728.7) * mm});
            skLineSegment(sketch, "E347.0.25.6", {"start": v(-90.74, 1750.1) * mm, "end": v(-92.06, 1739.4) * mm});
            skLineSegment(sketch, "E347.0.25.7", {"start": v(-148.74, 1750.1) * mm, "end": v(-150.06, 1739.4) * mm});
            skLineSegment(sketch, "E347.0.25.8", {"start": v(-90.74, 1751.9) * mm, "end": v(-90.74, 1750.1) * mm});
            skLineSegment(sketch, "E347.0.25.9", {"start": v(-148.54, 1726.7) * mm, "end": v(-140.8, 1726.7) * mm});
            skArc(sketch, "E347.0.25.10", {"start": v(-82.6, 1751.9) * mm, "mid": v(-82.66, 1752.05) * mm, "end": v(-82.8, 1752.1) * mm});
            skLineSegment(sketch, "E347.0.25.11", {"start": v(-82.8, 1752.1) * mm, "end": v(-90.54, 1752.1) * mm});
            skArc(sketch, "E347.0.25.12", {"start": v(-140.8, 1726.7) * mm, "mid": v(-140.66, 1726.77) * mm, "end": v(-140.6, 1726.9) * mm});
            skLineSegment(sketch, "E347.0.25.13", {"start": v(-82.6, 1750.1) * mm, "end": v(-82.6, 1751.9) * mm});
            skLineSegment(sketch, "E347.0.25.14", {"start": v(-140.6, 1726.9) * mm, "end": v(-140.6, 1728.7) * mm});
            skArc(sketch, "E347.0.25.15", {"start": v(-90.54, 1752.1) * mm, "mid": v(-90.68, 1752.05) * mm, "end": v(-90.74, 1751.9) * mm});
            skLineSegment(sketch, "E347.0.25.16", {"start": v(-140.6, 1750.1) * mm, "end": v(-140.6, 1751.9) * mm});
            skArc(sketch, "E347.0.25.17", {"start": v(-140.6, 1751.9) * mm, "mid": v(-140.66, 1752.05) * mm, "end": v(-140.8, 1752.1) * mm});
            skLineSegment(sketch, "E347.0.25.18", {"start": v(-140.8, 1752.1) * mm, "end": v(-148.54, 1752.1) * mm});
            skArc(sketch, "E347.0.25.19", {"start": v(-90.74, 1726.9) * mm, "mid": v(-90.68, 1726.77) * mm, "end": v(-90.54, 1726.7) * mm});
            skLineSegment(sketch, "E347.0.25.20", {"start": v(-90.74, 1728.7) * mm, "end": v(-90.74, 1726.9) * mm});
            skLineSegment(sketch, "E347.0.25.21", {"start": v(-82.6, 1726.9) * mm, "end": v(-82.6, 1728.7) * mm});
            skArc(sketch, "E347.0.25.22", {"start": v(-148.54, 1752.1) * mm, "mid": v(-148.68, 1752.05) * mm, "end": v(-148.74, 1751.9) * mm});
            skLineSegment(sketch, "E347.0.25.23", {"start": v(-148.74, 1751.9) * mm, "end": v(-148.74, 1750.1) * mm});
            skArc(sketch, "E347.0.25.24", {"start": v(-148.74, 1726.9) * mm, "mid": v(-148.68, 1726.77) * mm, "end": v(-148.54, 1726.7) * mm});
            skLineSegment(sketch, "E347.0.25.25", {"start": v(-148.74, 1728.7) * mm, "end": v(-148.74, 1726.9) * mm});
            skLineSegment(sketch, "E347.0.25.26", {"start": v(-90.54, 1726.7) * mm, "end": v(-82.8, 1726.7) * mm});
            skArc(sketch, "E347.0.25.27", {"start": v(-82.8, 1726.7) * mm, "mid": v(-82.66, 1726.77) * mm, "end": v(-82.6, 1726.9) * mm});
            skLineSegment(sketch, "E347.0.26.0", {"start": v(-92.06, 1815.6) * mm, "end": v(-90.74, 1804.9) * mm});
            skLineSegment(sketch, "E347.0.26.1", {"start": v(-139.29, 1815.6) * mm, "end": v(-140.6, 1826.3) * mm});
            skLineSegment(sketch, "E347.0.26.2", {"start": v(-81.29, 1815.6) * mm, "end": v(-82.6, 1826.3) * mm});
            skLineSegment(sketch, "E347.0.26.3", {"start": v(-82.6, 1804.9) * mm, "end": v(-81.29, 1815.6) * mm});
            skLineSegment(sketch, "E347.0.26.4", {"start": v(-140.6, 1804.9) * mm, "end": v(-139.29, 1815.6) * mm});
            skLineSegment(sketch, "E347.0.26.5", {"start": v(-150.06, 1815.6) * mm, "end": v(-148.74, 1804.9) * mm});
            skLineSegment(sketch, "E347.0.26.6", {"start": v(-90.74, 1826.3) * mm, "end": v(-92.06, 1815.6) * mm});
            skLineSegment(sketch, "E347.0.26.7", {"start": v(-148.74, 1826.3) * mm, "end": v(-150.06, 1815.6) * mm});
            skLineSegment(sketch, "E347.0.26.8", {"start": v(-90.74, 1828.1) * mm, "end": v(-90.74, 1826.3) * mm});
            skLineSegment(sketch, "E347.0.26.9", {"start": v(-148.54, 1802.9) * mm, "end": v(-140.8, 1802.9) * mm});
            skArc(sketch, "E347.0.26.10", {"start": v(-82.6, 1828.1) * mm, "mid": v(-82.66, 1828.25) * mm, "end": v(-82.8, 1828.3) * mm});
            skLineSegment(sketch, "E347.0.26.11", {"start": v(-82.8, 1828.3) * mm, "end": v(-90.54, 1828.3) * mm});
            skArc(sketch, "E347.0.26.12", {"start": v(-140.8, 1802.9) * mm, "mid": v(-140.66, 1802.97) * mm, "end": v(-140.6, 1803.1) * mm});
            skLineSegment(sketch, "E347.0.26.13", {"start": v(-82.6, 1826.3) * mm, "end": v(-82.6, 1828.1) * mm});
            skLineSegment(sketch, "E347.0.26.14", {"start": v(-140.6, 1803.1) * mm, "end": v(-140.6, 1804.9) * mm});
            skArc(sketch, "E347.0.26.15", {"start": v(-90.54, 1828.3) * mm, "mid": v(-90.68, 1828.25) * mm, "end": v(-90.74, 1828.1) * mm});
            skLineSegment(sketch, "E347.0.26.16", {"start": v(-140.6, 1826.3) * mm, "end": v(-140.6, 1828.1) * mm});
            skArc(sketch, "E347.0.26.17", {"start": v(-140.6, 1828.1) * mm, "mid": v(-140.66, 1828.25) * mm, "end": v(-140.8, 1828.3) * mm});
            skLineSegment(sketch, "E347.0.26.18", {"start": v(-140.8, 1828.3) * mm, "end": v(-148.54, 1828.3) * mm});
            skArc(sketch, "E347.0.26.19", {"start": v(-90.74, 1803.1) * mm, "mid": v(-90.68, 1802.97) * mm, "end": v(-90.54, 1802.9) * mm});
            skLineSegment(sketch, "E347.0.26.20", {"start": v(-90.74, 1804.9) * mm, "end": v(-90.74, 1803.1) * mm});
            skLineSegment(sketch, "E347.0.26.21", {"start": v(-82.6, 1803.1) * mm, "end": v(-82.6, 1804.9) * mm});
            skArc(sketch, "E347.0.26.22", {"start": v(-148.54, 1828.3) * mm, "mid": v(-148.68, 1828.25) * mm, "end": v(-148.74, 1828.1) * mm});
            skLineSegment(sketch, "E347.0.26.23", {"start": v(-148.74, 1828.1) * mm, "end": v(-148.74, 1826.3) * mm});
            skArc(sketch, "E347.0.26.24", {"start": v(-148.74, 1803.1) * mm, "mid": v(-148.68, 1802.97) * mm, "end": v(-148.54, 1802.9) * mm});
            skLineSegment(sketch, "E347.0.26.25", {"start": v(-148.74, 1804.9) * mm, "end": v(-148.74, 1803.1) * mm});
            skLineSegment(sketch, "E347.0.26.26", {"start": v(-90.54, 1802.9) * mm, "end": v(-82.8, 1802.9) * mm});
            skArc(sketch, "E347.0.26.27", {"start": v(-82.8, 1802.9) * mm, "mid": v(-82.66, 1802.97) * mm, "end": v(-82.6, 1803.1) * mm});
            skLineSegment(sketch, "E347.0.27.0", {"start": v(-92.06, 1891.8) * mm, "end": v(-90.74, 1881.1) * mm});
            skLineSegment(sketch, "E347.0.27.1", {"start": v(-139.29, 1891.8) * mm, "end": v(-140.6, 1902.5) * mm});
            skLineSegment(sketch, "E347.0.27.2", {"start": v(-81.29, 1891.8) * mm, "end": v(-82.6, 1902.5) * mm});
            skLineSegment(sketch, "E347.0.27.3", {"start": v(-82.6, 1881.1) * mm, "end": v(-81.29, 1891.8) * mm});
            skLineSegment(sketch, "E347.0.27.4", {"start": v(-140.6, 1881.1) * mm, "end": v(-139.29, 1891.8) * mm});
            skLineSegment(sketch, "E347.0.27.5", {"start": v(-150.06, 1891.8) * mm, "end": v(-148.74, 1881.1) * mm});
            skLineSegment(sketch, "E347.0.27.6", {"start": v(-90.74, 1902.5) * mm, "end": v(-92.06, 1891.8) * mm});
            skLineSegment(sketch, "E347.0.27.7", {"start": v(-148.74, 1902.5) * mm, "end": v(-150.06, 1891.8) * mm});
            skLineSegment(sketch, "E347.0.27.8", {"start": v(-90.74, 1904.3) * mm, "end": v(-90.74, 1902.5) * mm});
            skLineSegment(sketch, "E347.0.27.9", {"start": v(-148.54, 1879.1) * mm, "end": v(-140.8, 1879.1) * mm});
            skArc(sketch, "E347.0.27.10", {"start": v(-82.6, 1904.3) * mm, "mid": v(-82.66, 1904.45) * mm, "end": v(-82.8, 1904.5) * mm});
            skLineSegment(sketch, "E347.0.27.11", {"start": v(-82.8, 1904.5) * mm, "end": v(-90.54, 1904.5) * mm});
            skArc(sketch, "E347.0.27.12", {"start": v(-140.8, 1879.1) * mm, "mid": v(-140.66, 1879.17) * mm, "end": v(-140.6, 1879.3) * mm});
            skLineSegment(sketch, "E347.0.27.13", {"start": v(-82.6, 1902.5) * mm, "end": v(-82.6, 1904.3) * mm});
            skLineSegment(sketch, "E347.0.27.14", {"start": v(-140.6, 1879.3) * mm, "end": v(-140.6, 1881.1) * mm});
            skArc(sketch, "E347.0.27.15", {"start": v(-90.54, 1904.5) * mm, "mid": v(-90.68, 1904.45) * mm, "end": v(-90.74, 1904.3) * mm});
            skLineSegment(sketch, "E347.0.27.16", {"start": v(-140.6, 1902.5) * mm, "end": v(-140.6, 1904.3) * mm});
            skArc(sketch, "E347.0.27.17", {"start": v(-140.6, 1904.3) * mm, "mid": v(-140.66, 1904.45) * mm, "end": v(-140.8, 1904.5) * mm});
            skLineSegment(sketch, "E347.0.27.18", {"start": v(-140.8, 1904.5) * mm, "end": v(-148.54, 1904.5) * mm});
            skArc(sketch, "E347.0.27.19", {"start": v(-90.74, 1879.3) * mm, "mid": v(-90.68, 1879.17) * mm, "end": v(-90.54, 1879.1) * mm});
            skLineSegment(sketch, "E347.0.27.20", {"start": v(-90.74, 1881.1) * mm, "end": v(-90.74, 1879.3) * mm});
            skLineSegment(sketch, "E347.0.27.21", {"start": v(-82.6, 1879.3) * mm, "end": v(-82.6, 1881.1) * mm});
            skArc(sketch, "E347.0.27.22", {"start": v(-148.54, 1904.5) * mm, "mid": v(-148.68, 1904.45) * mm, "end": v(-148.74, 1904.3) * mm});
            skLineSegment(sketch, "E347.0.27.23", {"start": v(-148.74, 1904.3) * mm, "end": v(-148.74, 1902.5) * mm});
            skArc(sketch, "E347.0.27.24", {"start": v(-148.74, 1879.3) * mm, "mid": v(-148.68, 1879.17) * mm, "end": v(-148.54, 1879.1) * mm});
            skLineSegment(sketch, "E347.0.27.25", {"start": v(-148.74, 1881.1) * mm, "end": v(-148.74, 1879.3) * mm});
            skLineSegment(sketch, "E347.0.27.26", {"start": v(-90.54, 1879.1) * mm, "end": v(-82.8, 1879.1) * mm});
            skArc(sketch, "E347.0.27.27", {"start": v(-82.8, 1879.1) * mm, "mid": v(-82.66, 1879.17) * mm, "end": v(-82.6, 1879.3) * mm});
            skLineSegment(sketch, "E347.0.28.0", {"start": v(-92.06, 1968) * mm, "end": v(-90.74, 1957.3) * mm});
            skLineSegment(sketch, "E347.0.28.1", {"start": v(-139.29, 1968) * mm, "end": v(-140.6, 1978.7) * mm});
            skLineSegment(sketch, "E347.0.28.2", {"start": v(-81.29, 1968) * mm, "end": v(-82.6, 1978.7) * mm});
            skLineSegment(sketch, "E347.0.28.3", {"start": v(-82.6, 1957.3) * mm, "end": v(-81.29, 1968) * mm});
            skLineSegment(sketch, "E347.0.28.4", {"start": v(-140.6, 1957.3) * mm, "end": v(-139.29, 1968) * mm});
            skLineSegment(sketch, "E347.0.28.5", {"start": v(-150.06, 1968) * mm, "end": v(-148.74, 1957.3) * mm});
            skLineSegment(sketch, "E347.0.28.6", {"start": v(-90.74, 1978.7) * mm, "end": v(-92.06, 1968) * mm});
            skLineSegment(sketch, "E347.0.28.7", {"start": v(-148.74, 1978.7) * mm, "end": v(-150.06, 1968) * mm});
            skLineSegment(sketch, "E347.0.28.8", {"start": v(-90.74, 1980.5) * mm, "end": v(-90.74, 1978.7) * mm});
            skLineSegment(sketch, "E347.0.28.9", {"start": v(-148.54, 1955.3) * mm, "end": v(-140.8, 1955.3) * mm});
            skArc(sketch, "E347.0.28.10", {"start": v(-82.6, 1980.5) * mm, "mid": v(-82.66, 1980.65) * mm, "end": v(-82.8, 1980.7) * mm});
            skLineSegment(sketch, "E347.0.28.11", {"start": v(-82.8, 1980.7) * mm, "end": v(-90.54, 1980.7) * mm});
            skArc(sketch, "E347.0.28.12", {"start": v(-140.8, 1955.3) * mm, "mid": v(-140.66, 1955.37) * mm, "end": v(-140.6, 1955.5) * mm});
            skLineSegment(sketch, "E347.0.28.13", {"start": v(-82.6, 1978.7) * mm, "end": v(-82.6, 1980.5) * mm});
            skLineSegment(sketch, "E347.0.28.14", {"start": v(-140.6, 1955.5) * mm, "end": v(-140.6, 1957.3) * mm});
            skArc(sketch, "E347.0.28.15", {"start": v(-90.54, 1980.7) * mm, "mid": v(-90.68, 1980.65) * mm, "end": v(-90.74, 1980.5) * mm});
            skLineSegment(sketch, "E347.0.28.16", {"start": v(-140.6, 1978.7) * mm, "end": v(-140.6, 1980.5) * mm});
            skArc(sketch, "E347.0.28.17", {"start": v(-140.6, 1980.5) * mm, "mid": v(-140.66, 1980.65) * mm, "end": v(-140.8, 1980.7) * mm});
            skLineSegment(sketch, "E347.0.28.18", {"start": v(-140.8, 1980.7) * mm, "end": v(-148.54, 1980.7) * mm});
            skArc(sketch, "E347.0.28.19", {"start": v(-90.74, 1955.5) * mm, "mid": v(-90.68, 1955.37) * mm, "end": v(-90.54, 1955.3) * mm});
            skLineSegment(sketch, "E347.0.28.20", {"start": v(-90.74, 1957.3) * mm, "end": v(-90.74, 1955.5) * mm});
            skLineSegment(sketch, "E347.0.28.21", {"start": v(-82.6, 1955.5) * mm, "end": v(-82.6, 1957.3) * mm});
            skArc(sketch, "E347.0.28.22", {"start": v(-148.54, 1980.7) * mm, "mid": v(-148.68, 1980.65) * mm, "end": v(-148.74, 1980.5) * mm});
            skLineSegment(sketch, "E347.0.28.23", {"start": v(-148.74, 1980.5) * mm, "end": v(-148.74, 1978.7) * mm});
            skArc(sketch, "E347.0.28.24", {"start": v(-148.74, 1955.5) * mm, "mid": v(-148.68, 1955.37) * mm, "end": v(-148.54, 1955.3) * mm});
            skLineSegment(sketch, "E347.0.28.25", {"start": v(-148.74, 1957.3) * mm, "end": v(-148.74, 1955.5) * mm});
            skLineSegment(sketch, "E347.0.28.26", {"start": v(-90.54, 1955.3) * mm, "end": v(-82.8, 1955.3) * mm});
            skArc(sketch, "E347.0.28.27", {"start": v(-82.8, 1955.3) * mm, "mid": v(-82.66, 1955.37) * mm, "end": v(-82.6, 1955.5) * mm});
            skLineSegment(sketch, "E347.0.29.0", {"start": v(-92.06, 2044.2) * mm, "end": v(-90.74, 2033.5) * mm});
            skLineSegment(sketch, "E347.0.29.1", {"start": v(-139.29, 2044.2) * mm, "end": v(-140.6, 2054.9) * mm});
            skLineSegment(sketch, "E347.0.29.2", {"start": v(-81.29, 2044.2) * mm, "end": v(-82.6, 2054.9) * mm});
            skLineSegment(sketch, "E347.0.29.3", {"start": v(-82.6, 2033.5) * mm, "end": v(-81.29, 2044.2) * mm});
            skLineSegment(sketch, "E347.0.29.4", {"start": v(-140.6, 2033.5) * mm, "end": v(-139.29, 2044.2) * mm});
            skLineSegment(sketch, "E347.0.29.5", {"start": v(-150.06, 2044.2) * mm, "end": v(-148.74, 2033.5) * mm});
            skLineSegment(sketch, "E347.0.29.6", {"start": v(-90.74, 2054.9) * mm, "end": v(-92.06, 2044.2) * mm});
            skLineSegment(sketch, "E347.0.29.7", {"start": v(-148.74, 2054.9) * mm, "end": v(-150.06, 2044.2) * mm});
            skLineSegment(sketch, "E347.0.29.8", {"start": v(-90.74, 2056.7) * mm, "end": v(-90.74, 2054.9) * mm});
            skLineSegment(sketch, "E347.0.29.9", {"start": v(-148.54, 2031.5) * mm, "end": v(-140.8, 2031.5) * mm});
            skArc(sketch, "E347.0.29.10", {"start": v(-82.6, 2056.7) * mm, "mid": v(-82.66, 2056.85) * mm, "end": v(-82.8, 2056.9) * mm});
            skLineSegment(sketch, "E347.0.29.11", {"start": v(-82.8, 2056.9) * mm, "end": v(-90.54, 2056.9) * mm});
            skArc(sketch, "E347.0.29.12", {"start": v(-140.8, 2031.5) * mm, "mid": v(-140.66, 2031.57) * mm, "end": v(-140.6, 2031.7) * mm});
            skLineSegment(sketch, "E347.0.29.13", {"start": v(-82.6, 2054.9) * mm, "end": v(-82.6, 2056.7) * mm});
            skLineSegment(sketch, "E347.0.29.14", {"start": v(-140.6, 2031.7) * mm, "end": v(-140.6, 2033.5) * mm});
            skArc(sketch, "E347.0.29.15", {"start": v(-90.54, 2056.9) * mm, "mid": v(-90.68, 2056.85) * mm, "end": v(-90.74, 2056.7) * mm});
            skLineSegment(sketch, "E347.0.29.16", {"start": v(-140.6, 2054.9) * mm, "end": v(-140.6, 2056.7) * mm});
            skArc(sketch, "E347.0.29.17", {"start": v(-140.6, 2056.7) * mm, "mid": v(-140.66, 2056.85) * mm, "end": v(-140.8, 2056.9) * mm});
            skLineSegment(sketch, "E347.0.29.18", {"start": v(-140.8, 2056.9) * mm, "end": v(-148.54, 2056.9) * mm});
            skArc(sketch, "E347.0.29.19", {"start": v(-90.74, 2031.7) * mm, "mid": v(-90.68, 2031.57) * mm, "end": v(-90.54, 2031.5) * mm});
            skLineSegment(sketch, "E347.0.29.20", {"start": v(-90.74, 2033.5) * mm, "end": v(-90.74, 2031.7) * mm});
            skLineSegment(sketch, "E347.0.29.21", {"start": v(-82.6, 2031.7) * mm, "end": v(-82.6, 2033.5) * mm});
            skArc(sketch, "E347.0.29.22", {"start": v(-148.54, 2056.9) * mm, "mid": v(-148.68, 2056.85) * mm, "end": v(-148.74, 2056.7) * mm});
            skLineSegment(sketch, "E347.0.29.23", {"start": v(-148.74, 2056.7) * mm, "end": v(-148.74, 2054.9) * mm});
            skArc(sketch, "E347.0.29.24", {"start": v(-148.74, 2031.7) * mm, "mid": v(-148.68, 2031.57) * mm, "end": v(-148.54, 2031.5) * mm});
            skLineSegment(sketch, "E347.0.29.25", {"start": v(-148.74, 2033.5) * mm, "end": v(-148.74, 2031.7) * mm});
            skLineSegment(sketch, "E347.0.29.26", {"start": v(-90.54, 2031.5) * mm, "end": v(-82.8, 2031.5) * mm});
            skArc(sketch, "E347.0.29.27", {"start": v(-82.8, 2031.5) * mm, "mid": v(-82.66, 2031.57) * mm, "end": v(-82.6, 2031.7) * mm});
            skLineSegment(sketch, "E347.0.30.0", {"start": v(-92.06, 2120.4) * mm, "end": v(-90.74, 2109.7) * mm});
            skLineSegment(sketch, "E347.0.30.1", {"start": v(-139.29, 2120.4) * mm, "end": v(-140.6, 2131.1) * mm});
            skLineSegment(sketch, "E347.0.30.2", {"start": v(-81.29, 2120.4) * mm, "end": v(-82.6, 2131.1) * mm});
            skLineSegment(sketch, "E347.0.30.3", {"start": v(-82.6, 2109.7) * mm, "end": v(-81.29, 2120.4) * mm});
            skLineSegment(sketch, "E347.0.30.4", {"start": v(-140.6, 2109.7) * mm, "end": v(-139.29, 2120.4) * mm});
            skLineSegment(sketch, "E347.0.30.5", {"start": v(-150.06, 2120.4) * mm, "end": v(-148.74, 2109.7) * mm});
            skLineSegment(sketch, "E347.0.30.6", {"start": v(-90.74, 2131.1) * mm, "end": v(-92.06, 2120.4) * mm});
            skLineSegment(sketch, "E347.0.30.7", {"start": v(-148.74, 2131.1) * mm, "end": v(-150.06, 2120.4) * mm});
            skLineSegment(sketch, "E347.0.30.8", {"start": v(-90.74, 2132.9) * mm, "end": v(-90.74, 2131.1) * mm});
            skLineSegment(sketch, "E347.0.30.9", {"start": v(-148.54, 2107.7) * mm, "end": v(-140.8, 2107.7) * mm});
            skArc(sketch, "E347.0.30.10", {"start": v(-82.6, 2132.9) * mm, "mid": v(-82.66, 2133.05) * mm, "end": v(-82.8, 2133.1) * mm});
            skLineSegment(sketch, "E347.0.30.11", {"start": v(-82.8, 2133.1) * mm, "end": v(-90.54, 2133.1) * mm});
            skArc(sketch, "E347.0.30.12", {"start": v(-140.8, 2107.7) * mm, "mid": v(-140.66, 2107.77) * mm, "end": v(-140.6, 2107.9) * mm});
            skLineSegment(sketch, "E347.0.30.13", {"start": v(-82.6, 2131.1) * mm, "end": v(-82.6, 2132.9) * mm});
            skLineSegment(sketch, "E347.0.30.14", {"start": v(-140.6, 2107.9) * mm, "end": v(-140.6, 2109.7) * mm});
            skArc(sketch, "E347.0.30.15", {"start": v(-90.54, 2133.1) * mm, "mid": v(-90.68, 2133.05) * mm, "end": v(-90.74, 2132.9) * mm});
            skLineSegment(sketch, "E347.0.30.16", {"start": v(-140.6, 2131.1) * mm, "end": v(-140.6, 2132.9) * mm});
            skArc(sketch, "E347.0.30.17", {"start": v(-140.6, 2132.9) * mm, "mid": v(-140.66, 2133.05) * mm, "end": v(-140.8, 2133.1) * mm});
            skLineSegment(sketch, "E347.0.30.18", {"start": v(-140.8, 2133.1) * mm, "end": v(-148.54, 2133.1) * mm});
            skArc(sketch, "E347.0.30.19", {"start": v(-90.74, 2107.9) * mm, "mid": v(-90.68, 2107.77) * mm, "end": v(-90.54, 2107.7) * mm});
            skLineSegment(sketch, "E347.0.30.20", {"start": v(-90.74, 2109.7) * mm, "end": v(-90.74, 2107.9) * mm});
            skLineSegment(sketch, "E347.0.30.21", {"start": v(-82.6, 2107.9) * mm, "end": v(-82.6, 2109.7) * mm});
            skArc(sketch, "E347.0.30.22", {"start": v(-148.54, 2133.1) * mm, "mid": v(-148.68, 2133.05) * mm, "end": v(-148.74, 2132.9) * mm});
            skLineSegment(sketch, "E347.0.30.23", {"start": v(-148.74, 2132.9) * mm, "end": v(-148.74, 2131.1) * mm});
            skArc(sketch, "E347.0.30.24", {"start": v(-148.74, 2107.9) * mm, "mid": v(-148.68, 2107.77) * mm, "end": v(-148.54, 2107.7) * mm});
            skLineSegment(sketch, "E347.0.30.25", {"start": v(-148.74, 2109.7) * mm, "end": v(-148.74, 2107.9) * mm});
            skLineSegment(sketch, "E347.0.30.26", {"start": v(-90.54, 2107.7) * mm, "end": v(-82.8, 2107.7) * mm});
            skArc(sketch, "E347.0.30.27", {"start": v(-82.8, 2107.7) * mm, "mid": v(-82.66, 2107.77) * mm, "end": v(-82.6, 2107.9) * mm});
            skLineSegment(sketch, "E347.0.31.0", {"start": v(-92.06, 2196.6) * mm, "end": v(-90.74, 2185.9) * mm});
            skLineSegment(sketch, "E347.0.31.1", {"start": v(-139.29, 2196.6) * mm, "end": v(-140.6, 2207.3) * mm});
            skLineSegment(sketch, "E347.0.31.2", {"start": v(-81.29, 2196.6) * mm, "end": v(-82.6, 2207.3) * mm});
            skLineSegment(sketch, "E347.0.31.3", {"start": v(-82.6, 2185.9) * mm, "end": v(-81.29, 2196.6) * mm});
            skLineSegment(sketch, "E347.0.31.4", {"start": v(-140.6, 2185.9) * mm, "end": v(-139.29, 2196.6) * mm});
            skLineSegment(sketch, "E347.0.31.5", {"start": v(-150.06, 2196.6) * mm, "end": v(-148.74, 2185.9) * mm});
            skLineSegment(sketch, "E347.0.31.6", {"start": v(-90.74, 2207.3) * mm, "end": v(-92.06, 2196.6) * mm});
            skLineSegment(sketch, "E347.0.31.7", {"start": v(-148.74, 2207.3) * mm, "end": v(-150.06, 2196.6) * mm});
            skLineSegment(sketch, "E347.0.31.8", {"start": v(-90.74, 2209.1) * mm, "end": v(-90.74, 2207.3) * mm});
            skLineSegment(sketch, "E347.0.31.9", {"start": v(-148.54, 2183.9) * mm, "end": v(-140.8, 2183.9) * mm});
            skArc(sketch, "E347.0.31.10", {"start": v(-82.6, 2209.1) * mm, "mid": v(-82.66, 2209.25) * mm, "end": v(-82.8, 2209.3) * mm});
            skLineSegment(sketch, "E347.0.31.11", {"start": v(-82.8, 2209.3) * mm, "end": v(-90.54, 2209.3) * mm});
            skArc(sketch, "E347.0.31.12", {"start": v(-140.8, 2183.9) * mm, "mid": v(-140.66, 2183.97) * mm, "end": v(-140.6, 2184.1) * mm});
            skLineSegment(sketch, "E347.0.31.13", {"start": v(-82.6, 2207.3) * mm, "end": v(-82.6, 2209.1) * mm});
            skLineSegment(sketch, "E347.0.31.14", {"start": v(-140.6, 2184.1) * mm, "end": v(-140.6, 2185.9) * mm});
            skArc(sketch, "E347.0.31.15", {"start": v(-90.54, 2209.3) * mm, "mid": v(-90.68, 2209.25) * mm, "end": v(-90.74, 2209.1) * mm});
            skLineSegment(sketch, "E347.0.31.16", {"start": v(-140.6, 2207.3) * mm, "end": v(-140.6, 2209.1) * mm});
            skArc(sketch, "E347.0.31.17", {"start": v(-140.6, 2209.1) * mm, "mid": v(-140.66, 2209.25) * mm, "end": v(-140.8, 2209.3) * mm});
            skLineSegment(sketch, "E347.0.31.18", {"start": v(-140.8, 2209.3) * mm, "end": v(-148.54, 2209.3) * mm});
            skArc(sketch, "E347.0.31.19", {"start": v(-90.74, 2184.1) * mm, "mid": v(-90.68, 2183.97) * mm, "end": v(-90.54, 2183.9) * mm});
            skLineSegment(sketch, "E347.0.31.20", {"start": v(-90.74, 2185.9) * mm, "end": v(-90.74, 2184.1) * mm});
            skLineSegment(sketch, "E347.0.31.21", {"start": v(-82.6, 2184.1) * mm, "end": v(-82.6, 2185.9) * mm});
            skArc(sketch, "E347.0.31.22", {"start": v(-148.54, 2209.3) * mm, "mid": v(-148.68, 2209.25) * mm, "end": v(-148.74, 2209.1) * mm});
            skLineSegment(sketch, "E347.0.31.23", {"start": v(-148.74, 2209.1) * mm, "end": v(-148.74, 2207.3) * mm});
            skArc(sketch, "E347.0.31.24", {"start": v(-148.74, 2184.1) * mm, "mid": v(-148.68, 2183.97) * mm, "end": v(-148.54, 2183.9) * mm});
            skLineSegment(sketch, "E347.0.31.25", {"start": v(-148.74, 2185.9) * mm, "end": v(-148.74, 2184.1) * mm});
            skLineSegment(sketch, "E347.0.31.26", {"start": v(-90.54, 2183.9) * mm, "end": v(-82.8, 2183.9) * mm});
            skArc(sketch, "E347.0.31.27", {"start": v(-82.8, 2183.9) * mm, "mid": v(-82.66, 2183.97) * mm, "end": v(-82.6, 2184.1) * mm});
            skLineSegment(sketch, "E347.0.32.0", {"start": v(-92.06, 2272.8) * mm, "end": v(-90.74, 2262.1) * mm});
            skLineSegment(sketch, "E347.0.32.1", {"start": v(-139.29, 2272.8) * mm, "end": v(-140.6, 2283.5) * mm});
            skLineSegment(sketch, "E347.0.32.2", {"start": v(-81.29, 2272.8) * mm, "end": v(-82.6, 2283.5) * mm});
            skLineSegment(sketch, "E347.0.32.3", {"start": v(-82.6, 2262.1) * mm, "end": v(-81.29, 2272.8) * mm});
            skLineSegment(sketch, "E347.0.32.4", {"start": v(-140.6, 2262.1) * mm, "end": v(-139.29, 2272.8) * mm});
            skLineSegment(sketch, "E347.0.32.5", {"start": v(-150.06, 2272.8) * mm, "end": v(-148.74, 2262.1) * mm});
            skLineSegment(sketch, "E347.0.32.6", {"start": v(-90.74, 2283.5) * mm, "end": v(-92.06, 2272.8) * mm});
            skLineSegment(sketch, "E347.0.32.7", {"start": v(-148.74, 2283.5) * mm, "end": v(-150.06, 2272.8) * mm});
            skLineSegment(sketch, "E347.0.32.8", {"start": v(-90.74, 2285.3) * mm, "end": v(-90.74, 2283.5) * mm});
            skLineSegment(sketch, "E347.0.32.9", {"start": v(-148.54, 2260.1) * mm, "end": v(-140.8, 2260.1) * mm});
            skArc(sketch, "E347.0.32.10", {"start": v(-82.6, 2285.3) * mm, "mid": v(-82.66, 2285.45) * mm, "end": v(-82.8, 2285.5) * mm});
            skLineSegment(sketch, "E347.0.32.11", {"start": v(-82.8, 2285.5) * mm, "end": v(-90.54, 2285.5) * mm});
            skArc(sketch, "E347.0.32.12", {"start": v(-140.8, 2260.1) * mm, "mid": v(-140.66, 2260.17) * mm, "end": v(-140.6, 2260.3) * mm});
            skLineSegment(sketch, "E347.0.32.13", {"start": v(-82.6, 2283.5) * mm, "end": v(-82.6, 2285.3) * mm});
            skLineSegment(sketch, "E347.0.32.14", {"start": v(-140.6, 2260.3) * mm, "end": v(-140.6, 2262.1) * mm});
            skArc(sketch, "E347.0.32.15", {"start": v(-90.54, 2285.5) * mm, "mid": v(-90.68, 2285.45) * mm, "end": v(-90.74, 2285.3) * mm});
            skLineSegment(sketch, "E347.0.32.16", {"start": v(-140.6, 2283.5) * mm, "end": v(-140.6, 2285.3) * mm});
            skArc(sketch, "E347.0.32.17", {"start": v(-140.6, 2285.3) * mm, "mid": v(-140.66, 2285.45) * mm, "end": v(-140.8, 2285.5) * mm});
            skLineSegment(sketch, "E347.0.32.18", {"start": v(-140.8, 2285.5) * mm, "end": v(-148.54, 2285.5) * mm});
            skArc(sketch, "E347.0.32.19", {"start": v(-90.74, 2260.3) * mm, "mid": v(-90.68, 2260.17) * mm, "end": v(-90.54, 2260.1) * mm});
            skLineSegment(sketch, "E347.0.32.20", {"start": v(-90.74, 2262.1) * mm, "end": v(-90.74, 2260.3) * mm});
            skLineSegment(sketch, "E347.0.32.21", {"start": v(-82.6, 2260.3) * mm, "end": v(-82.6, 2262.1) * mm});
            skArc(sketch, "E347.0.32.22", {"start": v(-148.54, 2285.5) * mm, "mid": v(-148.68, 2285.45) * mm, "end": v(-148.74, 2285.3) * mm});
            skLineSegment(sketch, "E347.0.32.23", {"start": v(-148.74, 2285.3) * mm, "end": v(-148.74, 2283.5) * mm});
            skArc(sketch, "E347.0.32.24", {"start": v(-148.74, 2260.3) * mm, "mid": v(-148.68, 2260.17) * mm, "end": v(-148.54, 2260.1) * mm});
            skLineSegment(sketch, "E347.0.32.25", {"start": v(-148.74, 2262.1) * mm, "end": v(-148.74, 2260.3) * mm});
            skLineSegment(sketch, "E347.0.32.26", {"start": v(-90.54, 2260.1) * mm, "end": v(-82.8, 2260.1) * mm});
            skArc(sketch, "E347.0.32.27", {"start": v(-82.8, 2260.1) * mm, "mid": v(-82.66, 2260.17) * mm, "end": v(-82.6, 2260.3) * mm});
            skLineSegment(sketch, "E347.0.33.0", {"start": v(-92.06, 2349) * mm, "end": v(-90.74, 2338.3) * mm});
            skLineSegment(sketch, "E347.0.33.1", {"start": v(-139.29, 2349) * mm, "end": v(-140.6, 2359.7) * mm});
            skLineSegment(sketch, "E347.0.33.2", {"start": v(-81.29, 2349) * mm, "end": v(-82.6, 2359.7) * mm});
            skLineSegment(sketch, "E347.0.33.3", {"start": v(-82.6, 2338.3) * mm, "end": v(-81.29, 2349) * mm});
            skLineSegment(sketch, "E347.0.33.4", {"start": v(-140.6, 2338.3) * mm, "end": v(-139.29, 2349) * mm});
            skLineSegment(sketch, "E347.0.33.5", {"start": v(-150.06, 2349) * mm, "end": v(-148.74, 2338.3) * mm});
            skLineSegment(sketch, "E347.0.33.6", {"start": v(-90.74, 2359.7) * mm, "end": v(-92.06, 2349) * mm});
            skLineSegment(sketch, "E347.0.33.7", {"start": v(-148.74, 2359.7) * mm, "end": v(-150.06, 2349) * mm});
            skLineSegment(sketch, "E347.0.33.8", {"start": v(-90.74, 2361.5) * mm, "end": v(-90.74, 2359.7) * mm});
            skLineSegment(sketch, "E347.0.33.9", {"start": v(-148.54, 2336.3) * mm, "end": v(-140.8, 2336.3) * mm});
            skArc(sketch, "E347.0.33.10", {"start": v(-82.6, 2361.5) * mm, "mid": v(-82.66, 2361.65) * mm, "end": v(-82.8, 2361.7) * mm});
            skLineSegment(sketch, "E347.0.33.11", {"start": v(-82.8, 2361.7) * mm, "end": v(-90.54, 2361.7) * mm});
            skArc(sketch, "E347.0.33.12", {"start": v(-140.8, 2336.3) * mm, "mid": v(-140.66, 2336.37) * mm, "end": v(-140.6, 2336.5) * mm});
            skLineSegment(sketch, "E347.0.33.13", {"start": v(-82.6, 2359.7) * mm, "end": v(-82.6, 2361.5) * mm});
            skLineSegment(sketch, "E347.0.33.14", {"start": v(-140.6, 2336.5) * mm, "end": v(-140.6, 2338.3) * mm});
            skArc(sketch, "E347.0.33.15", {"start": v(-90.54, 2361.7) * mm, "mid": v(-90.68, 2361.65) * mm, "end": v(-90.74, 2361.5) * mm});
            skLineSegment(sketch, "E347.0.33.16", {"start": v(-140.6, 2359.7) * mm, "end": v(-140.6, 2361.5) * mm});
            skArc(sketch, "E347.0.33.17", {"start": v(-140.6, 2361.5) * mm, "mid": v(-140.66, 2361.65) * mm, "end": v(-140.8, 2361.7) * mm});
            skLineSegment(sketch, "E347.0.33.18", {"start": v(-140.8, 2361.7) * mm, "end": v(-148.54, 2361.7) * mm});
            skArc(sketch, "E347.0.33.19", {"start": v(-90.74, 2336.5) * mm, "mid": v(-90.68, 2336.37) * mm, "end": v(-90.54, 2336.3) * mm});
            skLineSegment(sketch, "E347.0.33.20", {"start": v(-90.74, 2338.3) * mm, "end": v(-90.74, 2336.5) * mm});
            skLineSegment(sketch, "E347.0.33.21", {"start": v(-82.6, 2336.5) * mm, "end": v(-82.6, 2338.3) * mm});
            skArc(sketch, "E347.0.33.22", {"start": v(-148.54, 2361.7) * mm, "mid": v(-148.68, 2361.65) * mm, "end": v(-148.74, 2361.5) * mm});
            skLineSegment(sketch, "E347.0.33.23", {"start": v(-148.74, 2361.5) * mm, "end": v(-148.74, 2359.7) * mm});
            skArc(sketch, "E347.0.33.24", {"start": v(-148.74, 2336.5) * mm, "mid": v(-148.68, 2336.37) * mm, "end": v(-148.54, 2336.3) * mm});
            skLineSegment(sketch, "E347.0.33.25", {"start": v(-148.74, 2338.3) * mm, "end": v(-148.74, 2336.5) * mm});
            skLineSegment(sketch, "E347.0.33.26", {"start": v(-90.54, 2336.3) * mm, "end": v(-82.8, 2336.3) * mm});
            skArc(sketch, "E347.0.33.27", {"start": v(-82.8, 2336.3) * mm, "mid": v(-82.66, 2336.37) * mm, "end": v(-82.6, 2336.5) * mm});
            skLineSegment(sketch, "E347.0.34.0", {"start": v(-92.06, 2425.2) * mm, "end": v(-90.74, 2414.5) * mm});
            skLineSegment(sketch, "E347.0.34.1", {"start": v(-139.29, 2425.2) * mm, "end": v(-140.6, 2435.9) * mm});
            skLineSegment(sketch, "E347.0.34.2", {"start": v(-81.29, 2425.2) * mm, "end": v(-82.6, 2435.9) * mm});
            skLineSegment(sketch, "E347.0.34.3", {"start": v(-82.6, 2414.5) * mm, "end": v(-81.29, 2425.2) * mm});
            skLineSegment(sketch, "E347.0.34.4", {"start": v(-140.6, 2414.5) * mm, "end": v(-139.29, 2425.2) * mm});
            skLineSegment(sketch, "E347.0.34.5", {"start": v(-150.06, 2425.2) * mm, "end": v(-148.74, 2414.5) * mm});
            skLineSegment(sketch, "E347.0.34.6", {"start": v(-90.74, 2435.9) * mm, "end": v(-92.06, 2425.2) * mm});
            skLineSegment(sketch, "E347.0.34.7", {"start": v(-148.74, 2435.9) * mm, "end": v(-150.06, 2425.2) * mm});
            skLineSegment(sketch, "E347.0.34.8", {"start": v(-90.74, 2437.7) * mm, "end": v(-90.74, 2435.9) * mm});
            skLineSegment(sketch, "E347.0.34.9", {"start": v(-148.54, 2412.5) * mm, "end": v(-140.8, 2412.5) * mm});
            skArc(sketch, "E347.0.34.10", {"start": v(-82.6, 2437.7) * mm, "mid": v(-82.66, 2437.85) * mm, "end": v(-82.8, 2437.9) * mm});
            skLineSegment(sketch, "E347.0.34.11", {"start": v(-82.8, 2437.9) * mm, "end": v(-90.54, 2437.9) * mm});
            skArc(sketch, "E347.0.34.12", {"start": v(-140.8, 2412.5) * mm, "mid": v(-140.66, 2412.57) * mm, "end": v(-140.6, 2412.7) * mm});
            skLineSegment(sketch, "E347.0.34.13", {"start": v(-82.6, 2435.9) * mm, "end": v(-82.6, 2437.7) * mm});
            skLineSegment(sketch, "E347.0.34.14", {"start": v(-140.6, 2412.7) * mm, "end": v(-140.6, 2414.5) * mm});
            skArc(sketch, "E347.0.34.15", {"start": v(-90.54, 2437.9) * mm, "mid": v(-90.68, 2437.85) * mm, "end": v(-90.74, 2437.7) * mm});
            skLineSegment(sketch, "E347.0.34.16", {"start": v(-140.6, 2435.9) * mm, "end": v(-140.6, 2437.7) * mm});
            skArc(sketch, "E347.0.34.17", {"start": v(-140.6, 2437.7) * mm, "mid": v(-140.66, 2437.85) * mm, "end": v(-140.8, 2437.9) * mm});
            skLineSegment(sketch, "E347.0.34.18", {"start": v(-140.8, 2437.9) * mm, "end": v(-148.54, 2437.9) * mm});
            skArc(sketch, "E347.0.34.19", {"start": v(-90.74, 2412.7) * mm, "mid": v(-90.68, 2412.57) * mm, "end": v(-90.54, 2412.5) * mm});
            skLineSegment(sketch, "E347.0.34.20", {"start": v(-90.74, 2414.5) * mm, "end": v(-90.74, 2412.7) * mm});
            skLineSegment(sketch, "E347.0.34.21", {"start": v(-82.6, 2412.7) * mm, "end": v(-82.6, 2414.5) * mm});
            skArc(sketch, "E347.0.34.22", {"start": v(-148.54, 2437.9) * mm, "mid": v(-148.68, 2437.85) * mm, "end": v(-148.74, 2437.7) * mm});
            skLineSegment(sketch, "E347.0.34.23", {"start": v(-148.74, 2437.7) * mm, "end": v(-148.74, 2435.9) * mm});
            skArc(sketch, "E347.0.34.24", {"start": v(-148.74, 2412.7) * mm, "mid": v(-148.68, 2412.57) * mm, "end": v(-148.54, 2412.5) * mm});
            skLineSegment(sketch, "E347.0.34.25", {"start": v(-148.74, 2414.5) * mm, "end": v(-148.74, 2412.7) * mm});
            skLineSegment(sketch, "E347.0.34.26", {"start": v(-90.54, 2412.5) * mm, "end": v(-82.8, 2412.5) * mm});
            skArc(sketch, "E347.0.34.27", {"start": v(-82.8, 2412.5) * mm, "mid": v(-82.66, 2412.57) * mm, "end": v(-82.6, 2412.7) * mm});
            skLineSegment(sketch, "E347.0.35.0", {"start": v(-92.06, 2501.4) * mm, "end": v(-90.74, 2490.7) * mm});
            skLineSegment(sketch, "E347.0.35.1", {"start": v(-139.29, 2501.4) * mm, "end": v(-140.6, 2512.1) * mm});
            skLineSegment(sketch, "E347.0.35.2", {"start": v(-81.29, 2501.4) * mm, "end": v(-82.6, 2512.1) * mm});
            skLineSegment(sketch, "E347.0.35.3", {"start": v(-82.6, 2490.7) * mm, "end": v(-81.29, 2501.4) * mm});
            skLineSegment(sketch, "E347.0.35.4", {"start": v(-140.6, 2490.7) * mm, "end": v(-139.29, 2501.4) * mm});
            skLineSegment(sketch, "E347.0.35.5", {"start": v(-150.06, 2501.4) * mm, "end": v(-148.74, 2490.7) * mm});
            skLineSegment(sketch, "E347.0.35.6", {"start": v(-90.74, 2512.1) * mm, "end": v(-92.06, 2501.4) * mm});
            skLineSegment(sketch, "E347.0.35.7", {"start": v(-148.74, 2512.1) * mm, "end": v(-150.06, 2501.4) * mm});
            skLineSegment(sketch, "E347.0.35.8", {"start": v(-90.74, 2513.9) * mm, "end": v(-90.74, 2512.1) * mm});
            skLineSegment(sketch, "E347.0.35.9", {"start": v(-148.54, 2488.7) * mm, "end": v(-140.8, 2488.7) * mm});
            skArc(sketch, "E347.0.35.10", {"start": v(-82.6, 2513.9) * mm, "mid": v(-82.66, 2514.05) * mm, "end": v(-82.8, 2514.1) * mm});
            skLineSegment(sketch, "E347.0.35.11", {"start": v(-82.8, 2514.1) * mm, "end": v(-90.54, 2514.1) * mm});
            skArc(sketch, "E347.0.35.12", {"start": v(-140.8, 2488.7) * mm, "mid": v(-140.66, 2488.77) * mm, "end": v(-140.6, 2488.9) * mm});
            skLineSegment(sketch, "E347.0.35.13", {"start": v(-82.6, 2512.1) * mm, "end": v(-82.6, 2513.9) * mm});
            skLineSegment(sketch, "E347.0.35.14", {"start": v(-140.6, 2488.9) * mm, "end": v(-140.6, 2490.7) * mm});
            skArc(sketch, "E347.0.35.15", {"start": v(-90.54, 2514.1) * mm, "mid": v(-90.68, 2514.05) * mm, "end": v(-90.74, 2513.9) * mm});
            skLineSegment(sketch, "E347.0.35.16", {"start": v(-140.6, 2512.1) * mm, "end": v(-140.6, 2513.9) * mm});
            skArc(sketch, "E347.0.35.17", {"start": v(-140.6, 2513.9) * mm, "mid": v(-140.66, 2514.05) * mm, "end": v(-140.8, 2514.1) * mm});
            skLineSegment(sketch, "E347.0.35.18", {"start": v(-140.8, 2514.1) * mm, "end": v(-148.54, 2514.1) * mm});
            skArc(sketch, "E347.0.35.19", {"start": v(-90.74, 2488.9) * mm, "mid": v(-90.68, 2488.77) * mm, "end": v(-90.54, 2488.7) * mm});
            skLineSegment(sketch, "E347.0.35.20", {"start": v(-90.74, 2490.7) * mm, "end": v(-90.74, 2488.9) * mm});
            skLineSegment(sketch, "E347.0.35.21", {"start": v(-82.6, 2488.9) * mm, "end": v(-82.6, 2490.7) * mm});
            skArc(sketch, "E347.0.35.22", {"start": v(-148.54, 2514.1) * mm, "mid": v(-148.68, 2514.05) * mm, "end": v(-148.74, 2513.9) * mm});
            skLineSegment(sketch, "E347.0.35.23", {"start": v(-148.74, 2513.9) * mm, "end": v(-148.74, 2512.1) * mm});
            skArc(sketch, "E347.0.35.24", {"start": v(-148.74, 2488.9) * mm, "mid": v(-148.68, 2488.77) * mm, "end": v(-148.54, 2488.7) * mm});
            skLineSegment(sketch, "E347.0.35.25", {"start": v(-148.74, 2490.7) * mm, "end": v(-148.74, 2488.9) * mm});
            skLineSegment(sketch, "E347.0.35.26", {"start": v(-90.54, 2488.7) * mm, "end": v(-82.8, 2488.7) * mm});
            skArc(sketch, "E347.0.35.27", {"start": v(-82.8, 2488.7) * mm, "mid": v(-82.66, 2488.77) * mm, "end": v(-82.6, 2488.9) * mm});
            skLineSegment(sketch, "E347.0.36.0", {"start": v(-92.06, 2577.6) * mm, "end": v(-90.74, 2566.9) * mm});
            skLineSegment(sketch, "E347.0.36.1", {"start": v(-139.29, 2577.6) * mm, "end": v(-140.6, 2588.3) * mm});
            skLineSegment(sketch, "E347.0.36.2", {"start": v(-81.29, 2577.6) * mm, "end": v(-82.6, 2588.3) * mm});
            skLineSegment(sketch, "E347.0.36.3", {"start": v(-82.6, 2566.9) * mm, "end": v(-81.29, 2577.6) * mm});
            skLineSegment(sketch, "E347.0.36.4", {"start": v(-140.6, 2566.9) * mm, "end": v(-139.29, 2577.6) * mm});
            skLineSegment(sketch, "E347.0.36.5", {"start": v(-150.06, 2577.6) * mm, "end": v(-148.74, 2566.9) * mm});
            skLineSegment(sketch, "E347.0.36.6", {"start": v(-90.74, 2588.3) * mm, "end": v(-92.06, 2577.6) * mm});
            skLineSegment(sketch, "E347.0.36.7", {"start": v(-148.74, 2588.3) * mm, "end": v(-150.06, 2577.6) * mm});
            skLineSegment(sketch, "E347.0.36.8", {"start": v(-90.74, 2590.1) * mm, "end": v(-90.74, 2588.3) * mm});
            skLineSegment(sketch, "E347.0.36.9", {"start": v(-148.54, 2564.9) * mm, "end": v(-140.8, 2564.9) * mm});
            skArc(sketch, "E347.0.36.10", {"start": v(-82.6, 2590.1) * mm, "mid": v(-82.66, 2590.25) * mm, "end": v(-82.8, 2590.3) * mm});
            skLineSegment(sketch, "E347.0.36.11", {"start": v(-82.8, 2590.3) * mm, "end": v(-90.54, 2590.3) * mm});
            skArc(sketch, "E347.0.36.12", {"start": v(-140.8, 2564.9) * mm, "mid": v(-140.66, 2564.97) * mm, "end": v(-140.6, 2565.1) * mm});
            skLineSegment(sketch, "E347.0.36.13", {"start": v(-82.6, 2588.3) * mm, "end": v(-82.6, 2590.1) * mm});
            skLineSegment(sketch, "E347.0.36.14", {"start": v(-140.6, 2565.1) * mm, "end": v(-140.6, 2566.9) * mm});
            skArc(sketch, "E347.0.36.15", {"start": v(-90.54, 2590.3) * mm, "mid": v(-90.68, 2590.25) * mm, "end": v(-90.74, 2590.1) * mm});
            skLineSegment(sketch, "E347.0.36.16", {"start": v(-140.6, 2588.3) * mm, "end": v(-140.6, 2590.1) * mm});
            skArc(sketch, "E347.0.36.17", {"start": v(-140.6, 2590.1) * mm, "mid": v(-140.66, 2590.25) * mm, "end": v(-140.8, 2590.3) * mm});
            skLineSegment(sketch, "E347.0.36.18", {"start": v(-140.8, 2590.3) * mm, "end": v(-148.54, 2590.3) * mm});
            skArc(sketch, "E347.0.36.19", {"start": v(-90.74, 2565.1) * mm, "mid": v(-90.68, 2564.97) * mm, "end": v(-90.54, 2564.9) * mm});
            skLineSegment(sketch, "E347.0.36.20", {"start": v(-90.74, 2566.9) * mm, "end": v(-90.74, 2565.1) * mm});
            skLineSegment(sketch, "E347.0.36.21", {"start": v(-82.6, 2565.1) * mm, "end": v(-82.6, 2566.9) * mm});
            skArc(sketch, "E347.0.36.22", {"start": v(-148.54, 2590.3) * mm, "mid": v(-148.68, 2590.25) * mm, "end": v(-148.74, 2590.1) * mm});
            skLineSegment(sketch, "E347.0.36.23", {"start": v(-148.74, 2590.1) * mm, "end": v(-148.74, 2588.3) * mm});
            skArc(sketch, "E347.0.36.24", {"start": v(-148.74, 2565.1) * mm, "mid": v(-148.68, 2564.97) * mm, "end": v(-148.54, 2564.9) * mm});
            skLineSegment(sketch, "E347.0.36.25", {"start": v(-148.74, 2566.9) * mm, "end": v(-148.74, 2565.1) * mm});
            skLineSegment(sketch, "E347.0.36.26", {"start": v(-90.54, 2564.9) * mm, "end": v(-82.8, 2564.9) * mm});
            skArc(sketch, "E347.0.36.27", {"start": v(-82.8, 2564.9) * mm, "mid": v(-82.66, 2564.97) * mm, "end": v(-82.6, 2565.1) * mm});
            skLineSegment(sketch, "E347.0.37.0", {"start": v(-92.06, 2653.8) * mm, "end": v(-90.74, 2643.1) * mm});
            skLineSegment(sketch, "E347.0.37.1", {"start": v(-139.29, 2653.8) * mm, "end": v(-140.6, 2664.5) * mm});
            skLineSegment(sketch, "E347.0.37.2", {"start": v(-81.29, 2653.8) * mm, "end": v(-82.6, 2664.5) * mm});
            skLineSegment(sketch, "E347.0.37.3", {"start": v(-82.6, 2643.1) * mm, "end": v(-81.29, 2653.8) * mm});
            skLineSegment(sketch, "E347.0.37.4", {"start": v(-140.6, 2643.1) * mm, "end": v(-139.29, 2653.8) * mm});
            skLineSegment(sketch, "E347.0.37.5", {"start": v(-150.06, 2653.8) * mm, "end": v(-148.74, 2643.1) * mm});
            skLineSegment(sketch, "E347.0.37.6", {"start": v(-90.74, 2664.5) * mm, "end": v(-92.06, 2653.8) * mm});
            skLineSegment(sketch, "E347.0.37.7", {"start": v(-148.74, 2664.5) * mm, "end": v(-150.06, 2653.8) * mm});
            skLineSegment(sketch, "E347.0.37.8", {"start": v(-90.74, 2666.3) * mm, "end": v(-90.74, 2664.5) * mm});
            skLineSegment(sketch, "E347.0.37.9", {"start": v(-148.54, 2641.1) * mm, "end": v(-140.8, 2641.1) * mm});
            skArc(sketch, "E347.0.37.10", {"start": v(-82.6, 2666.3) * mm, "mid": v(-82.66, 2666.45) * mm, "end": v(-82.8, 2666.5) * mm});
            skLineSegment(sketch, "E347.0.37.11", {"start": v(-82.8, 2666.5) * mm, "end": v(-90.54, 2666.5) * mm});
            skArc(sketch, "E347.0.37.12", {"start": v(-140.8, 2641.1) * mm, "mid": v(-140.66, 2641.17) * mm, "end": v(-140.6, 2641.3) * mm});
            skLineSegment(sketch, "E347.0.37.13", {"start": v(-82.6, 2664.5) * mm, "end": v(-82.6, 2666.3) * mm});
            skLineSegment(sketch, "E347.0.37.14", {"start": v(-140.6, 2641.3) * mm, "end": v(-140.6, 2643.1) * mm});
            skArc(sketch, "E347.0.37.15", {"start": v(-90.54, 2666.5) * mm, "mid": v(-90.68, 2666.45) * mm, "end": v(-90.74, 2666.3) * mm});
            skLineSegment(sketch, "E347.0.37.16", {"start": v(-140.6, 2664.5) * mm, "end": v(-140.6, 2666.3) * mm});
            skArc(sketch, "E347.0.37.17", {"start": v(-140.6, 2666.3) * mm, "mid": v(-140.66, 2666.45) * mm, "end": v(-140.8, 2666.5) * mm});
            skLineSegment(sketch, "E347.0.37.18", {"start": v(-140.8, 2666.5) * mm, "end": v(-148.54, 2666.5) * mm});
            skArc(sketch, "E347.0.37.19", {"start": v(-90.74, 2641.3) * mm, "mid": v(-90.68, 2641.17) * mm, "end": v(-90.54, 2641.1) * mm});
            skLineSegment(sketch, "E347.0.37.20", {"start": v(-90.74, 2643.1) * mm, "end": v(-90.74, 2641.3) * mm});
            skLineSegment(sketch, "E347.0.37.21", {"start": v(-82.6, 2641.3) * mm, "end": v(-82.6, 2643.1) * mm});
            skArc(sketch, "E347.0.37.22", {"start": v(-148.54, 2666.5) * mm, "mid": v(-148.68, 2666.45) * mm, "end": v(-148.74, 2666.3) * mm});
            skLineSegment(sketch, "E347.0.37.23", {"start": v(-148.74, 2666.3) * mm, "end": v(-148.74, 2664.5) * mm});
            skArc(sketch, "E347.0.37.24", {"start": v(-148.74, 2641.3) * mm, "mid": v(-148.68, 2641.17) * mm, "end": v(-148.54, 2641.1) * mm});
            skLineSegment(sketch, "E347.0.37.25", {"start": v(-148.74, 2643.1) * mm, "end": v(-148.74, 2641.3) * mm});
            skLineSegment(sketch, "E347.0.37.26", {"start": v(-90.54, 2641.1) * mm, "end": v(-82.8, 2641.1) * mm});
            skArc(sketch, "E347.0.37.27", {"start": v(-82.8, 2641.1) * mm, "mid": v(-82.66, 2641.17) * mm, "end": v(-82.6, 2641.3) * mm});
            skLineSegment(sketch, "E347.0.38.0", {"start": v(-92.06, 2730) * mm, "end": v(-90.74, 2719.3) * mm});
            skLineSegment(sketch, "E347.0.38.1", {"start": v(-139.29, 2730) * mm, "end": v(-140.6, 2740.7) * mm});
            skLineSegment(sketch, "E347.0.38.2", {"start": v(-81.29, 2730) * mm, "end": v(-82.6, 2740.7) * mm});
            skLineSegment(sketch, "E347.0.38.3", {"start": v(-82.6, 2719.3) * mm, "end": v(-81.29, 2730) * mm});
            skLineSegment(sketch, "E347.0.38.4", {"start": v(-140.6, 2719.3) * mm, "end": v(-139.29, 2730) * mm});
            skLineSegment(sketch, "E347.0.38.5", {"start": v(-150.06, 2730) * mm, "end": v(-148.74, 2719.3) * mm});
            skLineSegment(sketch, "E347.0.38.6", {"start": v(-90.74, 2740.7) * mm, "end": v(-92.06, 2730) * mm});
            skLineSegment(sketch, "E347.0.38.7", {"start": v(-148.74, 2740.7) * mm, "end": v(-150.06, 2730) * mm});
            skLineSegment(sketch, "E347.0.38.8", {"start": v(-90.74, 2742.5) * mm, "end": v(-90.74, 2740.7) * mm});
            skLineSegment(sketch, "E347.0.38.9", {"start": v(-148.54, 2717.3) * mm, "end": v(-140.8, 2717.3) * mm});
            skArc(sketch, "E347.0.38.10", {"start": v(-82.6, 2742.5) * mm, "mid": v(-82.66, 2742.65) * mm, "end": v(-82.8, 2742.7) * mm});
            skLineSegment(sketch, "E347.0.38.11", {"start": v(-82.8, 2742.7) * mm, "end": v(-90.54, 2742.7) * mm});
            skArc(sketch, "E347.0.38.12", {"start": v(-140.8, 2717.3) * mm, "mid": v(-140.66, 2717.37) * mm, "end": v(-140.6, 2717.5) * mm});
            skLineSegment(sketch, "E347.0.38.13", {"start": v(-82.6, 2740.7) * mm, "end": v(-82.6, 2742.5) * mm});
            skLineSegment(sketch, "E347.0.38.14", {"start": v(-140.6, 2717.5) * mm, "end": v(-140.6, 2719.3) * mm});
            skArc(sketch, "E347.0.38.15", {"start": v(-90.54, 2742.7) * mm, "mid": v(-90.68, 2742.65) * mm, "end": v(-90.74, 2742.5) * mm});
            skLineSegment(sketch, "E347.0.38.16", {"start": v(-140.6, 2740.7) * mm, "end": v(-140.6, 2742.5) * mm});
            skArc(sketch, "E347.0.38.17", {"start": v(-140.6, 2742.5) * mm, "mid": v(-140.66, 2742.65) * mm, "end": v(-140.8, 2742.7) * mm});
            skLineSegment(sketch, "E347.0.38.18", {"start": v(-140.8, 2742.7) * mm, "end": v(-148.54, 2742.7) * mm});
            skArc(sketch, "E347.0.38.19", {"start": v(-90.74, 2717.5) * mm, "mid": v(-90.68, 2717.37) * mm, "end": v(-90.54, 2717.3) * mm});
            skLineSegment(sketch, "E347.0.38.20", {"start": v(-90.74, 2719.3) * mm, "end": v(-90.74, 2717.5) * mm});
            skLineSegment(sketch, "E347.0.38.21", {"start": v(-82.6, 2717.5) * mm, "end": v(-82.6, 2719.3) * mm});
            skArc(sketch, "E347.0.38.22", {"start": v(-148.54, 2742.7) * mm, "mid": v(-148.68, 2742.65) * mm, "end": v(-148.74, 2742.5) * mm});
            skLineSegment(sketch, "E347.0.38.23", {"start": v(-148.74, 2742.5) * mm, "end": v(-148.74, 2740.7) * mm});
            skArc(sketch, "E347.0.38.24", {"start": v(-148.74, 2717.5) * mm, "mid": v(-148.68, 2717.37) * mm, "end": v(-148.54, 2717.3) * mm});
            skLineSegment(sketch, "E347.0.38.25", {"start": v(-148.74, 2719.3) * mm, "end": v(-148.74, 2717.5) * mm});
            skLineSegment(sketch, "E347.0.38.26", {"start": v(-90.54, 2717.3) * mm, "end": v(-82.8, 2717.3) * mm});
            skArc(sketch, "E347.0.38.27", {"start": v(-82.8, 2717.3) * mm, "mid": v(-82.66, 2717.37) * mm, "end": v(-82.6, 2717.5) * mm});
            skLineSegment(sketch, "E347.0.39.0", {"start": v(-92.06, 2806.2) * mm, "end": v(-90.74, 2795.5) * mm});
            skLineSegment(sketch, "E347.0.39.1", {"start": v(-139.29, 2806.2) * mm, "end": v(-140.6, 2816.9) * mm});
            skLineSegment(sketch, "E347.0.39.2", {"start": v(-81.29, 2806.2) * mm, "end": v(-82.6, 2816.9) * mm});
            skLineSegment(sketch, "E347.0.39.3", {"start": v(-82.6, 2795.5) * mm, "end": v(-81.29, 2806.2) * mm});
            skLineSegment(sketch, "E347.0.39.4", {"start": v(-140.6, 2795.5) * mm, "end": v(-139.29, 2806.2) * mm});
            skLineSegment(sketch, "E347.0.39.5", {"start": v(-150.06, 2806.2) * mm, "end": v(-148.74, 2795.5) * mm});
            skLineSegment(sketch, "E347.0.39.6", {"start": v(-90.74, 2816.9) * mm, "end": v(-92.06, 2806.2) * mm});
            skLineSegment(sketch, "E347.0.39.7", {"start": v(-148.74, 2816.9) * mm, "end": v(-150.06, 2806.2) * mm});
            skLineSegment(sketch, "E347.0.39.8", {"start": v(-90.74, 2818.7) * mm, "end": v(-90.74, 2816.9) * mm});
            skLineSegment(sketch, "E347.0.39.9", {"start": v(-148.54, 2793.5) * mm, "end": v(-140.8, 2793.5) * mm});
            skArc(sketch, "E347.0.39.10", {"start": v(-82.6, 2818.7) * mm, "mid": v(-82.66, 2818.85) * mm, "end": v(-82.8, 2818.9) * mm});
            skLineSegment(sketch, "E347.0.39.11", {"start": v(-82.8, 2818.9) * mm, "end": v(-90.54, 2818.9) * mm});
            skArc(sketch, "E347.0.39.12", {"start": v(-140.8, 2793.5) * mm, "mid": v(-140.66, 2793.57) * mm, "end": v(-140.6, 2793.7) * mm});
            skLineSegment(sketch, "E347.0.39.13", {"start": v(-82.6, 2816.9) * mm, "end": v(-82.6, 2818.7) * mm});
            skLineSegment(sketch, "E347.0.39.14", {"start": v(-140.6, 2793.7) * mm, "end": v(-140.6, 2795.5) * mm});
            skArc(sketch, "E347.0.39.15", {"start": v(-90.54, 2818.9) * mm, "mid": v(-90.68, 2818.85) * mm, "end": v(-90.74, 2818.7) * mm});
            skLineSegment(sketch, "E347.0.39.16", {"start": v(-140.6, 2816.9) * mm, "end": v(-140.6, 2818.7) * mm});
            skArc(sketch, "E347.0.39.17", {"start": v(-140.6, 2818.7) * mm, "mid": v(-140.66, 2818.85) * mm, "end": v(-140.8, 2818.9) * mm});
            skLineSegment(sketch, "E347.0.39.18", {"start": v(-140.8, 2818.9) * mm, "end": v(-148.54, 2818.9) * mm});
            skArc(sketch, "E347.0.39.19", {"start": v(-90.74, 2793.7) * mm, "mid": v(-90.68, 2793.57) * mm, "end": v(-90.54, 2793.5) * mm});
            skLineSegment(sketch, "E347.0.39.20", {"start": v(-90.74, 2795.5) * mm, "end": v(-90.74, 2793.7) * mm});
            skLineSegment(sketch, "E347.0.39.21", {"start": v(-82.6, 2793.7) * mm, "end": v(-82.6, 2795.5) * mm});
            skArc(sketch, "E347.0.39.22", {"start": v(-148.54, 2818.9) * mm, "mid": v(-148.68, 2818.85) * mm, "end": v(-148.74, 2818.7) * mm});
            skLineSegment(sketch, "E347.0.39.23", {"start": v(-148.74, 2818.7) * mm, "end": v(-148.74, 2816.9) * mm});
            skArc(sketch, "E347.0.39.24", {"start": v(-148.74, 2793.7) * mm, "mid": v(-148.68, 2793.57) * mm, "end": v(-148.54, 2793.5) * mm});
            skLineSegment(sketch, "E347.0.39.25", {"start": v(-148.74, 2795.5) * mm, "end": v(-148.74, 2793.7) * mm});
            skLineSegment(sketch, "E347.0.39.26", {"start": v(-90.54, 2793.5) * mm, "end": v(-82.8, 2793.5) * mm});
            skArc(sketch, "E347.0.39.27", {"start": v(-82.8, 2793.5) * mm, "mid": v(-82.66, 2793.57) * mm, "end": v(-82.6, 2793.7) * mm});
            skLineSegment(sketch, "E347.0.40.0", {"start": v(-92.06, 2882.4) * mm, "end": v(-90.74, 2871.7) * mm});
            skLineSegment(sketch, "E347.0.40.1", {"start": v(-139.29, 2882.4) * mm, "end": v(-140.6, 2893.1) * mm});
            skLineSegment(sketch, "E347.0.40.2", {"start": v(-81.29, 2882.4) * mm, "end": v(-82.6, 2893.1) * mm});
            skLineSegment(sketch, "E347.0.40.3", {"start": v(-82.6, 2871.7) * mm, "end": v(-81.29, 2882.4) * mm});
            skLineSegment(sketch, "E347.0.40.4", {"start": v(-140.6, 2871.7) * mm, "end": v(-139.29, 2882.4) * mm});
            skLineSegment(sketch, "E347.0.40.5", {"start": v(-150.06, 2882.4) * mm, "end": v(-148.74, 2871.7) * mm});
            skLineSegment(sketch, "E347.0.40.6", {"start": v(-90.74, 2893.1) * mm, "end": v(-92.06, 2882.4) * mm});
            skLineSegment(sketch, "E347.0.40.7", {"start": v(-148.74, 2893.1) * mm, "end": v(-150.06, 2882.4) * mm});
            skLineSegment(sketch, "E347.0.40.8", {"start": v(-90.74, 2894.9) * mm, "end": v(-90.74, 2893.1) * mm});
            skLineSegment(sketch, "E347.0.40.9", {"start": v(-148.54, 2869.7) * mm, "end": v(-140.8, 2869.7) * mm});
            skArc(sketch, "E347.0.40.10", {"start": v(-82.6, 2894.9) * mm, "mid": v(-82.66, 2895.05) * mm, "end": v(-82.8, 2895.1) * mm});
            skLineSegment(sketch, "E347.0.40.11", {"start": v(-82.8, 2895.1) * mm, "end": v(-90.54, 2895.1) * mm});
            skArc(sketch, "E347.0.40.12", {"start": v(-140.8, 2869.7) * mm, "mid": v(-140.66, 2869.77) * mm, "end": v(-140.6, 2869.9) * mm});
            skLineSegment(sketch, "E347.0.40.13", {"start": v(-82.6, 2893.1) * mm, "end": v(-82.6, 2894.9) * mm});
            skLineSegment(sketch, "E347.0.40.14", {"start": v(-140.6, 2869.9) * mm, "end": v(-140.6, 2871.7) * mm});
            skArc(sketch, "E347.0.40.15", {"start": v(-90.54, 2895.1) * mm, "mid": v(-90.68, 2895.05) * mm, "end": v(-90.74, 2894.9) * mm});
            skLineSegment(sketch, "E347.0.40.16", {"start": v(-140.6, 2893.1) * mm, "end": v(-140.6, 2894.9) * mm});
            skArc(sketch, "E347.0.40.17", {"start": v(-140.6, 2894.9) * mm, "mid": v(-140.66, 2895.05) * mm, "end": v(-140.8, 2895.1) * mm});
            skLineSegment(sketch, "E347.0.40.18", {"start": v(-140.8, 2895.1) * mm, "end": v(-148.54, 2895.1) * mm});
            skArc(sketch, "E347.0.40.19", {"start": v(-90.74, 2869.9) * mm, "mid": v(-90.68, 2869.77) * mm, "end": v(-90.54, 2869.7) * mm});
            skLineSegment(sketch, "E347.0.40.20", {"start": v(-90.74, 2871.7) * mm, "end": v(-90.74, 2869.9) * mm});
            skLineSegment(sketch, "E347.0.40.21", {"start": v(-82.6, 2869.9) * mm, "end": v(-82.6, 2871.7) * mm});
            skArc(sketch, "E347.0.40.22", {"start": v(-148.54, 2895.1) * mm, "mid": v(-148.68, 2895.05) * mm, "end": v(-148.74, 2894.9) * mm});
            skLineSegment(sketch, "E347.0.40.23", {"start": v(-148.74, 2894.9) * mm, "end": v(-148.74, 2893.1) * mm});
            skArc(sketch, "E347.0.40.24", {"start": v(-148.74, 2869.9) * mm, "mid": v(-148.68, 2869.77) * mm, "end": v(-148.54, 2869.7) * mm});
            skLineSegment(sketch, "E347.0.40.25", {"start": v(-148.74, 2871.7) * mm, "end": v(-148.74, 2869.9) * mm});
            skLineSegment(sketch, "E347.0.40.26", {"start": v(-90.54, 2869.7) * mm, "end": v(-82.8, 2869.7) * mm});
            skArc(sketch, "E347.0.40.27", {"start": v(-82.8, 2869.7) * mm, "mid": v(-82.66, 2869.77) * mm, "end": v(-82.6, 2869.9) * mm});
            skLineSegment(sketch, "E347.0.41.0", {"start": v(-92.06, 2958.6) * mm, "end": v(-90.74, 2947.9) * mm});
            skLineSegment(sketch, "E347.0.41.1", {"start": v(-139.29, 2958.6) * mm, "end": v(-140.6, 2969.3) * mm});
            skLineSegment(sketch, "E347.0.41.2", {"start": v(-81.29, 2958.6) * mm, "end": v(-82.6, 2969.3) * mm});
            skLineSegment(sketch, "E347.0.41.3", {"start": v(-82.6, 2947.9) * mm, "end": v(-81.29, 2958.6) * mm});
            skLineSegment(sketch, "E347.0.41.4", {"start": v(-140.6, 2947.9) * mm, "end": v(-139.29, 2958.6) * mm});
            skLineSegment(sketch, "E347.0.41.5", {"start": v(-150.06, 2958.6) * mm, "end": v(-148.74, 2947.9) * mm});
            skLineSegment(sketch, "E347.0.41.6", {"start": v(-90.74, 2969.3) * mm, "end": v(-92.06, 2958.6) * mm});
            skLineSegment(sketch, "E347.0.41.7", {"start": v(-148.74, 2969.3) * mm, "end": v(-150.06, 2958.6) * mm});
            skLineSegment(sketch, "E347.0.41.8", {"start": v(-90.74, 2971.1) * mm, "end": v(-90.74, 2969.3) * mm});
            skLineSegment(sketch, "E347.0.41.9", {"start": v(-148.54, 2945.9) * mm, "end": v(-140.8, 2945.9) * mm});
            skArc(sketch, "E347.0.41.10", {"start": v(-82.6, 2971.1) * mm, "mid": v(-82.66, 2971.25) * mm, "end": v(-82.8, 2971.3) * mm});
            skLineSegment(sketch, "E347.0.41.11", {"start": v(-82.8, 2971.3) * mm, "end": v(-90.54, 2971.3) * mm});
            skArc(sketch, "E347.0.41.12", {"start": v(-140.8, 2945.9) * mm, "mid": v(-140.66, 2945.97) * mm, "end": v(-140.6, 2946.1) * mm});
            skLineSegment(sketch, "E347.0.41.13", {"start": v(-82.6, 2969.3) * mm, "end": v(-82.6, 2971.1) * mm});
            skLineSegment(sketch, "E347.0.41.14", {"start": v(-140.6, 2946.1) * mm, "end": v(-140.6, 2947.9) * mm});
            skArc(sketch, "E347.0.41.15", {"start": v(-90.54, 2971.3) * mm, "mid": v(-90.68, 2971.25) * mm, "end": v(-90.74, 2971.1) * mm});
            skLineSegment(sketch, "E347.0.41.16", {"start": v(-140.6, 2969.3) * mm, "end": v(-140.6, 2971.1) * mm});
            skArc(sketch, "E347.0.41.17", {"start": v(-140.6, 2971.1) * mm, "mid": v(-140.66, 2971.25) * mm, "end": v(-140.8, 2971.3) * mm});
            skLineSegment(sketch, "E347.0.41.18", {"start": v(-140.8, 2971.3) * mm, "end": v(-148.54, 2971.3) * mm});
            skArc(sketch, "E347.0.41.19", {"start": v(-90.74, 2946.1) * mm, "mid": v(-90.68, 2945.97) * mm, "end": v(-90.54, 2945.9) * mm});
            skLineSegment(sketch, "E347.0.41.20", {"start": v(-90.74, 2947.9) * mm, "end": v(-90.74, 2946.1) * mm});
            skLineSegment(sketch, "E347.0.41.21", {"start": v(-82.6, 2946.1) * mm, "end": v(-82.6, 2947.9) * mm});
            skArc(sketch, "E347.0.41.22", {"start": v(-148.54, 2971.3) * mm, "mid": v(-148.68, 2971.25) * mm, "end": v(-148.74, 2971.1) * mm});
            skLineSegment(sketch, "E347.0.41.23", {"start": v(-148.74, 2971.1) * mm, "end": v(-148.74, 2969.3) * mm});
            skArc(sketch, "E347.0.41.24", {"start": v(-148.74, 2946.1) * mm, "mid": v(-148.68, 2945.97) * mm, "end": v(-148.54, 2945.9) * mm});
            skLineSegment(sketch, "E347.0.41.25", {"start": v(-148.74, 2947.9) * mm, "end": v(-148.74, 2946.1) * mm});
            skLineSegment(sketch, "E347.0.41.26", {"start": v(-90.54, 2945.9) * mm, "end": v(-82.8, 2945.9) * mm});
            skArc(sketch, "E347.0.41.27", {"start": v(-82.8, 2945.9) * mm, "mid": v(-82.66, 2945.97) * mm, "end": v(-82.6, 2946.1) * mm});
            skLineSegment(sketch, "E347.0.42.0", {"start": v(-92.06, 3034.8) * mm, "end": v(-90.74, 3024.1) * mm});
            skLineSegment(sketch, "E347.0.42.1", {"start": v(-139.29, 3034.8) * mm, "end": v(-140.6, 3045.5) * mm});
            skLineSegment(sketch, "E347.0.42.2", {"start": v(-81.29, 3034.8) * mm, "end": v(-82.6, 3045.5) * mm});
            skLineSegment(sketch, "E347.0.42.3", {"start": v(-82.6, 3024.1) * mm, "end": v(-81.29, 3034.8) * mm});
            skLineSegment(sketch, "E347.0.42.4", {"start": v(-140.6, 3024.1) * mm, "end": v(-139.29, 3034.8) * mm});
            skLineSegment(sketch, "E347.0.42.5", {"start": v(-150.06, 3034.8) * mm, "end": v(-148.74, 3024.1) * mm});
            skLineSegment(sketch, "E347.0.42.6", {"start": v(-90.74, 3045.5) * mm, "end": v(-92.06, 3034.8) * mm});
            skLineSegment(sketch, "E347.0.42.7", {"start": v(-148.74, 3045.5) * mm, "end": v(-150.06, 3034.8) * mm});
            skLineSegment(sketch, "E347.0.42.8", {"start": v(-90.74, 3047.3) * mm, "end": v(-90.74, 3045.5) * mm});
            skLineSegment(sketch, "E347.0.42.9", {"start": v(-148.54, 3022.1) * mm, "end": v(-140.8, 3022.1) * mm});
            skArc(sketch, "E347.0.42.10", {"start": v(-82.6, 3047.3) * mm, "mid": v(-82.66, 3047.45) * mm, "end": v(-82.8, 3047.5) * mm});
            skLineSegment(sketch, "E347.0.42.11", {"start": v(-82.8, 3047.5) * mm, "end": v(-90.54, 3047.5) * mm});
            skArc(sketch, "E347.0.42.12", {"start": v(-140.8, 3022.1) * mm, "mid": v(-140.66, 3022.17) * mm, "end": v(-140.6, 3022.3) * mm});
            skLineSegment(sketch, "E347.0.42.13", {"start": v(-82.6, 3045.5) * mm, "end": v(-82.6, 3047.3) * mm});
            skLineSegment(sketch, "E347.0.42.14", {"start": v(-140.6, 3022.3) * mm, "end": v(-140.6, 3024.1) * mm});
            skArc(sketch, "E347.0.42.15", {"start": v(-90.54, 3047.5) * mm, "mid": v(-90.68, 3047.45) * mm, "end": v(-90.74, 3047.3) * mm});
            skLineSegment(sketch, "E347.0.42.16", {"start": v(-140.6, 3045.5) * mm, "end": v(-140.6, 3047.3) * mm});
            skArc(sketch, "E347.0.42.17", {"start": v(-140.6, 3047.3) * mm, "mid": v(-140.66, 3047.45) * mm, "end": v(-140.8, 3047.5) * mm});
            skLineSegment(sketch, "E347.0.42.18", {"start": v(-140.8, 3047.5) * mm, "end": v(-148.54, 3047.5) * mm});
            skArc(sketch, "E347.0.42.19", {"start": v(-90.74, 3022.3) * mm, "mid": v(-90.68, 3022.17) * mm, "end": v(-90.54, 3022.1) * mm});
            skLineSegment(sketch, "E347.0.42.20", {"start": v(-90.74, 3024.1) * mm, "end": v(-90.74, 3022.3) * mm});
            skLineSegment(sketch, "E347.0.42.21", {"start": v(-82.6, 3022.3) * mm, "end": v(-82.6, 3024.1) * mm});
            skArc(sketch, "E347.0.42.22", {"start": v(-148.54, 3047.5) * mm, "mid": v(-148.68, 3047.45) * mm, "end": v(-148.74, 3047.3) * mm});
            skLineSegment(sketch, "E347.0.42.23", {"start": v(-148.74, 3047.3) * mm, "end": v(-148.74, 3045.5) * mm});
            skArc(sketch, "E347.0.42.24", {"start": v(-148.74, 3022.3) * mm, "mid": v(-148.68, 3022.17) * mm, "end": v(-148.54, 3022.1) * mm});
            skLineSegment(sketch, "E347.0.42.25", {"start": v(-148.74, 3024.1) * mm, "end": v(-148.74, 3022.3) * mm});
            skLineSegment(sketch, "E347.0.42.26", {"start": v(-90.54, 3022.1) * mm, "end": v(-82.8, 3022.1) * mm});
            skArc(sketch, "E347.0.42.27", {"start": v(-82.8, 3022.1) * mm, "mid": v(-82.66, 3022.17) * mm, "end": v(-82.6, 3022.3) * mm});
            skLineSegment(sketch, "E347.0.43.0", {"start": v(-92.06, 3111) * mm, "end": v(-90.74, 3100.3) * mm});
            skLineSegment(sketch, "E347.0.43.1", {"start": v(-139.29, 3111) * mm, "end": v(-140.6, 3121.7) * mm});
            skLineSegment(sketch, "E347.0.43.2", {"start": v(-81.29, 3111) * mm, "end": v(-82.6, 3121.7) * mm});
            skLineSegment(sketch, "E347.0.43.3", {"start": v(-82.6, 3100.3) * mm, "end": v(-81.29, 3111) * mm});
            skLineSegment(sketch, "E347.0.43.4", {"start": v(-140.6, 3100.3) * mm, "end": v(-139.29, 3111) * mm});
            skLineSegment(sketch, "E347.0.43.5", {"start": v(-150.06, 3111) * mm, "end": v(-148.74, 3100.3) * mm});
            skLineSegment(sketch, "E347.0.43.6", {"start": v(-90.74, 3121.7) * mm, "end": v(-92.06, 3111) * mm});
            skLineSegment(sketch, "E347.0.43.7", {"start": v(-148.74, 3121.7) * mm, "end": v(-150.06, 3111) * mm});
            skLineSegment(sketch, "E347.0.43.8", {"start": v(-90.74, 3123.5) * mm, "end": v(-90.74, 3121.7) * mm});
            skLineSegment(sketch, "E347.0.43.9", {"start": v(-148.54, 3098.3) * mm, "end": v(-140.8, 3098.3) * mm});
            skArc(sketch, "E347.0.43.10", {"start": v(-82.6, 3123.5) * mm, "mid": v(-82.66, 3123.65) * mm, "end": v(-82.8, 3123.7) * mm});
            skLineSegment(sketch, "E347.0.43.11", {"start": v(-82.8, 3123.7) * mm, "end": v(-90.54, 3123.7) * mm});
            skArc(sketch, "E347.0.43.12", {"start": v(-140.8, 3098.3) * mm, "mid": v(-140.66, 3098.37) * mm, "end": v(-140.6, 3098.5) * mm});
            skLineSegment(sketch, "E347.0.43.13", {"start": v(-82.6, 3121.7) * mm, "end": v(-82.6, 3123.5) * mm});
            skLineSegment(sketch, "E347.0.43.14", {"start": v(-140.6, 3098.5) * mm, "end": v(-140.6, 3100.3) * mm});
            skArc(sketch, "E347.0.43.15", {"start": v(-90.54, 3123.7) * mm, "mid": v(-90.68, 3123.65) * mm, "end": v(-90.74, 3123.5) * mm});
            skLineSegment(sketch, "E347.0.43.16", {"start": v(-140.6, 3121.7) * mm, "end": v(-140.6, 3123.5) * mm});
            skArc(sketch, "E347.0.43.17", {"start": v(-140.6, 3123.5) * mm, "mid": v(-140.66, 3123.65) * mm, "end": v(-140.8, 3123.7) * mm});
            skLineSegment(sketch, "E347.0.43.18", {"start": v(-140.8, 3123.7) * mm, "end": v(-148.54, 3123.7) * mm});
            skArc(sketch, "E347.0.43.19", {"start": v(-90.74, 3098.5) * mm, "mid": v(-90.68, 3098.37) * mm, "end": v(-90.54, 3098.3) * mm});
            skLineSegment(sketch, "E347.0.43.20", {"start": v(-90.74, 3100.3) * mm, "end": v(-90.74, 3098.5) * mm});
            skLineSegment(sketch, "E347.0.43.21", {"start": v(-82.6, 3098.5) * mm, "end": v(-82.6, 3100.3) * mm});
            skArc(sketch, "E347.0.43.22", {"start": v(-148.54, 3123.7) * mm, "mid": v(-148.68, 3123.65) * mm, "end": v(-148.74, 3123.5) * mm});
            skLineSegment(sketch, "E347.0.43.23", {"start": v(-148.74, 3123.5) * mm, "end": v(-148.74, 3121.7) * mm});
            skArc(sketch, "E347.0.43.24", {"start": v(-148.74, 3098.5) * mm, "mid": v(-148.68, 3098.37) * mm, "end": v(-148.54, 3098.3) * mm});
            skLineSegment(sketch, "E347.0.43.25", {"start": v(-148.74, 3100.3) * mm, "end": v(-148.74, 3098.5) * mm});
            skLineSegment(sketch, "E347.0.43.26", {"start": v(-90.54, 3098.3) * mm, "end": v(-82.8, 3098.3) * mm});
            skArc(sketch, "E347.0.43.27", {"start": v(-82.8, 3098.3) * mm, "mid": v(-82.66, 3098.37) * mm, "end": v(-82.6, 3098.5) * mm});
            skLineSegment(sketch, "E347.0.44.0", {"start": v(-92.06, 3187.2) * mm, "end": v(-90.74, 3176.5) * mm});
            skLineSegment(sketch, "E347.0.44.1", {"start": v(-139.29, 3187.2) * mm, "end": v(-140.6, 3197.9) * mm});
            skLineSegment(sketch, "E347.0.44.2", {"start": v(-81.29, 3187.2) * mm, "end": v(-82.6, 3197.9) * mm});
            skLineSegment(sketch, "E347.0.44.3", {"start": v(-82.6, 3176.5) * mm, "end": v(-81.29, 3187.2) * mm});
            skLineSegment(sketch, "E347.0.44.4", {"start": v(-140.6, 3176.5) * mm, "end": v(-139.29, 3187.2) * mm});
            skLineSegment(sketch, "E347.0.44.5", {"start": v(-150.06, 3187.2) * mm, "end": v(-148.74, 3176.5) * mm});
            skLineSegment(sketch, "E347.0.44.6", {"start": v(-90.74, 3197.9) * mm, "end": v(-92.06, 3187.2) * mm});
            skLineSegment(sketch, "E347.0.44.7", {"start": v(-148.74, 3197.9) * mm, "end": v(-150.06, 3187.2) * mm});
            skLineSegment(sketch, "E347.0.44.8", {"start": v(-90.74, 3199.7) * mm, "end": v(-90.74, 3197.9) * mm});
            skLineSegment(sketch, "E347.0.44.9", {"start": v(-148.54, 3174.5) * mm, "end": v(-140.8, 3174.5) * mm});
            skArc(sketch, "E347.0.44.10", {"start": v(-82.6, 3199.7) * mm, "mid": v(-82.66, 3199.85) * mm, "end": v(-82.8, 3199.9) * mm});
            skLineSegment(sketch, "E347.0.44.11", {"start": v(-82.8, 3199.9) * mm, "end": v(-90.54, 3199.9) * mm});
            skArc(sketch, "E347.0.44.12", {"start": v(-140.8, 3174.5) * mm, "mid": v(-140.66, 3174.57) * mm, "end": v(-140.6, 3174.7) * mm});
            skLineSegment(sketch, "E347.0.44.13", {"start": v(-82.6, 3197.9) * mm, "end": v(-82.6, 3199.7) * mm});
            skLineSegment(sketch, "E347.0.44.14", {"start": v(-140.6, 3174.7) * mm, "end": v(-140.6, 3176.5) * mm});
            skArc(sketch, "E347.0.44.15", {"start": v(-90.54, 3199.9) * mm, "mid": v(-90.68, 3199.85) * mm, "end": v(-90.74, 3199.7) * mm});
            skLineSegment(sketch, "E347.0.44.16", {"start": v(-140.6, 3197.9) * mm, "end": v(-140.6, 3199.7) * mm});
            skArc(sketch, "E347.0.44.17", {"start": v(-140.6, 3199.7) * mm, "mid": v(-140.66, 3199.85) * mm, "end": v(-140.8, 3199.9) * mm});
            skLineSegment(sketch, "E347.0.44.18", {"start": v(-140.8, 3199.9) * mm, "end": v(-148.54, 3199.9) * mm});
            skArc(sketch, "E347.0.44.19", {"start": v(-90.74, 3174.7) * mm, "mid": v(-90.68, 3174.57) * mm, "end": v(-90.54, 3174.5) * mm});
            skLineSegment(sketch, "E347.0.44.20", {"start": v(-90.74, 3176.5) * mm, "end": v(-90.74, 3174.7) * mm});
            skLineSegment(sketch, "E347.0.44.21", {"start": v(-82.6, 3174.7) * mm, "end": v(-82.6, 3176.5) * mm});
            skArc(sketch, "E347.0.44.22", {"start": v(-148.54, 3199.9) * mm, "mid": v(-148.68, 3199.85) * mm, "end": v(-148.74, 3199.7) * mm});
            skLineSegment(sketch, "E347.0.44.23", {"start": v(-148.74, 3199.7) * mm, "end": v(-148.74, 3197.9) * mm});
            skArc(sketch, "E347.0.44.24", {"start": v(-148.74, 3174.7) * mm, "mid": v(-148.68, 3174.57) * mm, "end": v(-148.54, 3174.5) * mm});
            skLineSegment(sketch, "E347.0.44.25", {"start": v(-148.74, 3176.5) * mm, "end": v(-148.74, 3174.7) * mm});
            skLineSegment(sketch, "E347.0.44.26", {"start": v(-90.54, 3174.5) * mm, "end": v(-82.8, 3174.5) * mm});
            skArc(sketch, "E347.0.44.27", {"start": v(-82.8, 3174.5) * mm, "mid": v(-82.66, 3174.57) * mm, "end": v(-82.6, 3174.7) * mm});
            skLineSegment(sketch, "E347.0.45.0", {"start": v(-92.06, 3263.4) * mm, "end": v(-90.74, 3252.7) * mm});
            skLineSegment(sketch, "E347.0.45.1", {"start": v(-139.29, 3263.4) * mm, "end": v(-140.6, 3274.1) * mm});
            skLineSegment(sketch, "E347.0.45.2", {"start": v(-81.29, 3263.4) * mm, "end": v(-82.6, 3274.1) * mm});
            skLineSegment(sketch, "E347.0.45.3", {"start": v(-82.6, 3252.7) * mm, "end": v(-81.29, 3263.4) * mm});
            skLineSegment(sketch, "E347.0.45.4", {"start": v(-140.6, 3252.7) * mm, "end": v(-139.29, 3263.4) * mm});
            skLineSegment(sketch, "E347.0.45.5", {"start": v(-150.06, 3263.4) * mm, "end": v(-148.74, 3252.7) * mm});
            skLineSegment(sketch, "E347.0.45.6", {"start": v(-90.74, 3274.1) * mm, "end": v(-92.06, 3263.4) * mm});
            skLineSegment(sketch, "E347.0.45.7", {"start": v(-148.74, 3274.1) * mm, "end": v(-150.06, 3263.4) * mm});
            skLineSegment(sketch, "E347.0.45.8", {"start": v(-90.74, 3275.9) * mm, "end": v(-90.74, 3274.1) * mm});
            skLineSegment(sketch, "E347.0.45.9", {"start": v(-148.54, 3250.7) * mm, "end": v(-140.8, 3250.7) * mm});
            skArc(sketch, "E347.0.45.10", {"start": v(-82.6, 3275.9) * mm, "mid": v(-82.66, 3276.05) * mm, "end": v(-82.8, 3276.1) * mm});
            skLineSegment(sketch, "E347.0.45.11", {"start": v(-82.8, 3276.1) * mm, "end": v(-90.54, 3276.1) * mm});
            skArc(sketch, "E347.0.45.12", {"start": v(-140.8, 3250.7) * mm, "mid": v(-140.66, 3250.77) * mm, "end": v(-140.6, 3250.9) * mm});
            skLineSegment(sketch, "E347.0.45.13", {"start": v(-82.6, 3274.1) * mm, "end": v(-82.6, 3275.9) * mm});
            skLineSegment(sketch, "E347.0.45.14", {"start": v(-140.6, 3250.9) * mm, "end": v(-140.6, 3252.7) * mm});
            skArc(sketch, "E347.0.45.15", {"start": v(-90.54, 3276.1) * mm, "mid": v(-90.68, 3276.05) * mm, "end": v(-90.74, 3275.9) * mm});
            skLineSegment(sketch, "E347.0.45.16", {"start": v(-140.6, 3274.1) * mm, "end": v(-140.6, 3275.9) * mm});
            skArc(sketch, "E347.0.45.17", {"start": v(-140.6, 3275.9) * mm, "mid": v(-140.66, 3276.05) * mm, "end": v(-140.8, 3276.1) * mm});
            skLineSegment(sketch, "E347.0.45.18", {"start": v(-140.8, 3276.1) * mm, "end": v(-148.54, 3276.1) * mm});
            skArc(sketch, "E347.0.45.19", {"start": v(-90.74, 3250.9) * mm, "mid": v(-90.68, 3250.77) * mm, "end": v(-90.54, 3250.7) * mm});
            skLineSegment(sketch, "E347.0.45.20", {"start": v(-90.74, 3252.7) * mm, "end": v(-90.74, 3250.9) * mm});
            skLineSegment(sketch, "E347.0.45.21", {"start": v(-82.6, 3250.9) * mm, "end": v(-82.6, 3252.7) * mm});
            skArc(sketch, "E347.0.45.22", {"start": v(-148.54, 3276.1) * mm, "mid": v(-148.68, 3276.05) * mm, "end": v(-148.74, 3275.9) * mm});
            skLineSegment(sketch, "E347.0.45.23", {"start": v(-148.74, 3275.9) * mm, "end": v(-148.74, 3274.1) * mm});
            skArc(sketch, "E347.0.45.24", {"start": v(-148.74, 3250.9) * mm, "mid": v(-148.68, 3250.77) * mm, "end": v(-148.54, 3250.7) * mm});
            skLineSegment(sketch, "E347.0.45.25", {"start": v(-148.74, 3252.7) * mm, "end": v(-148.74, 3250.9) * mm});
            skLineSegment(sketch, "E347.0.45.26", {"start": v(-90.54, 3250.7) * mm, "end": v(-82.8, 3250.7) * mm});
            skArc(sketch, "E347.0.45.27", {"start": v(-82.8, 3250.7) * mm, "mid": v(-82.66, 3250.77) * mm, "end": v(-82.6, 3250.9) * mm});
            skLineSegment(sketch, "E347.0.46.0", {"start": v(-92.06, 3339.6) * mm, "end": v(-90.74, 3328.9) * mm});
            skLineSegment(sketch, "E347.0.46.1", {"start": v(-139.29, 3339.6) * mm, "end": v(-140.6, 3350.3) * mm});
            skLineSegment(sketch, "E347.0.46.2", {"start": v(-81.29, 3339.6) * mm, "end": v(-82.6, 3350.3) * mm});
            skLineSegment(sketch, "E347.0.46.3", {"start": v(-82.6, 3328.9) * mm, "end": v(-81.29, 3339.6) * mm});
            skLineSegment(sketch, "E347.0.46.4", {"start": v(-140.6, 3328.9) * mm, "end": v(-139.29, 3339.6) * mm});
            skLineSegment(sketch, "E347.0.46.5", {"start": v(-150.06, 3339.6) * mm, "end": v(-148.74, 3328.9) * mm});
            skLineSegment(sketch, "E347.0.46.6", {"start": v(-90.74, 3350.3) * mm, "end": v(-92.06, 3339.6) * mm});
            skLineSegment(sketch, "E347.0.46.7", {"start": v(-148.74, 3350.3) * mm, "end": v(-150.06, 3339.6) * mm});
            skLineSegment(sketch, "E347.0.46.8", {"start": v(-90.74, 3352.1) * mm, "end": v(-90.74, 3350.3) * mm});
            skLineSegment(sketch, "E347.0.46.9", {"start": v(-148.54, 3326.9) * mm, "end": v(-140.8, 3326.9) * mm});
            skArc(sketch, "E347.0.46.10", {"start": v(-82.6, 3352.1) * mm, "mid": v(-82.66, 3352.25) * mm, "end": v(-82.8, 3352.3) * mm});
            skLineSegment(sketch, "E347.0.46.11", {"start": v(-82.8, 3352.3) * mm, "end": v(-90.54, 3352.3) * mm});
            skArc(sketch, "E347.0.46.12", {"start": v(-140.8, 3326.9) * mm, "mid": v(-140.66, 3326.97) * mm, "end": v(-140.6, 3327.1) * mm});
            skLineSegment(sketch, "E347.0.46.13", {"start": v(-82.6, 3350.3) * mm, "end": v(-82.6, 3352.1) * mm});
            skLineSegment(sketch, "E347.0.46.14", {"start": v(-140.6, 3327.1) * mm, "end": v(-140.6, 3328.9) * mm});
            skArc(sketch, "E347.0.46.15", {"start": v(-90.54, 3352.3) * mm, "mid": v(-90.68, 3352.25) * mm, "end": v(-90.74, 3352.1) * mm});
            skLineSegment(sketch, "E347.0.46.16", {"start": v(-140.6, 3350.3) * mm, "end": v(-140.6, 3352.1) * mm});
            skArc(sketch, "E347.0.46.17", {"start": v(-140.6, 3352.1) * mm, "mid": v(-140.66, 3352.25) * mm, "end": v(-140.8, 3352.3) * mm});
            skLineSegment(sketch, "E347.0.46.18", {"start": v(-140.8, 3352.3) * mm, "end": v(-148.54, 3352.3) * mm});
            skArc(sketch, "E347.0.46.19", {"start": v(-90.74, 3327.1) * mm, "mid": v(-90.68, 3326.97) * mm, "end": v(-90.54, 3326.9) * mm});
            skLineSegment(sketch, "E347.0.46.20", {"start": v(-90.74, 3328.9) * mm, "end": v(-90.74, 3327.1) * mm});
            skLineSegment(sketch, "E347.0.46.21", {"start": v(-82.6, 3327.1) * mm, "end": v(-82.6, 3328.9) * mm});
            skArc(sketch, "E347.0.46.22", {"start": v(-148.54, 3352.3) * mm, "mid": v(-148.68, 3352.25) * mm, "end": v(-148.74, 3352.1) * mm});
            skLineSegment(sketch, "E347.0.46.23", {"start": v(-148.74, 3352.1) * mm, "end": v(-148.74, 3350.3) * mm});
            skArc(sketch, "E347.0.46.24", {"start": v(-148.74, 3327.1) * mm, "mid": v(-148.68, 3326.97) * mm, "end": v(-148.54, 3326.9) * mm});
            skLineSegment(sketch, "E347.0.46.25", {"start": v(-148.74, 3328.9) * mm, "end": v(-148.74, 3327.1) * mm});
            skLineSegment(sketch, "E347.0.46.26", {"start": v(-90.54, 3326.9) * mm, "end": v(-82.8, 3326.9) * mm});
            skArc(sketch, "E347.0.46.27", {"start": v(-82.8, 3326.9) * mm, "mid": v(-82.66, 3326.97) * mm, "end": v(-82.6, 3327.1) * mm});
            skLineSegment(sketch, "E347.0.47.0", {"start": v(-92.06, 3415.8) * mm, "end": v(-90.74, 3405.1) * mm});
            skLineSegment(sketch, "E347.0.47.1", {"start": v(-139.29, 3415.8) * mm, "end": v(-140.6, 3426.5) * mm});
            skLineSegment(sketch, "E347.0.47.2", {"start": v(-81.29, 3415.8) * mm, "end": v(-82.6, 3426.5) * mm});
            skLineSegment(sketch, "E347.0.47.3", {"start": v(-82.6, 3405.1) * mm, "end": v(-81.29, 3415.8) * mm});
            skLineSegment(sketch, "E347.0.47.4", {"start": v(-140.6, 3405.1) * mm, "end": v(-139.29, 3415.8) * mm});
            skLineSegment(sketch, "E347.0.47.5", {"start": v(-150.06, 3415.8) * mm, "end": v(-148.74, 3405.1) * mm});
            skLineSegment(sketch, "E347.0.47.6", {"start": v(-90.74, 3426.5) * mm, "end": v(-92.06, 3415.8) * mm});
            skLineSegment(sketch, "E347.0.47.7", {"start": v(-148.74, 3426.5) * mm, "end": v(-150.06, 3415.8) * mm});
            skLineSegment(sketch, "E347.0.47.8", {"start": v(-90.74, 3428.3) * mm, "end": v(-90.74, 3426.5) * mm});
            skLineSegment(sketch, "E347.0.47.9", {"start": v(-148.54, 3403.1) * mm, "end": v(-140.8, 3403.1) * mm});
            skArc(sketch, "E347.0.47.10", {"start": v(-82.6, 3428.3) * mm, "mid": v(-82.66, 3428.45) * mm, "end": v(-82.8, 3428.5) * mm});
            skLineSegment(sketch, "E347.0.47.11", {"start": v(-82.8, 3428.5) * mm, "end": v(-90.54, 3428.5) * mm});
            skArc(sketch, "E347.0.47.12", {"start": v(-140.8, 3403.1) * mm, "mid": v(-140.66, 3403.17) * mm, "end": v(-140.6, 3403.3) * mm});
            skLineSegment(sketch, "E347.0.47.13", {"start": v(-82.6, 3426.5) * mm, "end": v(-82.6, 3428.3) * mm});
            skLineSegment(sketch, "E347.0.47.14", {"start": v(-140.6, 3403.3) * mm, "end": v(-140.6, 3405.1) * mm});
            skArc(sketch, "E347.0.47.15", {"start": v(-90.54, 3428.5) * mm, "mid": v(-90.68, 3428.45) * mm, "end": v(-90.74, 3428.3) * mm});
            skLineSegment(sketch, "E347.0.47.16", {"start": v(-140.6, 3426.5) * mm, "end": v(-140.6, 3428.3) * mm});
            skArc(sketch, "E347.0.47.17", {"start": v(-140.6, 3428.3) * mm, "mid": v(-140.66, 3428.45) * mm, "end": v(-140.8, 3428.5) * mm});
            skLineSegment(sketch, "E347.0.47.18", {"start": v(-140.8, 3428.5) * mm, "end": v(-148.54, 3428.5) * mm});
            skArc(sketch, "E347.0.47.19", {"start": v(-90.74, 3403.3) * mm, "mid": v(-90.68, 3403.17) * mm, "end": v(-90.54, 3403.1) * mm});
            skLineSegment(sketch, "E347.0.47.20", {"start": v(-90.74, 3405.1) * mm, "end": v(-90.74, 3403.3) * mm});
            skLineSegment(sketch, "E347.0.47.21", {"start": v(-82.6, 3403.3) * mm, "end": v(-82.6, 3405.1) * mm});
            skArc(sketch, "E347.0.47.22", {"start": v(-148.54, 3428.5) * mm, "mid": v(-148.68, 3428.45) * mm, "end": v(-148.74, 3428.3) * mm});
            skLineSegment(sketch, "E347.0.47.23", {"start": v(-148.74, 3428.3) * mm, "end": v(-148.74, 3426.5) * mm});
            skArc(sketch, "E347.0.47.24", {"start": v(-148.74, 3403.3) * mm, "mid": v(-148.68, 3403.17) * mm, "end": v(-148.54, 3403.1) * mm});
            skLineSegment(sketch, "E347.0.47.25", {"start": v(-148.74, 3405.1) * mm, "end": v(-148.74, 3403.3) * mm});
            skLineSegment(sketch, "E347.0.47.26", {"start": v(-90.54, 3403.1) * mm, "end": v(-82.8, 3403.1) * mm});
            skArc(sketch, "E347.0.47.27", {"start": v(-82.8, 3403.1) * mm, "mid": v(-82.66, 3403.17) * mm, "end": v(-82.6, 3403.3) * mm});
            skLineSegment(sketch, "E347.0.48.0", {"start": v(-92.06, 3492) * mm, "end": v(-90.74, 3481.3) * mm});
            skLineSegment(sketch, "E347.0.48.1", {"start": v(-139.29, 3492) * mm, "end": v(-140.6, 3502.7) * mm});
            skLineSegment(sketch, "E347.0.48.2", {"start": v(-81.29, 3492) * mm, "end": v(-82.6, 3502.7) * mm});
            skLineSegment(sketch, "E347.0.48.3", {"start": v(-82.6, 3481.3) * mm, "end": v(-81.29, 3492) * mm});
            skLineSegment(sketch, "E347.0.48.4", {"start": v(-140.6, 3481.3) * mm, "end": v(-139.29, 3492) * mm});
            skLineSegment(sketch, "E347.0.48.5", {"start": v(-150.06, 3492) * mm, "end": v(-148.74, 3481.3) * mm});
            skLineSegment(sketch, "E347.0.48.6", {"start": v(-90.74, 3502.7) * mm, "end": v(-92.06, 3492) * mm});
            skLineSegment(sketch, "E347.0.48.7", {"start": v(-148.74, 3502.7) * mm, "end": v(-150.06, 3492) * mm});
            skLineSegment(sketch, "E347.0.48.8", {"start": v(-90.74, 3504.5) * mm, "end": v(-90.74, 3502.7) * mm});
            skLineSegment(sketch, "E347.0.48.9", {"start": v(-148.54, 3479.3) * mm, "end": v(-140.8, 3479.3) * mm});
            skArc(sketch, "E347.0.48.10", {"start": v(-82.6, 3504.5) * mm, "mid": v(-82.66, 3504.65) * mm, "end": v(-82.8, 3504.7) * mm});
            skLineSegment(sketch, "E347.0.48.11", {"start": v(-82.8, 3504.7) * mm, "end": v(-90.54, 3504.7) * mm});
            skArc(sketch, "E347.0.48.12", {"start": v(-140.8, 3479.3) * mm, "mid": v(-140.66, 3479.37) * mm, "end": v(-140.6, 3479.5) * mm});
            skLineSegment(sketch, "E347.0.48.13", {"start": v(-82.6, 3502.7) * mm, "end": v(-82.6, 3504.5) * mm});
            skLineSegment(sketch, "E347.0.48.14", {"start": v(-140.6, 3479.5) * mm, "end": v(-140.6, 3481.3) * mm});
            skArc(sketch, "E347.0.48.15", {"start": v(-90.54, 3504.7) * mm, "mid": v(-90.68, 3504.65) * mm, "end": v(-90.74, 3504.5) * mm});
            skLineSegment(sketch, "E347.0.48.16", {"start": v(-140.6, 3502.7) * mm, "end": v(-140.6, 3504.5) * mm});
            skArc(sketch, "E347.0.48.17", {"start": v(-140.6, 3504.5) * mm, "mid": v(-140.66, 3504.65) * mm, "end": v(-140.8, 3504.7) * mm});
            skLineSegment(sketch, "E347.0.48.18", {"start": v(-140.8, 3504.7) * mm, "end": v(-148.54, 3504.7) * mm});
            skArc(sketch, "E347.0.48.19", {"start": v(-90.74, 3479.5) * mm, "mid": v(-90.68, 3479.37) * mm, "end": v(-90.54, 3479.3) * mm});
            skLineSegment(sketch, "E347.0.48.20", {"start": v(-90.74, 3481.3) * mm, "end": v(-90.74, 3479.5) * mm});
            skLineSegment(sketch, "E347.0.48.21", {"start": v(-82.6, 3479.5) * mm, "end": v(-82.6, 3481.3) * mm});
            skArc(sketch, "E347.0.48.22", {"start": v(-148.54, 3504.7) * mm, "mid": v(-148.68, 3504.65) * mm, "end": v(-148.74, 3504.5) * mm});
            skLineSegment(sketch, "E347.0.48.23", {"start": v(-148.74, 3504.5) * mm, "end": v(-148.74, 3502.7) * mm});
            skArc(sketch, "E347.0.48.24", {"start": v(-148.74, 3479.5) * mm, "mid": v(-148.68, 3479.37) * mm, "end": v(-148.54, 3479.3) * mm});
            skLineSegment(sketch, "E347.0.48.25", {"start": v(-148.74, 3481.3) * mm, "end": v(-148.74, 3479.5) * mm});
            skLineSegment(sketch, "E347.0.48.26", {"start": v(-90.54, 3479.3) * mm, "end": v(-82.8, 3479.3) * mm});
            skArc(sketch, "E347.0.48.27", {"start": v(-82.8, 3479.3) * mm, "mid": v(-82.66, 3479.37) * mm, "end": v(-82.6, 3479.5) * mm});
            skLineSegment(sketch, "E347.0.49.0", {"start": v(-92.06, 3568.2) * mm, "end": v(-90.74, 3557.5) * mm});
            skLineSegment(sketch, "E347.0.49.1", {"start": v(-139.29, 3568.2) * mm, "end": v(-140.6, 3578.9) * mm});
            skLineSegment(sketch, "E347.0.49.2", {"start": v(-81.29, 3568.2) * mm, "end": v(-82.6, 3578.9) * mm});
            skLineSegment(sketch, "E347.0.49.3", {"start": v(-82.6, 3557.5) * mm, "end": v(-81.29, 3568.2) * mm});
            skLineSegment(sketch, "E347.0.49.4", {"start": v(-140.6, 3557.5) * mm, "end": v(-139.29, 3568.2) * mm});
            skLineSegment(sketch, "E347.0.49.5", {"start": v(-150.06, 3568.2) * mm, "end": v(-148.74, 3557.5) * mm});
            skLineSegment(sketch, "E347.0.49.6", {"start": v(-90.74, 3578.9) * mm, "end": v(-92.06, 3568.2) * mm});
            skLineSegment(sketch, "E347.0.49.7", {"start": v(-148.74, 3578.9) * mm, "end": v(-150.06, 3568.2) * mm});
            skLineSegment(sketch, "E347.0.49.8", {"start": v(-90.74, 3580.7) * mm, "end": v(-90.74, 3578.9) * mm});
            skLineSegment(sketch, "E347.0.49.9", {"start": v(-148.54, 3555.5) * mm, "end": v(-140.8, 3555.5) * mm});
            skArc(sketch, "E347.0.49.10", {"start": v(-82.6, 3580.7) * mm, "mid": v(-82.66, 3580.85) * mm, "end": v(-82.8, 3580.9) * mm});
            skLineSegment(sketch, "E347.0.49.11", {"start": v(-82.8, 3580.9) * mm, "end": v(-90.54, 3580.9) * mm});
            skArc(sketch, "E347.0.49.12", {"start": v(-140.8, 3555.5) * mm, "mid": v(-140.66, 3555.57) * mm, "end": v(-140.6, 3555.7) * mm});
            skLineSegment(sketch, "E347.0.49.13", {"start": v(-82.6, 3578.9) * mm, "end": v(-82.6, 3580.7) * mm});
            skLineSegment(sketch, "E347.0.49.14", {"start": v(-140.6, 3555.7) * mm, "end": v(-140.6, 3557.5) * mm});
            skArc(sketch, "E347.0.49.15", {"start": v(-90.54, 3580.9) * mm, "mid": v(-90.68, 3580.85) * mm, "end": v(-90.74, 3580.7) * mm});
            skLineSegment(sketch, "E347.0.49.16", {"start": v(-140.6, 3578.9) * mm, "end": v(-140.6, 3580.7) * mm});
            skArc(sketch, "E347.0.49.17", {"start": v(-140.6, 3580.7) * mm, "mid": v(-140.66, 3580.85) * mm, "end": v(-140.8, 3580.9) * mm});
            skLineSegment(sketch, "E347.0.49.18", {"start": v(-140.8, 3580.9) * mm, "end": v(-148.54, 3580.9) * mm});
            skArc(sketch, "E347.0.49.19", {"start": v(-90.74, 3555.7) * mm, "mid": v(-90.68, 3555.57) * mm, "end": v(-90.54, 3555.5) * mm});
            skLineSegment(sketch, "E347.0.49.20", {"start": v(-90.74, 3557.5) * mm, "end": v(-90.74, 3555.7) * mm});
            skLineSegment(sketch, "E347.0.49.21", {"start": v(-82.6, 3555.7) * mm, "end": v(-82.6, 3557.5) * mm});
            skArc(sketch, "E347.0.49.22", {"start": v(-148.54, 3580.9) * mm, "mid": v(-148.68, 3580.85) * mm, "end": v(-148.74, 3580.7) * mm});
            skLineSegment(sketch, "E347.0.49.23", {"start": v(-148.74, 3580.7) * mm, "end": v(-148.74, 3578.9) * mm});
            skArc(sketch, "E347.0.49.24", {"start": v(-148.74, 3555.7) * mm, "mid": v(-148.68, 3555.57) * mm, "end": v(-148.54, 3555.5) * mm});
            skLineSegment(sketch, "E347.0.49.25", {"start": v(-148.74, 3557.5) * mm, "end": v(-148.74, 3555.7) * mm});
            skLineSegment(sketch, "E347.0.49.26", {"start": v(-90.54, 3555.5) * mm, "end": v(-82.8, 3555.5) * mm});
            skArc(sketch, "E347.0.49.27", {"start": v(-82.8, 3555.5) * mm, "mid": v(-82.66, 3555.57) * mm, "end": v(-82.6, 3555.7) * mm});
            skLineSegment(sketch, "E347.0.50.0", {"start": v(-92.06, 3644.4) * mm, "end": v(-90.74, 3633.7) * mm});
            skLineSegment(sketch, "E347.0.50.1", {"start": v(-139.29, 3644.4) * mm, "end": v(-140.6, 3655.1) * mm});
            skLineSegment(sketch, "E347.0.50.2", {"start": v(-81.29, 3644.4) * mm, "end": v(-82.6, 3655.1) * mm});
            skLineSegment(sketch, "E347.0.50.3", {"start": v(-82.6, 3633.7) * mm, "end": v(-81.29, 3644.4) * mm});
            skLineSegment(sketch, "E347.0.50.4", {"start": v(-140.6, 3633.7) * mm, "end": v(-139.29, 3644.4) * mm});
            skLineSegment(sketch, "E347.0.50.5", {"start": v(-150.06, 3644.4) * mm, "end": v(-148.74, 3633.7) * mm});
            skLineSegment(sketch, "E347.0.50.6", {"start": v(-90.74, 3655.1) * mm, "end": v(-92.06, 3644.4) * mm});
            skLineSegment(sketch, "E347.0.50.7", {"start": v(-148.74, 3655.1) * mm, "end": v(-150.06, 3644.4) * mm});
            skLineSegment(sketch, "E347.0.50.8", {"start": v(-90.74, 3656.9) * mm, "end": v(-90.74, 3655.1) * mm});
            skLineSegment(sketch, "E347.0.50.9", {"start": v(-148.54, 3631.7) * mm, "end": v(-140.8, 3631.7) * mm});
            skArc(sketch, "E347.0.50.10", {"start": v(-82.6, 3656.9) * mm, "mid": v(-82.66, 3657.05) * mm, "end": v(-82.8, 3657.1) * mm});
            skLineSegment(sketch, "E347.0.50.11", {"start": v(-82.8, 3657.1) * mm, "end": v(-90.54, 3657.1) * mm});
            skArc(sketch, "E347.0.50.12", {"start": v(-140.8, 3631.7) * mm, "mid": v(-140.66, 3631.77) * mm, "end": v(-140.6, 3631.9) * mm});
            skLineSegment(sketch, "E347.0.50.13", {"start": v(-82.6, 3655.1) * mm, "end": v(-82.6, 3656.9) * mm});
            skLineSegment(sketch, "E347.0.50.14", {"start": v(-140.6, 3631.9) * mm, "end": v(-140.6, 3633.7) * mm});
            skArc(sketch, "E347.0.50.15", {"start": v(-90.54, 3657.1) * mm, "mid": v(-90.68, 3657.05) * mm, "end": v(-90.74, 3656.9) * mm});
            skLineSegment(sketch, "E347.0.50.16", {"start": v(-140.6, 3655.1) * mm, "end": v(-140.6, 3656.9) * mm});
            skArc(sketch, "E347.0.50.17", {"start": v(-140.6, 3656.9) * mm, "mid": v(-140.66, 3657.05) * mm, "end": v(-140.8, 3657.1) * mm});
            skLineSegment(sketch, "E347.0.50.18", {"start": v(-140.8, 3657.1) * mm, "end": v(-148.54, 3657.1) * mm});
            skArc(sketch, "E347.0.50.19", {"start": v(-90.74, 3631.9) * mm, "mid": v(-90.68, 3631.77) * mm, "end": v(-90.54, 3631.7) * mm});
            skLineSegment(sketch, "E347.0.50.20", {"start": v(-90.74, 3633.7) * mm, "end": v(-90.74, 3631.9) * mm});
            skLineSegment(sketch, "E347.0.50.21", {"start": v(-82.6, 3631.9) * mm, "end": v(-82.6, 3633.7) * mm});
            skArc(sketch, "E347.0.50.22", {"start": v(-148.54, 3657.1) * mm, "mid": v(-148.68, 3657.05) * mm, "end": v(-148.74, 3656.9) * mm});
            skLineSegment(sketch, "E347.0.50.23", {"start": v(-148.74, 3656.9) * mm, "end": v(-148.74, 3655.1) * mm});
            skArc(sketch, "E347.0.50.24", {"start": v(-148.74, 3631.9) * mm, "mid": v(-148.68, 3631.77) * mm, "end": v(-148.54, 3631.7) * mm});
            skLineSegment(sketch, "E347.0.50.25", {"start": v(-148.74, 3633.7) * mm, "end": v(-148.74, 3631.9) * mm});
            skLineSegment(sketch, "E347.0.50.26", {"start": v(-90.54, 3631.7) * mm, "end": v(-82.8, 3631.7) * mm});
            skArc(sketch, "E347.0.50.27", {"start": v(-82.8, 3631.7) * mm, "mid": v(-82.66, 3631.77) * mm, "end": v(-82.6, 3631.9) * mm});
            skLineSegment(sketch, "E347.0.51.0", {"start": v(-92.06, 3720.6) * mm, "end": v(-90.74, 3709.9) * mm});
            skLineSegment(sketch, "E347.0.51.1", {"start": v(-139.29, 3720.6) * mm, "end": v(-140.6, 3731.3) * mm});
            skLineSegment(sketch, "E347.0.51.2", {"start": v(-81.29, 3720.6) * mm, "end": v(-82.6, 3731.3) * mm});
            skLineSegment(sketch, "E347.0.51.3", {"start": v(-82.6, 3709.9) * mm, "end": v(-81.29, 3720.6) * mm});
            skLineSegment(sketch, "E347.0.51.4", {"start": v(-140.6, 3709.9) * mm, "end": v(-139.29, 3720.6) * mm});
            skLineSegment(sketch, "E347.0.51.5", {"start": v(-150.06, 3720.6) * mm, "end": v(-148.74, 3709.9) * mm});
            skLineSegment(sketch, "E347.0.51.6", {"start": v(-90.74, 3731.3) * mm, "end": v(-92.06, 3720.6) * mm});
            skLineSegment(sketch, "E347.0.51.7", {"start": v(-148.74, 3731.3) * mm, "end": v(-150.06, 3720.6) * mm});
            skLineSegment(sketch, "E347.0.51.8", {"start": v(-90.74, 3733.1) * mm, "end": v(-90.74, 3731.3) * mm});
            skLineSegment(sketch, "E347.0.51.9", {"start": v(-148.54, 3707.9) * mm, "end": v(-140.8, 3707.9) * mm});
            skArc(sketch, "E347.0.51.10", {"start": v(-82.6, 3733.1) * mm, "mid": v(-82.66, 3733.25) * mm, "end": v(-82.8, 3733.3) * mm});
            skLineSegment(sketch, "E347.0.51.11", {"start": v(-82.8, 3733.3) * mm, "end": v(-90.54, 3733.3) * mm});
            skArc(sketch, "E347.0.51.12", {"start": v(-140.8, 3707.9) * mm, "mid": v(-140.66, 3707.97) * mm, "end": v(-140.6, 3708.1) * mm});
            skLineSegment(sketch, "E347.0.51.13", {"start": v(-82.6, 3731.3) * mm, "end": v(-82.6, 3733.1) * mm});
            skLineSegment(sketch, "E347.0.51.14", {"start": v(-140.6, 3708.1) * mm, "end": v(-140.6, 3709.9) * mm});
            skArc(sketch, "E347.0.51.15", {"start": v(-90.54, 3733.3) * mm, "mid": v(-90.68, 3733.25) * mm, "end": v(-90.74, 3733.1) * mm});
            skLineSegment(sketch, "E347.0.51.16", {"start": v(-140.6, 3731.3) * mm, "end": v(-140.6, 3733.1) * mm});
            skArc(sketch, "E347.0.51.17", {"start": v(-140.6, 3733.1) * mm, "mid": v(-140.66, 3733.25) * mm, "end": v(-140.8, 3733.3) * mm});
            skLineSegment(sketch, "E347.0.51.18", {"start": v(-140.8, 3733.3) * mm, "end": v(-148.54, 3733.3) * mm});
            skArc(sketch, "E347.0.51.19", {"start": v(-90.74, 3708.1) * mm, "mid": v(-90.68, 3707.97) * mm, "end": v(-90.54, 3707.9) * mm});
            skLineSegment(sketch, "E347.0.51.20", {"start": v(-90.74, 3709.9) * mm, "end": v(-90.74, 3708.1) * mm});
            skLineSegment(sketch, "E347.0.51.21", {"start": v(-82.6, 3708.1) * mm, "end": v(-82.6, 3709.9) * mm});
            skArc(sketch, "E347.0.51.22", {"start": v(-148.54, 3733.3) * mm, "mid": v(-148.68, 3733.25) * mm, "end": v(-148.74, 3733.1) * mm});
            skLineSegment(sketch, "E347.0.51.23", {"start": v(-148.74, 3733.1) * mm, "end": v(-148.74, 3731.3) * mm});
            skArc(sketch, "E347.0.51.24", {"start": v(-148.74, 3708.1) * mm, "mid": v(-148.68, 3707.97) * mm, "end": v(-148.54, 3707.9) * mm});
            skLineSegment(sketch, "E347.0.51.25", {"start": v(-148.74, 3709.9) * mm, "end": v(-148.74, 3708.1) * mm});
            skLineSegment(sketch, "E347.0.51.26", {"start": v(-90.54, 3707.9) * mm, "end": v(-82.8, 3707.9) * mm});
            skArc(sketch, "E347.0.51.27", {"start": v(-82.8, 3707.9) * mm, "mid": v(-82.66, 3707.97) * mm, "end": v(-82.6, 3708.1) * mm});
            skLineSegment(sketch, "E347.0.52.0", {"start": v(-92.06, 3796.8) * mm, "end": v(-90.74, 3786.1) * mm});
            skLineSegment(sketch, "E347.0.52.1", {"start": v(-139.29, 3796.8) * mm, "end": v(-140.6, 3807.5) * mm});
            skLineSegment(sketch, "E347.0.52.2", {"start": v(-81.29, 3796.8) * mm, "end": v(-82.6, 3807.5) * mm});
            skLineSegment(sketch, "E347.0.52.3", {"start": v(-82.6, 3786.1) * mm, "end": v(-81.29, 3796.8) * mm});
            skLineSegment(sketch, "E347.0.52.4", {"start": v(-140.6, 3786.1) * mm, "end": v(-139.29, 3796.8) * mm});
            skLineSegment(sketch, "E347.0.52.5", {"start": v(-150.06, 3796.8) * mm, "end": v(-148.74, 3786.1) * mm});
            skLineSegment(sketch, "E347.0.52.6", {"start": v(-90.74, 3807.5) * mm, "end": v(-92.06, 3796.8) * mm});
            skLineSegment(sketch, "E347.0.52.7", {"start": v(-148.74, 3807.5) * mm, "end": v(-150.06, 3796.8) * mm});
            skLineSegment(sketch, "E347.0.52.8", {"start": v(-90.74, 3809.3) * mm, "end": v(-90.74, 3807.5) * mm});
            skLineSegment(sketch, "E347.0.52.9", {"start": v(-148.54, 3784.1) * mm, "end": v(-140.8, 3784.1) * mm});
            skArc(sketch, "E347.0.52.10", {"start": v(-82.6, 3809.3) * mm, "mid": v(-82.66, 3809.45) * mm, "end": v(-82.8, 3809.5) * mm});
            skLineSegment(sketch, "E347.0.52.11", {"start": v(-82.8, 3809.5) * mm, "end": v(-90.54, 3809.5) * mm});
            skArc(sketch, "E347.0.52.12", {"start": v(-140.8, 3784.1) * mm, "mid": v(-140.66, 3784.17) * mm, "end": v(-140.6, 3784.3) * mm});
            skLineSegment(sketch, "E347.0.52.13", {"start": v(-82.6, 3807.5) * mm, "end": v(-82.6, 3809.3) * mm});
            skLineSegment(sketch, "E347.0.52.14", {"start": v(-140.6, 3784.3) * mm, "end": v(-140.6, 3786.1) * mm});
            skArc(sketch, "E347.0.52.15", {"start": v(-90.54, 3809.5) * mm, "mid": v(-90.68, 3809.45) * mm, "end": v(-90.74, 3809.3) * mm});
            skLineSegment(sketch, "E347.0.52.16", {"start": v(-140.6, 3807.5) * mm, "end": v(-140.6, 3809.3) * mm});
            skArc(sketch, "E347.0.52.17", {"start": v(-140.6, 3809.3) * mm, "mid": v(-140.66, 3809.45) * mm, "end": v(-140.8, 3809.5) * mm});
            skLineSegment(sketch, "E347.0.52.18", {"start": v(-140.8, 3809.5) * mm, "end": v(-148.54, 3809.5) * mm});
            skArc(sketch, "E347.0.52.19", {"start": v(-90.74, 3784.3) * mm, "mid": v(-90.68, 3784.17) * mm, "end": v(-90.54, 3784.1) * mm});
            skLineSegment(sketch, "E347.0.52.20", {"start": v(-90.74, 3786.1) * mm, "end": v(-90.74, 3784.3) * mm});
            skLineSegment(sketch, "E347.0.52.21", {"start": v(-82.6, 3784.3) * mm, "end": v(-82.6, 3786.1) * mm});
            skArc(sketch, "E347.0.52.22", {"start": v(-148.54, 3809.5) * mm, "mid": v(-148.68, 3809.45) * mm, "end": v(-148.74, 3809.3) * mm});
            skLineSegment(sketch, "E347.0.52.23", {"start": v(-148.74, 3809.3) * mm, "end": v(-148.74, 3807.5) * mm});
            skArc(sketch, "E347.0.52.24", {"start": v(-148.74, 3784.3) * mm, "mid": v(-148.68, 3784.17) * mm, "end": v(-148.54, 3784.1) * mm});
            skLineSegment(sketch, "E347.0.52.25", {"start": v(-148.74, 3786.1) * mm, "end": v(-148.74, 3784.3) * mm});
            skLineSegment(sketch, "E347.0.52.26", {"start": v(-90.54, 3784.1) * mm, "end": v(-82.8, 3784.1) * mm});
            skArc(sketch, "E347.0.52.27", {"start": v(-82.8, 3784.1) * mm, "mid": v(-82.66, 3784.17) * mm, "end": v(-82.6, 3784.3) * mm});
            skLineSegment(sketch, "E347.0.53.0", {"start": v(-92.06, 3873) * mm, "end": v(-90.74, 3862.3) * mm});
            skLineSegment(sketch, "E347.0.53.1", {"start": v(-139.29, 3873) * mm, "end": v(-140.6, 3883.7) * mm});
            skLineSegment(sketch, "E347.0.53.2", {"start": v(-81.29, 3873) * mm, "end": v(-82.6, 3883.7) * mm});
            skLineSegment(sketch, "E347.0.53.3", {"start": v(-82.6, 3862.3) * mm, "end": v(-81.29, 3873) * mm});
            skLineSegment(sketch, "E347.0.53.4", {"start": v(-140.6, 3862.3) * mm, "end": v(-139.29, 3873) * mm});
            skLineSegment(sketch, "E347.0.53.5", {"start": v(-150.06, 3873) * mm, "end": v(-148.74, 3862.3) * mm});
            skLineSegment(sketch, "E347.0.53.6", {"start": v(-90.74, 3883.7) * mm, "end": v(-92.06, 3873) * mm});
            skLineSegment(sketch, "E347.0.53.7", {"start": v(-148.74, 3883.7) * mm, "end": v(-150.06, 3873) * mm});
            skLineSegment(sketch, "E347.0.53.8", {"start": v(-90.74, 3885.5) * mm, "end": v(-90.74, 3883.7) * mm});
            skLineSegment(sketch, "E347.0.53.9", {"start": v(-148.54, 3860.3) * mm, "end": v(-140.8, 3860.3) * mm});
            skArc(sketch, "E347.0.53.10", {"start": v(-82.6, 3885.5) * mm, "mid": v(-82.66, 3885.65) * mm, "end": v(-82.8, 3885.7) * mm});
            skLineSegment(sketch, "E347.0.53.11", {"start": v(-82.8, 3885.7) * mm, "end": v(-90.54, 3885.7) * mm});
            skArc(sketch, "E347.0.53.12", {"start": v(-140.8, 3860.3) * mm, "mid": v(-140.66, 3860.37) * mm, "end": v(-140.6, 3860.5) * mm});
            skLineSegment(sketch, "E347.0.53.13", {"start": v(-82.6, 3883.7) * mm, "end": v(-82.6, 3885.5) * mm});
            skLineSegment(sketch, "E347.0.53.14", {"start": v(-140.6, 3860.5) * mm, "end": v(-140.6, 3862.3) * mm});
            skArc(sketch, "E347.0.53.15", {"start": v(-90.54, 3885.7) * mm, "mid": v(-90.68, 3885.65) * mm, "end": v(-90.74, 3885.5) * mm});
            skLineSegment(sketch, "E347.0.53.16", {"start": v(-140.6, 3883.7) * mm, "end": v(-140.6, 3885.5) * mm});
            skArc(sketch, "E347.0.53.17", {"start": v(-140.6, 3885.5) * mm, "mid": v(-140.66, 3885.65) * mm, "end": v(-140.8, 3885.7) * mm});
            skLineSegment(sketch, "E347.0.53.18", {"start": v(-140.8, 3885.7) * mm, "end": v(-148.54, 3885.7) * mm});
            skArc(sketch, "E347.0.53.19", {"start": v(-90.74, 3860.5) * mm, "mid": v(-90.68, 3860.37) * mm, "end": v(-90.54, 3860.3) * mm});
            skLineSegment(sketch, "E347.0.53.20", {"start": v(-90.74, 3862.3) * mm, "end": v(-90.74, 3860.5) * mm});
            skLineSegment(sketch, "E347.0.53.21", {"start": v(-82.6, 3860.5) * mm, "end": v(-82.6, 3862.3) * mm});
            skArc(sketch, "E347.0.53.22", {"start": v(-148.54, 3885.7) * mm, "mid": v(-148.68, 3885.65) * mm, "end": v(-148.74, 3885.5) * mm});
            skLineSegment(sketch, "E347.0.53.23", {"start": v(-148.74, 3885.5) * mm, "end": v(-148.74, 3883.7) * mm});
            skArc(sketch, "E347.0.53.24", {"start": v(-148.74, 3860.5) * mm, "mid": v(-148.68, 3860.37) * mm, "end": v(-148.54, 3860.3) * mm});
            skLineSegment(sketch, "E347.0.53.25", {"start": v(-148.74, 3862.3) * mm, "end": v(-148.74, 3860.5) * mm});
            skLineSegment(sketch, "E347.0.53.26", {"start": v(-90.54, 3860.3) * mm, "end": v(-82.8, 3860.3) * mm});
            skArc(sketch, "E347.0.53.27", {"start": v(-82.8, 3860.3) * mm, "mid": v(-82.66, 3860.37) * mm, "end": v(-82.6, 3860.5) * mm});
            skLineSegment(sketch, "E347.0.54.0", {"start": v(-92.06, 3949.2) * mm, "end": v(-90.74, 3938.5) * mm});
            skLineSegment(sketch, "E347.0.54.1", {"start": v(-139.29, 3949.2) * mm, "end": v(-140.6, 3959.9) * mm});
            skLineSegment(sketch, "E347.0.54.2", {"start": v(-81.29, 3949.2) * mm, "end": v(-82.6, 3959.9) * mm});
            skLineSegment(sketch, "E347.0.54.3", {"start": v(-82.6, 3938.5) * mm, "end": v(-81.29, 3949.2) * mm});
            skLineSegment(sketch, "E347.0.54.4", {"start": v(-140.6, 3938.5) * mm, "end": v(-139.29, 3949.2) * mm});
            skLineSegment(sketch, "E347.0.54.5", {"start": v(-150.06, 3949.2) * mm, "end": v(-148.74, 3938.5) * mm});
            skLineSegment(sketch, "E347.0.54.6", {"start": v(-90.74, 3959.9) * mm, "end": v(-92.06, 3949.2) * mm});
            skLineSegment(sketch, "E347.0.54.7", {"start": v(-148.74, 3959.9) * mm, "end": v(-150.06, 3949.2) * mm});
            skLineSegment(sketch, "E347.0.54.8", {"start": v(-90.74, 3961.7) * mm, "end": v(-90.74, 3959.9) * mm});
            skLineSegment(sketch, "E347.0.54.9", {"start": v(-148.54, 3936.5) * mm, "end": v(-140.8, 3936.5) * mm});
            skArc(sketch, "E347.0.54.10", {"start": v(-82.6, 3961.7) * mm, "mid": v(-82.66, 3961.85) * mm, "end": v(-82.8, 3961.9) * mm});
            skLineSegment(sketch, "E347.0.54.11", {"start": v(-82.8, 3961.9) * mm, "end": v(-90.54, 3961.9) * mm});
            skArc(sketch, "E347.0.54.12", {"start": v(-140.8, 3936.5) * mm, "mid": v(-140.66, 3936.57) * mm, "end": v(-140.6, 3936.7) * mm});
            skLineSegment(sketch, "E347.0.54.13", {"start": v(-82.6, 3959.9) * mm, "end": v(-82.6, 3961.7) * mm});
            skLineSegment(sketch, "E347.0.54.14", {"start": v(-140.6, 3936.7) * mm, "end": v(-140.6, 3938.5) * mm});
            skArc(sketch, "E347.0.54.15", {"start": v(-90.54, 3961.9) * mm, "mid": v(-90.68, 3961.85) * mm, "end": v(-90.74, 3961.7) * mm});
            skLineSegment(sketch, "E347.0.54.16", {"start": v(-140.6, 3959.9) * mm, "end": v(-140.6, 3961.7) * mm});
            skArc(sketch, "E347.0.54.17", {"start": v(-140.6, 3961.7) * mm, "mid": v(-140.66, 3961.85) * mm, "end": v(-140.8, 3961.9) * mm});
            skLineSegment(sketch, "E347.0.54.18", {"start": v(-140.8, 3961.9) * mm, "end": v(-148.54, 3961.9) * mm});
            skArc(sketch, "E347.0.54.19", {"start": v(-90.74, 3936.7) * mm, "mid": v(-90.68, 3936.57) * mm, "end": v(-90.54, 3936.5) * mm});
            skLineSegment(sketch, "E347.0.54.20", {"start": v(-90.74, 3938.5) * mm, "end": v(-90.74, 3936.7) * mm});
            skLineSegment(sketch, "E347.0.54.21", {"start": v(-82.6, 3936.7) * mm, "end": v(-82.6, 3938.5) * mm});
            skArc(sketch, "E347.0.54.22", {"start": v(-148.54, 3961.9) * mm, "mid": v(-148.68, 3961.85) * mm, "end": v(-148.74, 3961.7) * mm});
            skLineSegment(sketch, "E347.0.54.23", {"start": v(-148.74, 3961.7) * mm, "end": v(-148.74, 3959.9) * mm});
            skArc(sketch, "E347.0.54.24", {"start": v(-148.74, 3936.7) * mm, "mid": v(-148.68, 3936.57) * mm, "end": v(-148.54, 3936.5) * mm});
            skLineSegment(sketch, "E347.0.54.25", {"start": v(-148.74, 3938.5) * mm, "end": v(-148.74, 3936.7) * mm});
            skLineSegment(sketch, "E347.0.54.26", {"start": v(-90.54, 3936.5) * mm, "end": v(-82.8, 3936.5) * mm});
            skArc(sketch, "E347.0.54.27", {"start": v(-82.8, 3936.5) * mm, "mid": v(-82.66, 3936.57) * mm, "end": v(-82.6, 3936.7) * mm});
            skLineSegment(sketch, "E347.0.55.0", {"start": v(-92.06, 4025.4) * mm, "end": v(-90.74, 4014.7) * mm});
            skLineSegment(sketch, "E347.0.55.1", {"start": v(-139.29, 4025.4) * mm, "end": v(-140.6, 4036.1) * mm});
            skLineSegment(sketch, "E347.0.55.2", {"start": v(-81.29, 4025.4) * mm, "end": v(-82.6, 4036.1) * mm});
            skLineSegment(sketch, "E347.0.55.3", {"start": v(-82.6, 4014.7) * mm, "end": v(-81.29, 4025.4) * mm});
            skLineSegment(sketch, "E347.0.55.4", {"start": v(-140.6, 4014.7) * mm, "end": v(-139.29, 4025.4) * mm});
            skLineSegment(sketch, "E347.0.55.5", {"start": v(-150.06, 4025.4) * mm, "end": v(-148.74, 4014.7) * mm});
            skLineSegment(sketch, "E347.0.55.6", {"start": v(-90.74, 4036.1) * mm, "end": v(-92.06, 4025.4) * mm});
            skLineSegment(sketch, "E347.0.55.7", {"start": v(-148.74, 4036.1) * mm, "end": v(-150.06, 4025.4) * mm});
            skLineSegment(sketch, "E347.0.55.8", {"start": v(-90.74, 4037.9) * mm, "end": v(-90.74, 4036.1) * mm});
            skLineSegment(sketch, "E347.0.55.9", {"start": v(-148.54, 4012.7) * mm, "end": v(-140.8, 4012.7) * mm});
            skArc(sketch, "E347.0.55.10", {"start": v(-82.6, 4037.9) * mm, "mid": v(-82.66, 4038.05) * mm, "end": v(-82.8, 4038.1) * mm});
            skLineSegment(sketch, "E347.0.55.11", {"start": v(-82.8, 4038.1) * mm, "end": v(-90.54, 4038.1) * mm});
            skArc(sketch, "E347.0.55.12", {"start": v(-140.8, 4012.7) * mm, "mid": v(-140.66, 4012.77) * mm, "end": v(-140.6, 4012.9) * mm});
            skLineSegment(sketch, "E347.0.55.13", {"start": v(-82.6, 4036.1) * mm, "end": v(-82.6, 4037.9) * mm});
            skLineSegment(sketch, "E347.0.55.14", {"start": v(-140.6, 4012.9) * mm, "end": v(-140.6, 4014.7) * mm});
            skArc(sketch, "E347.0.55.15", {"start": v(-90.54, 4038.1) * mm, "mid": v(-90.68, 4038.05) * mm, "end": v(-90.74, 4037.9) * mm});
            skLineSegment(sketch, "E347.0.55.16", {"start": v(-140.6, 4036.1) * mm, "end": v(-140.6, 4037.9) * mm});
            skArc(sketch, "E347.0.55.17", {"start": v(-140.6, 4037.9) * mm, "mid": v(-140.66, 4038.05) * mm, "end": v(-140.8, 4038.1) * mm});
            skLineSegment(sketch, "E347.0.55.18", {"start": v(-140.8, 4038.1) * mm, "end": v(-148.54, 4038.1) * mm});
            skArc(sketch, "E347.0.55.19", {"start": v(-90.74, 4012.9) * mm, "mid": v(-90.68, 4012.77) * mm, "end": v(-90.54, 4012.7) * mm});
            skLineSegment(sketch, "E347.0.55.20", {"start": v(-90.74, 4014.7) * mm, "end": v(-90.74, 4012.9) * mm});
            skLineSegment(sketch, "E347.0.55.21", {"start": v(-82.6, 4012.9) * mm, "end": v(-82.6, 4014.7) * mm});
            skArc(sketch, "E347.0.55.22", {"start": v(-148.54, 4038.1) * mm, "mid": v(-148.68, 4038.05) * mm, "end": v(-148.74, 4037.9) * mm});
            skLineSegment(sketch, "E347.0.55.23", {"start": v(-148.74, 4037.9) * mm, "end": v(-148.74, 4036.1) * mm});
            skArc(sketch, "E347.0.55.24", {"start": v(-148.74, 4012.9) * mm, "mid": v(-148.68, 4012.77) * mm, "end": v(-148.54, 4012.7) * mm});
            skLineSegment(sketch, "E347.0.55.25", {"start": v(-148.74, 4014.7) * mm, "end": v(-148.74, 4012.9) * mm});
            skLineSegment(sketch, "E347.0.55.26", {"start": v(-90.54, 4012.7) * mm, "end": v(-82.8, 4012.7) * mm});
            skArc(sketch, "E347.0.55.27", {"start": v(-82.8, 4012.7) * mm, "mid": v(-82.66, 4012.77) * mm, "end": v(-82.6, 4012.9) * mm});
            skLineSegment(sketch, "E347.0.56.0", {"start": v(-92.06, 4101.6) * mm, "end": v(-90.74, 4090.9) * mm});
            skLineSegment(sketch, "E347.0.56.1", {"start": v(-139.29, 4101.6) * mm, "end": v(-140.6, 4112.3) * mm});
            skLineSegment(sketch, "E347.0.56.2", {"start": v(-81.29, 4101.6) * mm, "end": v(-82.6, 4112.3) * mm});
            skLineSegment(sketch, "E347.0.56.3", {"start": v(-82.6, 4090.9) * mm, "end": v(-81.29, 4101.6) * mm});
            skLineSegment(sketch, "E347.0.56.4", {"start": v(-140.6, 4090.9) * mm, "end": v(-139.29, 4101.6) * mm});
            skLineSegment(sketch, "E347.0.56.5", {"start": v(-150.06, 4101.6) * mm, "end": v(-148.74, 4090.9) * mm});
            skLineSegment(sketch, "E347.0.56.6", {"start": v(-90.74, 4112.3) * mm, "end": v(-92.06, 4101.6) * mm});
            skLineSegment(sketch, "E347.0.56.7", {"start": v(-148.74, 4112.3) * mm, "end": v(-150.06, 4101.6) * mm});
            skLineSegment(sketch, "E347.0.56.8", {"start": v(-90.74, 4114.1) * mm, "end": v(-90.74, 4112.3) * mm});
            skLineSegment(sketch, "E347.0.56.9", {"start": v(-148.54, 4088.9) * mm, "end": v(-140.8, 4088.9) * mm});
            skArc(sketch, "E347.0.56.10", {"start": v(-82.6, 4114.1) * mm, "mid": v(-82.66, 4114.25) * mm, "end": v(-82.8, 4114.3) * mm});
            skLineSegment(sketch, "E347.0.56.11", {"start": v(-82.8, 4114.3) * mm, "end": v(-90.54, 4114.3) * mm});
            skArc(sketch, "E347.0.56.12", {"start": v(-140.8, 4088.9) * mm, "mid": v(-140.66, 4088.97) * mm, "end": v(-140.6, 4089.1) * mm});
            skLineSegment(sketch, "E347.0.56.13", {"start": v(-82.6, 4112.3) * mm, "end": v(-82.6, 4114.1) * mm});
            skLineSegment(sketch, "E347.0.56.14", {"start": v(-140.6, 4089.1) * mm, "end": v(-140.6, 4090.9) * mm});
            skArc(sketch, "E347.0.56.15", {"start": v(-90.54, 4114.3) * mm, "mid": v(-90.68, 4114.25) * mm, "end": v(-90.74, 4114.1) * mm});
            skLineSegment(sketch, "E347.0.56.16", {"start": v(-140.6, 4112.3) * mm, "end": v(-140.6, 4114.1) * mm});
            skArc(sketch, "E347.0.56.17", {"start": v(-140.6, 4114.1) * mm, "mid": v(-140.66, 4114.25) * mm, "end": v(-140.8, 4114.3) * mm});
            skLineSegment(sketch, "E347.0.56.18", {"start": v(-140.8, 4114.3) * mm, "end": v(-148.54, 4114.3) * mm});
            skArc(sketch, "E347.0.56.19", {"start": v(-90.74, 4089.1) * mm, "mid": v(-90.68, 4088.97) * mm, "end": v(-90.54, 4088.9) * mm});
            skLineSegment(sketch, "E347.0.56.20", {"start": v(-90.74, 4090.9) * mm, "end": v(-90.74, 4089.1) * mm});
            skLineSegment(sketch, "E347.0.56.21", {"start": v(-82.6, 4089.1) * mm, "end": v(-82.6, 4090.9) * mm});
            skArc(sketch, "E347.0.56.22", {"start": v(-148.54, 4114.3) * mm, "mid": v(-148.68, 4114.25) * mm, "end": v(-148.74, 4114.1) * mm});
            skLineSegment(sketch, "E347.0.56.23", {"start": v(-148.74, 4114.1) * mm, "end": v(-148.74, 4112.3) * mm});
            skArc(sketch, "E347.0.56.24", {"start": v(-148.74, 4089.1) * mm, "mid": v(-148.68, 4088.97) * mm, "end": v(-148.54, 4088.9) * mm});
            skLineSegment(sketch, "E347.0.56.25", {"start": v(-148.74, 4090.9) * mm, "end": v(-148.74, 4089.1) * mm});
            skLineSegment(sketch, "E347.0.56.26", {"start": v(-90.54, 4088.9) * mm, "end": v(-82.8, 4088.9) * mm});
            skArc(sketch, "E347.0.56.27", {"start": v(-82.8, 4088.9) * mm, "mid": v(-82.66, 4088.97) * mm, "end": v(-82.6, 4089.1) * mm});
            skLineSegment(sketch, "E347.0.57.0", {"start": v(-92.06, 4177.8) * mm, "end": v(-90.74, 4167.1) * mm});
            skLineSegment(sketch, "E347.0.57.1", {"start": v(-139.29, 4177.8) * mm, "end": v(-140.6, 4188.5) * mm});
            skLineSegment(sketch, "E347.0.57.2", {"start": v(-81.29, 4177.8) * mm, "end": v(-82.6, 4188.5) * mm});
            skLineSegment(sketch, "E347.0.57.3", {"start": v(-82.6, 4167.1) * mm, "end": v(-81.29, 4177.8) * mm});
            skLineSegment(sketch, "E347.0.57.4", {"start": v(-140.6, 4167.1) * mm, "end": v(-139.29, 4177.8) * mm});
            skLineSegment(sketch, "E347.0.57.5", {"start": v(-150.06, 4177.8) * mm, "end": v(-148.74, 4167.1) * mm});
            skLineSegment(sketch, "E347.0.57.6", {"start": v(-90.74, 4188.5) * mm, "end": v(-92.06, 4177.8) * mm});
            skLineSegment(sketch, "E347.0.57.7", {"start": v(-148.74, 4188.5) * mm, "end": v(-150.06, 4177.8) * mm});
            skLineSegment(sketch, "E347.0.57.8", {"start": v(-90.74, 4190.3) * mm, "end": v(-90.74, 4188.5) * mm});
            skLineSegment(sketch, "E347.0.57.9", {"start": v(-148.54, 4165.1) * mm, "end": v(-140.8, 4165.1) * mm});
            skArc(sketch, "E347.0.57.10", {"start": v(-82.6, 4190.3) * mm, "mid": v(-82.66, 4190.45) * mm, "end": v(-82.8, 4190.5) * mm});
            skLineSegment(sketch, "E347.0.57.11", {"start": v(-82.8, 4190.5) * mm, "end": v(-90.54, 4190.5) * mm});
            skArc(sketch, "E347.0.57.12", {"start": v(-140.8, 4165.1) * mm, "mid": v(-140.66, 4165.17) * mm, "end": v(-140.6, 4165.3) * mm});
            skLineSegment(sketch, "E347.0.57.13", {"start": v(-82.6, 4188.5) * mm, "end": v(-82.6, 4190.3) * mm});
            skLineSegment(sketch, "E347.0.57.14", {"start": v(-140.6, 4165.3) * mm, "end": v(-140.6, 4167.1) * mm});
            skArc(sketch, "E347.0.57.15", {"start": v(-90.54, 4190.5) * mm, "mid": v(-90.68, 4190.45) * mm, "end": v(-90.74, 4190.3) * mm});
            skLineSegment(sketch, "E347.0.57.16", {"start": v(-140.6, 4188.5) * mm, "end": v(-140.6, 4190.3) * mm});
            skArc(sketch, "E347.0.57.17", {"start": v(-140.6, 4190.3) * mm, "mid": v(-140.66, 4190.45) * mm, "end": v(-140.8, 4190.5) * mm});
            skLineSegment(sketch, "E347.0.57.18", {"start": v(-140.8, 4190.5) * mm, "end": v(-148.54, 4190.5) * mm});
            skArc(sketch, "E347.0.57.19", {"start": v(-90.74, 4165.3) * mm, "mid": v(-90.68, 4165.17) * mm, "end": v(-90.54, 4165.1) * mm});
            skLineSegment(sketch, "E347.0.57.20", {"start": v(-90.74, 4167.1) * mm, "end": v(-90.74, 4165.3) * mm});
            skLineSegment(sketch, "E347.0.57.21", {"start": v(-82.6, 4165.3) * mm, "end": v(-82.6, 4167.1) * mm});
            skArc(sketch, "E347.0.57.22", {"start": v(-148.54, 4190.5) * mm, "mid": v(-148.68, 4190.45) * mm, "end": v(-148.74, 4190.3) * mm});
            skLineSegment(sketch, "E347.0.57.23", {"start": v(-148.74, 4190.3) * mm, "end": v(-148.74, 4188.5) * mm});
            skArc(sketch, "E347.0.57.24", {"start": v(-148.74, 4165.3) * mm, "mid": v(-148.68, 4165.17) * mm, "end": v(-148.54, 4165.1) * mm});
            skLineSegment(sketch, "E347.0.57.25", {"start": v(-148.74, 4167.1) * mm, "end": v(-148.74, 4165.3) * mm});
            skLineSegment(sketch, "E347.0.57.26", {"start": v(-90.54, 4165.1) * mm, "end": v(-82.8, 4165.1) * mm});
            skArc(sketch, "E347.0.57.27", {"start": v(-82.8, 4165.1) * mm, "mid": v(-82.66, 4165.17) * mm, "end": v(-82.6, 4165.3) * mm});
            skLineSegment(sketch, "E347.0.58.0", {"start": v(-92.06, 4254) * mm, "end": v(-90.74, 4243.3) * mm});
            skLineSegment(sketch, "E347.0.58.1", {"start": v(-139.29, 4254) * mm, "end": v(-140.6, 4264.7) * mm});
            skLineSegment(sketch, "E347.0.58.2", {"start": v(-81.29, 4254) * mm, "end": v(-82.6, 4264.7) * mm});
            skLineSegment(sketch, "E347.0.58.3", {"start": v(-82.6, 4243.3) * mm, "end": v(-81.29, 4254) * mm});
            skLineSegment(sketch, "E347.0.58.4", {"start": v(-140.6, 4243.3) * mm, "end": v(-139.29, 4254) * mm});
            skLineSegment(sketch, "E347.0.58.5", {"start": v(-150.06, 4254) * mm, "end": v(-148.74, 4243.3) * mm});
            skLineSegment(sketch, "E347.0.58.6", {"start": v(-90.74, 4264.7) * mm, "end": v(-92.06, 4254) * mm});
            skLineSegment(sketch, "E347.0.58.7", {"start": v(-148.74, 4264.7) * mm, "end": v(-150.06, 4254) * mm});
            skLineSegment(sketch, "E347.0.58.8", {"start": v(-90.74, 4266.5) * mm, "end": v(-90.74, 4264.7) * mm});
            skLineSegment(sketch, "E347.0.58.9", {"start": v(-148.54, 4241.3) * mm, "end": v(-140.8, 4241.3) * mm});
            skArc(sketch, "E347.0.58.10", {"start": v(-82.6, 4266.5) * mm, "mid": v(-82.66, 4266.65) * mm, "end": v(-82.8, 4266.7) * mm});
            skLineSegment(sketch, "E347.0.58.11", {"start": v(-82.8, 4266.7) * mm, "end": v(-90.54, 4266.7) * mm});
            skArc(sketch, "E347.0.58.12", {"start": v(-140.8, 4241.3) * mm, "mid": v(-140.66, 4241.37) * mm, "end": v(-140.6, 4241.5) * mm});
            skLineSegment(sketch, "E347.0.58.13", {"start": v(-82.6, 4264.7) * mm, "end": v(-82.6, 4266.5) * mm});
            skLineSegment(sketch, "E347.0.58.14", {"start": v(-140.6, 4241.5) * mm, "end": v(-140.6, 4243.3) * mm});
            skArc(sketch, "E347.0.58.15", {"start": v(-90.54, 4266.7) * mm, "mid": v(-90.68, 4266.65) * mm, "end": v(-90.74, 4266.5) * mm});
            skLineSegment(sketch, "E347.0.58.16", {"start": v(-140.6, 4264.7) * mm, "end": v(-140.6, 4266.5) * mm});
            skArc(sketch, "E347.0.58.17", {"start": v(-140.6, 4266.5) * mm, "mid": v(-140.66, 4266.65) * mm, "end": v(-140.8, 4266.7) * mm});
            skLineSegment(sketch, "E347.0.58.18", {"start": v(-140.8, 4266.7) * mm, "end": v(-148.54, 4266.7) * mm});
            skArc(sketch, "E347.0.58.19", {"start": v(-90.74, 4241.5) * mm, "mid": v(-90.68, 4241.37) * mm, "end": v(-90.54, 4241.3) * mm});
            skLineSegment(sketch, "E347.0.58.20", {"start": v(-90.74, 4243.3) * mm, "end": v(-90.74, 4241.5) * mm});
            skLineSegment(sketch, "E347.0.58.21", {"start": v(-82.6, 4241.5) * mm, "end": v(-82.6, 4243.3) * mm});
            skArc(sketch, "E347.0.58.22", {"start": v(-148.54, 4266.7) * mm, "mid": v(-148.68, 4266.65) * mm, "end": v(-148.74, 4266.5) * mm});
            skLineSegment(sketch, "E347.0.58.23", {"start": v(-148.74, 4266.5) * mm, "end": v(-148.74, 4264.7) * mm});
            skArc(sketch, "E347.0.58.24", {"start": v(-148.74, 4241.5) * mm, "mid": v(-148.68, 4241.37) * mm, "end": v(-148.54, 4241.3) * mm});
            skLineSegment(sketch, "E347.0.58.25", {"start": v(-148.74, 4243.3) * mm, "end": v(-148.74, 4241.5) * mm});
            skLineSegment(sketch, "E347.0.58.26", {"start": v(-90.54, 4241.3) * mm, "end": v(-82.8, 4241.3) * mm});
            skArc(sketch, "E347.0.58.27", {"start": v(-82.8, 4241.3) * mm, "mid": v(-82.66, 4241.37) * mm, "end": v(-82.6, 4241.5) * mm});
            skLineSegment(sketch, "E347.0.59.0", {"start": v(-92.06, 4330.2) * mm, "end": v(-90.74, 4319.5) * mm});
            skLineSegment(sketch, "E347.0.59.1", {"start": v(-139.29, 4330.2) * mm, "end": v(-140.6, 4340.9) * mm});
            skLineSegment(sketch, "E347.0.59.2", {"start": v(-81.29, 4330.2) * mm, "end": v(-82.6, 4340.9) * mm});
            skLineSegment(sketch, "E347.0.59.3", {"start": v(-82.6, 4319.5) * mm, "end": v(-81.29, 4330.2) * mm});
            skLineSegment(sketch, "E347.0.59.4", {"start": v(-140.6, 4319.5) * mm, "end": v(-139.29, 4330.2) * mm});
            skLineSegment(sketch, "E347.0.59.5", {"start": v(-150.06, 4330.2) * mm, "end": v(-148.74, 4319.5) * mm});
            skLineSegment(sketch, "E347.0.59.6", {"start": v(-90.74, 4340.9) * mm, "end": v(-92.06, 4330.2) * mm});
            skLineSegment(sketch, "E347.0.59.7", {"start": v(-148.74, 4340.9) * mm, "end": v(-150.06, 4330.2) * mm});
            skLineSegment(sketch, "E347.0.59.8", {"start": v(-90.74, 4342.7) * mm, "end": v(-90.74, 4340.9) * mm});
            skLineSegment(sketch, "E347.0.59.9", {"start": v(-148.54, 4317.5) * mm, "end": v(-140.8, 4317.5) * mm});
            skArc(sketch, "E347.0.59.10", {"start": v(-82.6, 4342.7) * mm, "mid": v(-82.66, 4342.85) * mm, "end": v(-82.8, 4342.9) * mm});
            skLineSegment(sketch, "E347.0.59.11", {"start": v(-82.8, 4342.9) * mm, "end": v(-90.54, 4342.9) * mm});
            skArc(sketch, "E347.0.59.12", {"start": v(-140.8, 4317.5) * mm, "mid": v(-140.66, 4317.57) * mm, "end": v(-140.6, 4317.7) * mm});
            skLineSegment(sketch, "E347.0.59.13", {"start": v(-82.6, 4340.9) * mm, "end": v(-82.6, 4342.7) * mm});
            skLineSegment(sketch, "E347.0.59.14", {"start": v(-140.6, 4317.7) * mm, "end": v(-140.6, 4319.5) * mm});
            skArc(sketch, "E347.0.59.15", {"start": v(-90.54, 4342.9) * mm, "mid": v(-90.68, 4342.85) * mm, "end": v(-90.74, 4342.7) * mm});
            skLineSegment(sketch, "E347.0.59.16", {"start": v(-140.6, 4340.9) * mm, "end": v(-140.6, 4342.7) * mm});
            skArc(sketch, "E347.0.59.17", {"start": v(-140.6, 4342.7) * mm, "mid": v(-140.66, 4342.85) * mm, "end": v(-140.8, 4342.9) * mm});
            skLineSegment(sketch, "E347.0.59.18", {"start": v(-140.8, 4342.9) * mm, "end": v(-148.54, 4342.9) * mm});
            skArc(sketch, "E347.0.59.19", {"start": v(-90.74, 4317.7) * mm, "mid": v(-90.68, 4317.57) * mm, "end": v(-90.54, 4317.5) * mm});
            skLineSegment(sketch, "E347.0.59.20", {"start": v(-90.74, 4319.5) * mm, "end": v(-90.74, 4317.7) * mm});
            skLineSegment(sketch, "E347.0.59.21", {"start": v(-82.6, 4317.7) * mm, "end": v(-82.6, 4319.5) * mm});
            skArc(sketch, "E347.0.59.22", {"start": v(-148.54, 4342.9) * mm, "mid": v(-148.68, 4342.85) * mm, "end": v(-148.74, 4342.7) * mm});
            skLineSegment(sketch, "E347.0.59.23", {"start": v(-148.74, 4342.7) * mm, "end": v(-148.74, 4340.9) * mm});
            skArc(sketch, "E347.0.59.24", {"start": v(-148.74, 4317.7) * mm, "mid": v(-148.68, 4317.57) * mm, "end": v(-148.54, 4317.5) * mm});
            skLineSegment(sketch, "E347.0.59.25", {"start": v(-148.74, 4319.5) * mm, "end": v(-148.74, 4317.7) * mm});
            skLineSegment(sketch, "E347.0.59.26", {"start": v(-90.54, 4317.5) * mm, "end": v(-82.8, 4317.5) * mm});
            skArc(sketch, "E347.0.59.27", {"start": v(-82.8, 4317.5) * mm, "mid": v(-82.66, 4317.57) * mm, "end": v(-82.6, 4317.7) * mm});
            skLineSegment(sketch, "E347.0.60.0", {"start": v(-92.06, 4406.4) * mm, "end": v(-90.74, 4395.7) * mm});
            skLineSegment(sketch, "E347.0.60.1", {"start": v(-139.29, 4406.4) * mm, "end": v(-140.6, 4417.1) * mm});
            skLineSegment(sketch, "E347.0.60.2", {"start": v(-81.29, 4406.4) * mm, "end": v(-82.6, 4417.1) * mm});
            skLineSegment(sketch, "E347.0.60.3", {"start": v(-82.6, 4395.7) * mm, "end": v(-81.29, 4406.4) * mm});
            skLineSegment(sketch, "E347.0.60.4", {"start": v(-140.6, 4395.7) * mm, "end": v(-139.29, 4406.4) * mm});
            skLineSegment(sketch, "E347.0.60.5", {"start": v(-150.06, 4406.4) * mm, "end": v(-148.74, 4395.7) * mm});
            skLineSegment(sketch, "E347.0.60.6", {"start": v(-90.74, 4417.1) * mm, "end": v(-92.06, 4406.4) * mm});
            skLineSegment(sketch, "E347.0.60.7", {"start": v(-148.74, 4417.1) * mm, "end": v(-150.06, 4406.4) * mm});
            skLineSegment(sketch, "E347.0.60.8", {"start": v(-90.74, 4418.9) * mm, "end": v(-90.74, 4417.1) * mm});
            skLineSegment(sketch, "E347.0.60.9", {"start": v(-148.54, 4393.7) * mm, "end": v(-140.8, 4393.7) * mm});
            skArc(sketch, "E347.0.60.10", {"start": v(-82.6, 4418.9) * mm, "mid": v(-82.66, 4419.05) * mm, "end": v(-82.8, 4419.1) * mm});
            skLineSegment(sketch, "E347.0.60.11", {"start": v(-82.8, 4419.1) * mm, "end": v(-90.54, 4419.1) * mm});
            skArc(sketch, "E347.0.60.12", {"start": v(-140.8, 4393.7) * mm, "mid": v(-140.66, 4393.77) * mm, "end": v(-140.6, 4393.9) * mm});
            skLineSegment(sketch, "E347.0.60.13", {"start": v(-82.6, 4417.1) * mm, "end": v(-82.6, 4418.9) * mm});
            skLineSegment(sketch, "E347.0.60.14", {"start": v(-140.6, 4393.9) * mm, "end": v(-140.6, 4395.7) * mm});
            skArc(sketch, "E347.0.60.15", {"start": v(-90.54, 4419.1) * mm, "mid": v(-90.68, 4419.05) * mm, "end": v(-90.74, 4418.9) * mm});
            skLineSegment(sketch, "E347.0.60.16", {"start": v(-140.6, 4417.1) * mm, "end": v(-140.6, 4418.9) * mm});
            skArc(sketch, "E347.0.60.17", {"start": v(-140.6, 4418.9) * mm, "mid": v(-140.66, 4419.05) * mm, "end": v(-140.8, 4419.1) * mm});
            skLineSegment(sketch, "E347.0.60.18", {"start": v(-140.8, 4419.1) * mm, "end": v(-148.54, 4419.1) * mm});
            skArc(sketch, "E347.0.60.19", {"start": v(-90.74, 4393.9) * mm, "mid": v(-90.68, 4393.77) * mm, "end": v(-90.54, 4393.7) * mm});
            skLineSegment(sketch, "E347.0.60.20", {"start": v(-90.74, 4395.7) * mm, "end": v(-90.74, 4393.9) * mm});
            skLineSegment(sketch, "E347.0.60.21", {"start": v(-82.6, 4393.9) * mm, "end": v(-82.6, 4395.7) * mm});
            skArc(sketch, "E347.0.60.22", {"start": v(-148.54, 4419.1) * mm, "mid": v(-148.68, 4419.05) * mm, "end": v(-148.74, 4418.9) * mm});
            skLineSegment(sketch, "E347.0.60.23", {"start": v(-148.74, 4418.9) * mm, "end": v(-148.74, 4417.1) * mm});
            skArc(sketch, "E347.0.60.24", {"start": v(-148.74, 4393.9) * mm, "mid": v(-148.68, 4393.77) * mm, "end": v(-148.54, 4393.7) * mm});
            skLineSegment(sketch, "E347.0.60.25", {"start": v(-148.74, 4395.7) * mm, "end": v(-148.74, 4393.9) * mm});
            skLineSegment(sketch, "E347.0.60.26", {"start": v(-90.54, 4393.7) * mm, "end": v(-82.8, 4393.7) * mm});
            skArc(sketch, "E347.0.60.27", {"start": v(-82.8, 4393.7) * mm, "mid": v(-82.66, 4393.77) * mm, "end": v(-82.6, 4393.9) * mm});
            skLineSegment(sketch, "E347.0.61.0", {"start": v(-92.06, 4482.6) * mm, "end": v(-90.74, 4471.9) * mm});
            skLineSegment(sketch, "E347.0.61.1", {"start": v(-139.29, 4482.6) * mm, "end": v(-140.6, 4493.3) * mm});
            skLineSegment(sketch, "E347.0.61.2", {"start": v(-81.29, 4482.6) * mm, "end": v(-82.6, 4493.3) * mm});
            skLineSegment(sketch, "E347.0.61.3", {"start": v(-82.6, 4471.9) * mm, "end": v(-81.29, 4482.6) * mm});
            skLineSegment(sketch, "E347.0.61.4", {"start": v(-140.6, 4471.9) * mm, "end": v(-139.29, 4482.6) * mm});
            skLineSegment(sketch, "E347.0.61.5", {"start": v(-150.06, 4482.6) * mm, "end": v(-148.74, 4471.9) * mm});
            skLineSegment(sketch, "E347.0.61.6", {"start": v(-90.74, 4493.3) * mm, "end": v(-92.06, 4482.6) * mm});
            skLineSegment(sketch, "E347.0.61.7", {"start": v(-148.74, 4493.3) * mm, "end": v(-150.06, 4482.6) * mm});
            skLineSegment(sketch, "E347.0.61.8", {"start": v(-90.74, 4495.1) * mm, "end": v(-90.74, 4493.3) * mm});
            skLineSegment(sketch, "E347.0.61.9", {"start": v(-148.54, 4469.9) * mm, "end": v(-140.8, 4469.9) * mm});
            skArc(sketch, "E347.0.61.10", {"start": v(-82.6, 4495.1) * mm, "mid": v(-82.66, 4495.25) * mm, "end": v(-82.8, 4495.3) * mm});
            skLineSegment(sketch, "E347.0.61.11", {"start": v(-82.8, 4495.3) * mm, "end": v(-90.54, 4495.3) * mm});
            skArc(sketch, "E347.0.61.12", {"start": v(-140.8, 4469.9) * mm, "mid": v(-140.66, 4469.97) * mm, "end": v(-140.6, 4470.1) * mm});
            skLineSegment(sketch, "E347.0.61.13", {"start": v(-82.6, 4493.3) * mm, "end": v(-82.6, 4495.1) * mm});
            skLineSegment(sketch, "E347.0.61.14", {"start": v(-140.6, 4470.1) * mm, "end": v(-140.6, 4471.9) * mm});
            skArc(sketch, "E347.0.61.15", {"start": v(-90.54, 4495.3) * mm, "mid": v(-90.68, 4495.25) * mm, "end": v(-90.74, 4495.1) * mm});
            skLineSegment(sketch, "E347.0.61.16", {"start": v(-140.6, 4493.3) * mm, "end": v(-140.6, 4495.1) * mm});
            skArc(sketch, "E347.0.61.17", {"start": v(-140.6, 4495.1) * mm, "mid": v(-140.66, 4495.25) * mm, "end": v(-140.8, 4495.3) * mm});
            skLineSegment(sketch, "E347.0.61.18", {"start": v(-140.8, 4495.3) * mm, "end": v(-148.54, 4495.3) * mm});
            skArc(sketch, "E347.0.61.19", {"start": v(-90.74, 4470.1) * mm, "mid": v(-90.68, 4469.97) * mm, "end": v(-90.54, 4469.9) * mm});
            skLineSegment(sketch, "E347.0.61.20", {"start": v(-90.74, 4471.9) * mm, "end": v(-90.74, 4470.1) * mm});
            skLineSegment(sketch, "E347.0.61.21", {"start": v(-82.6, 4470.1) * mm, "end": v(-82.6, 4471.9) * mm});
            skArc(sketch, "E347.0.61.22", {"start": v(-148.54, 4495.3) * mm, "mid": v(-148.68, 4495.25) * mm, "end": v(-148.74, 4495.1) * mm});
            skLineSegment(sketch, "E347.0.61.23", {"start": v(-148.74, 4495.1) * mm, "end": v(-148.74, 4493.3) * mm});
            skArc(sketch, "E347.0.61.24", {"start": v(-148.74, 4470.1) * mm, "mid": v(-148.68, 4469.97) * mm, "end": v(-148.54, 4469.9) * mm});
            skLineSegment(sketch, "E347.0.61.25", {"start": v(-148.74, 4471.9) * mm, "end": v(-148.74, 4470.1) * mm});
            skLineSegment(sketch, "E347.0.61.26", {"start": v(-90.54, 4469.9) * mm, "end": v(-82.8, 4469.9) * mm});
            skArc(sketch, "E347.0.61.27", {"start": v(-82.8, 4469.9) * mm, "mid": v(-82.66, 4469.97) * mm, "end": v(-82.6, 4470.1) * mm});
            skLineSegment(sketch, "E347.0.62.0", {"start": v(-92.06, 4558.8) * mm, "end": v(-90.74, 4548.1) * mm});
            skLineSegment(sketch, "E347.0.62.1", {"start": v(-139.29, 4558.8) * mm, "end": v(-140.6, 4569.5) * mm});
            skLineSegment(sketch, "E347.0.62.2", {"start": v(-81.29, 4558.8) * mm, "end": v(-82.6, 4569.5) * mm});
            skLineSegment(sketch, "E347.0.62.3", {"start": v(-82.6, 4548.1) * mm, "end": v(-81.29, 4558.8) * mm});
            skLineSegment(sketch, "E347.0.62.4", {"start": v(-140.6, 4548.1) * mm, "end": v(-139.29, 4558.8) * mm});
            skLineSegment(sketch, "E347.0.62.5", {"start": v(-150.06, 4558.8) * mm, "end": v(-148.74, 4548.1) * mm});
            skLineSegment(sketch, "E347.0.62.6", {"start": v(-90.74, 4569.5) * mm, "end": v(-92.06, 4558.8) * mm});
            skLineSegment(sketch, "E347.0.62.7", {"start": v(-148.74, 4569.5) * mm, "end": v(-150.06, 4558.8) * mm});
            skLineSegment(sketch, "E347.0.62.8", {"start": v(-90.74, 4571.3) * mm, "end": v(-90.74, 4569.5) * mm});
            skLineSegment(sketch, "E347.0.62.9", {"start": v(-148.54, 4546.1) * mm, "end": v(-140.8, 4546.1) * mm});
            skArc(sketch, "E347.0.62.10", {"start": v(-82.6, 4571.3) * mm, "mid": v(-82.66, 4571.45) * mm, "end": v(-82.8, 4571.5) * mm});
            skLineSegment(sketch, "E347.0.62.11", {"start": v(-82.8, 4571.5) * mm, "end": v(-90.54, 4571.5) * mm});
            skArc(sketch, "E347.0.62.12", {"start": v(-140.8, 4546.1) * mm, "mid": v(-140.66, 4546.17) * mm, "end": v(-140.6, 4546.3) * mm});
            skLineSegment(sketch, "E347.0.62.13", {"start": v(-82.6, 4569.5) * mm, "end": v(-82.6, 4571.3) * mm});
            skLineSegment(sketch, "E347.0.62.14", {"start": v(-140.6, 4546.3) * mm, "end": v(-140.6, 4548.1) * mm});
            skArc(sketch, "E347.0.62.15", {"start": v(-90.54, 4571.5) * mm, "mid": v(-90.68, 4571.45) * mm, "end": v(-90.74, 4571.3) * mm});
            skLineSegment(sketch, "E347.0.62.16", {"start": v(-140.6, 4569.5) * mm, "end": v(-140.6, 4571.3) * mm});
            skArc(sketch, "E347.0.62.17", {"start": v(-140.6, 4571.3) * mm, "mid": v(-140.66, 4571.45) * mm, "end": v(-140.8, 4571.5) * mm});
            skLineSegment(sketch, "E347.0.62.18", {"start": v(-140.8, 4571.5) * mm, "end": v(-148.54, 4571.5) * mm});
            skArc(sketch, "E347.0.62.19", {"start": v(-90.74, 4546.3) * mm, "mid": v(-90.68, 4546.17) * mm, "end": v(-90.54, 4546.1) * mm});
            skLineSegment(sketch, "E347.0.62.20", {"start": v(-90.74, 4548.1) * mm, "end": v(-90.74, 4546.3) * mm});
            skLineSegment(sketch, "E347.0.62.21", {"start": v(-82.6, 4546.3) * mm, "end": v(-82.6, 4548.1) * mm});
            skArc(sketch, "E347.0.62.22", {"start": v(-148.54, 4571.5) * mm, "mid": v(-148.68, 4571.45) * mm, "end": v(-148.74, 4571.3) * mm});
            skLineSegment(sketch, "E347.0.62.23", {"start": v(-148.74, 4571.3) * mm, "end": v(-148.74, 4569.5) * mm});
            skArc(sketch, "E347.0.62.24", {"start": v(-148.74, 4546.3) * mm, "mid": v(-148.68, 4546.17) * mm, "end": v(-148.54, 4546.1) * mm});
            skLineSegment(sketch, "E347.0.62.25", {"start": v(-148.74, 4548.1) * mm, "end": v(-148.74, 4546.3) * mm});
            skLineSegment(sketch, "E347.0.62.26", {"start": v(-90.54, 4546.1) * mm, "end": v(-82.8, 4546.1) * mm});
            skArc(sketch, "E347.0.62.27", {"start": v(-82.8, 4546.1) * mm, "mid": v(-82.66, 4546.17) * mm, "end": v(-82.6, 4546.3) * mm});
            skLineSegment(sketch, "E347.0.63.0", {"start": v(-92.06, 4635) * mm, "end": v(-90.74, 4624.3) * mm});
            skLineSegment(sketch, "E347.0.63.1", {"start": v(-139.29, 4635) * mm, "end": v(-140.6, 4645.7) * mm});
            skLineSegment(sketch, "E347.0.63.2", {"start": v(-81.29, 4635) * mm, "end": v(-82.6, 4645.7) * mm});
            skLineSegment(sketch, "E347.0.63.3", {"start": v(-82.6, 4624.3) * mm, "end": v(-81.29, 4635) * mm});
            skLineSegment(sketch, "E347.0.63.4", {"start": v(-140.6, 4624.3) * mm, "end": v(-139.29, 4635) * mm});
            skLineSegment(sketch, "E347.0.63.5", {"start": v(-150.06, 4635) * mm, "end": v(-148.74, 4624.3) * mm});
            skLineSegment(sketch, "E347.0.63.6", {"start": v(-90.74, 4645.7) * mm, "end": v(-92.06, 4635) * mm});
            skLineSegment(sketch, "E347.0.63.7", {"start": v(-148.74, 4645.7) * mm, "end": v(-150.06, 4635) * mm});
            skLineSegment(sketch, "E347.0.63.8", {"start": v(-90.74, 4647.5) * mm, "end": v(-90.74, 4645.7) * mm});
            skLineSegment(sketch, "E347.0.63.9", {"start": v(-148.54, 4622.3) * mm, "end": v(-140.8, 4622.3) * mm});
            skArc(sketch, "E347.0.63.10", {"start": v(-82.6, 4647.5) * mm, "mid": v(-82.66, 4647.65) * mm, "end": v(-82.8, 4647.7) * mm});
            skLineSegment(sketch, "E347.0.63.11", {"start": v(-82.8, 4647.7) * mm, "end": v(-90.54, 4647.7) * mm});
            skArc(sketch, "E347.0.63.12", {"start": v(-140.8, 4622.3) * mm, "mid": v(-140.66, 4622.37) * mm, "end": v(-140.6, 4622.5) * mm});
            skLineSegment(sketch, "E347.0.63.13", {"start": v(-82.6, 4645.7) * mm, "end": v(-82.6, 4647.5) * mm});
            skLineSegment(sketch, "E347.0.63.14", {"start": v(-140.6, 4622.5) * mm, "end": v(-140.6, 4624.3) * mm});
            skArc(sketch, "E347.0.63.15", {"start": v(-90.54, 4647.7) * mm, "mid": v(-90.68, 4647.65) * mm, "end": v(-90.74, 4647.5) * mm});
            skLineSegment(sketch, "E347.0.63.16", {"start": v(-140.6, 4645.7) * mm, "end": v(-140.6, 4647.5) * mm});
            skArc(sketch, "E347.0.63.17", {"start": v(-140.6, 4647.5) * mm, "mid": v(-140.66, 4647.65) * mm, "end": v(-140.8, 4647.7) * mm});
            skLineSegment(sketch, "E347.0.63.18", {"start": v(-140.8, 4647.7) * mm, "end": v(-148.54, 4647.7) * mm});
            skArc(sketch, "E347.0.63.19", {"start": v(-90.74, 4622.5) * mm, "mid": v(-90.68, 4622.37) * mm, "end": v(-90.54, 4622.3) * mm});
            skLineSegment(sketch, "E347.0.63.20", {"start": v(-90.74, 4624.3) * mm, "end": v(-90.74, 4622.5) * mm});
            skLineSegment(sketch, "E347.0.63.21", {"start": v(-82.6, 4622.5) * mm, "end": v(-82.6, 4624.3) * mm});
            skArc(sketch, "E347.0.63.22", {"start": v(-148.54, 4647.7) * mm, "mid": v(-148.68, 4647.65) * mm, "end": v(-148.74, 4647.5) * mm});
            skLineSegment(sketch, "E347.0.63.23", {"start": v(-148.74, 4647.5) * mm, "end": v(-148.74, 4645.7) * mm});
            skArc(sketch, "E347.0.63.24", {"start": v(-148.74, 4622.5) * mm, "mid": v(-148.68, 4622.37) * mm, "end": v(-148.54, 4622.3) * mm});
            skLineSegment(sketch, "E347.0.63.25", {"start": v(-148.74, 4624.3) * mm, "end": v(-148.74, 4622.5) * mm});
            skLineSegment(sketch, "E347.0.63.26", {"start": v(-90.54, 4622.3) * mm, "end": v(-82.8, 4622.3) * mm});
            skArc(sketch, "E347.0.63.27", {"start": v(-82.8, 4622.3) * mm, "mid": v(-82.66, 4622.37) * mm, "end": v(-82.6, 4622.5) * mm});
            skLineSegment(sketch, "E347.0.64.0", {"start": v(-92.06, 4711.2) * mm, "end": v(-90.74, 4700.5) * mm});
            skLineSegment(sketch, "E347.0.64.1", {"start": v(-139.29, 4711.2) * mm, "end": v(-140.6, 4721.9) * mm});
            skLineSegment(sketch, "E347.0.64.2", {"start": v(-81.29, 4711.2) * mm, "end": v(-82.6, 4721.9) * mm});
            skLineSegment(sketch, "E347.0.64.3", {"start": v(-82.6, 4700.5) * mm, "end": v(-81.29, 4711.2) * mm});
            skLineSegment(sketch, "E347.0.64.4", {"start": v(-140.6, 4700.5) * mm, "end": v(-139.29, 4711.2) * mm});
            skLineSegment(sketch, "E347.0.64.5", {"start": v(-150.06, 4711.2) * mm, "end": v(-148.74, 4700.5) * mm});
            skLineSegment(sketch, "E347.0.64.6", {"start": v(-90.74, 4721.9) * mm, "end": v(-92.06, 4711.2) * mm});
            skLineSegment(sketch, "E347.0.64.7", {"start": v(-148.74, 4721.9) * mm, "end": v(-150.06, 4711.2) * mm});
            skLineSegment(sketch, "E347.0.64.8", {"start": v(-90.74, 4723.7) * mm, "end": v(-90.74, 4721.9) * mm});
            skLineSegment(sketch, "E347.0.64.9", {"start": v(-148.54, 4698.5) * mm, "end": v(-140.8, 4698.5) * mm});
            skArc(sketch, "E347.0.64.10", {"start": v(-82.6, 4723.7) * mm, "mid": v(-82.66, 4723.85) * mm, "end": v(-82.8, 4723.9) * mm});
            skLineSegment(sketch, "E347.0.64.11", {"start": v(-82.8, 4723.9) * mm, "end": v(-90.54, 4723.9) * mm});
            skArc(sketch, "E347.0.64.12", {"start": v(-140.8, 4698.5) * mm, "mid": v(-140.66, 4698.57) * mm, "end": v(-140.6, 4698.7) * mm});
            skLineSegment(sketch, "E347.0.64.13", {"start": v(-82.6, 4721.9) * mm, "end": v(-82.6, 4723.7) * mm});
            skLineSegment(sketch, "E347.0.64.14", {"start": v(-140.6, 4698.7) * mm, "end": v(-140.6, 4700.5) * mm});
            skArc(sketch, "E347.0.64.15", {"start": v(-90.54, 4723.9) * mm, "mid": v(-90.68, 4723.85) * mm, "end": v(-90.74, 4723.7) * mm});
            skLineSegment(sketch, "E347.0.64.16", {"start": v(-140.6, 4721.9) * mm, "end": v(-140.6, 4723.7) * mm});
            skArc(sketch, "E347.0.64.17", {"start": v(-140.6, 4723.7) * mm, "mid": v(-140.66, 4723.85) * mm, "end": v(-140.8, 4723.9) * mm});
            skLineSegment(sketch, "E347.0.64.18", {"start": v(-140.8, 4723.9) * mm, "end": v(-148.54, 4723.9) * mm});
            skArc(sketch, "E347.0.64.19", {"start": v(-90.74, 4698.7) * mm, "mid": v(-90.68, 4698.57) * mm, "end": v(-90.54, 4698.5) * mm});
            skLineSegment(sketch, "E347.0.64.20", {"start": v(-90.74, 4700.5) * mm, "end": v(-90.74, 4698.7) * mm});
            skLineSegment(sketch, "E347.0.64.21", {"start": v(-82.6, 4698.7) * mm, "end": v(-82.6, 4700.5) * mm});
            skArc(sketch, "E347.0.64.22", {"start": v(-148.54, 4723.9) * mm, "mid": v(-148.68, 4723.85) * mm, "end": v(-148.74, 4723.7) * mm});
            skLineSegment(sketch, "E347.0.64.23", {"start": v(-148.74, 4723.7) * mm, "end": v(-148.74, 4721.9) * mm});
            skArc(sketch, "E347.0.64.24", {"start": v(-148.74, 4698.7) * mm, "mid": v(-148.68, 4698.57) * mm, "end": v(-148.54, 4698.5) * mm});
            skLineSegment(sketch, "E347.0.64.25", {"start": v(-148.74, 4700.5) * mm, "end": v(-148.74, 4698.7) * mm});
            skLineSegment(sketch, "E347.0.64.26", {"start": v(-90.54, 4698.5) * mm, "end": v(-82.8, 4698.5) * mm});
            skArc(sketch, "E347.0.64.27", {"start": v(-82.8, 4698.5) * mm, "mid": v(-82.66, 4698.57) * mm, "end": v(-82.6, 4698.7) * mm});
            skLineSegment(sketch, "E347.0.65.0", {"start": v(-92.06, 4787.4) * mm, "end": v(-90.74, 4776.7) * mm});
            skLineSegment(sketch, "E347.0.65.1", {"start": v(-139.29, 4787.4) * mm, "end": v(-140.6, 4798.1) * mm});
            skLineSegment(sketch, "E347.0.65.2", {"start": v(-81.29, 4787.4) * mm, "end": v(-82.6, 4798.1) * mm});
            skLineSegment(sketch, "E347.0.65.3", {"start": v(-82.6, 4776.7) * mm, "end": v(-81.29, 4787.4) * mm});
            skLineSegment(sketch, "E347.0.65.4", {"start": v(-140.6, 4776.7) * mm, "end": v(-139.29, 4787.4) * mm});
            skLineSegment(sketch, "E347.0.65.5", {"start": v(-150.06, 4787.4) * mm, "end": v(-148.74, 4776.7) * mm});
            skLineSegment(sketch, "E347.0.65.6", {"start": v(-90.74, 4798.1) * mm, "end": v(-92.06, 4787.4) * mm});
            skLineSegment(sketch, "E347.0.65.7", {"start": v(-148.74, 4798.1) * mm, "end": v(-150.06, 4787.4) * mm});
            skLineSegment(sketch, "E347.0.65.8", {"start": v(-90.74, 4799.9) * mm, "end": v(-90.74, 4798.1) * mm});
            skLineSegment(sketch, "E347.0.65.9", {"start": v(-148.54, 4774.7) * mm, "end": v(-140.8, 4774.7) * mm});
            skArc(sketch, "E347.0.65.10", {"start": v(-82.6, 4799.9) * mm, "mid": v(-82.66, 4800.05) * mm, "end": v(-82.8, 4800.1) * mm});
            skLineSegment(sketch, "E347.0.65.11", {"start": v(-82.8, 4800.1) * mm, "end": v(-90.54, 4800.1) * mm});
            skArc(sketch, "E347.0.65.12", {"start": v(-140.8, 4774.7) * mm, "mid": v(-140.66, 4774.77) * mm, "end": v(-140.6, 4774.9) * mm});
            skLineSegment(sketch, "E347.0.65.13", {"start": v(-82.6, 4798.1) * mm, "end": v(-82.6, 4799.9) * mm});
            skLineSegment(sketch, "E347.0.65.14", {"start": v(-140.6, 4774.9) * mm, "end": v(-140.6, 4776.7) * mm});
            skArc(sketch, "E347.0.65.15", {"start": v(-90.54, 4800.1) * mm, "mid": v(-90.68, 4800.05) * mm, "end": v(-90.74, 4799.9) * mm});
            skLineSegment(sketch, "E347.0.65.16", {"start": v(-140.6, 4798.1) * mm, "end": v(-140.6, 4799.9) * mm});
            skArc(sketch, "E347.0.65.17", {"start": v(-140.6, 4799.9) * mm, "mid": v(-140.66, 4800.05) * mm, "end": v(-140.8, 4800.1) * mm});
            skLineSegment(sketch, "E347.0.65.18", {"start": v(-140.8, 4800.1) * mm, "end": v(-148.54, 4800.1) * mm});
            skArc(sketch, "E347.0.65.19", {"start": v(-90.74, 4774.9) * mm, "mid": v(-90.68, 4774.77) * mm, "end": v(-90.54, 4774.7) * mm});
            skLineSegment(sketch, "E347.0.65.20", {"start": v(-90.74, 4776.7) * mm, "end": v(-90.74, 4774.9) * mm});
            skLineSegment(sketch, "E347.0.65.21", {"start": v(-82.6, 4774.9) * mm, "end": v(-82.6, 4776.7) * mm});
            skArc(sketch, "E347.0.65.22", {"start": v(-148.54, 4800.1) * mm, "mid": v(-148.68, 4800.05) * mm, "end": v(-148.74, 4799.9) * mm});
            skLineSegment(sketch, "E347.0.65.23", {"start": v(-148.74, 4799.9) * mm, "end": v(-148.74, 4798.1) * mm});
            skArc(sketch, "E347.0.65.24", {"start": v(-148.74, 4774.9) * mm, "mid": v(-148.68, 4774.77) * mm, "end": v(-148.54, 4774.7) * mm});
            skLineSegment(sketch, "E347.0.65.25", {"start": v(-148.74, 4776.7) * mm, "end": v(-148.74, 4774.9) * mm});
            skLineSegment(sketch, "E347.0.65.26", {"start": v(-90.54, 4774.7) * mm, "end": v(-82.8, 4774.7) * mm});
            skArc(sketch, "E347.0.65.27", {"start": v(-82.8, 4774.7) * mm, "mid": v(-82.66, 4774.77) * mm, "end": v(-82.6, 4774.9) * mm});
            skLineSegment(sketch, "E347.0.66.0", {"start": v(-92.06, 4863.6) * mm, "end": v(-90.74, 4852.9) * mm});
            skLineSegment(sketch, "E347.0.66.1", {"start": v(-139.29, 4863.6) * mm, "end": v(-140.6, 4874.3) * mm});
            skLineSegment(sketch, "E347.0.66.2", {"start": v(-81.29, 4863.6) * mm, "end": v(-82.6, 4874.3) * mm});
            skLineSegment(sketch, "E347.0.66.3", {"start": v(-82.6, 4852.9) * mm, "end": v(-81.29, 4863.6) * mm});
            skLineSegment(sketch, "E347.0.66.4", {"start": v(-140.6, 4852.9) * mm, "end": v(-139.29, 4863.6) * mm});
            skLineSegment(sketch, "E347.0.66.5", {"start": v(-150.06, 4863.6) * mm, "end": v(-148.74, 4852.9) * mm});
            skLineSegment(sketch, "E347.0.66.6", {"start": v(-90.74, 4874.3) * mm, "end": v(-92.06, 4863.6) * mm});
            skLineSegment(sketch, "E347.0.66.7", {"start": v(-148.74, 4874.3) * mm, "end": v(-150.06, 4863.6) * mm});
            skLineSegment(sketch, "E347.0.66.8", {"start": v(-90.74, 4876.1) * mm, "end": v(-90.74, 4874.3) * mm});
            skLineSegment(sketch, "E347.0.66.9", {"start": v(-148.54, 4850.9) * mm, "end": v(-140.8, 4850.9) * mm});
            skArc(sketch, "E347.0.66.10", {"start": v(-82.6, 4876.1) * mm, "mid": v(-82.66, 4876.25) * mm, "end": v(-82.8, 4876.3) * mm});
            skLineSegment(sketch, "E347.0.66.11", {"start": v(-82.8, 4876.3) * mm, "end": v(-90.54, 4876.3) * mm});
            skArc(sketch, "E347.0.66.12", {"start": v(-140.8, 4850.9) * mm, "mid": v(-140.66, 4850.97) * mm, "end": v(-140.6, 4851.1) * mm});
            skLineSegment(sketch, "E347.0.66.13", {"start": v(-82.6, 4874.3) * mm, "end": v(-82.6, 4876.1) * mm});
            skLineSegment(sketch, "E347.0.66.14", {"start": v(-140.6, 4851.1) * mm, "end": v(-140.6, 4852.9) * mm});
            skArc(sketch, "E347.0.66.15", {"start": v(-90.54, 4876.3) * mm, "mid": v(-90.68, 4876.25) * mm, "end": v(-90.74, 4876.1) * mm});
            skLineSegment(sketch, "E347.0.66.16", {"start": v(-140.6, 4874.3) * mm, "end": v(-140.6, 4876.1) * mm});
            skArc(sketch, "E347.0.66.17", {"start": v(-140.6, 4876.1) * mm, "mid": v(-140.66, 4876.25) * mm, "end": v(-140.8, 4876.3) * mm});
            skLineSegment(sketch, "E347.0.66.18", {"start": v(-140.8, 4876.3) * mm, "end": v(-148.54, 4876.3) * mm});
            skArc(sketch, "E347.0.66.19", {"start": v(-90.74, 4851.1) * mm, "mid": v(-90.68, 4850.97) * mm, "end": v(-90.54, 4850.9) * mm});
            skLineSegment(sketch, "E347.0.66.20", {"start": v(-90.74, 4852.9) * mm, "end": v(-90.74, 4851.1) * mm});
            skLineSegment(sketch, "E347.0.66.21", {"start": v(-82.6, 4851.1) * mm, "end": v(-82.6, 4852.9) * mm});
            skArc(sketch, "E347.0.66.22", {"start": v(-148.54, 4876.3) * mm, "mid": v(-148.68, 4876.25) * mm, "end": v(-148.74, 4876.1) * mm});
            skLineSegment(sketch, "E347.0.66.23", {"start": v(-148.74, 4876.1) * mm, "end": v(-148.74, 4874.3) * mm});
            skArc(sketch, "E347.0.66.24", {"start": v(-148.74, 4851.1) * mm, "mid": v(-148.68, 4850.97) * mm, "end": v(-148.54, 4850.9) * mm});
            skLineSegment(sketch, "E347.0.66.25", {"start": v(-148.74, 4852.9) * mm, "end": v(-148.74, 4851.1) * mm});
            skLineSegment(sketch, "E347.0.66.26", {"start": v(-90.54, 4850.9) * mm, "end": v(-82.8, 4850.9) * mm});
            skArc(sketch, "E347.0.66.27", {"start": v(-82.8, 4850.9) * mm, "mid": v(-82.66, 4850.97) * mm, "end": v(-82.6, 4851.1) * mm});
            skLineSegment(sketch, "E347.0.67.0", {"start": v(-92.06, 4939.8) * mm, "end": v(-90.74, 4929.1) * mm});
            skLineSegment(sketch, "E347.0.67.1", {"start": v(-139.29, 4939.8) * mm, "end": v(-140.6, 4950.5) * mm});
            skLineSegment(sketch, "E347.0.67.2", {"start": v(-81.29, 4939.8) * mm, "end": v(-82.6, 4950.5) * mm});
            skLineSegment(sketch, "E347.0.67.3", {"start": v(-82.6, 4929.1) * mm, "end": v(-81.29, 4939.8) * mm});
            skLineSegment(sketch, "E347.0.67.4", {"start": v(-140.6, 4929.1) * mm, "end": v(-139.29, 4939.8) * mm});
            skLineSegment(sketch, "E347.0.67.5", {"start": v(-150.06, 4939.8) * mm, "end": v(-148.74, 4929.1) * mm});
            skLineSegment(sketch, "E347.0.67.6", {"start": v(-90.74, 4950.5) * mm, "end": v(-92.06, 4939.8) * mm});
            skLineSegment(sketch, "E347.0.67.7", {"start": v(-148.74, 4950.5) * mm, "end": v(-150.06, 4939.8) * mm});
            skLineSegment(sketch, "E347.0.67.8", {"start": v(-90.74, 4952.3) * mm, "end": v(-90.74, 4950.5) * mm});
            skLineSegment(sketch, "E347.0.67.9", {"start": v(-148.54, 4927.1) * mm, "end": v(-140.8, 4927.1) * mm});
            skArc(sketch, "E347.0.67.10", {"start": v(-82.6, 4952.3) * mm, "mid": v(-82.66, 4952.45) * mm, "end": v(-82.8, 4952.5) * mm});
            skLineSegment(sketch, "E347.0.67.11", {"start": v(-82.8, 4952.5) * mm, "end": v(-90.54, 4952.5) * mm});
            skArc(sketch, "E347.0.67.12", {"start": v(-140.8, 4927.1) * mm, "mid": v(-140.66, 4927.17) * mm, "end": v(-140.6, 4927.3) * mm});
            skLineSegment(sketch, "E347.0.67.13", {"start": v(-82.6, 4950.5) * mm, "end": v(-82.6, 4952.3) * mm});
            skLineSegment(sketch, "E347.0.67.14", {"start": v(-140.6, 4927.3) * mm, "end": v(-140.6, 4929.1) * mm});
            skArc(sketch, "E347.0.67.15", {"start": v(-90.54, 4952.5) * mm, "mid": v(-90.68, 4952.45) * mm, "end": v(-90.74, 4952.3) * mm});
            skLineSegment(sketch, "E347.0.67.16", {"start": v(-140.6, 4950.5) * mm, "end": v(-140.6, 4952.3) * mm});
            skArc(sketch, "E347.0.67.17", {"start": v(-140.6, 4952.3) * mm, "mid": v(-140.66, 4952.45) * mm, "end": v(-140.8, 4952.5) * mm});
            skLineSegment(sketch, "E347.0.67.18", {"start": v(-140.8, 4952.5) * mm, "end": v(-148.54, 4952.5) * mm});
            skArc(sketch, "E347.0.67.19", {"start": v(-90.74, 4927.3) * mm, "mid": v(-90.68, 4927.17) * mm, "end": v(-90.54, 4927.1) * mm});
            skLineSegment(sketch, "E347.0.67.20", {"start": v(-90.74, 4929.1) * mm, "end": v(-90.74, 4927.3) * mm});
            skLineSegment(sketch, "E347.0.67.21", {"start": v(-82.6, 4927.3) * mm, "end": v(-82.6, 4929.1) * mm});
            skArc(sketch, "E347.0.67.22", {"start": v(-148.54, 4952.5) * mm, "mid": v(-148.68, 4952.45) * mm, "end": v(-148.74, 4952.3) * mm});
            skLineSegment(sketch, "E347.0.67.23", {"start": v(-148.74, 4952.3) * mm, "end": v(-148.74, 4950.5) * mm});
            skArc(sketch, "E347.0.67.24", {"start": v(-148.74, 4927.3) * mm, "mid": v(-148.68, 4927.17) * mm, "end": v(-148.54, 4927.1) * mm});
            skLineSegment(sketch, "E347.0.67.25", {"start": v(-148.74, 4929.1) * mm, "end": v(-148.74, 4927.3) * mm});
            skLineSegment(sketch, "E347.0.67.26", {"start": v(-90.54, 4927.1) * mm, "end": v(-82.8, 4927.1) * mm});
            skArc(sketch, "E347.0.67.27", {"start": v(-82.8, 4927.1) * mm, "mid": v(-82.66, 4927.17) * mm, "end": v(-82.6, 4927.3) * mm});
            skLineSegment(sketch, "E347.0.68.0", {"start": v(-92.06, 5016) * mm, "end": v(-90.74, 5005.3) * mm});
            skLineSegment(sketch, "E347.0.68.1", {"start": v(-139.29, 5016) * mm, "end": v(-140.6, 5026.7) * mm});
            skLineSegment(sketch, "E347.0.68.2", {"start": v(-81.29, 5016) * mm, "end": v(-82.6, 5026.7) * mm});
            skLineSegment(sketch, "E347.0.68.3", {"start": v(-82.6, 5005.3) * mm, "end": v(-81.29, 5016) * mm});
            skLineSegment(sketch, "E347.0.68.4", {"start": v(-140.6, 5005.3) * mm, "end": v(-139.29, 5016) * mm});
            skLineSegment(sketch, "E347.0.68.5", {"start": v(-150.06, 5016) * mm, "end": v(-148.74, 5005.3) * mm});
            skLineSegment(sketch, "E347.0.68.6", {"start": v(-90.74, 5026.7) * mm, "end": v(-92.06, 5016) * mm});
            skLineSegment(sketch, "E347.0.68.7", {"start": v(-148.74, 5026.7) * mm, "end": v(-150.06, 5016) * mm});
            skLineSegment(sketch, "E347.0.68.8", {"start": v(-90.74, 5028.5) * mm, "end": v(-90.74, 5026.7) * mm});
            skLineSegment(sketch, "E347.0.68.9", {"start": v(-148.54, 5003.3) * mm, "end": v(-140.8, 5003.3) * mm});
            skArc(sketch, "E347.0.68.10", {"start": v(-82.6, 5028.5) * mm, "mid": v(-82.66, 5028.65) * mm, "end": v(-82.8, 5028.7) * mm});
            skLineSegment(sketch, "E347.0.68.11", {"start": v(-82.8, 5028.7) * mm, "end": v(-90.54, 5028.7) * mm});
            skArc(sketch, "E347.0.68.12", {"start": v(-140.8, 5003.3) * mm, "mid": v(-140.66, 5003.37) * mm, "end": v(-140.6, 5003.5) * mm});
            skLineSegment(sketch, "E347.0.68.13", {"start": v(-82.6, 5026.7) * mm, "end": v(-82.6, 5028.5) * mm});
            skLineSegment(sketch, "E347.0.68.14", {"start": v(-140.6, 5003.5) * mm, "end": v(-140.6, 5005.3) * mm});
            skArc(sketch, "E347.0.68.15", {"start": v(-90.54, 5028.7) * mm, "mid": v(-90.68, 5028.65) * mm, "end": v(-90.74, 5028.5) * mm});
            skLineSegment(sketch, "E347.0.68.16", {"start": v(-140.6, 5026.7) * mm, "end": v(-140.6, 5028.5) * mm});
            skArc(sketch, "E347.0.68.17", {"start": v(-140.6, 5028.5) * mm, "mid": v(-140.66, 5028.65) * mm, "end": v(-140.8, 5028.7) * mm});
            skLineSegment(sketch, "E347.0.68.18", {"start": v(-140.8, 5028.7) * mm, "end": v(-148.54, 5028.7) * mm});
            skArc(sketch, "E347.0.68.19", {"start": v(-90.74, 5003.5) * mm, "mid": v(-90.68, 5003.37) * mm, "end": v(-90.54, 5003.3) * mm});
            skLineSegment(sketch, "E347.0.68.20", {"start": v(-90.74, 5005.3) * mm, "end": v(-90.74, 5003.5) * mm});
            skLineSegment(sketch, "E347.0.68.21", {"start": v(-82.6, 5003.5) * mm, "end": v(-82.6, 5005.3) * mm});
            skArc(sketch, "E347.0.68.22", {"start": v(-148.54, 5028.7) * mm, "mid": v(-148.68, 5028.65) * mm, "end": v(-148.74, 5028.5) * mm});
            skLineSegment(sketch, "E347.0.68.23", {"start": v(-148.74, 5028.5) * mm, "end": v(-148.74, 5026.7) * mm});
            skArc(sketch, "E347.0.68.24", {"start": v(-148.74, 5003.5) * mm, "mid": v(-148.68, 5003.37) * mm, "end": v(-148.54, 5003.3) * mm});
            skLineSegment(sketch, "E347.0.68.25", {"start": v(-148.74, 5005.3) * mm, "end": v(-148.74, 5003.5) * mm});
            skLineSegment(sketch, "E347.0.68.26", {"start": v(-90.54, 5003.3) * mm, "end": v(-82.8, 5003.3) * mm});
            skArc(sketch, "E347.0.68.27", {"start": v(-82.8, 5003.3) * mm, "mid": v(-82.66, 5003.37) * mm, "end": v(-82.6, 5003.5) * mm});
            skLineSegment(sketch, "E347.0.69.0", {"start": v(-92.06, 5092.2) * mm, "end": v(-90.74, 5081.5) * mm});
            skLineSegment(sketch, "E347.0.69.1", {"start": v(-139.29, 5092.2) * mm, "end": v(-140.6, 5102.9) * mm});
            skLineSegment(sketch, "E347.0.69.2", {"start": v(-81.29, 5092.2) * mm, "end": v(-82.6, 5102.9) * mm});
            skLineSegment(sketch, "E347.0.69.3", {"start": v(-82.6, 5081.5) * mm, "end": v(-81.29, 5092.2) * mm});
            skLineSegment(sketch, "E347.0.69.4", {"start": v(-140.6, 5081.5) * mm, "end": v(-139.29, 5092.2) * mm});
            skLineSegment(sketch, "E347.0.69.5", {"start": v(-150.06, 5092.2) * mm, "end": v(-148.74, 5081.5) * mm});
            skLineSegment(sketch, "E347.0.69.6", {"start": v(-90.74, 5102.9) * mm, "end": v(-92.06, 5092.2) * mm});
            skLineSegment(sketch, "E347.0.69.7", {"start": v(-148.74, 5102.9) * mm, "end": v(-150.06, 5092.2) * mm});
            skLineSegment(sketch, "E347.0.69.8", {"start": v(-90.74, 5104.7) * mm, "end": v(-90.74, 5102.9) * mm});
            skLineSegment(sketch, "E347.0.69.9", {"start": v(-148.54, 5079.5) * mm, "end": v(-140.8, 5079.5) * mm});
            skArc(sketch, "E347.0.69.10", {"start": v(-82.6, 5104.7) * mm, "mid": v(-82.66, 5104.85) * mm, "end": v(-82.8, 5104.9) * mm});
            skLineSegment(sketch, "E347.0.69.11", {"start": v(-82.8, 5104.9) * mm, "end": v(-90.54, 5104.9) * mm});
            skArc(sketch, "E347.0.69.12", {"start": v(-140.8, 5079.5) * mm, "mid": v(-140.66, 5079.57) * mm, "end": v(-140.6, 5079.7) * mm});
            skLineSegment(sketch, "E347.0.69.13", {"start": v(-82.6, 5102.9) * mm, "end": v(-82.6, 5104.7) * mm});
            skLineSegment(sketch, "E347.0.69.14", {"start": v(-140.6, 5079.7) * mm, "end": v(-140.6, 5081.5) * mm});
            skArc(sketch, "E347.0.69.15", {"start": v(-90.54, 5104.9) * mm, "mid": v(-90.68, 5104.85) * mm, "end": v(-90.74, 5104.7) * mm});
            skLineSegment(sketch, "E347.0.69.16", {"start": v(-140.6, 5102.9) * mm, "end": v(-140.6, 5104.7) * mm});
            skArc(sketch, "E347.0.69.17", {"start": v(-140.6, 5104.7) * mm, "mid": v(-140.66, 5104.85) * mm, "end": v(-140.8, 5104.9) * mm});
            skLineSegment(sketch, "E347.0.69.18", {"start": v(-140.8, 5104.9) * mm, "end": v(-148.54, 5104.9) * mm});
            skArc(sketch, "E347.0.69.19", {"start": v(-90.74, 5079.7) * mm, "mid": v(-90.68, 5079.57) * mm, "end": v(-90.54, 5079.5) * mm});
            skLineSegment(sketch, "E347.0.69.20", {"start": v(-90.74, 5081.5) * mm, "end": v(-90.74, 5079.7) * mm});
            skLineSegment(sketch, "E347.0.69.21", {"start": v(-82.6, 5079.7) * mm, "end": v(-82.6, 5081.5) * mm});
            skArc(sketch, "E347.0.69.22", {"start": v(-148.54, 5104.9) * mm, "mid": v(-148.68, 5104.85) * mm, "end": v(-148.74, 5104.7) * mm});
            skLineSegment(sketch, "E347.0.69.23", {"start": v(-148.74, 5104.7) * mm, "end": v(-148.74, 5102.9) * mm});
            skArc(sketch, "E347.0.69.24", {"start": v(-148.74, 5079.7) * mm, "mid": v(-148.68, 5079.57) * mm, "end": v(-148.54, 5079.5) * mm});
            skLineSegment(sketch, "E347.0.69.25", {"start": v(-148.74, 5081.5) * mm, "end": v(-148.74, 5079.7) * mm});
            skLineSegment(sketch, "E347.0.69.26", {"start": v(-90.54, 5079.5) * mm, "end": v(-82.8, 5079.5) * mm});
            skArc(sketch, "E347.0.69.27", {"start": v(-82.8, 5079.5) * mm, "mid": v(-82.66, 5079.57) * mm, "end": v(-82.6, 5079.7) * mm});
            skLineSegment(sketch, "E347.0.70.0", {"start": v(-92.06, 5168.4) * mm, "end": v(-90.74, 5157.7) * mm});
            skLineSegment(sketch, "E347.0.70.1", {"start": v(-139.29, 5168.4) * mm, "end": v(-140.6, 5179.1) * mm});
            skLineSegment(sketch, "E347.0.70.2", {"start": v(-81.29, 5168.4) * mm, "end": v(-82.6, 5179.1) * mm});
            skLineSegment(sketch, "E347.0.70.3", {"start": v(-82.6, 5157.7) * mm, "end": v(-81.29, 5168.4) * mm});
            skLineSegment(sketch, "E347.0.70.4", {"start": v(-140.6, 5157.7) * mm, "end": v(-139.29, 5168.4) * mm});
            skLineSegment(sketch, "E347.0.70.5", {"start": v(-150.06, 5168.4) * mm, "end": v(-148.74, 5157.7) * mm});
            skLineSegment(sketch, "E347.0.70.6", {"start": v(-90.74, 5179.1) * mm, "end": v(-92.06, 5168.4) * mm});
            skLineSegment(sketch, "E347.0.70.7", {"start": v(-148.74, 5179.1) * mm, "end": v(-150.06, 5168.4) * mm});
            skLineSegment(sketch, "E347.0.70.8", {"start": v(-90.74, 5180.9) * mm, "end": v(-90.74, 5179.1) * mm});
            skLineSegment(sketch, "E347.0.70.9", {"start": v(-148.54, 5155.7) * mm, "end": v(-140.8, 5155.7) * mm});
            skArc(sketch, "E347.0.70.10", {"start": v(-82.6, 5180.9) * mm, "mid": v(-82.66, 5181.05) * mm, "end": v(-82.8, 5181.1) * mm});
            skLineSegment(sketch, "E347.0.70.11", {"start": v(-82.8, 5181.1) * mm, "end": v(-90.54, 5181.1) * mm});
            skArc(sketch, "E347.0.70.12", {"start": v(-140.8, 5155.7) * mm, "mid": v(-140.66, 5155.77) * mm, "end": v(-140.6, 5155.9) * mm});
            skLineSegment(sketch, "E347.0.70.13", {"start": v(-82.6, 5179.1) * mm, "end": v(-82.6, 5180.9) * mm});
            skLineSegment(sketch, "E347.0.70.14", {"start": v(-140.6, 5155.9) * mm, "end": v(-140.6, 5157.7) * mm});
            skArc(sketch, "E347.0.70.15", {"start": v(-90.54, 5181.1) * mm, "mid": v(-90.68, 5181.05) * mm, "end": v(-90.74, 5180.9) * mm});
            skLineSegment(sketch, "E347.0.70.16", {"start": v(-140.6, 5179.1) * mm, "end": v(-140.6, 5180.9) * mm});
            skArc(sketch, "E347.0.70.17", {"start": v(-140.6, 5180.9) * mm, "mid": v(-140.66, 5181.05) * mm, "end": v(-140.8, 5181.1) * mm});
            skLineSegment(sketch, "E347.0.70.18", {"start": v(-140.8, 5181.1) * mm, "end": v(-148.54, 5181.1) * mm});
            skArc(sketch, "E347.0.70.19", {"start": v(-90.74, 5155.9) * mm, "mid": v(-90.68, 5155.77) * mm, "end": v(-90.54, 5155.7) * mm});
            skLineSegment(sketch, "E347.0.70.20", {"start": v(-90.74, 5157.7) * mm, "end": v(-90.74, 5155.9) * mm});
            skLineSegment(sketch, "E347.0.70.21", {"start": v(-82.6, 5155.9) * mm, "end": v(-82.6, 5157.7) * mm});
            skArc(sketch, "E347.0.70.22", {"start": v(-148.54, 5181.1) * mm, "mid": v(-148.68, 5181.05) * mm, "end": v(-148.74, 5180.9) * mm});
            skLineSegment(sketch, "E347.0.70.23", {"start": v(-148.74, 5180.9) * mm, "end": v(-148.74, 5179.1) * mm});
            skArc(sketch, "E347.0.70.24", {"start": v(-148.74, 5155.9) * mm, "mid": v(-148.68, 5155.77) * mm, "end": v(-148.54, 5155.7) * mm});
            skLineSegment(sketch, "E347.0.70.25", {"start": v(-148.74, 5157.7) * mm, "end": v(-148.74, 5155.9) * mm});
            skLineSegment(sketch, "E347.0.70.26", {"start": v(-90.54, 5155.7) * mm, "end": v(-82.8, 5155.7) * mm});
            skArc(sketch, "E347.0.70.27", {"start": v(-82.8, 5155.7) * mm, "mid": v(-82.66, 5155.77) * mm, "end": v(-82.6, 5155.9) * mm});
            skLineSegment(sketch, "E347.0.71.0", {"start": v(-92.06, 5244.6) * mm, "end": v(-90.74, 5233.9) * mm});
            skLineSegment(sketch, "E347.0.71.1", {"start": v(-139.29, 5244.6) * mm, "end": v(-140.6, 5255.3) * mm});
            skLineSegment(sketch, "E347.0.71.2", {"start": v(-81.29, 5244.6) * mm, "end": v(-82.6, 5255.3) * mm});
            skLineSegment(sketch, "E347.0.71.3", {"start": v(-82.6, 5233.9) * mm, "end": v(-81.29, 5244.6) * mm});
            skLineSegment(sketch, "E347.0.71.4", {"start": v(-140.6, 5233.9) * mm, "end": v(-139.29, 5244.6) * mm});
            skLineSegment(sketch, "E347.0.71.5", {"start": v(-150.06, 5244.6) * mm, "end": v(-148.74, 5233.9) * mm});
            skLineSegment(sketch, "E347.0.71.6", {"start": v(-90.74, 5255.3) * mm, "end": v(-92.06, 5244.6) * mm});
            skLineSegment(sketch, "E347.0.71.7", {"start": v(-148.74, 5255.3) * mm, "end": v(-150.06, 5244.6) * mm});
            skLineSegment(sketch, "E347.0.71.8", {"start": v(-90.74, 5257.1) * mm, "end": v(-90.74, 5255.3) * mm});
            skLineSegment(sketch, "E347.0.71.9", {"start": v(-148.54, 5231.9) * mm, "end": v(-140.8, 5231.9) * mm});
            skArc(sketch, "E347.0.71.10", {"start": v(-82.6, 5257.1) * mm, "mid": v(-82.66, 5257.25) * mm, "end": v(-82.8, 5257.3) * mm});
            skLineSegment(sketch, "E347.0.71.11", {"start": v(-82.8, 5257.3) * mm, "end": v(-90.54, 5257.3) * mm});
            skArc(sketch, "E347.0.71.12", {"start": v(-140.8, 5231.9) * mm, "mid": v(-140.66, 5231.97) * mm, "end": v(-140.6, 5232.1) * mm});
            skLineSegment(sketch, "E347.0.71.13", {"start": v(-82.6, 5255.3) * mm, "end": v(-82.6, 5257.1) * mm});
            skLineSegment(sketch, "E347.0.71.14", {"start": v(-140.6, 5232.1) * mm, "end": v(-140.6, 5233.9) * mm});
            skArc(sketch, "E347.0.71.15", {"start": v(-90.54, 5257.3) * mm, "mid": v(-90.68, 5257.25) * mm, "end": v(-90.74, 5257.1) * mm});
            skLineSegment(sketch, "E347.0.71.16", {"start": v(-140.6, 5255.3) * mm, "end": v(-140.6, 5257.1) * mm});
            skArc(sketch, "E347.0.71.17", {"start": v(-140.6, 5257.1) * mm, "mid": v(-140.66, 5257.25) * mm, "end": v(-140.8, 5257.3) * mm});
            skLineSegment(sketch, "E347.0.71.18", {"start": v(-140.8, 5257.3) * mm, "end": v(-148.54, 5257.3) * mm});
            skArc(sketch, "E347.0.71.19", {"start": v(-90.74, 5232.1) * mm, "mid": v(-90.68, 5231.97) * mm, "end": v(-90.54, 5231.9) * mm});
            skLineSegment(sketch, "E347.0.71.20", {"start": v(-90.74, 5233.9) * mm, "end": v(-90.74, 5232.1) * mm});
            skLineSegment(sketch, "E347.0.71.21", {"start": v(-82.6, 5232.1) * mm, "end": v(-82.6, 5233.9) * mm});
            skArc(sketch, "E347.0.71.22", {"start": v(-148.54, 5257.3) * mm, "mid": v(-148.68, 5257.25) * mm, "end": v(-148.74, 5257.1) * mm});
            skLineSegment(sketch, "E347.0.71.23", {"start": v(-148.74, 5257.1) * mm, "end": v(-148.74, 5255.3) * mm});
            skArc(sketch, "E347.0.71.24", {"start": v(-148.74, 5232.1) * mm, "mid": v(-148.68, 5231.97) * mm, "end": v(-148.54, 5231.9) * mm});
            skLineSegment(sketch, "E347.0.71.25", {"start": v(-148.74, 5233.9) * mm, "end": v(-148.74, 5232.1) * mm});
            skLineSegment(sketch, "E347.0.71.26", {"start": v(-90.54, 5231.9) * mm, "end": v(-82.8, 5231.9) * mm});
            skArc(sketch, "E347.0.71.27", {"start": v(-82.8, 5231.9) * mm, "mid": v(-82.66, 5231.97) * mm, "end": v(-82.6, 5232.1) * mm});
            skLineSegment(sketch, "E347.0.72.0", {"start": v(-92.06, 5320.8) * mm, "end": v(-90.74, 5310.1) * mm});
            skLineSegment(sketch, "E347.0.72.1", {"start": v(-139.29, 5320.8) * mm, "end": v(-140.6, 5331.5) * mm});
            skLineSegment(sketch, "E347.0.72.2", {"start": v(-81.29, 5320.8) * mm, "end": v(-82.6, 5331.5) * mm});
            skLineSegment(sketch, "E347.0.72.3", {"start": v(-82.6, 5310.1) * mm, "end": v(-81.29, 5320.8) * mm});
            skLineSegment(sketch, "E347.0.72.4", {"start": v(-140.6, 5310.1) * mm, "end": v(-139.29, 5320.8) * mm});
            skLineSegment(sketch, "E347.0.72.5", {"start": v(-150.06, 5320.8) * mm, "end": v(-148.74, 5310.1) * mm});
            skLineSegment(sketch, "E347.0.72.6", {"start": v(-90.74, 5331.5) * mm, "end": v(-92.06, 5320.8) * mm});
            skLineSegment(sketch, "E347.0.72.7", {"start": v(-148.74, 5331.5) * mm, "end": v(-150.06, 5320.8) * mm});
            skLineSegment(sketch, "E347.0.72.8", {"start": v(-90.74, 5333.3) * mm, "end": v(-90.74, 5331.5) * mm});
            skLineSegment(sketch, "E347.0.72.9", {"start": v(-148.54, 5308.1) * mm, "end": v(-140.8, 5308.1) * mm});
            skArc(sketch, "E347.0.72.10", {"start": v(-82.6, 5333.3) * mm, "mid": v(-82.66, 5333.45) * mm, "end": v(-82.8, 5333.5) * mm});
            skLineSegment(sketch, "E347.0.72.11", {"start": v(-82.8, 5333.5) * mm, "end": v(-90.54, 5333.5) * mm});
            skArc(sketch, "E347.0.72.12", {"start": v(-140.8, 5308.1) * mm, "mid": v(-140.66, 5308.17) * mm, "end": v(-140.6, 5308.3) * mm});
            skLineSegment(sketch, "E347.0.72.13", {"start": v(-82.6, 5331.5) * mm, "end": v(-82.6, 5333.3) * mm});
            skLineSegment(sketch, "E347.0.72.14", {"start": v(-140.6, 5308.3) * mm, "end": v(-140.6, 5310.1) * mm});
            skArc(sketch, "E347.0.72.15", {"start": v(-90.54, 5333.5) * mm, "mid": v(-90.68, 5333.45) * mm, "end": v(-90.74, 5333.3) * mm});
            skLineSegment(sketch, "E347.0.72.16", {"start": v(-140.6, 5331.5) * mm, "end": v(-140.6, 5333.3) * mm});
            skArc(sketch, "E347.0.72.17", {"start": v(-140.6, 5333.3) * mm, "mid": v(-140.66, 5333.45) * mm, "end": v(-140.8, 5333.5) * mm});
            skLineSegment(sketch, "E347.0.72.18", {"start": v(-140.8, 5333.5) * mm, "end": v(-148.54, 5333.5) * mm});
            skArc(sketch, "E347.0.72.19", {"start": v(-90.74, 5308.3) * mm, "mid": v(-90.68, 5308.17) * mm, "end": v(-90.54, 5308.1) * mm});
            skLineSegment(sketch, "E347.0.72.20", {"start": v(-90.74, 5310.1) * mm, "end": v(-90.74, 5308.3) * mm});
            skLineSegment(sketch, "E347.0.72.21", {"start": v(-82.6, 5308.3) * mm, "end": v(-82.6, 5310.1) * mm});
            skArc(sketch, "E347.0.72.22", {"start": v(-148.54, 5333.5) * mm, "mid": v(-148.68, 5333.45) * mm, "end": v(-148.74, 5333.3) * mm});
            skLineSegment(sketch, "E347.0.72.23", {"start": v(-148.74, 5333.3) * mm, "end": v(-148.74, 5331.5) * mm});
            skArc(sketch, "E347.0.72.24", {"start": v(-148.74, 5308.3) * mm, "mid": v(-148.68, 5308.17) * mm, "end": v(-148.54, 5308.1) * mm});
            skLineSegment(sketch, "E347.0.72.25", {"start": v(-148.74, 5310.1) * mm, "end": v(-148.74, 5308.3) * mm});
            skLineSegment(sketch, "E347.0.72.26", {"start": v(-90.54, 5308.1) * mm, "end": v(-82.8, 5308.1) * mm});
            skArc(sketch, "E347.0.72.27", {"start": v(-82.8, 5308.1) * mm, "mid": v(-82.66, 5308.17) * mm, "end": v(-82.6, 5308.3) * mm});
            skLineSegment(sketch, "E347.0.73.0", {"start": v(-92.06, 5397) * mm, "end": v(-90.74, 5386.3) * mm});
            skLineSegment(sketch, "E347.0.73.1", {"start": v(-139.29, 5397) * mm, "end": v(-140.6, 5407.7) * mm});
            skLineSegment(sketch, "E347.0.73.2", {"start": v(-81.29, 5397) * mm, "end": v(-82.6, 5407.7) * mm});
            skLineSegment(sketch, "E347.0.73.3", {"start": v(-82.6, 5386.3) * mm, "end": v(-81.29, 5397) * mm});
            skLineSegment(sketch, "E347.0.73.4", {"start": v(-140.6, 5386.3) * mm, "end": v(-139.29, 5397) * mm});
            skLineSegment(sketch, "E347.0.73.5", {"start": v(-150.06, 5397) * mm, "end": v(-148.74, 5386.3) * mm});
            skLineSegment(sketch, "E347.0.73.6", {"start": v(-90.74, 5407.7) * mm, "end": v(-92.06, 5397) * mm});
            skLineSegment(sketch, "E347.0.73.7", {"start": v(-148.74, 5407.7) * mm, "end": v(-150.06, 5397) * mm});
            skLineSegment(sketch, "E347.0.73.8", {"start": v(-90.74, 5409.5) * mm, "end": v(-90.74, 5407.7) * mm});
            skLineSegment(sketch, "E347.0.73.9", {"start": v(-148.54, 5384.3) * mm, "end": v(-140.8, 5384.3) * mm});
            skArc(sketch, "E347.0.73.10", {"start": v(-82.6, 5409.5) * mm, "mid": v(-82.66, 5409.65) * mm, "end": v(-82.8, 5409.7) * mm});
            skLineSegment(sketch, "E347.0.73.11", {"start": v(-82.8, 5409.7) * mm, "end": v(-90.54, 5409.7) * mm});
            skArc(sketch, "E347.0.73.12", {"start": v(-140.8, 5384.3) * mm, "mid": v(-140.66, 5384.37) * mm, "end": v(-140.6, 5384.5) * mm});
            skLineSegment(sketch, "E347.0.73.13", {"start": v(-82.6, 5407.7) * mm, "end": v(-82.6, 5409.5) * mm});
            skLineSegment(sketch, "E347.0.73.14", {"start": v(-140.6, 5384.5) * mm, "end": v(-140.6, 5386.3) * mm});
            skArc(sketch, "E347.0.73.15", {"start": v(-90.54, 5409.7) * mm, "mid": v(-90.68, 5409.65) * mm, "end": v(-90.74, 5409.5) * mm});
            skLineSegment(sketch, "E347.0.73.16", {"start": v(-140.6, 5407.7) * mm, "end": v(-140.6, 5409.5) * mm});
            skArc(sketch, "E347.0.73.17", {"start": v(-140.6, 5409.5) * mm, "mid": v(-140.66, 5409.65) * mm, "end": v(-140.8, 5409.7) * mm});
            skLineSegment(sketch, "E347.0.73.18", {"start": v(-140.8, 5409.7) * mm, "end": v(-148.54, 5409.7) * mm});
            skArc(sketch, "E347.0.73.19", {"start": v(-90.74, 5384.5) * mm, "mid": v(-90.68, 5384.37) * mm, "end": v(-90.54, 5384.3) * mm});
            skLineSegment(sketch, "E347.0.73.20", {"start": v(-90.74, 5386.3) * mm, "end": v(-90.74, 5384.5) * mm});
            skLineSegment(sketch, "E347.0.73.21", {"start": v(-82.6, 5384.5) * mm, "end": v(-82.6, 5386.3) * mm});
            skArc(sketch, "E347.0.73.22", {"start": v(-148.54, 5409.7) * mm, "mid": v(-148.68, 5409.65) * mm, "end": v(-148.74, 5409.5) * mm});
            skLineSegment(sketch, "E347.0.73.23", {"start": v(-148.74, 5409.5) * mm, "end": v(-148.74, 5407.7) * mm});
            skArc(sketch, "E347.0.73.24", {"start": v(-148.74, 5384.5) * mm, "mid": v(-148.68, 5384.37) * mm, "end": v(-148.54, 5384.3) * mm});
            skLineSegment(sketch, "E347.0.73.25", {"start": v(-148.74, 5386.3) * mm, "end": v(-148.74, 5384.5) * mm});
            skLineSegment(sketch, "E347.0.73.26", {"start": v(-90.54, 5384.3) * mm, "end": v(-82.8, 5384.3) * mm});
            skArc(sketch, "E347.0.73.27", {"start": v(-82.8, 5384.3) * mm, "mid": v(-82.66, 5384.37) * mm, "end": v(-82.6, 5384.5) * mm});
            skLineSegment(sketch, "E347.0.74.0", {"start": v(-92.06, 5473.2) * mm, "end": v(-90.74, 5462.5) * mm});
            skLineSegment(sketch, "E347.0.74.1", {"start": v(-139.29, 5473.2) * mm, "end": v(-140.6, 5483.9) * mm});
            skLineSegment(sketch, "E347.0.74.2", {"start": v(-81.29, 5473.2) * mm, "end": v(-82.6, 5483.9) * mm});
            skLineSegment(sketch, "E347.0.74.3", {"start": v(-82.6, 5462.5) * mm, "end": v(-81.29, 5473.2) * mm});
            skLineSegment(sketch, "E347.0.74.4", {"start": v(-140.6, 5462.5) * mm, "end": v(-139.29, 5473.2) * mm});
            skLineSegment(sketch, "E347.0.74.5", {"start": v(-150.06, 5473.2) * mm, "end": v(-148.74, 5462.5) * mm});
            skLineSegment(sketch, "E347.0.74.6", {"start": v(-90.74, 5483.9) * mm, "end": v(-92.06, 5473.2) * mm});
            skLineSegment(sketch, "E347.0.74.7", {"start": v(-148.74, 5483.9) * mm, "end": v(-150.06, 5473.2) * mm});
            skLineSegment(sketch, "E347.0.74.8", {"start": v(-90.74, 5485.7) * mm, "end": v(-90.74, 5483.9) * mm});
            skLineSegment(sketch, "E347.0.74.9", {"start": v(-148.54, 5460.5) * mm, "end": v(-140.8, 5460.5) * mm});
            skArc(sketch, "E347.0.74.10", {"start": v(-82.6, 5485.7) * mm, "mid": v(-82.66, 5485.85) * mm, "end": v(-82.8, 5485.9) * mm});
            skLineSegment(sketch, "E347.0.74.11", {"start": v(-82.8, 5485.9) * mm, "end": v(-90.54, 5485.9) * mm});
            skArc(sketch, "E347.0.74.12", {"start": v(-140.8, 5460.5) * mm, "mid": v(-140.66, 5460.57) * mm, "end": v(-140.6, 5460.7) * mm});
            skLineSegment(sketch, "E347.0.74.13", {"start": v(-82.6, 5483.9) * mm, "end": v(-82.6, 5485.7) * mm});
            skLineSegment(sketch, "E347.0.74.14", {"start": v(-140.6, 5460.7) * mm, "end": v(-140.6, 5462.5) * mm});
            skArc(sketch, "E347.0.74.15", {"start": v(-90.54, 5485.9) * mm, "mid": v(-90.68, 5485.85) * mm, "end": v(-90.74, 5485.7) * mm});
            skLineSegment(sketch, "E347.0.74.16", {"start": v(-140.6, 5483.9) * mm, "end": v(-140.6, 5485.7) * mm});
            skArc(sketch, "E347.0.74.17", {"start": v(-140.6, 5485.7) * mm, "mid": v(-140.66, 5485.85) * mm, "end": v(-140.8, 5485.9) * mm});
            skLineSegment(sketch, "E347.0.74.18", {"start": v(-140.8, 5485.9) * mm, "end": v(-148.54, 5485.9) * mm});
            skArc(sketch, "E347.0.74.19", {"start": v(-90.74, 5460.7) * mm, "mid": v(-90.68, 5460.57) * mm, "end": v(-90.54, 5460.5) * mm});
            skLineSegment(sketch, "E347.0.74.20", {"start": v(-90.74, 5462.5) * mm, "end": v(-90.74, 5460.7) * mm});
            skLineSegment(sketch, "E347.0.74.21", {"start": v(-82.6, 5460.7) * mm, "end": v(-82.6, 5462.5) * mm});
            skArc(sketch, "E347.0.74.22", {"start": v(-148.54, 5485.9) * mm, "mid": v(-148.68, 5485.85) * mm, "end": v(-148.74, 5485.7) * mm});
            skLineSegment(sketch, "E347.0.74.23", {"start": v(-148.74, 5485.7) * mm, "end": v(-148.74, 5483.9) * mm});
            skArc(sketch, "E347.0.74.24", {"start": v(-148.74, 5460.7) * mm, "mid": v(-148.68, 5460.57) * mm, "end": v(-148.54, 5460.5) * mm});
            skLineSegment(sketch, "E347.0.74.25", {"start": v(-148.74, 5462.5) * mm, "end": v(-148.74, 5460.7) * mm});
            skLineSegment(sketch, "E347.0.74.26", {"start": v(-90.54, 5460.5) * mm, "end": v(-82.8, 5460.5) * mm});
            skArc(sketch, "E347.0.74.27", {"start": v(-82.8, 5460.5) * mm, "mid": v(-82.66, 5460.57) * mm, "end": v(-82.6, 5460.7) * mm});
            skLineSegment(sketch, "E347.0.75.0", {"start": v(-92.06, 5549.4) * mm, "end": v(-90.74, 5538.7) * mm});
            skLineSegment(sketch, "E347.0.75.1", {"start": v(-139.29, 5549.4) * mm, "end": v(-140.6, 5560.1) * mm});
            skLineSegment(sketch, "E347.0.75.2", {"start": v(-81.29, 5549.4) * mm, "end": v(-82.6, 5560.1) * mm});
            skLineSegment(sketch, "E347.0.75.3", {"start": v(-82.6, 5538.7) * mm, "end": v(-81.29, 5549.4) * mm});
            skLineSegment(sketch, "E347.0.75.4", {"start": v(-140.6, 5538.7) * mm, "end": v(-139.29, 5549.4) * mm});
            skLineSegment(sketch, "E347.0.75.5", {"start": v(-150.06, 5549.4) * mm, "end": v(-148.74, 5538.7) * mm});
            skLineSegment(sketch, "E347.0.75.6", {"start": v(-90.74, 5560.1) * mm, "end": v(-92.06, 5549.4) * mm});
            skLineSegment(sketch, "E347.0.75.7", {"start": v(-148.74, 5560.1) * mm, "end": v(-150.06, 5549.4) * mm});
            skLineSegment(sketch, "E347.0.75.8", {"start": v(-90.74, 5561.9) * mm, "end": v(-90.74, 5560.1) * mm});
            skLineSegment(sketch, "E347.0.75.9", {"start": v(-148.54, 5536.7) * mm, "end": v(-140.8, 5536.7) * mm});
            skArc(sketch, "E347.0.75.10", {"start": v(-82.6, 5561.9) * mm, "mid": v(-82.66, 5562.05) * mm, "end": v(-82.8, 5562.1) * mm});
            skLineSegment(sketch, "E347.0.75.11", {"start": v(-82.8, 5562.1) * mm, "end": v(-90.54, 5562.1) * mm});
            skArc(sketch, "E347.0.75.12", {"start": v(-140.8, 5536.7) * mm, "mid": v(-140.66, 5536.77) * mm, "end": v(-140.6, 5536.9) * mm});
            skLineSegment(sketch, "E347.0.75.13", {"start": v(-82.6, 5560.1) * mm, "end": v(-82.6, 5561.9) * mm});
            skLineSegment(sketch, "E347.0.75.14", {"start": v(-140.6, 5536.9) * mm, "end": v(-140.6, 5538.7) * mm});
            skArc(sketch, "E347.0.75.15", {"start": v(-90.54, 5562.1) * mm, "mid": v(-90.68, 5562.05) * mm, "end": v(-90.74, 5561.9) * mm});
            skLineSegment(sketch, "E347.0.75.16", {"start": v(-140.6, 5560.1) * mm, "end": v(-140.6, 5561.9) * mm});
            skArc(sketch, "E347.0.75.17", {"start": v(-140.6, 5561.9) * mm, "mid": v(-140.66, 5562.05) * mm, "end": v(-140.8, 5562.1) * mm});
            skLineSegment(sketch, "E347.0.75.18", {"start": v(-140.8, 5562.1) * mm, "end": v(-148.54, 5562.1) * mm});
            skArc(sketch, "E347.0.75.19", {"start": v(-90.74, 5536.9) * mm, "mid": v(-90.68, 5536.77) * mm, "end": v(-90.54, 5536.7) * mm});
            skLineSegment(sketch, "E347.0.75.20", {"start": v(-90.74, 5538.7) * mm, "end": v(-90.74, 5536.9) * mm});
            skLineSegment(sketch, "E347.0.75.21", {"start": v(-82.6, 5536.9) * mm, "end": v(-82.6, 5538.7) * mm});
            skArc(sketch, "E347.0.75.22", {"start": v(-148.54, 5562.1) * mm, "mid": v(-148.68, 5562.05) * mm, "end": v(-148.74, 5561.9) * mm});
            skLineSegment(sketch, "E347.0.75.23", {"start": v(-148.74, 5561.9) * mm, "end": v(-148.74, 5560.1) * mm});
            skArc(sketch, "E347.0.75.24", {"start": v(-148.74, 5536.9) * mm, "mid": v(-148.68, 5536.77) * mm, "end": v(-148.54, 5536.7) * mm});
            skLineSegment(sketch, "E347.0.75.25", {"start": v(-148.74, 5538.7) * mm, "end": v(-148.74, 5536.9) * mm});
            skLineSegment(sketch, "E347.0.75.26", {"start": v(-90.54, 5536.7) * mm, "end": v(-82.8, 5536.7) * mm});
            skArc(sketch, "E347.0.75.27", {"start": v(-82.8, 5536.7) * mm, "mid": v(-82.66, 5536.77) * mm, "end": v(-82.6, 5536.9) * mm});
            skLineSegment(sketch, "E347.0.76.0", {"start": v(-92.06, 5625.6) * mm, "end": v(-90.74, 5614.9) * mm});
            skLineSegment(sketch, "E347.0.76.1", {"start": v(-139.29, 5625.6) * mm, "end": v(-140.6, 5636.3) * mm});
            skLineSegment(sketch, "E347.0.76.2", {"start": v(-81.29, 5625.6) * mm, "end": v(-82.6, 5636.3) * mm});
            skLineSegment(sketch, "E347.0.76.3", {"start": v(-82.6, 5614.9) * mm, "end": v(-81.29, 5625.6) * mm});
            skLineSegment(sketch, "E347.0.76.4", {"start": v(-140.6, 5614.9) * mm, "end": v(-139.29, 5625.6) * mm});
            skLineSegment(sketch, "E347.0.76.5", {"start": v(-150.06, 5625.6) * mm, "end": v(-148.74, 5614.9) * mm});
            skLineSegment(sketch, "E347.0.76.6", {"start": v(-90.74, 5636.3) * mm, "end": v(-92.06, 5625.6) * mm});
            skLineSegment(sketch, "E347.0.76.7", {"start": v(-148.74, 5636.3) * mm, "end": v(-150.06, 5625.6) * mm});
            skLineSegment(sketch, "E347.0.76.8", {"start": v(-90.74, 5638.1) * mm, "end": v(-90.74, 5636.3) * mm});
            skLineSegment(sketch, "E347.0.76.9", {"start": v(-148.54, 5612.9) * mm, "end": v(-140.8, 5612.9) * mm});
            skArc(sketch, "E347.0.76.10", {"start": v(-82.6, 5638.1) * mm, "mid": v(-82.66, 5638.25) * mm, "end": v(-82.8, 5638.3) * mm});
            skLineSegment(sketch, "E347.0.76.11", {"start": v(-82.8, 5638.3) * mm, "end": v(-90.54, 5638.3) * mm});
            skArc(sketch, "E347.0.76.12", {"start": v(-140.8, 5612.9) * mm, "mid": v(-140.66, 5612.97) * mm, "end": v(-140.6, 5613.1) * mm});
            skLineSegment(sketch, "E347.0.76.13", {"start": v(-82.6, 5636.3) * mm, "end": v(-82.6, 5638.1) * mm});
            skLineSegment(sketch, "E347.0.76.14", {"start": v(-140.6, 5613.1) * mm, "end": v(-140.6, 5614.9) * mm});
            skArc(sketch, "E347.0.76.15", {"start": v(-90.54, 5638.3) * mm, "mid": v(-90.68, 5638.25) * mm, "end": v(-90.74, 5638.1) * mm});
            skLineSegment(sketch, "E347.0.76.16", {"start": v(-140.6, 5636.3) * mm, "end": v(-140.6, 5638.1) * mm});
            skArc(sketch, "E347.0.76.17", {"start": v(-140.6, 5638.1) * mm, "mid": v(-140.66, 5638.25) * mm, "end": v(-140.8, 5638.3) * mm});
            skLineSegment(sketch, "E347.0.76.18", {"start": v(-140.8, 5638.3) * mm, "end": v(-148.54, 5638.3) * mm});
            skArc(sketch, "E347.0.76.19", {"start": v(-90.74, 5613.1) * mm, "mid": v(-90.68, 5612.97) * mm, "end": v(-90.54, 5612.9) * mm});
            skLineSegment(sketch, "E347.0.76.20", {"start": v(-90.74, 5614.9) * mm, "end": v(-90.74, 5613.1) * mm});
            skLineSegment(sketch, "E347.0.76.21", {"start": v(-82.6, 5613.1) * mm, "end": v(-82.6, 5614.9) * mm});
            skArc(sketch, "E347.0.76.22", {"start": v(-148.54, 5638.3) * mm, "mid": v(-148.68, 5638.25) * mm, "end": v(-148.74, 5638.1) * mm});
            skLineSegment(sketch, "E347.0.76.23", {"start": v(-148.74, 5638.1) * mm, "end": v(-148.74, 5636.3) * mm});
            skArc(sketch, "E347.0.76.24", {"start": v(-148.74, 5613.1) * mm, "mid": v(-148.68, 5612.97) * mm, "end": v(-148.54, 5612.9) * mm});
            skLineSegment(sketch, "E347.0.76.25", {"start": v(-148.74, 5614.9) * mm, "end": v(-148.74, 5613.1) * mm});
            skLineSegment(sketch, "E347.0.76.26", {"start": v(-90.54, 5612.9) * mm, "end": v(-82.8, 5612.9) * mm});
            skArc(sketch, "E347.0.76.27", {"start": v(-82.8, 5612.9) * mm, "mid": v(-82.66, 5612.97) * mm, "end": v(-82.6, 5613.1) * mm});
            skLineSegment(sketch, "E347.0.77.0", {"start": v(-92.06, 5701.8) * mm, "end": v(-90.74, 5691.1) * mm});
            skLineSegment(sketch, "E347.0.77.1", {"start": v(-139.29, 5701.8) * mm, "end": v(-140.6, 5712.5) * mm});
            skLineSegment(sketch, "E347.0.77.2", {"start": v(-81.29, 5701.8) * mm, "end": v(-82.6, 5712.5) * mm});
            skLineSegment(sketch, "E347.0.77.3", {"start": v(-82.6, 5691.1) * mm, "end": v(-81.29, 5701.8) * mm});
            skLineSegment(sketch, "E347.0.77.4", {"start": v(-140.6, 5691.1) * mm, "end": v(-139.29, 5701.8) * mm});
            skLineSegment(sketch, "E347.0.77.5", {"start": v(-150.06, 5701.8) * mm, "end": v(-148.74, 5691.1) * mm});
            skLineSegment(sketch, "E347.0.77.6", {"start": v(-90.74, 5712.5) * mm, "end": v(-92.06, 5701.8) * mm});
            skLineSegment(sketch, "E347.0.77.7", {"start": v(-148.74, 5712.5) * mm, "end": v(-150.06, 5701.8) * mm});
            skLineSegment(sketch, "E347.0.77.8", {"start": v(-90.74, 5714.3) * mm, "end": v(-90.74, 5712.5) * mm});
            skLineSegment(sketch, "E347.0.77.9", {"start": v(-148.54, 5689.1) * mm, "end": v(-140.8, 5689.1) * mm});
            skArc(sketch, "E347.0.77.10", {"start": v(-82.6, 5714.3) * mm, "mid": v(-82.66, 5714.45) * mm, "end": v(-82.8, 5714.5) * mm});
            skLineSegment(sketch, "E347.0.77.11", {"start": v(-82.8, 5714.5) * mm, "end": v(-90.54, 5714.5) * mm});
            skArc(sketch, "E347.0.77.12", {"start": v(-140.8, 5689.1) * mm, "mid": v(-140.66, 5689.17) * mm, "end": v(-140.6, 5689.3) * mm});
            skLineSegment(sketch, "E347.0.77.13", {"start": v(-82.6, 5712.5) * mm, "end": v(-82.6, 5714.3) * mm});
            skLineSegment(sketch, "E347.0.77.14", {"start": v(-140.6, 5689.3) * mm, "end": v(-140.6, 5691.1) * mm});
            skArc(sketch, "E347.0.77.15", {"start": v(-90.54, 5714.5) * mm, "mid": v(-90.68, 5714.45) * mm, "end": v(-90.74, 5714.3) * mm});
            skLineSegment(sketch, "E347.0.77.16", {"start": v(-140.6, 5712.5) * mm, "end": v(-140.6, 5714.3) * mm});
            skArc(sketch, "E347.0.77.17", {"start": v(-140.6, 5714.3) * mm, "mid": v(-140.66, 5714.45) * mm, "end": v(-140.8, 5714.5) * mm});
            skLineSegment(sketch, "E347.0.77.18", {"start": v(-140.8, 5714.5) * mm, "end": v(-148.54, 5714.5) * mm});
            skArc(sketch, "E347.0.77.19", {"start": v(-90.74, 5689.3) * mm, "mid": v(-90.68, 5689.17) * mm, "end": v(-90.54, 5689.1) * mm});
            skLineSegment(sketch, "E347.0.77.20", {"start": v(-90.74, 5691.1) * mm, "end": v(-90.74, 5689.3) * mm});
            skLineSegment(sketch, "E347.0.77.21", {"start": v(-82.6, 5689.3) * mm, "end": v(-82.6, 5691.1) * mm});
            skArc(sketch, "E347.0.77.22", {"start": v(-148.54, 5714.5) * mm, "mid": v(-148.68, 5714.45) * mm, "end": v(-148.74, 5714.3) * mm});
            skLineSegment(sketch, "E347.0.77.23", {"start": v(-148.74, 5714.3) * mm, "end": v(-148.74, 5712.5) * mm});
            skArc(sketch, "E347.0.77.24", {"start": v(-148.74, 5689.3) * mm, "mid": v(-148.68, 5689.17) * mm, "end": v(-148.54, 5689.1) * mm});
            skLineSegment(sketch, "E347.0.77.25", {"start": v(-148.74, 5691.1) * mm, "end": v(-148.74, 5689.3) * mm});
            skLineSegment(sketch, "E347.0.77.26", {"start": v(-90.54, 5689.1) * mm, "end": v(-82.8, 5689.1) * mm});
            skArc(sketch, "E347.0.77.27", {"start": v(-82.8, 5689.1) * mm, "mid": v(-82.66, 5689.17) * mm, "end": v(-82.6, 5689.3) * mm});
            skLineSegment(sketch, "E347.0.78.0", {"start": v(-92.06, 5778) * mm, "end": v(-90.74, 5767.3) * mm});
            skLineSegment(sketch, "E347.0.78.1", {"start": v(-139.29, 5778) * mm, "end": v(-140.6, 5788.7) * mm});
            skLineSegment(sketch, "E347.0.78.2", {"start": v(-81.29, 5778) * mm, "end": v(-82.6, 5788.7) * mm});
            skLineSegment(sketch, "E347.0.78.3", {"start": v(-82.6, 5767.3) * mm, "end": v(-81.29, 5778) * mm});
            skLineSegment(sketch, "E347.0.78.4", {"start": v(-140.6, 5767.3) * mm, "end": v(-139.29, 5778) * mm});
            skLineSegment(sketch, "E347.0.78.5", {"start": v(-150.06, 5778) * mm, "end": v(-148.74, 5767.3) * mm});
            skLineSegment(sketch, "E347.0.78.6", {"start": v(-90.74, 5788.7) * mm, "end": v(-92.06, 5778) * mm});
            skLineSegment(sketch, "E347.0.78.7", {"start": v(-148.74, 5788.7) * mm, "end": v(-150.06, 5778) * mm});
            skLineSegment(sketch, "E347.0.78.8", {"start": v(-90.74, 5790.5) * mm, "end": v(-90.74, 5788.7) * mm});
            skLineSegment(sketch, "E347.0.78.9", {"start": v(-148.54, 5765.3) * mm, "end": v(-140.8, 5765.3) * mm});
            skArc(sketch, "E347.0.78.10", {"start": v(-82.6, 5790.5) * mm, "mid": v(-82.66, 5790.65) * mm, "end": v(-82.8, 5790.7) * mm});
            skLineSegment(sketch, "E347.0.78.11", {"start": v(-82.8, 5790.7) * mm, "end": v(-90.54, 5790.7) * mm});
            skArc(sketch, "E347.0.78.12", {"start": v(-140.8, 5765.3) * mm, "mid": v(-140.66, 5765.37) * mm, "end": v(-140.6, 5765.5) * mm});
            skLineSegment(sketch, "E347.0.78.13", {"start": v(-82.6, 5788.7) * mm, "end": v(-82.6, 5790.5) * mm});
            skLineSegment(sketch, "E347.0.78.14", {"start": v(-140.6, 5765.5) * mm, "end": v(-140.6, 5767.3) * mm});
            skArc(sketch, "E347.0.78.15", {"start": v(-90.54, 5790.7) * mm, "mid": v(-90.68, 5790.65) * mm, "end": v(-90.74, 5790.5) * mm});
            skLineSegment(sketch, "E347.0.78.16", {"start": v(-140.6, 5788.7) * mm, "end": v(-140.6, 5790.5) * mm});
            skArc(sketch, "E347.0.78.17", {"start": v(-140.6, 5790.5) * mm, "mid": v(-140.66, 5790.65) * mm, "end": v(-140.8, 5790.7) * mm});
            skLineSegment(sketch, "E347.0.78.18", {"start": v(-140.8, 5790.7) * mm, "end": v(-148.54, 5790.7) * mm});
            skArc(sketch, "E347.0.78.19", {"start": v(-90.74, 5765.5) * mm, "mid": v(-90.68, 5765.37) * mm, "end": v(-90.54, 5765.3) * mm});
            skLineSegment(sketch, "E347.0.78.20", {"start": v(-90.74, 5767.3) * mm, "end": v(-90.74, 5765.5) * mm});
            skLineSegment(sketch, "E347.0.78.21", {"start": v(-82.6, 5765.5) * mm, "end": v(-82.6, 5767.3) * mm});
            skArc(sketch, "E347.0.78.22", {"start": v(-148.54, 5790.7) * mm, "mid": v(-148.68, 5790.65) * mm, "end": v(-148.74, 5790.5) * mm});
            skLineSegment(sketch, "E347.0.78.23", {"start": v(-148.74, 5790.5) * mm, "end": v(-148.74, 5788.7) * mm});
            skArc(sketch, "E347.0.78.24", {"start": v(-148.74, 5765.5) * mm, "mid": v(-148.68, 5765.37) * mm, "end": v(-148.54, 5765.3) * mm});
            skLineSegment(sketch, "E347.0.78.25", {"start": v(-148.74, 5767.3) * mm, "end": v(-148.74, 5765.5) * mm});
            skLineSegment(sketch, "E347.0.78.26", {"start": v(-90.54, 5765.3) * mm, "end": v(-82.8, 5765.3) * mm});
            skArc(sketch, "E347.0.78.27", {"start": v(-82.8, 5765.3) * mm, "mid": v(-82.66, 5765.37) * mm, "end": v(-82.6, 5765.5) * mm});
            skLineSegment(sketch, "E347.0.79.0", {"start": v(-92.06, 5854.2) * mm, "end": v(-90.74, 5843.5) * mm});
            skLineSegment(sketch, "E347.0.79.1", {"start": v(-139.29, 5854.2) * mm, "end": v(-140.6, 5864.9) * mm});
            skLineSegment(sketch, "E347.0.79.2", {"start": v(-81.29, 5854.2) * mm, "end": v(-82.6, 5864.9) * mm});
            skLineSegment(sketch, "E347.0.79.3", {"start": v(-82.6, 5843.5) * mm, "end": v(-81.29, 5854.2) * mm});
            skLineSegment(sketch, "E347.0.79.4", {"start": v(-140.6, 5843.5) * mm, "end": v(-139.29, 5854.2) * mm});
            skLineSegment(sketch, "E347.0.79.5", {"start": v(-150.06, 5854.2) * mm, "end": v(-148.74, 5843.5) * mm});
            skLineSegment(sketch, "E347.0.79.6", {"start": v(-90.74, 5864.9) * mm, "end": v(-92.06, 5854.2) * mm});
            skLineSegment(sketch, "E347.0.79.7", {"start": v(-148.74, 5864.9) * mm, "end": v(-150.06, 5854.2) * mm});
            skLineSegment(sketch, "E347.0.79.8", {"start": v(-90.74, 5866.7) * mm, "end": v(-90.74, 5864.9) * mm});
            skLineSegment(sketch, "E347.0.79.9", {"start": v(-148.54, 5841.5) * mm, "end": v(-140.8, 5841.5) * mm});
            skArc(sketch, "E347.0.79.10", {"start": v(-82.6, 5866.7) * mm, "mid": v(-82.66, 5866.85) * mm, "end": v(-82.8, 5866.9) * mm});
            skLineSegment(sketch, "E347.0.79.11", {"start": v(-82.8, 5866.9) * mm, "end": v(-90.54, 5866.9) * mm});
            skArc(sketch, "E347.0.79.12", {"start": v(-140.8, 5841.5) * mm, "mid": v(-140.66, 5841.57) * mm, "end": v(-140.6, 5841.7) * mm});
            skLineSegment(sketch, "E347.0.79.13", {"start": v(-82.6, 5864.9) * mm, "end": v(-82.6, 5866.7) * mm});
            skLineSegment(sketch, "E347.0.79.14", {"start": v(-140.6, 5841.7) * mm, "end": v(-140.6, 5843.5) * mm});
            skArc(sketch, "E347.0.79.15", {"start": v(-90.54, 5866.9) * mm, "mid": v(-90.68, 5866.85) * mm, "end": v(-90.74, 5866.7) * mm});
            skLineSegment(sketch, "E347.0.79.16", {"start": v(-140.6, 5864.9) * mm, "end": v(-140.6, 5866.7) * mm});
            skArc(sketch, "E347.0.79.17", {"start": v(-140.6, 5866.7) * mm, "mid": v(-140.66, 5866.85) * mm, "end": v(-140.8, 5866.9) * mm});
            skLineSegment(sketch, "E347.0.79.18", {"start": v(-140.8, 5866.9) * mm, "end": v(-148.54, 5866.9) * mm});
            skArc(sketch, "E347.0.79.19", {"start": v(-90.74, 5841.7) * mm, "mid": v(-90.68, 5841.57) * mm, "end": v(-90.54, 5841.5) * mm});
            skLineSegment(sketch, "E347.0.79.20", {"start": v(-90.74, 5843.5) * mm, "end": v(-90.74, 5841.7) * mm});
            skLineSegment(sketch, "E347.0.79.21", {"start": v(-82.6, 5841.7) * mm, "end": v(-82.6, 5843.5) * mm});
            skArc(sketch, "E347.0.79.22", {"start": v(-148.54, 5866.9) * mm, "mid": v(-148.68, 5866.85) * mm, "end": v(-148.74, 5866.7) * mm});
            skLineSegment(sketch, "E347.0.79.23", {"start": v(-148.74, 5866.7) * mm, "end": v(-148.74, 5864.9) * mm});
            skArc(sketch, "E347.0.79.24", {"start": v(-148.74, 5841.7) * mm, "mid": v(-148.68, 5841.57) * mm, "end": v(-148.54, 5841.5) * mm});
            skLineSegment(sketch, "E347.0.79.25", {"start": v(-148.74, 5843.5) * mm, "end": v(-148.74, 5841.7) * mm});
            skLineSegment(sketch, "E347.0.79.26", {"start": v(-90.54, 5841.5) * mm, "end": v(-82.8, 5841.5) * mm});
            skArc(sketch, "E347.0.79.27", {"start": v(-82.8, 5841.5) * mm, "mid": v(-82.66, 5841.57) * mm, "end": v(-82.6, 5841.7) * mm});
            skLineSegment(sketch, "E347.direction1", {"start": v(-148.54, -178.3) * mm, "end": v(-123.54, -178.3) * mm, "construction": true});
            skLineSegment(sketch, "E347.direction2", {"start": v(-148.54, -178.3) * mm, "end": v(-148.54, -102.1) * mm, "construction": true});
            skSolve(sketch);
        }
        {
            var Q0;
            Q0=makeQuery(id+"F5.imprint","IMPRINT",FACE,{"disambiguationData":[TD([[makeQuery(id+"F5.imprint","IMPRINT",EDGE,{"derivedFrom":sQuery(id+"F5.wireOp",EDGE,"E347.0.79.1")}),1.0]])]});
            var Q1;
            Q1=makeQuery(id+"F5.imprint","IMPRINT",FACE,{"disambiguationData":[TD([[makeQuery(id+"F5.imprint","IMPRINT",EDGE,{"derivedFrom":sQuery(id+"F5.wireOp",EDGE,"E347.0.79.0")}),1.0]])]});
            var Q2;
            Q2=makeQuery(id+"F5.imprint","IMPRINT",FACE,{"disambiguationData":[TD([[makeQuery(id+"F5.imprint","IMPRINT",EDGE,{"derivedFrom":sQuery(id+"F5.wireOp",EDGE,"E347.0.78.1")}),1.0]])]});
            var Q3;
            Q3=makeQuery(id+"F5.imprint","IMPRINT",FACE,{"disambiguationData":[TD([[makeQuery(id+"F5.imprint","IMPRINT",EDGE,{"derivedFrom":sQuery(id+"F5.wireOp",EDGE,"E347.0.78.0")}),1.0]])]});
            var Q4;
            Q4=makeQuery(id+"F5.imprint","IMPRINT",FACE,{"disambiguationData":[TD([[makeQuery(id+"F5.imprint","IMPRINT",EDGE,{"derivedFrom":sQuery(id+"F5.wireOp",EDGE,"E347.0.77.0")}),1.0]])]});
            var Q5;
            Q5=makeQuery(id+"F5.imprint","IMPRINT",FACE,{"disambiguationData":[TD([[makeQuery(id+"F5.imprint","IMPRINT",EDGE,{"derivedFrom":sQuery(id+"F5.wireOp",EDGE,"E347.0.77.1")}),1.0]])]});
            var Q6;
            Q6=makeQuery(id+"F5.imprint","IMPRINT",FACE,{"disambiguationData":[TD([[makeQuery(id+"F5.imprint","IMPRINT",EDGE,{"derivedFrom":sQuery(id+"F5.wireOp",EDGE,"E347.0.76.1")}),1.0]])]});
            var Q7;
            Q7=makeQuery(id+"F5.imprint","IMPRINT",FACE,{"disambiguationData":[TD([[makeQuery(id+"F5.imprint","IMPRINT",EDGE,{"derivedFrom":sQuery(id+"F5.wireOp",EDGE,"E347.0.76.0")}),1.0]])]});
            var Q8;
            Q8=makeQuery(id+"F5.imprint","IMPRINT",FACE,{"disambiguationData":[TD([[makeQuery(id+"F5.imprint","IMPRINT",EDGE,{"derivedFrom":sQuery(id+"F5.wireOp",EDGE,"E347.0.75.0")}),1.0]])]});
            var Q9;
            Q9=makeQuery(id+"F5.imprint","IMPRINT",FACE,{"disambiguationData":[TD([[makeQuery(id+"F5.imprint","IMPRINT",EDGE,{"derivedFrom":sQuery(id+"F5.wireOp",EDGE,"E347.0.75.1")}),1.0]])]});
            var Q10;
            Q10=makeQuery(id+"F5.imprint","IMPRINT",FACE,{"disambiguationData":[TD([[makeQuery(id+"F5.imprint","IMPRINT",EDGE,{"derivedFrom":sQuery(id+"F5.wireOp",EDGE,"E347.0.74.1")}),1.0]])]});
            var Q11;
            Q11=makeQuery(id+"F5.imprint","IMPRINT",FACE,{"disambiguationData":[TD([[makeQuery(id+"F5.imprint","IMPRINT",EDGE,{"derivedFrom":sQuery(id+"F5.wireOp",EDGE,"E347.0.74.0")}),1.0]])]});
            var Q12;
            Q12=makeQuery(id+"F5.imprint","IMPRINT",FACE,{"disambiguationData":[TD([[makeQuery(id+"F5.imprint","IMPRINT",EDGE,{"derivedFrom":sQuery(id+"F5.wireOp",EDGE,"E347.0.73.0")}),1.0]])]});
            var Q13;
            Q13=makeQuery(id+"F5.imprint","IMPRINT",FACE,{"disambiguationData":[TD([[makeQuery(id+"F5.imprint","IMPRINT",EDGE,{"derivedFrom":sQuery(id+"F5.wireOp",EDGE,"E347.0.73.1")}),1.0]])]});
            var Q14;
            Q14=makeQuery(id+"F5.imprint","IMPRINT",FACE,{"disambiguationData":[TD([[makeQuery(id+"F5.imprint","IMPRINT",EDGE,{"derivedFrom":sQuery(id+"F5.wireOp",EDGE,"E347.0.72.1")}),1.0]])]});
            var Q15;
            Q15=makeQuery(id+"F5.imprint","IMPRINT",FACE,{"disambiguationData":[TD([[makeQuery(id+"F5.imprint","IMPRINT",EDGE,{"derivedFrom":sQuery(id+"F5.wireOp",EDGE,"E347.0.72.0")}),1.0]])]});
            var Q16;
            Q16=makeQuery(id+"F5.imprint","IMPRINT",FACE,{"disambiguationData":[TD([[makeQuery(id+"F5.imprint","IMPRINT",EDGE,{"derivedFrom":sQuery(id+"F5.wireOp",EDGE,"E347.0.71.0")}),1.0]])]});
            var Q17;
            Q17=makeQuery(id+"F5.imprint","IMPRINT",FACE,{"disambiguationData":[TD([[makeQuery(id+"F5.imprint","IMPRINT",EDGE,{"derivedFrom":sQuery(id+"F5.wireOp",EDGE,"E347.0.71.1")}),1.0]])]});
            var Q18;
            Q18=makeQuery(id+"F5.imprint","IMPRINT",FACE,{"disambiguationData":[TD([[makeQuery(id+"F5.imprint","IMPRINT",EDGE,{"derivedFrom":sQuery(id+"F5.wireOp",EDGE,"E347.0.70.1")}),1.0]])]});
            var Q19;
            Q19=makeQuery(id+"F5.imprint","IMPRINT",FACE,{"disambiguationData":[TD([[makeQuery(id+"F5.imprint","IMPRINT",EDGE,{"derivedFrom":sQuery(id+"F5.wireOp",EDGE,"E347.0.70.0")}),1.0]])]});
            var Q20;
            Q20=makeQuery(id+"F5.imprint","IMPRINT",FACE,{"disambiguationData":[TD([[makeQuery(id+"F5.imprint","IMPRINT",EDGE,{"derivedFrom":sQuery(id+"F5.wireOp",EDGE,"E347.0.69.0")}),1.0]])]});
            var Q21;
            Q21=makeQuery(id+"F5.imprint","IMPRINT",FACE,{"disambiguationData":[TD([[makeQuery(id+"F5.imprint","IMPRINT",EDGE,{"derivedFrom":sQuery(id+"F5.wireOp",EDGE,"E347.0.69.1")}),1.0]])]});
            var Q22;
            Q22=makeQuery(id+"F5.imprint","IMPRINT",FACE,{"disambiguationData":[TD([[makeQuery(id+"F5.imprint","IMPRINT",EDGE,{"derivedFrom":sQuery(id+"F5.wireOp",EDGE,"E347.0.68.1")}),1.0]])]});
            var Q23;
            Q23=makeQuery(id+"F5.imprint","IMPRINT",FACE,{"disambiguationData":[TD([[makeQuery(id+"F5.imprint","IMPRINT",EDGE,{"derivedFrom":sQuery(id+"F5.wireOp",EDGE,"E347.0.68.0")}),1.0]])]});
            var Q24;
            Q24=makeQuery(id+"F5.imprint","IMPRINT",FACE,{"disambiguationData":[TD([[makeQuery(id+"F5.imprint","IMPRINT",EDGE,{"derivedFrom":sQuery(id+"F5.wireOp",EDGE,"E347.0.67.1")}),1.0]])]});
            var Q25;
            Q25=makeQuery(id+"F5.imprint","IMPRINT",FACE,{"disambiguationData":[TD([[makeQuery(id+"F5.imprint","IMPRINT",EDGE,{"derivedFrom":sQuery(id+"F5.wireOp",EDGE,"E347.0.67.0")}),1.0]])]});
            var Q26;
            Q26=makeQuery(id+"F5.imprint","IMPRINT",FACE,{"disambiguationData":[TD([[makeQuery(id+"F5.imprint","IMPRINT",EDGE,{"derivedFrom":sQuery(id+"F5.wireOp",EDGE,"E347.0.66.0")}),1.0]])]});
            var Q27;
            Q27=makeQuery(id+"F5.imprint","IMPRINT",FACE,{"disambiguationData":[TD([[makeQuery(id+"F5.imprint","IMPRINT",EDGE,{"derivedFrom":sQuery(id+"F5.wireOp",EDGE,"E347.0.66.1")}),1.0]])]});
            var Q28;
            Q28=makeQuery(id+"F5.imprint","IMPRINT",FACE,{"disambiguationData":[TD([[makeQuery(id+"F5.imprint","IMPRINT",EDGE,{"derivedFrom":sQuery(id+"F5.wireOp",EDGE,"E347.0.65.0")}),1.0]])]});
            var Q29;
            Q29=makeQuery(id+"F5.imprint","IMPRINT",FACE,{"disambiguationData":[TD([[makeQuery(id+"F5.imprint","IMPRINT",EDGE,{"derivedFrom":sQuery(id+"F5.wireOp",EDGE,"E347.0.65.1")}),1.0]])]});
            var Q30;
            Q30=makeQuery(id+"F5.imprint","IMPRINT",FACE,{"disambiguationData":[TD([[makeQuery(id+"F5.imprint","IMPRINT",EDGE,{"derivedFrom":sQuery(id+"F5.wireOp",EDGE,"E347.0.64.0")}),1.0]])]});
            var Q31;
            Q31=makeQuery(id+"F5.imprint","IMPRINT",FACE,{"disambiguationData":[TD([[makeQuery(id+"F5.imprint","IMPRINT",EDGE,{"derivedFrom":sQuery(id+"F5.wireOp",EDGE,"E347.0.64.1")}),1.0]])]});
            var Q32;
            Q32=makeQuery(id+"F5.imprint","IMPRINT",FACE,{"disambiguationData":[TD([[makeQuery(id+"F5.imprint","IMPRINT",EDGE,{"derivedFrom":sQuery(id+"F5.wireOp",EDGE,"E347.0.63.0")}),1.0]])]});
            var Q33;
            Q33=makeQuery(id+"F5.imprint","IMPRINT",FACE,{"disambiguationData":[TD([[makeQuery(id+"F5.imprint","IMPRINT",EDGE,{"derivedFrom":sQuery(id+"F5.wireOp",EDGE,"E347.0.63.1")}),1.0]])]});
            var Q34;
            Q34=makeQuery(id+"F5.imprint","IMPRINT",FACE,{"disambiguationData":[TD([[makeQuery(id+"F5.imprint","IMPRINT",EDGE,{"derivedFrom":sQuery(id+"F5.wireOp",EDGE,"E347.0.62.0")}),1.0]])]});
            var Q35;
            Q35=makeQuery(id+"F5.imprint","IMPRINT",FACE,{"disambiguationData":[TD([[makeQuery(id+"F5.imprint","IMPRINT",EDGE,{"derivedFrom":sQuery(id+"F5.wireOp",EDGE,"E347.0.62.1")}),1.0]])]});
            var Q36;
            Q36=makeQuery(id+"F5.imprint","IMPRINT",FACE,{"disambiguationData":[TD([[makeQuery(id+"F5.imprint","IMPRINT",EDGE,{"derivedFrom":sQuery(id+"F5.wireOp",EDGE,"E347.0.61.0")}),1.0]])]});
            var Q37;
            Q37=makeQuery(id+"F5.imprint","IMPRINT",FACE,{"disambiguationData":[TD([[makeQuery(id+"F5.imprint","IMPRINT",EDGE,{"derivedFrom":sQuery(id+"F5.wireOp",EDGE,"E347.0.61.1")}),1.0]])]});
            var Q38;
            Q38=makeQuery(id+"F5.imprint","IMPRINT",FACE,{"disambiguationData":[TD([[makeQuery(id+"F5.imprint","IMPRINT",EDGE,{"derivedFrom":sQuery(id+"F5.wireOp",EDGE,"E347.0.60.0")}),1.0]])]});
            var Q39;
            Q39=makeQuery(id+"F5.imprint","IMPRINT",FACE,{"disambiguationData":[TD([[makeQuery(id+"F5.imprint","IMPRINT",EDGE,{"derivedFrom":sQuery(id+"F5.wireOp",EDGE,"E347.0.60.1")}),1.0]])]});
            var Q40;
            Q40=makeQuery(id+"F5.imprint","IMPRINT",FACE,{"disambiguationData":[TD([[makeQuery(id+"F5.imprint","IMPRINT",EDGE,{"derivedFrom":sQuery(id+"F5.wireOp",EDGE,"E347.0.59.0")}),1.0]])]});
            var Q41;
            Q41=makeQuery(id+"F5.imprint","IMPRINT",FACE,{"disambiguationData":[TD([[makeQuery(id+"F5.imprint","IMPRINT",EDGE,{"derivedFrom":sQuery(id+"F5.wireOp",EDGE,"E347.0.59.1")}),1.0]])]});
            var Q42;
            Q42=makeQuery(id+"F5.imprint","IMPRINT",FACE,{"disambiguationData":[TD([[makeQuery(id+"F5.imprint","IMPRINT",EDGE,{"derivedFrom":sQuery(id+"F5.wireOp",EDGE,"E347.0.58.0")}),1.0]])]});
            var Q43;
            Q43=makeQuery(id+"F5.imprint","IMPRINT",FACE,{"disambiguationData":[TD([[makeQuery(id+"F5.imprint","IMPRINT",EDGE,{"derivedFrom":sQuery(id+"F5.wireOp",EDGE,"E347.0.58.1")}),1.0]])]});
            var Q44;
            Q44=makeQuery(id+"F5.imprint","IMPRINT",FACE,{"disambiguationData":[TD([[makeQuery(id+"F5.imprint","IMPRINT",EDGE,{"derivedFrom":sQuery(id+"F5.wireOp",EDGE,"E347.0.57.0")}),1.0]])]});
            var Q45;
            Q45=makeQuery(id+"F5.imprint","IMPRINT",FACE,{"disambiguationData":[TD([[makeQuery(id+"F5.imprint","IMPRINT",EDGE,{"derivedFrom":sQuery(id+"F5.wireOp",EDGE,"E347.0.57.1")}),1.0]])]});
            var Q46;
            Q46=makeQuery(id+"F5.imprint","IMPRINT",FACE,{"disambiguationData":[TD([[makeQuery(id+"F5.imprint","IMPRINT",EDGE,{"derivedFrom":sQuery(id+"F5.wireOp",EDGE,"E347.0.56.0")}),1.0]])]});
            var Q47;
            Q47=makeQuery(id+"F5.imprint","IMPRINT",FACE,{"disambiguationData":[TD([[makeQuery(id+"F5.imprint","IMPRINT",EDGE,{"derivedFrom":sQuery(id+"F5.wireOp",EDGE,"E347.0.56.1")}),1.0]])]});
            var Q48;
            Q48=makeQuery(id+"F5.imprint","IMPRINT",FACE,{"disambiguationData":[TD([[makeQuery(id+"F5.imprint","IMPRINT",EDGE,{"derivedFrom":sQuery(id+"F5.wireOp",EDGE,"E347.0.55.0")}),1.0]])]});
            var Q49;
            Q49=makeQuery(id+"F5.imprint","IMPRINT",FACE,{"disambiguationData":[TD([[makeQuery(id+"F5.imprint","IMPRINT",EDGE,{"derivedFrom":sQuery(id+"F5.wireOp",EDGE,"E347.0.55.1")}),1.0]])]});
            var Q50;
            Q50=makeQuery(id+"F5.imprint","IMPRINT",FACE,{"disambiguationData":[TD([[makeQuery(id+"F5.imprint","IMPRINT",EDGE,{"derivedFrom":sQuery(id+"F5.wireOp",EDGE,"E347.0.54.0")}),1.0]])]});
            var Q51;
            Q51=makeQuery(id+"F5.imprint","IMPRINT",FACE,{"disambiguationData":[TD([[makeQuery(id+"F5.imprint","IMPRINT",EDGE,{"derivedFrom":sQuery(id+"F5.wireOp",EDGE,"E347.0.54.1")}),1.0]])]});
            var Q52;
            Q52=makeQuery(id+"F5.imprint","IMPRINT",FACE,{"disambiguationData":[TD([[makeQuery(id+"F5.imprint","IMPRINT",EDGE,{"derivedFrom":sQuery(id+"F5.wireOp",EDGE,"E347.0.53.0")}),1.0]])]});
            var Q53;
            Q53=makeQuery(id+"F5.imprint","IMPRINT",FACE,{"disambiguationData":[TD([[makeQuery(id+"F5.imprint","IMPRINT",EDGE,{"derivedFrom":sQuery(id+"F5.wireOp",EDGE,"E347.0.53.1")}),1.0]])]});
            var Q54;
            Q54=makeQuery(id+"F5.imprint","IMPRINT",FACE,{"disambiguationData":[TD([[makeQuery(id+"F5.imprint","IMPRINT",EDGE,{"derivedFrom":sQuery(id+"F5.wireOp",EDGE,"E347.0.52.0")}),1.0]])]});
            var Q55;
            Q55=makeQuery(id+"F5.imprint","IMPRINT",FACE,{"disambiguationData":[TD([[makeQuery(id+"F5.imprint","IMPRINT",EDGE,{"derivedFrom":sQuery(id+"F5.wireOp",EDGE,"E347.0.52.1")}),1.0]])]});
            var Q56;
            Q56=makeQuery(id+"F5.imprint","IMPRINT",FACE,{"disambiguationData":[TD([[makeQuery(id+"F5.imprint","IMPRINT",EDGE,{"derivedFrom":sQuery(id+"F5.wireOp",EDGE,"E347.0.51.0")}),1.0]])]});
            var Q57;
            Q57=makeQuery(id+"F5.imprint","IMPRINT",FACE,{"disambiguationData":[TD([[makeQuery(id+"F5.imprint","IMPRINT",EDGE,{"derivedFrom":sQuery(id+"F5.wireOp",EDGE,"E347.0.51.1")}),1.0]])]});
            var Q58;
            Q58=makeQuery(id+"F5.imprint","IMPRINT",FACE,{"disambiguationData":[TD([[makeQuery(id+"F5.imprint","IMPRINT",EDGE,{"derivedFrom":sQuery(id+"F5.wireOp",EDGE,"E347.0.50.0")}),1.0]])]});
            var Q59;
            Q59=makeQuery(id+"F5.imprint","IMPRINT",FACE,{"disambiguationData":[TD([[makeQuery(id+"F5.imprint","IMPRINT",EDGE,{"derivedFrom":sQuery(id+"F5.wireOp",EDGE,"E347.0.50.1")}),1.0]])]});
            var Q60;
            Q60=makeQuery(id+"F5.imprint","IMPRINT",FACE,{"disambiguationData":[TD([[makeQuery(id+"F5.imprint","IMPRINT",EDGE,{"derivedFrom":sQuery(id+"F5.wireOp",EDGE,"E347.0.49.0")}),1.0]])]});
            var Q61;
            Q61=makeQuery(id+"F5.imprint","IMPRINT",FACE,{"disambiguationData":[TD([[makeQuery(id+"F5.imprint","IMPRINT",EDGE,{"derivedFrom":sQuery(id+"F5.wireOp",EDGE,"E347.0.49.1")}),1.0]])]});
            var Q62;
            Q62=makeQuery(id+"F5.imprint","IMPRINT",FACE,{"disambiguationData":[TD([[makeQuery(id+"F5.imprint","IMPRINT",EDGE,{"derivedFrom":sQuery(id+"F5.wireOp",EDGE,"E347.0.48.0")}),1.0]])]});
            var Q63;
            Q63=makeQuery(id+"F5.imprint","IMPRINT",FACE,{"disambiguationData":[TD([[makeQuery(id+"F5.imprint","IMPRINT",EDGE,{"derivedFrom":sQuery(id+"F5.wireOp",EDGE,"E347.0.48.1")}),1.0]])]});
            var Q64;
            Q64=makeQuery(id+"F5.imprint","IMPRINT",FACE,{"disambiguationData":[TD([[makeQuery(id+"F5.imprint","IMPRINT",EDGE,{"derivedFrom":sQuery(id+"F5.wireOp",EDGE,"E347.0.47.0")}),1.0]])]});
            var Q65;
            Q65=makeQuery(id+"F5.imprint","IMPRINT",FACE,{"disambiguationData":[TD([[makeQuery(id+"F5.imprint","IMPRINT",EDGE,{"derivedFrom":sQuery(id+"F5.wireOp",EDGE,"E347.0.47.1")}),1.0]])]});
            var Q66;
            Q66=makeQuery(id+"F5.imprint","IMPRINT",FACE,{"disambiguationData":[TD([[makeQuery(id+"F5.imprint","IMPRINT",EDGE,{"derivedFrom":sQuery(id+"F5.wireOp",EDGE,"E347.0.46.0")}),1.0]])]});
            var Q67;
            Q67=makeQuery(id+"F5.imprint","IMPRINT",FACE,{"disambiguationData":[TD([[makeQuery(id+"F5.imprint","IMPRINT",EDGE,{"derivedFrom":sQuery(id+"F5.wireOp",EDGE,"E347.0.46.1")}),1.0]])]});
            var Q68;
            Q68=makeQuery(id+"F5.imprint","IMPRINT",FACE,{"disambiguationData":[TD([[makeQuery(id+"F5.imprint","IMPRINT",EDGE,{"derivedFrom":sQuery(id+"F5.wireOp",EDGE,"E347.0.45.0")}),1.0]])]});
            var Q69;
            Q69=makeQuery(id+"F5.imprint","IMPRINT",FACE,{"disambiguationData":[TD([[makeQuery(id+"F5.imprint","IMPRINT",EDGE,{"derivedFrom":sQuery(id+"F5.wireOp",EDGE,"E347.0.45.1")}),1.0]])]});
            var Q70;
            Q70=makeQuery(id+"F5.imprint","IMPRINT",FACE,{"disambiguationData":[TD([[makeQuery(id+"F5.imprint","IMPRINT",EDGE,{"derivedFrom":sQuery(id+"F5.wireOp",EDGE,"E347.0.44.0")}),1.0]])]});
            var Q71;
            Q71=makeQuery(id+"F5.imprint","IMPRINT",FACE,{"disambiguationData":[TD([[makeQuery(id+"F5.imprint","IMPRINT",EDGE,{"derivedFrom":sQuery(id+"F5.wireOp",EDGE,"E347.0.44.1")}),1.0]])]});
            var Q72;
            Q72=makeQuery(id+"F5.imprint","IMPRINT",FACE,{"disambiguationData":[TD([[makeQuery(id+"F5.imprint","IMPRINT",EDGE,{"derivedFrom":sQuery(id+"F5.wireOp",EDGE,"E347.0.43.0")}),1.0]])]});
            var Q73;
            Q73=makeQuery(id+"F5.imprint","IMPRINT",FACE,{"disambiguationData":[TD([[makeQuery(id+"F5.imprint","IMPRINT",EDGE,{"derivedFrom":sQuery(id+"F5.wireOp",EDGE,"E347.0.43.1")}),1.0]])]});
            var Q74;
            Q74=makeQuery(id+"F5.imprint","IMPRINT",FACE,{"disambiguationData":[TD([[makeQuery(id+"F5.imprint","IMPRINT",EDGE,{"derivedFrom":sQuery(id+"F5.wireOp",EDGE,"E347.0.42.0")}),1.0]])]});
            var Q75;
            Q75=makeQuery(id+"F5.imprint","IMPRINT",FACE,{"disambiguationData":[TD([[makeQuery(id+"F5.imprint","IMPRINT",EDGE,{"derivedFrom":sQuery(id+"F5.wireOp",EDGE,"E347.0.42.1")}),1.0]])]});
            var Q76;
            Q76=makeQuery(id+"F5.imprint","IMPRINT",FACE,{"disambiguationData":[TD([[makeQuery(id+"F5.imprint","IMPRINT",EDGE,{"derivedFrom":sQuery(id+"F5.wireOp",EDGE,"E347.0.41.0")}),1.0]])]});
            var Q77;
            Q77=makeQuery(id+"F5.imprint","IMPRINT",FACE,{"disambiguationData":[TD([[makeQuery(id+"F5.imprint","IMPRINT",EDGE,{"derivedFrom":sQuery(id+"F5.wireOp",EDGE,"E347.0.41.1")}),1.0]])]});
            var Q78;
            Q78=makeQuery(id+"F5.imprint","IMPRINT",FACE,{"disambiguationData":[TD([[makeQuery(id+"F5.imprint","IMPRINT",EDGE,{"derivedFrom":sQuery(id+"F5.wireOp",EDGE,"E347.0.40.0")}),1.0]])]});
            var Q79;
            Q79=makeQuery(id+"F5.imprint","IMPRINT",FACE,{"disambiguationData":[TD([[makeQuery(id+"F5.imprint","IMPRINT",EDGE,{"derivedFrom":sQuery(id+"F5.wireOp",EDGE,"E347.0.40.1")}),1.0]])]});
            var Q80;
            Q80=makeQuery(id+"F5.imprint","IMPRINT",FACE,{"disambiguationData":[TD([[makeQuery(id+"F5.imprint","IMPRINT",EDGE,{"derivedFrom":sQuery(id+"F5.wireOp",EDGE,"E347.0.39.0")}),1.0]])]});
            var Q81;
            Q81=makeQuery(id+"F5.imprint","IMPRINT",FACE,{"disambiguationData":[TD([[makeQuery(id+"F5.imprint","IMPRINT",EDGE,{"derivedFrom":sQuery(id+"F5.wireOp",EDGE,"E347.0.39.1")}),1.0]])]});
            var Q82;
            Q82=makeQuery(id+"F5.imprint","IMPRINT",FACE,{"disambiguationData":[TD([[makeQuery(id+"F5.imprint","IMPRINT",EDGE,{"derivedFrom":sQuery(id+"F5.wireOp",EDGE,"E347.0.38.0")}),1.0]])]});
            var Q83;
            Q83=makeQuery(id+"F5.imprint","IMPRINT",FACE,{"disambiguationData":[TD([[makeQuery(id+"F5.imprint","IMPRINT",EDGE,{"derivedFrom":sQuery(id+"F5.wireOp",EDGE,"E347.0.38.1")}),1.0]])]});
            var Q84;
            Q84=makeQuery(id+"F5.imprint","IMPRINT",FACE,{"disambiguationData":[TD([[makeQuery(id+"F5.imprint","IMPRINT",EDGE,{"derivedFrom":sQuery(id+"F5.wireOp",EDGE,"E347.0.37.0")}),1.0]])]});
            var Q85;
            Q85=makeQuery(id+"F5.imprint","IMPRINT",FACE,{"disambiguationData":[TD([[makeQuery(id+"F5.imprint","IMPRINT",EDGE,{"derivedFrom":sQuery(id+"F5.wireOp",EDGE,"E347.0.37.1")}),1.0]])]});
            var Q86;
            Q86=makeQuery(id+"F5.imprint","IMPRINT",FACE,{"disambiguationData":[TD([[makeQuery(id+"F5.imprint","IMPRINT",EDGE,{"derivedFrom":sQuery(id+"F5.wireOp",EDGE,"E347.0.36.0")}),1.0]])]});
            var Q87;
            Q87=makeQuery(id+"F5.imprint","IMPRINT",FACE,{"disambiguationData":[TD([[makeQuery(id+"F5.imprint","IMPRINT",EDGE,{"derivedFrom":sQuery(id+"F5.wireOp",EDGE,"E347.0.36.1")}),1.0]])]});
            var Q88;
            Q88=makeQuery(id+"F5.imprint","IMPRINT",FACE,{"disambiguationData":[TD([[makeQuery(id+"F5.imprint","IMPRINT",EDGE,{"derivedFrom":sQuery(id+"F5.wireOp",EDGE,"E347.0.35.0")}),1.0]])]});
            var Q89;
            Q89=makeQuery(id+"F5.imprint","IMPRINT",FACE,{"disambiguationData":[TD([[makeQuery(id+"F5.imprint","IMPRINT",EDGE,{"derivedFrom":sQuery(id+"F5.wireOp",EDGE,"E347.0.35.1")}),1.0]])]});
            var Q90;
            Q90=makeQuery(id+"F5.imprint","IMPRINT",FACE,{"disambiguationData":[TD([[makeQuery(id+"F5.imprint","IMPRINT",EDGE,{"derivedFrom":sQuery(id+"F5.wireOp",EDGE,"E347.0.34.0")}),1.0]])]});
            var Q91;
            Q91=makeQuery(id+"F5.imprint","IMPRINT",FACE,{"disambiguationData":[TD([[makeQuery(id+"F5.imprint","IMPRINT",EDGE,{"derivedFrom":sQuery(id+"F5.wireOp",EDGE,"E347.0.34.1")}),1.0]])]});
            var Q92;
            Q92=makeQuery(id+"F5.imprint","IMPRINT",FACE,{"disambiguationData":[TD([[makeQuery(id+"F5.imprint","IMPRINT",EDGE,{"derivedFrom":sQuery(id+"F5.wireOp",EDGE,"E347.0.33.0")}),1.0]])]});
            var Q93;
            Q93=makeQuery(id+"F5.imprint","IMPRINT",FACE,{"disambiguationData":[TD([[makeQuery(id+"F5.imprint","IMPRINT",EDGE,{"derivedFrom":sQuery(id+"F5.wireOp",EDGE,"E347.0.33.1")}),1.0]])]});
            var Q94;
            Q94=makeQuery(id+"F5.imprint","IMPRINT",FACE,{"disambiguationData":[TD([[makeQuery(id+"F5.imprint","IMPRINT",EDGE,{"derivedFrom":sQuery(id+"F5.wireOp",EDGE,"E347.0.32.0")}),1.0]])]});
            var Q95;
            Q95=makeQuery(id+"F5.imprint","IMPRINT",FACE,{"disambiguationData":[TD([[makeQuery(id+"F5.imprint","IMPRINT",EDGE,{"derivedFrom":sQuery(id+"F5.wireOp",EDGE,"E347.0.32.1")}),1.0]])]});
            var Q96;
            Q96=makeQuery(id+"F5.imprint","IMPRINT",FACE,{"disambiguationData":[TD([[makeQuery(id+"F5.imprint","IMPRINT",EDGE,{"derivedFrom":sQuery(id+"F5.wireOp",EDGE,"E347.0.31.0")}),1.0]])]});
            var Q97;
            Q97=makeQuery(id+"F5.imprint","IMPRINT",FACE,{"disambiguationData":[TD([[makeQuery(id+"F5.imprint","IMPRINT",EDGE,{"derivedFrom":sQuery(id+"F5.wireOp",EDGE,"E347.0.31.1")}),1.0]])]});
            var Q98;
            Q98=makeQuery(id+"F5.imprint","IMPRINT",FACE,{"disambiguationData":[TD([[makeQuery(id+"F5.imprint","IMPRINT",EDGE,{"derivedFrom":sQuery(id+"F5.wireOp",EDGE,"E347.0.30.0")}),1.0]])]});
            var Q99;
            Q99=makeQuery(id+"F5.imprint","IMPRINT",FACE,{"disambiguationData":[TD([[makeQuery(id+"F5.imprint","IMPRINT",EDGE,{"derivedFrom":sQuery(id+"F5.wireOp",EDGE,"E347.0.30.1")}),1.0]])]});
            var Q100;
            Q100=makeQuery(id+"F5.imprint","IMPRINT",FACE,{"disambiguationData":[TD([[makeQuery(id+"F5.imprint","IMPRINT",EDGE,{"derivedFrom":sQuery(id+"F5.wireOp",EDGE,"E347.0.29.0")}),1.0]])]});
            var Q101;
            Q101=makeQuery(id+"F5.imprint","IMPRINT",FACE,{"disambiguationData":[TD([[makeQuery(id+"F5.imprint","IMPRINT",EDGE,{"derivedFrom":sQuery(id+"F5.wireOp",EDGE,"E347.0.29.1")}),1.0]])]});
            var Q102;
            Q102=makeQuery(id+"F5.imprint","IMPRINT",FACE,{"disambiguationData":[TD([[makeQuery(id+"F5.imprint","IMPRINT",EDGE,{"derivedFrom":sQuery(id+"F5.wireOp",EDGE,"E347.0.28.0")}),1.0]])]});
            var Q103;
            Q103=makeQuery(id+"F5.imprint","IMPRINT",FACE,{"disambiguationData":[TD([[makeQuery(id+"F5.imprint","IMPRINT",EDGE,{"derivedFrom":sQuery(id+"F5.wireOp",EDGE,"E347.0.28.1")}),1.0]])]});
            var Q104;
            Q104=makeQuery(id+"F5.imprint","IMPRINT",FACE,{"disambiguationData":[TD([[makeQuery(id+"F5.imprint","IMPRINT",EDGE,{"derivedFrom":sQuery(id+"F5.wireOp",EDGE,"E347.0.27.0")}),1.0]])]});
            var Q105;
            Q105=makeQuery(id+"F5.imprint","IMPRINT",FACE,{"disambiguationData":[TD([[makeQuery(id+"F5.imprint","IMPRINT",EDGE,{"derivedFrom":sQuery(id+"F5.wireOp",EDGE,"E347.0.27.1")}),1.0]])]});
            var Q106;
            Q106=makeQuery(id+"F5.imprint","IMPRINT",FACE,{"disambiguationData":[TD([[makeQuery(id+"F5.imprint","IMPRINT",EDGE,{"derivedFrom":sQuery(id+"F5.wireOp",EDGE,"E347.0.26.0")}),1.0]])]});
            var Q107;
            Q107=makeQuery(id+"F5.imprint","IMPRINT",FACE,{"disambiguationData":[TD([[makeQuery(id+"F5.imprint","IMPRINT",EDGE,{"derivedFrom":sQuery(id+"F5.wireOp",EDGE,"E347.0.26.1")}),1.0]])]});
            var Q108;
            Q108=makeQuery(id+"F5.imprint","IMPRINT",FACE,{"disambiguationData":[TD([[makeQuery(id+"F5.imprint","IMPRINT",EDGE,{"derivedFrom":sQuery(id+"F5.wireOp",EDGE,"E347.0.25.0")}),1.0]])]});
            var Q109;
            Q109=makeQuery(id+"F5.imprint","IMPRINT",FACE,{"disambiguationData":[TD([[makeQuery(id+"F5.imprint","IMPRINT",EDGE,{"derivedFrom":sQuery(id+"F5.wireOp",EDGE,"E347.0.25.1")}),1.0]])]});
            var Q110;
            Q110=makeQuery(id+"F5.imprint","IMPRINT",FACE,{"disambiguationData":[TD([[makeQuery(id+"F5.imprint","IMPRINT",EDGE,{"derivedFrom":sQuery(id+"F5.wireOp",EDGE,"E347.0.24.0")}),1.0]])]});
            var Q111;
            Q111=makeQuery(id+"F5.imprint","IMPRINT",FACE,{"disambiguationData":[TD([[makeQuery(id+"F5.imprint","IMPRINT",EDGE,{"derivedFrom":sQuery(id+"F5.wireOp",EDGE,"E347.0.24.1")}),1.0]])]});
            var Q112;
            Q112=makeQuery(id+"F5.imprint","IMPRINT",FACE,{"disambiguationData":[TD([[makeQuery(id+"F5.imprint","IMPRINT",EDGE,{"derivedFrom":sQuery(id+"F5.wireOp",EDGE,"E347.0.23.0")}),1.0]])]});
            var Q113;
            Q113=makeQuery(id+"F5.imprint","IMPRINT",FACE,{"disambiguationData":[TD([[makeQuery(id+"F5.imprint","IMPRINT",EDGE,{"derivedFrom":sQuery(id+"F5.wireOp",EDGE,"E347.0.23.1")}),1.0]])]});
            var Q114;
            Q114=makeQuery(id+"F5.imprint","IMPRINT",FACE,{"disambiguationData":[TD([[makeQuery(id+"F5.imprint","IMPRINT",EDGE,{"derivedFrom":sQuery(id+"F5.wireOp",EDGE,"E347.0.22.0")}),1.0]])]});
            var Q115;
            Q115=makeQuery(id+"F5.imprint","IMPRINT",FACE,{"disambiguationData":[TD([[makeQuery(id+"F5.imprint","IMPRINT",EDGE,{"derivedFrom":sQuery(id+"F5.wireOp",EDGE,"E347.0.22.1")}),1.0]])]});
            var Q116;
            Q116=makeQuery(id+"F5.imprint","IMPRINT",FACE,{"disambiguationData":[TD([[makeQuery(id+"F5.imprint","IMPRINT",EDGE,{"derivedFrom":sQuery(id+"F5.wireOp",EDGE,"E347.0.21.0")}),1.0]])]});
            var Q117;
            Q117=makeQuery(id+"F5.imprint","IMPRINT",FACE,{"disambiguationData":[TD([[makeQuery(id+"F5.imprint","IMPRINT",EDGE,{"derivedFrom":sQuery(id+"F5.wireOp",EDGE,"E347.0.21.1")}),1.0]])]});
            var Q118;
            Q118=makeQuery(id+"F5.imprint","IMPRINT",FACE,{"disambiguationData":[TD([[makeQuery(id+"F5.imprint","IMPRINT",EDGE,{"derivedFrom":sQuery(id+"F5.wireOp",EDGE,"E347.0.20.0")}),1.0]])]});
            var Q119;
            Q119=makeQuery(id+"F5.imprint","IMPRINT",FACE,{"disambiguationData":[TD([[makeQuery(id+"F5.imprint","IMPRINT",EDGE,{"derivedFrom":sQuery(id+"F5.wireOp",EDGE,"E347.0.20.1")}),1.0]])]});
            var Q120;
            Q120=makeQuery(id+"F5.imprint","IMPRINT",FACE,{"disambiguationData":[TD([[makeQuery(id+"F5.imprint","IMPRINT",EDGE,{"derivedFrom":sQuery(id+"F5.wireOp",EDGE,"E347.0.19.0")}),1.0]])]});
            var Q121;
            Q121=makeQuery(id+"F5.imprint","IMPRINT",FACE,{"disambiguationData":[TD([[makeQuery(id+"F5.imprint","IMPRINT",EDGE,{"derivedFrom":sQuery(id+"F5.wireOp",EDGE,"E347.0.19.1")}),1.0]])]});
            var Q122;
            Q122=makeQuery(id+"F5.imprint","IMPRINT",FACE,{"disambiguationData":[TD([[makeQuery(id+"F5.imprint","IMPRINT",EDGE,{"derivedFrom":sQuery(id+"F5.wireOp",EDGE,"E347.0.18.0")}),1.0]])]});
            var Q123;
            Q123=makeQuery(id+"F5.imprint","IMPRINT",FACE,{"disambiguationData":[TD([[makeQuery(id+"F5.imprint","IMPRINT",EDGE,{"derivedFrom":sQuery(id+"F5.wireOp",EDGE,"E347.0.18.1")}),1.0]])]});
            var Q124;
            Q124=makeQuery(id+"F5.imprint","IMPRINT",FACE,{"disambiguationData":[TD([[makeQuery(id+"F5.imprint","IMPRINT",EDGE,{"derivedFrom":sQuery(id+"F5.wireOp",EDGE,"E347.0.17.0")}),1.0]])]});
            var Q125;
            Q125=makeQuery(id+"F5.imprint","IMPRINT",FACE,{"disambiguationData":[TD([[makeQuery(id+"F5.imprint","IMPRINT",EDGE,{"derivedFrom":sQuery(id+"F5.wireOp",EDGE,"E347.0.17.1")}),1.0]])]});
            var Q126;
            Q126=makeQuery(id+"F5.imprint","IMPRINT",FACE,{"disambiguationData":[TD([[makeQuery(id+"F5.imprint","IMPRINT",EDGE,{"derivedFrom":sQuery(id+"F5.wireOp",EDGE,"E347.0.16.0")}),1.0]])]});
            var Q127;
            Q127=makeQuery(id+"F5.imprint","IMPRINT",FACE,{"disambiguationData":[TD([[makeQuery(id+"F5.imprint","IMPRINT",EDGE,{"derivedFrom":sQuery(id+"F5.wireOp",EDGE,"E347.0.16.1")}),1.0]])]});
            var Q128;
            Q128=makeQuery(id+"F5.imprint","IMPRINT",FACE,{"disambiguationData":[TD([[makeQuery(id+"F5.imprint","IMPRINT",EDGE,{"derivedFrom":sQuery(id+"F5.wireOp",EDGE,"E347.0.15.0")}),1.0]])]});
            var Q129;
            Q129=makeQuery(id+"F5.imprint","IMPRINT",FACE,{"disambiguationData":[TD([[makeQuery(id+"F5.imprint","IMPRINT",EDGE,{"derivedFrom":sQuery(id+"F5.wireOp",EDGE,"E347.0.15.1")}),1.0]])]});
            var Q130;
            Q130=makeQuery(id+"F5.imprint","IMPRINT",FACE,{"disambiguationData":[TD([[makeQuery(id+"F5.imprint","IMPRINT",EDGE,{"derivedFrom":sQuery(id+"F5.wireOp",EDGE,"E347.0.14.0")}),1.0]])]});
            var Q131;
            Q131=makeQuery(id+"F5.imprint","IMPRINT",FACE,{"disambiguationData":[TD([[makeQuery(id+"F5.imprint","IMPRINT",EDGE,{"derivedFrom":sQuery(id+"F5.wireOp",EDGE,"E347.0.14.1")}),1.0]])]});
            var Q132;
            Q132=makeQuery(id+"F5.imprint","IMPRINT",FACE,{"disambiguationData":[TD([[makeQuery(id+"F5.imprint","IMPRINT",EDGE,{"derivedFrom":sQuery(id+"F5.wireOp",EDGE,"E347.0.13.0")}),1.0]])]});
            var Q133;
            Q133=makeQuery(id+"F5.imprint","IMPRINT",FACE,{"disambiguationData":[TD([[makeQuery(id+"F5.imprint","IMPRINT",EDGE,{"derivedFrom":sQuery(id+"F5.wireOp",EDGE,"E347.0.13.1")}),1.0]])]});
            var Q134;
            Q134=makeQuery(id+"F5.imprint","IMPRINT",FACE,{"disambiguationData":[TD([[makeQuery(id+"F5.imprint","IMPRINT",EDGE,{"derivedFrom":sQuery(id+"F5.wireOp",EDGE,"E347.0.12.0")}),1.0]])]});
            var Q135;
            Q135=makeQuery(id+"F5.imprint","IMPRINT",FACE,{"disambiguationData":[TD([[makeQuery(id+"F5.imprint","IMPRINT",EDGE,{"derivedFrom":sQuery(id+"F5.wireOp",EDGE,"E347.0.12.1")}),1.0]])]});
            var Q136;
            Q136=makeQuery(id+"F5.imprint","IMPRINT",FACE,{"disambiguationData":[TD([[makeQuery(id+"F5.imprint","IMPRINT",EDGE,{"derivedFrom":sQuery(id+"F5.wireOp",EDGE,"E347.0.11.0")}),1.0]])]});
            var Q137;
            Q137=makeQuery(id+"F5.imprint","IMPRINT",FACE,{"disambiguationData":[TD([[makeQuery(id+"F5.imprint","IMPRINT",EDGE,{"derivedFrom":sQuery(id+"F5.wireOp",EDGE,"E347.0.11.1")}),1.0]])]});
            var Q138;
            Q138=makeQuery(id+"F5.imprint","IMPRINT",FACE,{"disambiguationData":[TD([[makeQuery(id+"F5.imprint","IMPRINT",EDGE,{"derivedFrom":sQuery(id+"F5.wireOp",EDGE,"E347.0.10.0")}),1.0]])]});
            var Q139;
            Q139=makeQuery(id+"F5.imprint","IMPRINT",FACE,{"disambiguationData":[TD([[makeQuery(id+"F5.imprint","IMPRINT",EDGE,{"derivedFrom":sQuery(id+"F5.wireOp",EDGE,"E347.0.10.1")}),1.0]])]});
            var Q140;
            Q140=makeQuery(id+"F5.imprint","IMPRINT",FACE,{"disambiguationData":[TD([[makeQuery(id+"F5.imprint","IMPRINT",EDGE,{"derivedFrom":sQuery(id+"F5.wireOp",EDGE,"E347.0.9.0")}),1.0]])]});
            var Q141;
            Q141=makeQuery(id+"F5.imprint","IMPRINT",FACE,{"disambiguationData":[TD([[makeQuery(id+"F5.imprint","IMPRINT",EDGE,{"derivedFrom":sQuery(id+"F5.wireOp",EDGE,"E347.0.9.1")}),1.0]])]});
            var Q142;
            Q142=makeQuery(id+"F5.imprint","IMPRINT",FACE,{"disambiguationData":[TD([[makeQuery(id+"F5.imprint","IMPRINT",EDGE,{"derivedFrom":sQuery(id+"F5.wireOp",EDGE,"E347.0.8.0")}),1.0]])]});
            var Q143;
            Q143=makeQuery(id+"F5.imprint","IMPRINT",FACE,{"disambiguationData":[TD([[makeQuery(id+"F5.imprint","IMPRINT",EDGE,{"derivedFrom":sQuery(id+"F5.wireOp",EDGE,"E347.0.8.1")}),1.0]])]});
            var Q144;
            Q144=makeQuery(id+"F5.imprint","IMPRINT",FACE,{"disambiguationData":[TD([[makeQuery(id+"F5.imprint","IMPRINT",EDGE,{"derivedFrom":sQuery(id+"F5.wireOp",EDGE,"E347.0.7.0")}),1.0]])]});
            var Q145;
            Q145=makeQuery(id+"F5.imprint","IMPRINT",FACE,{"disambiguationData":[TD([[makeQuery(id+"F5.imprint","IMPRINT",EDGE,{"derivedFrom":sQuery(id+"F5.wireOp",EDGE,"E347.0.7.1")}),1.0]])]});
            var Q146;
            Q146=makeQuery(id+"F5.imprint","IMPRINT",FACE,{"disambiguationData":[TD([[makeQuery(id+"F5.imprint","IMPRINT",EDGE,{"derivedFrom":sQuery(id+"F5.wireOp",EDGE,"E347.0.6.0")}),1.0]])]});
            var Q147;
            Q147=makeQuery(id+"F5.imprint","IMPRINT",FACE,{"disambiguationData":[TD([[makeQuery(id+"F5.imprint","IMPRINT",EDGE,{"derivedFrom":sQuery(id+"F5.wireOp",EDGE,"E347.0.6.1")}),1.0]])]});
            var Q148;
            Q148=makeQuery(id+"F5.imprint","IMPRINT",FACE,{"disambiguationData":[TD([[makeQuery(id+"F5.imprint","IMPRINT",EDGE,{"derivedFrom":sQuery(id+"F5.wireOp",EDGE,"E347.0.5.0")}),1.0]])]});
            var Q149;
            Q149=makeQuery(id+"F5.imprint","IMPRINT",FACE,{"disambiguationData":[TD([[makeQuery(id+"F5.imprint","IMPRINT",EDGE,{"derivedFrom":sQuery(id+"F5.wireOp",EDGE,"E347.0.5.1")}),1.0]])]});
            var Q150;
            Q150=makeQuery(id+"F5.imprint","IMPRINT",FACE,{"disambiguationData":[TD([[makeQuery(id+"F5.imprint","IMPRINT",EDGE,{"derivedFrom":sQuery(id+"F5.wireOp",EDGE,"E347.0.4.0")}),1.0]])]});
            var Q151;
            Q151=makeQuery(id+"F5.imprint","IMPRINT",FACE,{"disambiguationData":[TD([[makeQuery(id+"F5.imprint","IMPRINT",EDGE,{"derivedFrom":sQuery(id+"F5.wireOp",EDGE,"E347.0.4.1")}),1.0]])]});
            var Q152;
            Q152=makeQuery(id+"F5.imprint","IMPRINT",FACE,{"disambiguationData":[TD([[makeQuery(id+"F5.imprint","IMPRINT",EDGE,{"derivedFrom":sQuery(id+"F5.wireOp",EDGE,"E347.0.3.0")}),1.0]])]});
            var Q153;
            Q153=makeQuery(id+"F5.imprint","IMPRINT",FACE,{"disambiguationData":[TD([[makeQuery(id+"F5.imprint","IMPRINT",EDGE,{"derivedFrom":sQuery(id+"F5.wireOp",EDGE,"E347.0.3.1")}),1.0]])]});
            var Q154;
            Q154=makeQuery(id+"F5.imprint","IMPRINT",FACE,{"disambiguationData":[TD([[makeQuery(id+"F5.imprint","IMPRINT",EDGE,{"derivedFrom":sQuery(id+"F5.wireOp",EDGE,"E347.0.2.0")}),1.0]])]});
            var Q155;
            Q155=makeQuery(id+"F5.imprint","IMPRINT",FACE,{"disambiguationData":[TD([[makeQuery(id+"F5.imprint","IMPRINT",EDGE,{"derivedFrom":sQuery(id+"F5.wireOp",EDGE,"E347.0.2.1")}),1.0]])]});
            var Q156;
            Q156=makeQuery(id+"F5.imprint","IMPRINT",FACE,{"disambiguationData":[TD([[makeQuery(id+"F5.imprint","IMPRINT",EDGE,{"derivedFrom":sQuery(id+"F5.wireOp",EDGE,"E347.0.1.0")}),1.0]])]});
            var Q157;
            Q157=makeQuery(id+"F5.imprint","IMPRINT",FACE,{"disambiguationData":[TD([[makeQuery(id+"F5.imprint","IMPRINT",EDGE,{"derivedFrom":sQuery(id+"F5.wireOp",EDGE,"E347.0.1.1")}),1.0]])]});
            var Q158;
            Q158=makeQuery(id+"F5.imprint","IMPRINT",FACE,{"disambiguationData":[TD([[makeQuery(id+"F5.imprint","IMPRINT",EDGE,{"derivedFrom":sQuery(id+"F5.wireOp",EDGE,"E333")}),1.0]])]});
            var Q159;
            Q159=makeQuery(id+"F5.imprint","IMPRINT",FACE,{"disambiguationData":[TD([[makeQuery(id+"F5.imprint","IMPRINT",EDGE,{"derivedFrom":sQuery(id+"F5.wireOp",EDGE,"E319")}),1.0]])]});
            extrude(context, id + "F6", {"entities" : qUnion([Q0, Q1, Q2, Q3, Q4, Q5, Q6, Q7, Q8, Q9, Q10, Q11, Q12, Q13, Q14, Q15, Q16, Q17, Q18, Q19, Q20, Q21, Q22, Q23, Q24, Q25, Q26, Q27, Q28, Q29, Q30, Q31, Q32, Q33, Q34, Q35, Q36, Q37, Q38, Q39, Q40, Q41, Q42, Q43, Q44, Q45, Q46, Q47, Q48, Q49, Q50, Q51, Q52, Q53, Q54, Q55, Q56, Q57, Q58, Q59, Q60, Q61, Q62, Q63, Q64, Q65, Q66, Q67, Q68, Q69, Q70, Q71, Q72, Q73, Q74, Q75, Q76, Q77, Q78, Q79, Q80, Q81, Q82, Q83, Q84, Q85, Q86, Q87, Q88, Q89, Q90, Q91, Q92, Q93, Q94, Q95, Q96, Q97, Q98, Q99, Q100, Q101, Q102, Q103, Q104, Q105, Q106, Q107, Q108, Q109, Q110, Q111, Q112, Q113, Q114, Q115, Q116, Q117, Q118, Q119, Q120, Q121, Q122, Q123, Q124, Q125, Q126, Q127, Q128, Q129, Q130, Q131, Q132, Q133, Q134, Q135, Q136, Q137, Q138, Q139, Q140, Q141, Q142, Q143, Q144, Q145, Q146, Q147, Q148, Q149, Q150, Q151, Q152, Q153, Q154, Q155, Q156, Q157, Q158, Q159]), "operationType" : NewBodyOperationType.REMOVE, "oppositeDirection" : true, "depth" : 10 * mm, "offsetDistance" : 25 * mm});
        }
        {
            var Q0;
            {var subQ0=sQuery(id+"F0.wireOp",EDGE,"E280");Q0=makeQuery(id+"F4.boolean.opBoolean","MERGE",FACE,{"derivedFrom":[makeQuery(id+"F2.boolean.opBoolean","MERGE",FACE,{"derivedFrom":[makeQuery(id+"F1.opExtrude","SWEPT_FACE",FACE,{"disambiguationData":[OSD([subQ0])]}),makeQuery(id+"F2.opExtrude","SWEPT_FACE",FACE,{"disambiguationData":[OSD([subQ0])]})]}),makeQuery(id+"F4.opExtrude","SWEPT_FACE",FACE,{"disambiguationData":[OSD([subQ0])]})]});}
            var sketch = newSketch(context, id + "F7", { "sketchPlane" : qUnion([Q0])});
            skCircle(sketch, "E348", {"center": v(275.35, -203.7) * mm, "radius": 5.5 * mm});
            skCircle(sketch, "E349.0.1.0", {"center": v(275.35, -127.5) * mm, "radius": 5.5 * mm});
            skCircle(sketch, "E349.0.2.0", {"center": v(275.35, -51.3) * mm, "radius": 5.5 * mm});
            skCircle(sketch, "E349.0.3.0", {"center": v(275.35, 24.9) * mm, "radius": 5.5 * mm});
            skCircle(sketch, "E349.0.4.0", {"center": v(275.35, 101.1) * mm, "radius": 5.5 * mm});
            skCircle(sketch, "E349.0.5.0", {"center": v(275.35, 177.3) * mm, "radius": 5.5 * mm});
            skCircle(sketch, "E349.0.6.0", {"center": v(275.35, 253.5) * mm, "radius": 5.5 * mm});
            skCircle(sketch, "E349.0.7.0", {"center": v(275.35, 329.7) * mm, "radius": 5.5 * mm});
            skCircle(sketch, "E349.0.8.0", {"center": v(275.35, 405.9) * mm, "radius": 5.5 * mm});
            skCircle(sketch, "E349.0.9.0", {"center": v(275.35, 482.1) * mm, "radius": 5.5 * mm});
            skCircle(sketch, "E349.0.10.0", {"center": v(275.35, 558.3) * mm, "radius": 5.5 * mm});
            skCircle(sketch, "E349.0.11.0", {"center": v(275.35, 634.5) * mm, "radius": 5.5 * mm});
            skCircle(sketch, "E349.0.12.0", {"center": v(275.35, 710.7) * mm, "radius": 5.5 * mm});
            skCircle(sketch, "E349.0.13.0", {"center": v(275.35, 786.9) * mm, "radius": 5.5 * mm});
            skCircle(sketch, "E349.0.14.0", {"center": v(275.35, 863.1) * mm, "radius": 5.5 * mm});
            skCircle(sketch, "E349.0.15.0", {"center": v(275.35, 939.3) * mm, "radius": 5.5 * mm});
            skCircle(sketch, "E349.0.16.0", {"center": v(275.35, 1015.5) * mm, "radius": 5.5 * mm});
            skCircle(sketch, "E349.0.17.0", {"center": v(275.35, 1091.7) * mm, "radius": 5.5 * mm});
            skCircle(sketch, "E349.0.18.0", {"center": v(275.35, 1167.9) * mm, "radius": 5.5 * mm});
            skCircle(sketch, "E349.0.19.0", {"center": v(275.35, 1244.1) * mm, "radius": 5.5 * mm});
            skCircle(sketch, "E349.0.20.0", {"center": v(275.35, 1320.3) * mm, "radius": 5.5 * mm});
            skCircle(sketch, "E349.0.21.0", {"center": v(275.35, 1396.5) * mm, "radius": 5.5 * mm});
            skCircle(sketch, "E349.0.22.0", {"center": v(275.35, 1472.7) * mm, "radius": 5.5 * mm});
            skCircle(sketch, "E349.0.23.0", {"center": v(275.35, 1548.9) * mm, "radius": 5.5 * mm});
            skCircle(sketch, "E349.0.24.0", {"center": v(275.35, 1625.1) * mm, "radius": 5.5 * mm});
            skCircle(sketch, "E349.0.25.0", {"center": v(275.35, 1701.3) * mm, "radius": 5.5 * mm});
            skCircle(sketch, "E349.0.26.0", {"center": v(275.35, 1777.5) * mm, "radius": 5.5 * mm});
            skCircle(sketch, "E349.0.27.0", {"center": v(275.35, 1853.7) * mm, "radius": 5.5 * mm});
            skCircle(sketch, "E349.0.28.0", {"center": v(275.35, 1929.9) * mm, "radius": 5.5 * mm});
            skCircle(sketch, "E349.0.29.0", {"center": v(275.35, 2006.1) * mm, "radius": 5.5 * mm});
            skCircle(sketch, "E349.0.30.0", {"center": v(275.35, 2082.3) * mm, "radius": 5.5 * mm});
            skCircle(sketch, "E349.0.31.0", {"center": v(275.35, 2158.5) * mm, "radius": 5.5 * mm});
            skCircle(sketch, "E349.0.32.0", {"center": v(275.35, 2234.7) * mm, "radius": 5.5 * mm});
            skCircle(sketch, "E349.0.33.0", {"center": v(275.35, 2310.9) * mm, "radius": 5.5 * mm});
            skCircle(sketch, "E349.0.34.0", {"center": v(275.35, 2387.1) * mm, "radius": 5.5 * mm});
            skCircle(sketch, "E349.0.35.0", {"center": v(275.35, 2463.3) * mm, "radius": 5.5 * mm});
            skCircle(sketch, "E349.0.36.0", {"center": v(275.35, 2539.5) * mm, "radius": 5.5 * mm});
            skCircle(sketch, "E349.0.37.0", {"center": v(275.35, 2615.7) * mm, "radius": 5.5 * mm});
            skCircle(sketch, "E349.0.38.0", {"center": v(275.35, 2691.9) * mm, "radius": 5.5 * mm});
            skCircle(sketch, "E349.0.39.0", {"center": v(275.35, 2768.1) * mm, "radius": 5.5 * mm});
            skCircle(sketch, "E349.0.40.0", {"center": v(275.35, 2844.3) * mm, "radius": 5.5 * mm});
            skCircle(sketch, "E349.0.41.0", {"center": v(275.35, 2920.5) * mm, "radius": 5.5 * mm});
            skCircle(sketch, "E349.0.42.0", {"center": v(275.35, 2996.7) * mm, "radius": 5.5 * mm});
            skCircle(sketch, "E349.0.43.0", {"center": v(275.35, 3072.9) * mm, "radius": 5.5 * mm});
            skCircle(sketch, "E349.0.44.0", {"center": v(275.35, 3149.1) * mm, "radius": 5.5 * mm});
            skCircle(sketch, "E349.0.45.0", {"center": v(275.35, 3225.3) * mm, "radius": 5.5 * mm});
            skCircle(sketch, "E349.0.46.0", {"center": v(275.35, 3301.5) * mm, "radius": 5.5 * mm});
            skCircle(sketch, "E349.0.47.0", {"center": v(275.35, 3377.7) * mm, "radius": 5.5 * mm});
            skCircle(sketch, "E349.0.48.0", {"center": v(275.35, 3453.9) * mm, "radius": 5.5 * mm});
            skCircle(sketch, "E349.0.49.0", {"center": v(275.35, 3530.1) * mm, "radius": 5.5 * mm});
            skCircle(sketch, "E349.0.50.0", {"center": v(275.35, 3606.3) * mm, "radius": 5.5 * mm});
            skCircle(sketch, "E349.0.51.0", {"center": v(275.35, 3682.5) * mm, "radius": 5.5 * mm});
            skCircle(sketch, "E349.0.52.0", {"center": v(275.35, 3758.7) * mm, "radius": 5.5 * mm});
            skCircle(sketch, "E349.0.53.0", {"center": v(275.35, 3834.9) * mm, "radius": 5.5 * mm});
            skCircle(sketch, "E349.0.54.0", {"center": v(275.35, 3911.1) * mm, "radius": 5.5 * mm});
            skCircle(sketch, "E349.0.55.0", {"center": v(275.35, 3987.3) * mm, "radius": 5.5 * mm});
            skCircle(sketch, "E349.0.56.0", {"center": v(275.35, 4063.5) * mm, "radius": 5.5 * mm});
            skCircle(sketch, "E349.0.57.0", {"center": v(275.35, 4139.7) * mm, "radius": 5.5 * mm});
            skCircle(sketch, "E349.0.58.0", {"center": v(275.35, 4215.9) * mm, "radius": 5.5 * mm});
            skCircle(sketch, "E349.0.59.0", {"center": v(275.35, 4292.1) * mm, "radius": 5.5 * mm});
            skCircle(sketch, "E349.0.60.0", {"center": v(275.35, 4368.3) * mm, "radius": 5.5 * mm});
            skCircle(sketch, "E349.0.61.0", {"center": v(275.35, 4444.5) * mm, "radius": 5.5 * mm});
            skCircle(sketch, "E349.0.62.0", {"center": v(275.35, 4520.7) * mm, "radius": 5.5 * mm});
            skCircle(sketch, "E349.0.63.0", {"center": v(275.35, 4596.9) * mm, "radius": 5.5 * mm});
            skCircle(sketch, "E349.0.64.0", {"center": v(275.35, 4673.1) * mm, "radius": 5.5 * mm});
            skCircle(sketch, "E349.0.65.0", {"center": v(275.35, 4749.3) * mm, "radius": 5.5 * mm});
            skCircle(sketch, "E349.0.66.0", {"center": v(275.35, 4825.5) * mm, "radius": 5.5 * mm});
            skCircle(sketch, "E349.0.67.0", {"center": v(275.35, 4901.7) * mm, "radius": 5.5 * mm});
            skCircle(sketch, "E349.0.68.0", {"center": v(275.35, 4977.9) * mm, "radius": 5.5 * mm});
            skCircle(sketch, "E349.0.69.0", {"center": v(275.35, 5054.1) * mm, "radius": 5.5 * mm});
            skCircle(sketch, "E349.0.70.0", {"center": v(275.35, 5130.3) * mm, "radius": 5.5 * mm});
            skCircle(sketch, "E349.0.71.0", {"center": v(275.35, 5206.5) * mm, "radius": 5.5 * mm});
            skCircle(sketch, "E349.0.72.0", {"center": v(275.35, 5282.7) * mm, "radius": 5.5 * mm});
            skCircle(sketch, "E349.0.73.0", {"center": v(275.35, 5358.9) * mm, "radius": 5.5 * mm});
            skCircle(sketch, "E349.0.74.0", {"center": v(275.35, 5435.1) * mm, "radius": 5.5 * mm});
            skCircle(sketch, "E349.0.75.0", {"center": v(275.35, 5511.3) * mm, "radius": 5.5 * mm});
            skCircle(sketch, "E349.0.76.0", {"center": v(275.35, 5587.5) * mm, "radius": 5.5 * mm});
            skCircle(sketch, "E349.0.77.0", {"center": v(275.35, 5663.7) * mm, "radius": 5.5 * mm});
            skCircle(sketch, "E349.0.78.0", {"center": v(275.35, 5739.9) * mm, "radius": 5.5 * mm});
            skCircle(sketch, "E349.0.79.0", {"center": v(275.35, 5816.1) * mm, "radius": 5.5 * mm});
            skCircle(sketch, "E349.0.80.0", {"center": v(275.35, 5892.3) * mm, "radius": 5.5 * mm});
            skLineSegment(sketch, "E349.direction1", {"start": v(275.35, -203.7) * mm, "end": v(300.35, -203.7) * mm, "construction": true});
            skLineSegment(sketch, "E349.direction2", {"start": v(275.35, -203.7) * mm, "end": v(275.35, -127.5) * mm, "construction": true});
            skSolve(sketch);
        }
        {
            var Q0;
            Q0=sQuery(id+"F7.wireOp",VERTEX,"E349.0.80.0.center");
            var Q1;
            Q1=sQuery(id+"F7.wireOp",VERTEX,"E349.0.79.0.center");
            var Q2;
            Q2=sQuery(id+"F7.wireOp",VERTEX,"E349.0.78.0.center");
            var Q3;
            Q3=sQuery(id+"F7.wireOp",VERTEX,"E349.0.77.0.center");
            var Q4;
            Q4=sQuery(id+"F7.wireOp",VERTEX,"E349.0.76.0.center");
            var Q5;
            Q5=sQuery(id+"F7.wireOp",VERTEX,"E349.0.75.0.center");
            var Q6;
            Q6=sQuery(id+"F7.wireOp",VERTEX,"E349.0.74.0.center");
            var Q7;
            Q7=sQuery(id+"F7.wireOp",VERTEX,"E349.0.73.0.center");
            var Q8;
            Q8=sQuery(id+"F7.wireOp",VERTEX,"E349.0.72.0.center");
            var Q9;
            Q9=sQuery(id+"F7.wireOp",VERTEX,"E349.0.71.0.center");
            var Q10;
            Q10=sQuery(id+"F7.wireOp",VERTEX,"E349.0.70.0.center");
            var Q11;
            Q11=sQuery(id+"F7.wireOp",VERTEX,"E349.0.69.0.center");
            var Q12;
            Q12=sQuery(id+"F7.wireOp",VERTEX,"E349.0.68.0.center");
            var Q13;
            Q13=sQuery(id+"F7.wireOp",VERTEX,"E349.0.67.0.center");
            var Q14;
            Q14=sQuery(id+"F7.wireOp",VERTEX,"E349.0.66.0.center");
            var Q15;
            Q15=sQuery(id+"F7.wireOp",VERTEX,"E349.0.65.0.center");
            var Q16;
            Q16=sQuery(id+"F7.wireOp",VERTEX,"E349.0.64.0.center");
            var Q17;
            Q17=sQuery(id+"F7.wireOp",VERTEX,"E349.0.63.0.center");
            var Q18;
            Q18=sQuery(id+"F7.wireOp",VERTEX,"E349.0.62.0.center");
            var Q19;
            Q19=sQuery(id+"F7.wireOp",VERTEX,"E349.0.61.0.center");
            var Q20;
            Q20=sQuery(id+"F7.wireOp",VERTEX,"E349.0.60.0.center");
            var Q21;
            Q21=sQuery(id+"F7.wireOp",VERTEX,"E349.0.59.0.center");
            var Q22;
            Q22=sQuery(id+"F7.wireOp",VERTEX,"E349.0.58.0.center");
            var Q23;
            Q23=sQuery(id+"F7.wireOp",VERTEX,"E349.0.57.0.center");
            var Q24;
            Q24=sQuery(id+"F7.wireOp",VERTEX,"E349.0.56.0.center");
            var Q25;
            Q25=sQuery(id+"F7.wireOp",VERTEX,"E349.0.55.0.center");
            var Q26;
            Q26=sQuery(id+"F7.wireOp",VERTEX,"E349.0.54.0.center");
            var Q27;
            Q27=sQuery(id+"F7.wireOp",VERTEX,"E349.0.53.0.center");
            var Q28;
            Q28=sQuery(id+"F7.wireOp",VERTEX,"E349.0.52.0.center");
            var Q29;
            Q29=sQuery(id+"F7.wireOp",VERTEX,"E349.0.51.0.center");
            var Q30;
            Q30=sQuery(id+"F7.wireOp",VERTEX,"E349.0.50.0.center");
            var Q31;
            Q31=sQuery(id+"F7.wireOp",VERTEX,"E349.0.49.0.center");
            var Q32;
            Q32=sQuery(id+"F7.wireOp",VERTEX,"E349.0.48.0.center");
            var Q33;
            Q33=sQuery(id+"F7.wireOp",VERTEX,"E349.0.47.0.center");
            var Q34;
            Q34=sQuery(id+"F7.wireOp",VERTEX,"E349.0.46.0.center");
            var Q35;
            Q35=sQuery(id+"F7.wireOp",VERTEX,"E349.0.45.0.center");
            var Q36;
            Q36=sQuery(id+"F7.wireOp",VERTEX,"E349.0.44.0.center");
            var Q37;
            Q37=sQuery(id+"F7.wireOp",VERTEX,"E349.0.43.0.center");
            var Q38;
            Q38=sQuery(id+"F7.wireOp",VERTEX,"E349.0.42.0.center");
            var Q39;
            Q39=sQuery(id+"F7.wireOp",VERTEX,"E349.0.41.0.center");
            var Q40;
            Q40=sQuery(id+"F7.wireOp",VERTEX,"E349.0.40.0.center");
            var Q41;
            Q41=sQuery(id+"F7.wireOp",VERTEX,"E349.0.39.0.center");
            var Q42;
            Q42=sQuery(id+"F7.wireOp",VERTEX,"E349.0.38.0.center");
            var Q43;
            Q43=sQuery(id+"F7.wireOp",VERTEX,"E349.0.37.0.center");
            var Q44;
            Q44=sQuery(id+"F7.wireOp",VERTEX,"E349.0.36.0.center");
            var Q45;
            Q45=sQuery(id+"F7.wireOp",VERTEX,"E349.0.35.0.center");
            var Q46;
            Q46=sQuery(id+"F7.wireOp",VERTEX,"E349.0.34.0.center");
            var Q47;
            Q47=sQuery(id+"F7.wireOp",VERTEX,"E349.0.33.0.center");
            var Q48;
            Q48=sQuery(id+"F7.wireOp",VERTEX,"E349.0.32.0.center");
            var Q49;
            Q49=sQuery(id+"F7.wireOp",VERTEX,"E349.0.31.0.center");
            var Q50;
            Q50=sQuery(id+"F7.wireOp",VERTEX,"E349.0.30.0.center");
            var Q51;
            Q51=sQuery(id+"F7.wireOp",VERTEX,"E349.0.29.0.center");
            var Q52;
            Q52=sQuery(id+"F7.wireOp",VERTEX,"E349.0.28.0.center");
            var Q53;
            Q53=sQuery(id+"F7.wireOp",VERTEX,"E349.0.27.0.center");
            var Q54;
            Q54=sQuery(id+"F7.wireOp",VERTEX,"E349.0.26.0.center");
            var Q55;
            Q55=sQuery(id+"F7.wireOp",VERTEX,"E349.0.25.0.center");
            var Q56;
            Q56=sQuery(id+"F7.wireOp",VERTEX,"E349.0.24.0.center");
            var Q57;
            Q57=sQuery(id+"F7.wireOp",VERTEX,"E349.0.23.0.center");
            var Q58;
            Q58=sQuery(id+"F7.wireOp",VERTEX,"E349.0.22.0.center");
            var Q59;
            Q59=sQuery(id+"F7.wireOp",VERTEX,"E349.0.21.0.center");
            var Q60;
            Q60=sQuery(id+"F7.wireOp",VERTEX,"E349.0.20.0.center");
            var Q61;
            Q61=sQuery(id+"F7.wireOp",VERTEX,"E349.0.19.0.center");
            var Q62;
            Q62=sQuery(id+"F7.wireOp",VERTEX,"E349.0.18.0.center");
            var Q63;
            Q63=sQuery(id+"F7.wireOp",VERTEX,"E349.0.17.0.center");
            var Q64;
            Q64=sQuery(id+"F7.wireOp",VERTEX,"E349.0.16.0.center");
            var Q65;
            Q65=sQuery(id+"F7.wireOp",VERTEX,"E349.0.15.0.center");
            var Q66;
            Q66=sQuery(id+"F7.wireOp",VERTEX,"E349.0.14.0.center");
            var Q67;
            Q67=sQuery(id+"F7.wireOp",VERTEX,"E349.0.13.0.center");
            var Q68;
            Q68=sQuery(id+"F7.wireOp",VERTEX,"E349.0.12.0.center");
            var Q69;
            Q69=sQuery(id+"F7.wireOp",VERTEX,"E349.0.11.0.center");
            var Q70;
            Q70=sQuery(id+"F7.wireOp",VERTEX,"E349.0.10.0.center");
            var Q71;
            Q71=sQuery(id+"F7.wireOp",VERTEX,"E349.0.9.0.center");
            var Q72;
            Q72=sQuery(id+"F7.wireOp",VERTEX,"E349.0.8.0.center");
            var Q73;
            Q73=sQuery(id+"F7.wireOp",VERTEX,"E349.0.7.0.center");
            var Q74;
            Q74=sQuery(id+"F7.wireOp",VERTEX,"E349.0.6.0.center");
            var Q75;
            Q75=sQuery(id+"F7.wireOp",VERTEX,"E349.0.5.0.center");
            var Q76;
            Q76=sQuery(id+"F7.wireOp",VERTEX,"E349.0.4.0.center");
            var Q77;
            Q77=sQuery(id+"F7.wireOp",VERTEX,"E349.0.3.0.center");
            var Q78;
            Q78=sQuery(id+"F7.wireOp",VERTEX,"E349.0.2.0.center");
            var Q79;
            Q79=sQuery(id+"F7.wireOp",VERTEX,"E349.direction2.end");
            var Q80;
            Q80=sQuery(id+"F7.wireOp",VERTEX,"E349.direction1.start");
            var Q81;
            Q81=makeQuery(id+"F1.opExtrude","SWEPT_BODY",BODY,{"disambiguationData":[OSD([sQuery(id+"F0.wireOp",EDGE,"E264"),sQuery(id+"F0.wireOp",EDGE,"E265"),sQuery(id+"F0.wireOp",EDGE,"E266"),sQuery(id+"F0.wireOp",EDGE,"E267"),sQuery(id+"F0.wireOp",EDGE,"E268"),sQuery(id+"F0.wireOp",EDGE,"E269"),sQuery(id+"F0.wireOp",EDGE,"E270"),sQuery(id+"F0.wireOp",EDGE,"E271"),sQuery(id+"F0.wireOp",EDGE,"E275"),sQuery(id+"F0.wireOp",EDGE,"E276"),sQuery(id+"F0.wireOp",EDGE,"E277"),sQuery(id+"F0.wireOp",EDGE,"E278"),sQuery(id+"F0.wireOp",EDGE,"E279"),sQuery(id+"F0.wireOp",EDGE,"E280"),sQuery(id+"F0.wireOp",EDGE,"E281"),sQuery(id+"F0.wireOp",EDGE,"E282"),sQuery(id+"F0.wireOp",EDGE,"E283"),sQuery(id+"F0.wireOp",EDGE,"E284"),sQuery(id+"F0.wireOp",EDGE,"E285"),sQuery(id+"F0.wireOp",EDGE,"E286"),sQuery(id+"F0.wireOp",EDGE,"E287"),sQuery(id+"F0.wireOp",EDGE,"E288"),sQuery(id+"F0.wireOp",EDGE,"E289"),sQuery(id+"F0.wireOp",EDGE,"E290"),sQuery(id+"F0.wireOp",EDGE,"E291"),sQuery(id+"F0.wireOp",EDGE,"E292"),sQuery(id+"F0.wireOp",EDGE,"E293"),sQuery(id+"F0.wireOp",EDGE,"E294"),sQuery(id+"F0.wireOp",EDGE,"E295"),sQuery(id+"F0.wireOp",EDGE,"E296"),sQuery(id+"F0.wireOp",EDGE,"E297"),sQuery(id+"F0.wireOp",EDGE,"E298"),sQuery(id+"F0.wireOp",EDGE,"E299"),sQuery(id+"F0.wireOp",EDGE,"E300"),sQuery(id+"F0.wireOp",EDGE,"E301"),sQuery(id+"F0.wireOp",EDGE,"E302"),sQuery(id+"F0.wireOp",EDGE,"E303"),sQuery(id+"F0.wireOp",EDGE,"E304"),sQuery(id+"F0.wireOp",EDGE,"E305"),sQuery(id+"F0.wireOp",EDGE,"E306"),sQuery(id+"F0.wireOp",EDGE,"E307"),sQuery(id+"F0.wireOp",EDGE,"E308"),sQuery(id+"F0.wireOp",EDGE,"E309"),sQuery(id+"F0.wireOp",EDGE,"E310"),sQuery(id+"F0.wireOp",EDGE,"E311"),sQuery(id+"F0.wireOp",EDGE,"E312"),sQuery(id+"F0.wireOp",EDGE,"E313"),sQuery(id+"F0.wireOp",EDGE,"E314"),sQuery(id+"F0.wireOp",EDGE,"E315"),sQuery(id+"F0.wireOp",EDGE,"E316"),sQuery(id+"F0.wireOp",EDGE,"E317"),sQuery(id+"F0.wireOp",EDGE,"E318")])]});
            hole(context, id + "F8", {"style" : HoleStyle.SIMPLE, "endStyle" : HoleEndStyle.THROUGH, "holeDiameter" : 11 * mm, "majorDiameter" : 5 * mm, "isTappedThrough" : true, "tappedDepth" : 12 * mm, "tapClearance" : 3, "locations" : qUnion([Q0, Q1, Q2, Q3, Q4, Q5, Q6, Q7, Q8, Q9, Q10, Q11, Q12, Q13, Q14, Q15, Q16, Q17, Q18, Q19, Q20, Q21, Q22, Q23, Q24, Q25, Q26, Q27, Q28, Q29, Q30, Q31, Q32, Q33, Q34, Q35, Q36, Q37, Q38, Q39, Q40, Q41, Q42, Q43, Q44, Q45, Q46, Q47, Q48, Q49, Q50, Q51, Q52, Q53, Q54, Q55, Q56, Q57, Q58, Q59, Q60, Q61, Q62, Q63, Q64, Q65, Q66, Q67, Q68, Q69, Q70, Q71, Q72, Q73, Q74, Q75, Q76, Q77, Q78, Q79, Q80]), "scope" : qUnion([Q81])});
        }
    });
